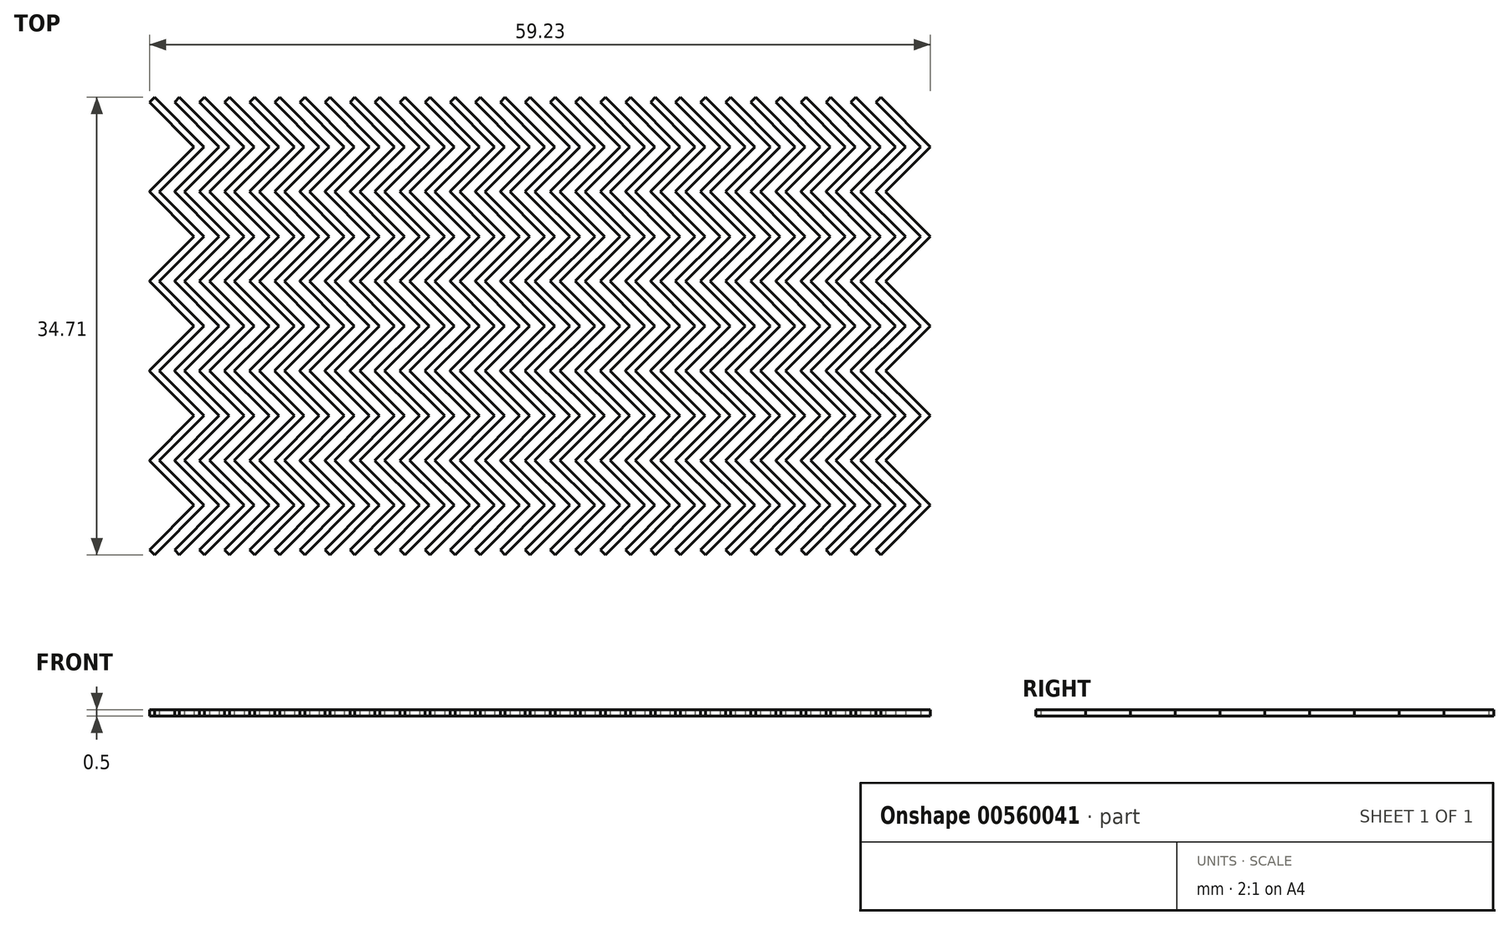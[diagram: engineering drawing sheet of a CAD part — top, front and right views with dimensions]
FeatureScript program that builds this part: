
annotation { "Feature Type Name" : "Feature", "Feature Type Description" : "" }
export const myFeature = defineFeature(function(context is Context, id is Id, definition is map)
    precondition{}
    {
        {
            var Q0;
            Q0=qCreatedBy(makeId("Top.planeOp"),FACE);
            var sketch = newSketch(context, id + "F0", { "sketchPlane" : qUnion([Q0])});
            skLineSegment(sketch, "E0.bottom", {"start": v(-22.51, 20.26) * mm, "end": v(-22.89, 19.88) * mm});
            skLineSegment(sketch, "E0.top", {"start": v(-26.27, 24.01) * mm, "end": v(-26.64, 23.64) * mm});
            skLineSegment(sketch, "E0.left", {"start": v(-22.51, 20.26) * mm, "end": v(-26.27, 24.01) * mm});
            skLineSegment(sketch, "E0.right", {"start": v(-22.89, 19.88) * mm, "end": v(-26.64, 23.64) * mm});
            skPoint(sketch, "E0.middle", {"position": v(-24.58, 21.95) * mm});
            skLineSegment(sketch, "E1.bottom", {"start": v(-22.89, 20.63) * mm, "end": v(-22.51, 20.26) * mm});
            skLineSegment(sketch, "E1.top", {"start": v(-26.64, 16.88) * mm, "end": v(-26.27, 16.5) * mm});
            skLineSegment(sketch, "E1.left", {"start": v(-22.89, 20.63) * mm, "end": v(-26.64, 16.88) * mm});
            skLineSegment(sketch, "E1.right", {"start": v(-22.51, 20.26) * mm, "end": v(-26.27, 16.5) * mm});
            skPoint(sketch, "E1.middle", {"position": v(-24.58, 18.57) * mm});
            skLineSegment(sketch, "E2.1.0.0", {"start": v(-20.61, 20.26) * mm, "end": v(-24.37, 24.01) * mm});
            skLineSegment(sketch, "E2.1.0.1", {"start": v(-20.99, 19.88) * mm, "end": v(-24.74, 23.64) * mm});
            skPoint(sketch, "E2.1.0.2", {"position": v(-22.68, 18.57) * mm});
            skLineSegment(sketch, "E2.1.0.3", {"start": v(-20.99, 20.63) * mm, "end": v(-24.74, 16.88) * mm});
            skPoint(sketch, "E2.1.0.4", {"position": v(-22.68, 21.95) * mm});
            skLineSegment(sketch, "E2.1.0.5", {"start": v(-20.61, 20.26) * mm, "end": v(-24.37, 16.5) * mm});
            skLineSegment(sketch, "E2.1.0.6", {"start": v(-24.37, 24.01) * mm, "end": v(-24.74, 23.64) * mm});
            skLineSegment(sketch, "E2.1.0.7", {"start": v(-24.74, 16.88) * mm, "end": v(-24.37, 16.5) * mm});
            skLineSegment(sketch, "E2.1.0.8", {"start": v(-20.61, 20.26) * mm, "end": v(-20.99, 19.88) * mm});
            skLineSegment(sketch, "E2.1.0.9", {"start": v(-20.99, 20.63) * mm, "end": v(-20.61, 20.26) * mm});
            skLineSegment(sketch, "E2.2.0.0", {"start": v(-18.71, 20.26) * mm, "end": v(-22.47, 24.01) * mm});
            skLineSegment(sketch, "E2.2.0.1", {"start": v(-19.09, 19.88) * mm, "end": v(-22.84, 23.64) * mm});
            skPoint(sketch, "E2.2.0.2", {"position": v(-20.78, 18.57) * mm});
            skLineSegment(sketch, "E2.2.0.3", {"start": v(-19.09, 20.63) * mm, "end": v(-22.84, 16.88) * mm});
            skPoint(sketch, "E2.2.0.4", {"position": v(-20.78, 21.95) * mm});
            skLineSegment(sketch, "E2.2.0.5", {"start": v(-18.71, 20.26) * mm, "end": v(-22.47, 16.5) * mm});
            skLineSegment(sketch, "E2.2.0.6", {"start": v(-22.47, 24.01) * mm, "end": v(-22.84, 23.64) * mm});
            skLineSegment(sketch, "E2.2.0.7", {"start": v(-22.84, 16.88) * mm, "end": v(-22.47, 16.5) * mm});
            skLineSegment(sketch, "E2.2.0.8", {"start": v(-18.71, 20.26) * mm, "end": v(-19.09, 19.88) * mm});
            skLineSegment(sketch, "E2.2.0.9", {"start": v(-19.09, 20.63) * mm, "end": v(-18.71, 20.26) * mm});
            skLineSegment(sketch, "E2.3.0.0", {"start": v(-16.81, 20.26) * mm, "end": v(-20.57, 24.01) * mm});
            skLineSegment(sketch, "E2.3.0.1", {"start": v(-17.19, 19.88) * mm, "end": v(-20.94, 23.64) * mm});
            skPoint(sketch, "E2.3.0.2", {"position": v(-18.88, 18.57) * mm});
            skLineSegment(sketch, "E2.3.0.3", {"start": v(-17.19, 20.63) * mm, "end": v(-20.94, 16.88) * mm});
            skPoint(sketch, "E2.3.0.4", {"position": v(-18.88, 21.95) * mm});
            skLineSegment(sketch, "E2.3.0.5", {"start": v(-16.81, 20.26) * mm, "end": v(-20.57, 16.5) * mm});
            skLineSegment(sketch, "E2.3.0.6", {"start": v(-20.57, 24.01) * mm, "end": v(-20.94, 23.64) * mm});
            skLineSegment(sketch, "E2.3.0.7", {"start": v(-20.94, 16.88) * mm, "end": v(-20.57, 16.5) * mm});
            skLineSegment(sketch, "E2.3.0.8", {"start": v(-16.81, 20.26) * mm, "end": v(-17.19, 19.88) * mm});
            skLineSegment(sketch, "E2.3.0.9", {"start": v(-17.19, 20.63) * mm, "end": v(-16.81, 20.26) * mm});
            skLineSegment(sketch, "E2.4.0.0", {"start": v(-14.91, 20.26) * mm, "end": v(-18.67, 24.01) * mm});
            skLineSegment(sketch, "E2.4.0.1", {"start": v(-15.29, 19.88) * mm, "end": v(-19.04, 23.64) * mm});
            skPoint(sketch, "E2.4.0.2", {"position": v(-16.98, 18.57) * mm});
            skLineSegment(sketch, "E2.4.0.3", {"start": v(-15.29, 20.63) * mm, "end": v(-19.04, 16.88) * mm});
            skPoint(sketch, "E2.4.0.4", {"position": v(-16.98, 21.95) * mm});
            skLineSegment(sketch, "E2.4.0.5", {"start": v(-14.91, 20.26) * mm, "end": v(-18.67, 16.5) * mm});
            skLineSegment(sketch, "E2.4.0.6", {"start": v(-18.67, 24.01) * mm, "end": v(-19.04, 23.64) * mm});
            skLineSegment(sketch, "E2.4.0.7", {"start": v(-19.04, 16.88) * mm, "end": v(-18.67, 16.5) * mm});
            skLineSegment(sketch, "E2.4.0.8", {"start": v(-14.91, 20.26) * mm, "end": v(-15.29, 19.88) * mm});
            skLineSegment(sketch, "E2.4.0.9", {"start": v(-15.29, 20.63) * mm, "end": v(-14.91, 20.26) * mm});
            skLineSegment(sketch, "E2.5.0.0", {"start": v(-13.01, 20.26) * mm, "end": v(-16.77, 24.01) * mm});
            skLineSegment(sketch, "E2.5.0.1", {"start": v(-13.39, 19.88) * mm, "end": v(-17.14, 23.64) * mm});
            skPoint(sketch, "E2.5.0.2", {"position": v(-15.08, 18.57) * mm});
            skLineSegment(sketch, "E2.5.0.3", {"start": v(-13.39, 20.63) * mm, "end": v(-17.14, 16.88) * mm});
            skPoint(sketch, "E2.5.0.4", {"position": v(-15.08, 21.95) * mm});
            skLineSegment(sketch, "E2.5.0.5", {"start": v(-13.01, 20.26) * mm, "end": v(-16.77, 16.5) * mm});
            skLineSegment(sketch, "E2.5.0.6", {"start": v(-16.77, 24.01) * mm, "end": v(-17.14, 23.64) * mm});
            skLineSegment(sketch, "E2.5.0.7", {"start": v(-17.14, 16.88) * mm, "end": v(-16.77, 16.5) * mm});
            skLineSegment(sketch, "E2.5.0.8", {"start": v(-13.01, 20.26) * mm, "end": v(-13.39, 19.88) * mm});
            skLineSegment(sketch, "E2.5.0.9", {"start": v(-13.39, 20.63) * mm, "end": v(-13.01, 20.26) * mm});
            skLineSegment(sketch, "E2.6.0.0", {"start": v(-11.11, 20.26) * mm, "end": v(-14.87, 24.01) * mm});
            skLineSegment(sketch, "E2.6.0.1", {"start": v(-11.49, 19.88) * mm, "end": v(-15.24, 23.64) * mm});
            skPoint(sketch, "E2.6.0.2", {"position": v(-13.18, 18.57) * mm});
            skLineSegment(sketch, "E2.6.0.3", {"start": v(-11.49, 20.63) * mm, "end": v(-15.24, 16.88) * mm});
            skPoint(sketch, "E2.6.0.4", {"position": v(-13.18, 21.95) * mm});
            skLineSegment(sketch, "E2.6.0.5", {"start": v(-11.11, 20.26) * mm, "end": v(-14.87, 16.5) * mm});
            skLineSegment(sketch, "E2.6.0.6", {"start": v(-14.87, 24.01) * mm, "end": v(-15.24, 23.64) * mm});
            skLineSegment(sketch, "E2.6.0.7", {"start": v(-15.24, 16.88) * mm, "end": v(-14.87, 16.5) * mm});
            skLineSegment(sketch, "E2.6.0.8", {"start": v(-11.11, 20.26) * mm, "end": v(-11.49, 19.88) * mm});
            skLineSegment(sketch, "E2.6.0.9", {"start": v(-11.49, 20.63) * mm, "end": v(-11.11, 20.26) * mm});
            skLineSegment(sketch, "E2.7.0.0", {"start": v(-9.21, 20.26) * mm, "end": v(-12.97, 24.01) * mm});
            skLineSegment(sketch, "E2.7.0.1", {"start": v(-9.59, 19.88) * mm, "end": v(-13.34, 23.64) * mm});
            skPoint(sketch, "E2.7.0.2", {"position": v(-11.28, 18.57) * mm});
            skLineSegment(sketch, "E2.7.0.3", {"start": v(-9.59, 20.63) * mm, "end": v(-13.34, 16.88) * mm});
            skPoint(sketch, "E2.7.0.4", {"position": v(-11.28, 21.95) * mm});
            skLineSegment(sketch, "E2.7.0.5", {"start": v(-9.21, 20.26) * mm, "end": v(-12.97, 16.5) * mm});
            skLineSegment(sketch, "E2.7.0.6", {"start": v(-12.97, 24.01) * mm, "end": v(-13.34, 23.64) * mm});
            skLineSegment(sketch, "E2.7.0.7", {"start": v(-13.34, 16.88) * mm, "end": v(-12.97, 16.5) * mm});
            skLineSegment(sketch, "E2.7.0.8", {"start": v(-9.21, 20.26) * mm, "end": v(-9.59, 19.88) * mm});
            skLineSegment(sketch, "E2.7.0.9", {"start": v(-9.59, 20.63) * mm, "end": v(-9.21, 20.26) * mm});
            skLineSegment(sketch, "E2.8.0.0", {"start": v(-7.31, 20.26) * mm, "end": v(-11.07, 24.01) * mm});
            skLineSegment(sketch, "E2.8.0.1", {"start": v(-7.69, 19.88) * mm, "end": v(-11.44, 23.64) * mm});
            skPoint(sketch, "E2.8.0.2", {"position": v(-9.38, 18.57) * mm});
            skLineSegment(sketch, "E2.8.0.3", {"start": v(-7.69, 20.63) * mm, "end": v(-11.44, 16.88) * mm});
            skPoint(sketch, "E2.8.0.4", {"position": v(-9.38, 21.95) * mm});
            skLineSegment(sketch, "E2.8.0.5", {"start": v(-7.31, 20.26) * mm, "end": v(-11.07, 16.5) * mm});
            skLineSegment(sketch, "E2.8.0.6", {"start": v(-11.07, 24.01) * mm, "end": v(-11.44, 23.64) * mm});
            skLineSegment(sketch, "E2.8.0.7", {"start": v(-11.44, 16.88) * mm, "end": v(-11.07, 16.5) * mm});
            skLineSegment(sketch, "E2.8.0.8", {"start": v(-7.31, 20.26) * mm, "end": v(-7.69, 19.88) * mm});
            skLineSegment(sketch, "E2.8.0.9", {"start": v(-7.69, 20.63) * mm, "end": v(-7.31, 20.26) * mm});
            skLineSegment(sketch, "E2.9.0.0", {"start": v(-5.41, 20.26) * mm, "end": v(-9.17, 24.01) * mm});
            skLineSegment(sketch, "E2.9.0.1", {"start": v(-5.79, 19.88) * mm, "end": v(-9.54, 23.64) * mm});
            skPoint(sketch, "E2.9.0.2", {"position": v(-7.48, 18.57) * mm});
            skLineSegment(sketch, "E2.9.0.3", {"start": v(-5.79, 20.63) * mm, "end": v(-9.54, 16.88) * mm});
            skPoint(sketch, "E2.9.0.4", {"position": v(-7.48, 21.95) * mm});
            skLineSegment(sketch, "E2.9.0.5", {"start": v(-5.41, 20.26) * mm, "end": v(-9.17, 16.5) * mm});
            skLineSegment(sketch, "E2.9.0.6", {"start": v(-9.17, 24.01) * mm, "end": v(-9.54, 23.64) * mm});
            skLineSegment(sketch, "E2.9.0.7", {"start": v(-9.54, 16.88) * mm, "end": v(-9.17, 16.5) * mm});
            skLineSegment(sketch, "E2.9.0.8", {"start": v(-5.41, 20.26) * mm, "end": v(-5.79, 19.88) * mm});
            skLineSegment(sketch, "E2.9.0.9", {"start": v(-5.79, 20.63) * mm, "end": v(-5.41, 20.26) * mm});
            skLineSegment(sketch, "E2.10.0.0", {"start": v(-3.51, 20.26) * mm, "end": v(-7.27, 24.01) * mm});
            skLineSegment(sketch, "E2.10.0.1", {"start": v(-3.89, 19.88) * mm, "end": v(-7.64, 23.64) * mm});
            skPoint(sketch, "E2.10.0.2", {"position": v(-5.58, 18.57) * mm});
            skLineSegment(sketch, "E2.10.0.3", {"start": v(-3.89, 20.63) * mm, "end": v(-7.64, 16.88) * mm});
            skPoint(sketch, "E2.10.0.4", {"position": v(-5.58, 21.95) * mm});
            skLineSegment(sketch, "E2.10.0.5", {"start": v(-3.51, 20.26) * mm, "end": v(-7.27, 16.5) * mm});
            skLineSegment(sketch, "E2.10.0.6", {"start": v(-7.27, 24.01) * mm, "end": v(-7.64, 23.64) * mm});
            skLineSegment(sketch, "E2.10.0.7", {"start": v(-7.64, 16.88) * mm, "end": v(-7.27, 16.5) * mm});
            skLineSegment(sketch, "E2.10.0.8", {"start": v(-3.51, 20.26) * mm, "end": v(-3.89, 19.88) * mm});
            skLineSegment(sketch, "E2.10.0.9", {"start": v(-3.89, 20.63) * mm, "end": v(-3.51, 20.26) * mm});
            skLineSegment(sketch, "E2.11.0.0", {"start": v(-1.61, 20.26) * mm, "end": v(-5.37, 24.01) * mm});
            skLineSegment(sketch, "E2.11.0.1", {"start": v(-1.99, 19.88) * mm, "end": v(-5.74, 23.64) * mm});
            skPoint(sketch, "E2.11.0.2", {"position": v(-3.68, 18.57) * mm});
            skLineSegment(sketch, "E2.11.0.3", {"start": v(-1.99, 20.63) * mm, "end": v(-5.74, 16.88) * mm});
            skPoint(sketch, "E2.11.0.4", {"position": v(-3.68, 21.95) * mm});
            skLineSegment(sketch, "E2.11.0.5", {"start": v(-1.61, 20.26) * mm, "end": v(-5.37, 16.5) * mm});
            skLineSegment(sketch, "E2.11.0.6", {"start": v(-5.37, 24.01) * mm, "end": v(-5.74, 23.64) * mm});
            skLineSegment(sketch, "E2.11.0.7", {"start": v(-5.74, 16.88) * mm, "end": v(-5.37, 16.5) * mm});
            skLineSegment(sketch, "E2.11.0.8", {"start": v(-1.61, 20.26) * mm, "end": v(-1.99, 19.88) * mm});
            skLineSegment(sketch, "E2.11.0.9", {"start": v(-1.99, 20.63) * mm, "end": v(-1.61, 20.26) * mm});
            skLineSegment(sketch, "E2.12.0.0", {"start": v(0.29, 20.26) * mm, "end": v(-3.47, 24.01) * mm});
            skLineSegment(sketch, "E2.12.0.1", {"start": v(-0.09, 19.88) * mm, "end": v(-3.84, 23.64) * mm});
            skPoint(sketch, "E2.12.0.2", {"position": v(-1.78, 18.57) * mm});
            skLineSegment(sketch, "E2.12.0.3", {"start": v(-0.09, 20.63) * mm, "end": v(-3.84, 16.88) * mm});
            skPoint(sketch, "E2.12.0.4", {"position": v(-1.78, 21.95) * mm});
            skLineSegment(sketch, "E2.12.0.5", {"start": v(0.29, 20.26) * mm, "end": v(-3.47, 16.5) * mm});
            skLineSegment(sketch, "E2.12.0.6", {"start": v(-3.47, 24.01) * mm, "end": v(-3.84, 23.64) * mm});
            skLineSegment(sketch, "E2.12.0.7", {"start": v(-3.84, 16.88) * mm, "end": v(-3.47, 16.5) * mm});
            skLineSegment(sketch, "E2.12.0.8", {"start": v(0.29, 20.26) * mm, "end": v(-0.09, 19.88) * mm});
            skLineSegment(sketch, "E2.12.0.9", {"start": v(-0.09, 20.63) * mm, "end": v(0.29, 20.26) * mm});
            skLineSegment(sketch, "E2.13.0.0", {"start": v(2.19, 20.26) * mm, "end": v(-1.57, 24.01) * mm});
            skLineSegment(sketch, "E2.13.0.1", {"start": v(1.81, 19.88) * mm, "end": v(-1.94, 23.64) * mm});
            skPoint(sketch, "E2.13.0.2", {"position": v(0.12, 18.57) * mm});
            skLineSegment(sketch, "E2.13.0.3", {"start": v(1.81, 20.63) * mm, "end": v(-1.94, 16.88) * mm});
            skPoint(sketch, "E2.13.0.4", {"position": v(0.12, 21.95) * mm});
            skLineSegment(sketch, "E2.13.0.5", {"start": v(2.19, 20.26) * mm, "end": v(-1.57, 16.5) * mm});
            skLineSegment(sketch, "E2.13.0.6", {"start": v(-1.57, 24.01) * mm, "end": v(-1.94, 23.64) * mm});
            skLineSegment(sketch, "E2.13.0.7", {"start": v(-1.94, 16.88) * mm, "end": v(-1.57, 16.5) * mm});
            skLineSegment(sketch, "E2.13.0.8", {"start": v(2.19, 20.26) * mm, "end": v(1.81, 19.88) * mm});
            skLineSegment(sketch, "E2.13.0.9", {"start": v(1.81, 20.63) * mm, "end": v(2.19, 20.26) * mm});
            skLineSegment(sketch, "E2.14.0.0", {"start": v(4.09, 20.26) * mm, "end": v(0.33, 24.01) * mm});
            skLineSegment(sketch, "E2.14.0.1", {"start": v(3.71, 19.88) * mm, "end": v(-0.04, 23.64) * mm});
            skPoint(sketch, "E2.14.0.2", {"position": v(2.02, 18.57) * mm});
            skLineSegment(sketch, "E2.14.0.3", {"start": v(3.71, 20.63) * mm, "end": v(-0.04, 16.88) * mm});
            skPoint(sketch, "E2.14.0.4", {"position": v(2.02, 21.95) * mm});
            skLineSegment(sketch, "E2.14.0.5", {"start": v(4.09, 20.26) * mm, "end": v(0.33, 16.5) * mm});
            skLineSegment(sketch, "E2.14.0.6", {"start": v(0.33, 24.01) * mm, "end": v(-0.04, 23.64) * mm});
            skLineSegment(sketch, "E2.14.0.7", {"start": v(-0.04, 16.88) * mm, "end": v(0.33, 16.5) * mm});
            skLineSegment(sketch, "E2.14.0.8", {"start": v(4.09, 20.26) * mm, "end": v(3.71, 19.88) * mm});
            skLineSegment(sketch, "E2.14.0.9", {"start": v(3.71, 20.63) * mm, "end": v(4.09, 20.26) * mm});
            skLineSegment(sketch, "E2.15.0.0", {"start": v(5.99, 20.26) * mm, "end": v(2.23, 24.01) * mm});
            skLineSegment(sketch, "E2.15.0.1", {"start": v(5.61, 19.88) * mm, "end": v(1.86, 23.64) * mm});
            skPoint(sketch, "E2.15.0.2", {"position": v(3.92, 18.57) * mm});
            skLineSegment(sketch, "E2.15.0.3", {"start": v(5.61, 20.63) * mm, "end": v(1.86, 16.88) * mm});
            skPoint(sketch, "E2.15.0.4", {"position": v(3.92, 21.95) * mm});
            skLineSegment(sketch, "E2.15.0.5", {"start": v(5.99, 20.26) * mm, "end": v(2.23, 16.5) * mm});
            skLineSegment(sketch, "E2.15.0.6", {"start": v(2.23, 24.01) * mm, "end": v(1.86, 23.64) * mm});
            skLineSegment(sketch, "E2.15.0.7", {"start": v(1.86, 16.88) * mm, "end": v(2.23, 16.5) * mm});
            skLineSegment(sketch, "E2.15.0.8", {"start": v(5.99, 20.26) * mm, "end": v(5.61, 19.88) * mm});
            skLineSegment(sketch, "E2.15.0.9", {"start": v(5.61, 20.63) * mm, "end": v(5.99, 20.26) * mm});
            skLineSegment(sketch, "E2.16.0.0", {"start": v(7.89, 20.26) * mm, "end": v(4.13, 24.01) * mm});
            skLineSegment(sketch, "E2.16.0.1", {"start": v(7.51, 19.88) * mm, "end": v(3.76, 23.64) * mm});
            skPoint(sketch, "E2.16.0.2", {"position": v(5.82, 18.57) * mm});
            skLineSegment(sketch, "E2.16.0.3", {"start": v(7.51, 20.63) * mm, "end": v(3.76, 16.88) * mm});
            skPoint(sketch, "E2.16.0.4", {"position": v(5.82, 21.95) * mm});
            skLineSegment(sketch, "E2.16.0.5", {"start": v(7.89, 20.26) * mm, "end": v(4.13, 16.5) * mm});
            skLineSegment(sketch, "E2.16.0.6", {"start": v(4.13, 24.01) * mm, "end": v(3.76, 23.64) * mm});
            skLineSegment(sketch, "E2.16.0.7", {"start": v(3.76, 16.88) * mm, "end": v(4.13, 16.5) * mm});
            skLineSegment(sketch, "E2.16.0.8", {"start": v(7.89, 20.26) * mm, "end": v(7.51, 19.88) * mm});
            skLineSegment(sketch, "E2.16.0.9", {"start": v(7.51, 20.63) * mm, "end": v(7.89, 20.26) * mm});
            skLineSegment(sketch, "E2.17.0.0", {"start": v(9.79, 20.26) * mm, "end": v(6.03, 24.01) * mm});
            skLineSegment(sketch, "E2.17.0.1", {"start": v(9.41, 19.88) * mm, "end": v(5.66, 23.64) * mm});
            skPoint(sketch, "E2.17.0.2", {"position": v(7.72, 18.57) * mm});
            skLineSegment(sketch, "E2.17.0.3", {"start": v(9.41, 20.63) * mm, "end": v(5.66, 16.88) * mm});
            skPoint(sketch, "E2.17.0.4", {"position": v(7.72, 21.95) * mm});
            skLineSegment(sketch, "E2.17.0.5", {"start": v(9.79, 20.26) * mm, "end": v(6.03, 16.5) * mm});
            skLineSegment(sketch, "E2.17.0.6", {"start": v(6.03, 24.01) * mm, "end": v(5.66, 23.64) * mm});
            skLineSegment(sketch, "E2.17.0.7", {"start": v(5.66, 16.88) * mm, "end": v(6.03, 16.5) * mm});
            skLineSegment(sketch, "E2.17.0.8", {"start": v(9.79, 20.26) * mm, "end": v(9.41, 19.88) * mm});
            skLineSegment(sketch, "E2.17.0.9", {"start": v(9.41, 20.63) * mm, "end": v(9.79, 20.26) * mm});
            skLineSegment(sketch, "E2.18.0.0", {"start": v(11.69, 20.26) * mm, "end": v(7.93, 24.01) * mm});
            skLineSegment(sketch, "E2.18.0.1", {"start": v(11.31, 19.88) * mm, "end": v(7.56, 23.64) * mm});
            skPoint(sketch, "E2.18.0.2", {"position": v(9.62, 18.57) * mm});
            skLineSegment(sketch, "E2.18.0.3", {"start": v(11.31, 20.63) * mm, "end": v(7.56, 16.88) * mm});
            skPoint(sketch, "E2.18.0.4", {"position": v(9.62, 21.95) * mm});
            skLineSegment(sketch, "E2.18.0.5", {"start": v(11.69, 20.26) * mm, "end": v(7.93, 16.5) * mm});
            skLineSegment(sketch, "E2.18.0.6", {"start": v(7.93, 24.01) * mm, "end": v(7.56, 23.64) * mm});
            skLineSegment(sketch, "E2.18.0.7", {"start": v(7.56, 16.88) * mm, "end": v(7.93, 16.5) * mm});
            skLineSegment(sketch, "E2.18.0.8", {"start": v(11.69, 20.26) * mm, "end": v(11.31, 19.88) * mm});
            skLineSegment(sketch, "E2.18.0.9", {"start": v(11.31, 20.63) * mm, "end": v(11.69, 20.26) * mm});
            skLineSegment(sketch, "E2.19.0.0", {"start": v(13.59, 20.26) * mm, "end": v(9.83, 24.01) * mm});
            skLineSegment(sketch, "E2.19.0.1", {"start": v(13.21, 19.88) * mm, "end": v(9.46, 23.64) * mm});
            skPoint(sketch, "E2.19.0.2", {"position": v(11.52, 18.57) * mm});
            skLineSegment(sketch, "E2.19.0.3", {"start": v(13.21, 20.63) * mm, "end": v(9.46, 16.88) * mm});
            skPoint(sketch, "E2.19.0.4", {"position": v(11.52, 21.95) * mm});
            skLineSegment(sketch, "E2.19.0.5", {"start": v(13.59, 20.26) * mm, "end": v(9.83, 16.5) * mm});
            skLineSegment(sketch, "E2.19.0.6", {"start": v(9.83, 24.01) * mm, "end": v(9.46, 23.64) * mm});
            skLineSegment(sketch, "E2.19.0.7", {"start": v(9.46, 16.88) * mm, "end": v(9.83, 16.5) * mm});
            skLineSegment(sketch, "E2.19.0.8", {"start": v(13.59, 20.26) * mm, "end": v(13.21, 19.88) * mm});
            skLineSegment(sketch, "E2.19.0.9", {"start": v(13.21, 20.63) * mm, "end": v(13.59, 20.26) * mm});
            skLineSegment(sketch, "E2.20.0.0", {"start": v(15.49, 20.26) * mm, "end": v(11.73, 24.01) * mm});
            skLineSegment(sketch, "E2.20.0.1", {"start": v(15.11, 19.88) * mm, "end": v(11.36, 23.64) * mm});
            skPoint(sketch, "E2.20.0.2", {"position": v(13.42, 18.57) * mm});
            skLineSegment(sketch, "E2.20.0.3", {"start": v(15.11, 20.63) * mm, "end": v(11.36, 16.88) * mm});
            skPoint(sketch, "E2.20.0.4", {"position": v(13.42, 21.95) * mm});
            skLineSegment(sketch, "E2.20.0.5", {"start": v(15.49, 20.26) * mm, "end": v(11.73, 16.5) * mm});
            skLineSegment(sketch, "E2.20.0.6", {"start": v(11.73, 24.01) * mm, "end": v(11.36, 23.64) * mm});
            skLineSegment(sketch, "E2.20.0.7", {"start": v(11.36, 16.88) * mm, "end": v(11.73, 16.5) * mm});
            skLineSegment(sketch, "E2.20.0.8", {"start": v(15.49, 20.26) * mm, "end": v(15.11, 19.88) * mm});
            skLineSegment(sketch, "E2.20.0.9", {"start": v(15.11, 20.63) * mm, "end": v(15.49, 20.26) * mm});
            skLineSegment(sketch, "E2.21.0.0", {"start": v(17.39, 20.26) * mm, "end": v(13.63, 24.01) * mm});
            skLineSegment(sketch, "E2.21.0.1", {"start": v(17.01, 19.88) * mm, "end": v(13.26, 23.64) * mm});
            skPoint(sketch, "E2.21.0.2", {"position": v(15.32, 18.57) * mm});
            skLineSegment(sketch, "E2.21.0.3", {"start": v(17.01, 20.63) * mm, "end": v(13.26, 16.88) * mm});
            skPoint(sketch, "E2.21.0.4", {"position": v(15.32, 21.95) * mm});
            skLineSegment(sketch, "E2.21.0.5", {"start": v(17.39, 20.26) * mm, "end": v(13.63, 16.5) * mm});
            skLineSegment(sketch, "E2.21.0.6", {"start": v(13.63, 24.01) * mm, "end": v(13.26, 23.64) * mm});
            skLineSegment(sketch, "E2.21.0.7", {"start": v(13.26, 16.88) * mm, "end": v(13.63, 16.5) * mm});
            skLineSegment(sketch, "E2.21.0.8", {"start": v(17.39, 20.26) * mm, "end": v(17.01, 19.88) * mm});
            skLineSegment(sketch, "E2.21.0.9", {"start": v(17.01, 20.63) * mm, "end": v(17.39, 20.26) * mm});
            skLineSegment(sketch, "E2.22.0.0", {"start": v(19.29, 20.26) * mm, "end": v(15.53, 24.01) * mm});
            skLineSegment(sketch, "E2.22.0.1", {"start": v(18.91, 19.88) * mm, "end": v(15.16, 23.64) * mm});
            skPoint(sketch, "E2.22.0.2", {"position": v(17.22, 18.57) * mm});
            skLineSegment(sketch, "E2.22.0.3", {"start": v(18.91, 20.63) * mm, "end": v(15.16, 16.88) * mm});
            skPoint(sketch, "E2.22.0.4", {"position": v(17.22, 21.95) * mm});
            skLineSegment(sketch, "E2.22.0.5", {"start": v(19.29, 20.26) * mm, "end": v(15.53, 16.5) * mm});
            skLineSegment(sketch, "E2.22.0.6", {"start": v(15.53, 24.01) * mm, "end": v(15.16, 23.64) * mm});
            skLineSegment(sketch, "E2.22.0.7", {"start": v(15.16, 16.88) * mm, "end": v(15.53, 16.5) * mm});
            skLineSegment(sketch, "E2.22.0.8", {"start": v(19.29, 20.26) * mm, "end": v(18.91, 19.88) * mm});
            skLineSegment(sketch, "E2.22.0.9", {"start": v(18.91, 20.63) * mm, "end": v(19.29, 20.26) * mm});
            skLineSegment(sketch, "E2.23.0.0", {"start": v(21.19, 20.26) * mm, "end": v(17.43, 24.01) * mm});
            skLineSegment(sketch, "E2.23.0.1", {"start": v(20.81, 19.88) * mm, "end": v(17.06, 23.64) * mm});
            skPoint(sketch, "E2.23.0.2", {"position": v(19.12, 18.57) * mm});
            skLineSegment(sketch, "E2.23.0.3", {"start": v(20.81, 20.63) * mm, "end": v(17.06, 16.88) * mm});
            skPoint(sketch, "E2.23.0.4", {"position": v(19.12, 21.95) * mm});
            skLineSegment(sketch, "E2.23.0.5", {"start": v(21.19, 20.26) * mm, "end": v(17.43, 16.5) * mm});
            skLineSegment(sketch, "E2.23.0.6", {"start": v(17.43, 24.01) * mm, "end": v(17.06, 23.64) * mm});
            skLineSegment(sketch, "E2.23.0.7", {"start": v(17.06, 16.88) * mm, "end": v(17.43, 16.5) * mm});
            skLineSegment(sketch, "E2.23.0.8", {"start": v(21.19, 20.26) * mm, "end": v(20.81, 19.88) * mm});
            skLineSegment(sketch, "E2.23.0.9", {"start": v(20.81, 20.63) * mm, "end": v(21.19, 20.26) * mm});
            skLineSegment(sketch, "E2.24.0.0", {"start": v(23.09, 20.26) * mm, "end": v(19.33, 24.01) * mm});
            skLineSegment(sketch, "E2.24.0.1", {"start": v(22.71, 19.88) * mm, "end": v(18.96, 23.64) * mm});
            skPoint(sketch, "E2.24.0.2", {"position": v(21.02, 18.57) * mm});
            skLineSegment(sketch, "E2.24.0.3", {"start": v(22.71, 20.63) * mm, "end": v(18.96, 16.88) * mm});
            skPoint(sketch, "E2.24.0.4", {"position": v(21.02, 21.95) * mm});
            skLineSegment(sketch, "E2.24.0.5", {"start": v(23.09, 20.26) * mm, "end": v(19.33, 16.5) * mm});
            skLineSegment(sketch, "E2.24.0.6", {"start": v(19.33, 24.01) * mm, "end": v(18.96, 23.64) * mm});
            skLineSegment(sketch, "E2.24.0.7", {"start": v(18.96, 16.88) * mm, "end": v(19.33, 16.5) * mm});
            skLineSegment(sketch, "E2.24.0.8", {"start": v(23.09, 20.26) * mm, "end": v(22.71, 19.88) * mm});
            skLineSegment(sketch, "E2.24.0.9", {"start": v(22.71, 20.63) * mm, "end": v(23.09, 20.26) * mm});
            skLineSegment(sketch, "E2.25.0.0", {"start": v(24.99, 20.26) * mm, "end": v(21.23, 24.01) * mm});
            skLineSegment(sketch, "E2.25.0.1", {"start": v(24.61, 19.88) * mm, "end": v(20.86, 23.64) * mm});
            skPoint(sketch, "E2.25.0.2", {"position": v(22.92, 18.57) * mm});
            skLineSegment(sketch, "E2.25.0.3", {"start": v(24.61, 20.63) * mm, "end": v(20.86, 16.88) * mm});
            skPoint(sketch, "E2.25.0.4", {"position": v(22.92, 21.95) * mm});
            skLineSegment(sketch, "E2.25.0.5", {"start": v(24.99, 20.26) * mm, "end": v(21.23, 16.5) * mm});
            skLineSegment(sketch, "E2.25.0.6", {"start": v(21.23, 24.01) * mm, "end": v(20.86, 23.64) * mm});
            skLineSegment(sketch, "E2.25.0.7", {"start": v(20.86, 16.88) * mm, "end": v(21.23, 16.5) * mm});
            skLineSegment(sketch, "E2.25.0.8", {"start": v(24.99, 20.26) * mm, "end": v(24.61, 19.88) * mm});
            skLineSegment(sketch, "E2.25.0.9", {"start": v(24.61, 20.63) * mm, "end": v(24.99, 20.26) * mm});
            skLineSegment(sketch, "E2.26.0.0", {"start": v(26.89, 20.26) * mm, "end": v(23.13, 24.01) * mm});
            skLineSegment(sketch, "E2.26.0.1", {"start": v(26.51, 19.88) * mm, "end": v(22.76, 23.64) * mm});
            skPoint(sketch, "E2.26.0.2", {"position": v(24.82, 18.57) * mm});
            skLineSegment(sketch, "E2.26.0.3", {"start": v(26.51, 20.63) * mm, "end": v(22.76, 16.88) * mm});
            skPoint(sketch, "E2.26.0.4", {"position": v(24.82, 21.95) * mm});
            skLineSegment(sketch, "E2.26.0.5", {"start": v(26.89, 20.26) * mm, "end": v(23.13, 16.5) * mm});
            skLineSegment(sketch, "E2.26.0.6", {"start": v(23.13, 24.01) * mm, "end": v(22.76, 23.64) * mm});
            skLineSegment(sketch, "E2.26.0.7", {"start": v(22.76, 16.88) * mm, "end": v(23.13, 16.5) * mm});
            skLineSegment(sketch, "E2.26.0.8", {"start": v(26.89, 20.26) * mm, "end": v(26.51, 19.88) * mm});
            skLineSegment(sketch, "E2.26.0.9", {"start": v(26.51, 20.63) * mm, "end": v(26.89, 20.26) * mm});
            skLineSegment(sketch, "E2.27.0.0", {"start": v(28.79, 20.26) * mm, "end": v(25.03, 24.01) * mm});
            skLineSegment(sketch, "E2.27.0.1", {"start": v(28.41, 19.88) * mm, "end": v(24.66, 23.64) * mm});
            skPoint(sketch, "E2.27.0.2", {"position": v(26.72, 18.57) * mm});
            skLineSegment(sketch, "E2.27.0.3", {"start": v(28.41, 20.63) * mm, "end": v(24.66, 16.88) * mm});
            skPoint(sketch, "E2.27.0.4", {"position": v(26.72, 21.95) * mm});
            skLineSegment(sketch, "E2.27.0.5", {"start": v(28.79, 20.26) * mm, "end": v(25.03, 16.5) * mm});
            skLineSegment(sketch, "E2.27.0.6", {"start": v(25.03, 24.01) * mm, "end": v(24.66, 23.64) * mm});
            skLineSegment(sketch, "E2.27.0.7", {"start": v(24.66, 16.88) * mm, "end": v(25.03, 16.5) * mm});
            skLineSegment(sketch, "E2.27.0.8", {"start": v(28.79, 20.26) * mm, "end": v(28.41, 19.88) * mm});
            skLineSegment(sketch, "E2.27.0.9", {"start": v(28.41, 20.63) * mm, "end": v(28.79, 20.26) * mm});
            skLineSegment(sketch, "E2.28.0.0", {"start": v(30.69, 20.26) * mm, "end": v(26.93, 24.01) * mm});
            skLineSegment(sketch, "E2.28.0.1", {"start": v(30.31, 19.88) * mm, "end": v(26.56, 23.64) * mm});
            skPoint(sketch, "E2.28.0.2", {"position": v(28.62, 18.57) * mm});
            skLineSegment(sketch, "E2.28.0.3", {"start": v(30.31, 20.63) * mm, "end": v(26.56, 16.88) * mm});
            skPoint(sketch, "E2.28.0.4", {"position": v(28.62, 21.95) * mm});
            skLineSegment(sketch, "E2.28.0.5", {"start": v(30.69, 20.26) * mm, "end": v(26.93, 16.5) * mm});
            skLineSegment(sketch, "E2.28.0.6", {"start": v(26.93, 24.01) * mm, "end": v(26.56, 23.64) * mm});
            skLineSegment(sketch, "E2.28.0.7", {"start": v(26.56, 16.88) * mm, "end": v(26.93, 16.5) * mm});
            skLineSegment(sketch, "E2.28.0.8", {"start": v(30.69, 20.26) * mm, "end": v(30.31, 19.88) * mm});
            skLineSegment(sketch, "E2.28.0.9", {"start": v(30.31, 20.63) * mm, "end": v(30.69, 20.26) * mm});
            skLineSegment(sketch, "E2.29.0.0", {"start": v(32.59, 20.26) * mm, "end": v(28.83, 24.01) * mm});
            skLineSegment(sketch, "E2.29.0.1", {"start": v(32.21, 19.88) * mm, "end": v(28.46, 23.64) * mm});
            skPoint(sketch, "E2.29.0.2", {"position": v(30.52, 18.57) * mm});
            skLineSegment(sketch, "E2.29.0.3", {"start": v(32.21, 20.63) * mm, "end": v(28.46, 16.88) * mm});
            skPoint(sketch, "E2.29.0.4", {"position": v(30.52, 21.95) * mm});
            skLineSegment(sketch, "E2.29.0.5", {"start": v(32.59, 20.26) * mm, "end": v(28.83, 16.5) * mm});
            skLineSegment(sketch, "E2.29.0.6", {"start": v(28.83, 24.01) * mm, "end": v(28.46, 23.64) * mm});
            skLineSegment(sketch, "E2.29.0.7", {"start": v(28.46, 16.88) * mm, "end": v(28.83, 16.5) * mm});
            skLineSegment(sketch, "E2.29.0.8", {"start": v(32.59, 20.26) * mm, "end": v(32.21, 19.88) * mm});
            skLineSegment(sketch, "E2.29.0.9", {"start": v(32.21, 20.63) * mm, "end": v(32.59, 20.26) * mm});
            skLineSegment(sketch, "E2.direction1", {"start": v(-26.27, 16.5) * mm, "end": v(-24.37, 16.5) * mm, "construction": true});
            skPoint(sketch, "E3.0.1.0", {"position": v(-22.68, 11.77) * mm});
            skPoint(sketch, "E3.0.1.1", {"position": v(-24.58, 11.77) * mm});
            skPoint(sketch, "E3.0.1.2", {"position": v(-24.58, 15.15) * mm});
            skPoint(sketch, "E3.0.1.3", {"position": v(30.52, 15.15) * mm});
            skPoint(sketch, "E3.0.1.4", {"position": v(-22.68, 15.15) * mm});
            skPoint(sketch, "E3.0.1.5", {"position": v(28.62, 15.15) * mm});
            skPoint(sketch, "E3.0.1.6", {"position": v(30.52, 11.77) * mm});
            skLineSegment(sketch, "E3.0.1.7", {"start": v(32.59, 13.46) * mm, "end": v(28.83, 17.21) * mm});
            skPoint(sketch, "E3.0.1.8", {"position": v(28.62, 11.77) * mm});
            skLineSegment(sketch, "E3.0.1.9", {"start": v(-22.89, 13.08) * mm, "end": v(-26.64, 16.84) * mm});
            skLineSegment(sketch, "E3.0.1.10", {"start": v(-22.89, 13.83) * mm, "end": v(-26.64, 10.08) * mm});
            skPoint(sketch, "E3.0.1.11", {"position": v(5.82, 11.77) * mm});
            skPoint(sketch, "E3.0.1.12", {"position": v(3.92, 11.77) * mm});
            skPoint(sketch, "E3.0.1.13", {"position": v(26.72, 11.77) * mm});
            skPoint(sketch, "E3.0.1.14", {"position": v(26.72, 15.15) * mm});
            skLineSegment(sketch, "E3.0.1.15", {"start": v(32.21, 13.08) * mm, "end": v(28.46, 16.84) * mm});
            skLineSegment(sketch, "E3.0.1.16", {"start": v(32.59, 13.46) * mm, "end": v(28.83, 9.7) * mm});
            skPoint(sketch, "E3.0.1.17", {"position": v(0.12, 11.77) * mm});
            skLineSegment(sketch, "E3.0.1.18", {"start": v(-22.51, 13.46) * mm, "end": v(-26.27, 17.21) * mm});
            skLineSegment(sketch, "E3.0.1.19", {"start": v(-22.51, 13.46) * mm, "end": v(-26.27, 9.7) * mm});
            skPoint(sketch, "E3.0.1.20", {"position": v(-7.48, 11.77) * mm});
            skPoint(sketch, "E3.0.1.21", {"position": v(7.72, 11.77) * mm});
            skPoint(sketch, "E3.0.1.22", {"position": v(22.92, 11.77) * mm});
            skLineSegment(sketch, "E3.0.1.23", {"start": v(30.69, 13.46) * mm, "end": v(26.93, 9.7) * mm});
            skPoint(sketch, "E3.0.1.24", {"position": v(-9.38, 15.15) * mm});
            skPoint(sketch, "E3.0.1.25", {"position": v(5.82, 15.15) * mm});
            skLineSegment(sketch, "E3.0.1.26", {"start": v(7.89, 13.46) * mm, "end": v(4.13, 9.7) * mm});
            skPoint(sketch, "E3.0.1.27", {"position": v(21.02, 15.15) * mm});
            skPoint(sketch, "E3.0.1.28", {"position": v(-9.38, 11.77) * mm});
            skPoint(sketch, "E3.0.1.29", {"position": v(21.02, 11.77) * mm});
            skPoint(sketch, "E3.0.1.30", {"position": v(-11.28, 15.15) * mm});
            skPoint(sketch, "E3.0.1.31", {"position": v(3.92, 15.15) * mm});
            skPoint(sketch, "E3.0.1.32", {"position": v(19.12, 15.15) * mm});
            skLineSegment(sketch, "E3.0.1.33", {"start": v(30.31, 13.08) * mm, "end": v(26.56, 16.84) * mm});
            skLineSegment(sketch, "E3.0.1.34", {"start": v(30.69, 13.46) * mm, "end": v(26.93, 17.21) * mm});
            skPoint(sketch, "E3.0.1.35", {"position": v(-11.28, 11.77) * mm});
            skPoint(sketch, "E3.0.1.36", {"position": v(19.12, 11.77) * mm});
            skPoint(sketch, "E3.0.1.37", {"position": v(-13.18, 15.15) * mm});
            skPoint(sketch, "E3.0.1.38", {"position": v(2.02, 15.15) * mm});
            skPoint(sketch, "E3.0.1.39", {"position": v(17.22, 15.15) * mm});
            skPoint(sketch, "E3.0.1.40", {"position": v(2.02, 11.77) * mm});
            skLineSegment(sketch, "E3.0.1.41", {"start": v(28.46, 10.08) * mm, "end": v(28.83, 9.7) * mm});
            skPoint(sketch, "E3.0.1.42", {"position": v(22.92, 15.15) * mm});
            skPoint(sketch, "E3.0.1.43", {"position": v(7.72, 15.15) * mm});
            skPoint(sketch, "E3.0.1.44", {"position": v(-7.48, 15.15) * mm});
            skPoint(sketch, "E3.0.1.45", {"position": v(24.82, 11.77) * mm});
            skPoint(sketch, "E3.0.1.46", {"position": v(9.62, 11.77) * mm});
            skPoint(sketch, "E3.0.1.47", {"position": v(-5.58, 11.77) * mm});
            skPoint(sketch, "E3.0.1.48", {"position": v(9.62, 15.15) * mm});
            skPoint(sketch, "E3.0.1.49", {"position": v(-5.58, 15.15) * mm});
            skPoint(sketch, "E3.0.1.50", {"position": v(-20.78, 15.15) * mm});
            skPoint(sketch, "E3.0.1.51", {"position": v(24.82, 15.15) * mm});
            skPoint(sketch, "E3.0.1.52", {"position": v(11.52, 11.77) * mm});
            skPoint(sketch, "E3.0.1.53", {"position": v(-3.68, 11.77) * mm});
            skPoint(sketch, "E3.0.1.54", {"position": v(-18.88, 11.77) * mm});
            skPoint(sketch, "E3.0.1.55", {"position": v(11.52, 15.15) * mm});
            skPoint(sketch, "E3.0.1.56", {"position": v(-3.68, 15.15) * mm});
            skPoint(sketch, "E3.0.1.57", {"position": v(-18.88, 15.15) * mm});
            skPoint(sketch, "E3.0.1.58", {"position": v(13.42, 11.77) * mm});
            skPoint(sketch, "E3.0.1.59", {"position": v(-1.78, 11.77) * mm});
            skPoint(sketch, "E3.0.1.60", {"position": v(-16.98, 11.77) * mm});
            skLineSegment(sketch, "E3.0.1.61", {"start": v(32.21, 13.83) * mm, "end": v(28.46, 10.08) * mm});
            skPoint(sketch, "E3.0.1.62", {"position": v(13.42, 15.15) * mm});
            skPoint(sketch, "E3.0.1.63", {"position": v(-1.78, 15.15) * mm});
            skPoint(sketch, "E3.0.1.64", {"position": v(-16.98, 15.15) * mm});
            skPoint(sketch, "E3.0.1.65", {"position": v(15.32, 11.77) * mm});
            skPoint(sketch, "E3.0.1.66", {"position": v(-15.08, 11.77) * mm});
            skLineSegment(sketch, "E3.0.1.67", {"start": v(28.83, 17.21) * mm, "end": v(28.46, 16.84) * mm});
            skLineSegment(sketch, "E3.0.1.68", {"start": v(-26.27, 17.21) * mm, "end": v(-26.64, 16.84) * mm});
            skLineSegment(sketch, "E3.0.1.69", {"start": v(-20.61, 13.46) * mm, "end": v(-24.37, 17.21) * mm});
            skLineSegment(sketch, "E3.0.1.70", {"start": v(-20.99, 13.08) * mm, "end": v(-24.74, 16.84) * mm});
            skLineSegment(sketch, "E3.0.1.71", {"start": v(-24.37, 17.21) * mm, "end": v(-24.74, 16.84) * mm});
            skLineSegment(sketch, "E3.0.1.72", {"start": v(19.33, 17.21) * mm, "end": v(18.96, 16.84) * mm});
            skLineSegment(sketch, "E3.0.1.73", {"start": v(23.13, 17.21) * mm, "end": v(22.76, 16.84) * mm});
            skLineSegment(sketch, "E3.0.1.74", {"start": v(-3.47, 17.21) * mm, "end": v(-3.84, 16.84) * mm});
            skLineSegment(sketch, "E3.0.1.75", {"start": v(4.13, 17.21) * mm, "end": v(3.76, 16.84) * mm});
            skLineSegment(sketch, "E3.0.1.76", {"start": v(7.93, 17.21) * mm, "end": v(7.56, 16.84) * mm});
            skLineSegment(sketch, "E3.0.1.77", {"start": v(-18.67, 17.21) * mm, "end": v(-19.04, 16.84) * mm});
            skLineSegment(sketch, "E3.0.1.78", {"start": v(-11.07, 17.21) * mm, "end": v(-11.44, 16.84) * mm});
            skLineSegment(sketch, "E3.0.1.79", {"start": v(-7.27, 17.21) * mm, "end": v(-7.64, 16.84) * mm});
            skLineSegment(sketch, "E3.0.1.80", {"start": v(-22.47, 17.21) * mm, "end": v(-22.84, 16.84) * mm});
            skLineSegment(sketch, "E3.0.1.81", {"start": v(15.49, 13.46) * mm, "end": v(11.73, 9.7) * mm});
            skLineSegment(sketch, "E3.0.1.82", {"start": v(23.09, 13.46) * mm, "end": v(19.33, 9.7) * mm});
            skLineSegment(sketch, "E3.0.1.83", {"start": v(26.89, 13.46) * mm, "end": v(23.13, 9.7) * mm});
            skLineSegment(sketch, "E3.0.1.84", {"start": v(0.29, 13.46) * mm, "end": v(-3.47, 9.7) * mm});
            skLineSegment(sketch, "E3.0.1.85", {"start": v(4.09, 13.46) * mm, "end": v(0.33, 9.7) * mm});
            skLineSegment(sketch, "E3.0.1.86", {"start": v(11.69, 13.46) * mm, "end": v(7.93, 9.7) * mm});
            skLineSegment(sketch, "E3.0.1.87", {"start": v(-14.91, 13.46) * mm, "end": v(-18.67, 9.7) * mm});
            skLineSegment(sketch, "E3.0.1.88", {"start": v(-7.31, 13.46) * mm, "end": v(-11.07, 9.7) * mm});
            skLineSegment(sketch, "E3.0.1.89", {"start": v(-3.51, 13.46) * mm, "end": v(-7.27, 9.7) * mm});
            skLineSegment(sketch, "E3.0.1.90", {"start": v(22.71, 13.83) * mm, "end": v(18.96, 10.08) * mm});
            skLineSegment(sketch, "E3.0.1.91", {"start": v(26.51, 13.83) * mm, "end": v(22.76, 10.08) * mm});
            skLineSegment(sketch, "E3.0.1.92", {"start": v(3.71, 13.83) * mm, "end": v(-0.04, 10.08) * mm});
            skLineSegment(sketch, "E3.0.1.93", {"start": v(7.51, 13.83) * mm, "end": v(3.76, 10.08) * mm});
            skLineSegment(sketch, "E3.0.1.94", {"start": v(30.31, 13.83) * mm, "end": v(26.56, 10.08) * mm});
            skLineSegment(sketch, "E3.0.1.95", {"start": v(-0.09, 13.08) * mm, "end": v(-3.84, 16.84) * mm});
            skLineSegment(sketch, "E3.0.1.96", {"start": v(7.51, 13.08) * mm, "end": v(3.76, 16.84) * mm});
            skLineSegment(sketch, "E3.0.1.97", {"start": v(11.31, 13.08) * mm, "end": v(7.56, 16.84) * mm});
            skLineSegment(sketch, "E3.0.1.98", {"start": v(-15.29, 13.08) * mm, "end": v(-19.04, 16.84) * mm});
            skLineSegment(sketch, "E3.0.1.99", {"start": v(-7.69, 13.08) * mm, "end": v(-11.44, 16.84) * mm});
            skLineSegment(sketch, "E3.0.1.100", {"start": v(-3.89, 13.08) * mm, "end": v(-7.64, 16.84) * mm});
            skLineSegment(sketch, "E3.0.1.101", {"start": v(-19.09, 13.08) * mm, "end": v(-22.84, 16.84) * mm});
            skLineSegment(sketch, "E3.0.1.102", {"start": v(15.11, 13.08) * mm, "end": v(11.36, 16.84) * mm});
            skLineSegment(sketch, "E3.0.1.103", {"start": v(22.71, 13.08) * mm, "end": v(18.96, 16.84) * mm});
            skLineSegment(sketch, "E3.0.1.104", {"start": v(26.51, 13.08) * mm, "end": v(22.76, 16.84) * mm});
            skLineSegment(sketch, "E3.0.1.105", {"start": v(-14.91, 13.46) * mm, "end": v(-18.67, 17.21) * mm});
            skLineSegment(sketch, "E3.0.1.106", {"start": v(26.93, 17.21) * mm, "end": v(26.56, 16.84) * mm});
            skLineSegment(sketch, "E3.0.1.107", {"start": v(-3.51, 13.46) * mm, "end": v(-7.27, 17.21) * mm});
            skLineSegment(sketch, "E3.0.1.108", {"start": v(-7.31, 13.46) * mm, "end": v(-11.07, 17.21) * mm});
            skLineSegment(sketch, "E3.0.1.109", {"start": v(-18.71, 13.46) * mm, "end": v(-22.47, 17.21) * mm});
            skLineSegment(sketch, "E3.0.1.110", {"start": v(-26.27, 9.7) * mm, "end": v(-24.37, 9.7) * mm, "construction": true});
            skLineSegment(sketch, "E3.0.1.111", {"start": v(15.49, 13.46) * mm, "end": v(11.73, 17.21) * mm});
            skLineSegment(sketch, "E3.0.1.112", {"start": v(23.09, 13.46) * mm, "end": v(19.33, 17.21) * mm});
            skLineSegment(sketch, "E3.0.1.113", {"start": v(0.29, 13.46) * mm, "end": v(-3.47, 17.21) * mm});
            skLineSegment(sketch, "E3.0.1.114", {"start": v(26.89, 13.46) * mm, "end": v(23.13, 17.21) * mm});
            skLineSegment(sketch, "E3.0.1.115", {"start": v(7.89, 13.46) * mm, "end": v(4.13, 17.21) * mm});
            skLineSegment(sketch, "E3.0.1.116", {"start": v(11.69, 13.46) * mm, "end": v(7.93, 17.21) * mm});
            skPoint(sketch, "E3.0.1.117", {"position": v(-13.18, 11.77) * mm});
            skPoint(sketch, "E3.0.1.118", {"position": v(17.22, 11.77) * mm});
            skPoint(sketch, "E3.0.1.119", {"position": v(-15.08, 15.15) * mm});
            skPoint(sketch, "E3.0.1.120", {"position": v(0.12, 15.15) * mm});
            skPoint(sketch, "E3.0.1.121", {"position": v(15.32, 15.15) * mm});
            skLineSegment(sketch, "E3.0.1.122", {"start": v(11.73, 17.21) * mm, "end": v(11.36, 16.84) * mm});
            skLineSegment(sketch, "E3.0.1.123", {"start": v(-7.64, 10.08) * mm, "end": v(-7.27, 9.7) * mm});
            skLineSegment(sketch, "E3.0.1.124", {"start": v(7.56, 10.08) * mm, "end": v(7.93, 9.7) * mm});
            skLineSegment(sketch, "E3.0.1.125", {"start": v(3.76, 10.08) * mm, "end": v(4.13, 9.7) * mm});
            skLineSegment(sketch, "E3.0.1.126", {"start": v(-0.04, 10.08) * mm, "end": v(0.33, 9.7) * mm});
            skLineSegment(sketch, "E3.0.1.127", {"start": v(-3.84, 10.08) * mm, "end": v(-3.47, 9.7) * mm});
            skLineSegment(sketch, "E3.0.1.128", {"start": v(22.76, 10.08) * mm, "end": v(23.13, 9.7) * mm});
            skLineSegment(sketch, "E3.0.1.129", {"start": v(11.36, 10.08) * mm, "end": v(11.73, 9.7) * mm});
            skLineSegment(sketch, "E3.0.1.130", {"start": v(26.56, 10.08) * mm, "end": v(26.93, 9.7) * mm});
            skPoint(sketch, "E3.0.1.131", {"position": v(-20.78, 11.77) * mm});
            skLineSegment(sketch, "E3.0.1.132", {"start": v(-9.21, 13.46) * mm, "end": v(-12.97, 17.21) * mm});
            skLineSegment(sketch, "E3.0.1.133", {"start": v(-16.81, 13.46) * mm, "end": v(-20.57, 17.21) * mm});
            skLineSegment(sketch, "E3.0.1.134", {"start": v(5.99, 13.46) * mm, "end": v(2.23, 17.21) * mm});
            skLineSegment(sketch, "E3.0.1.135", {"start": v(-1.61, 13.46) * mm, "end": v(-5.37, 17.21) * mm});
            skLineSegment(sketch, "E3.0.1.136", {"start": v(-5.41, 13.46) * mm, "end": v(-9.17, 17.21) * mm});
            skLineSegment(sketch, "E3.0.1.137", {"start": v(21.19, 13.46) * mm, "end": v(17.43, 17.21) * mm});
            skLineSegment(sketch, "E3.0.1.138", {"start": v(13.59, 13.46) * mm, "end": v(9.83, 17.21) * mm});
            skLineSegment(sketch, "E3.0.1.139", {"start": v(9.79, 13.46) * mm, "end": v(6.03, 17.21) * mm});
            skLineSegment(sketch, "E3.0.1.140", {"start": v(28.79, 13.46) * mm, "end": v(25.03, 17.21) * mm});
            skLineSegment(sketch, "E3.0.1.141", {"start": v(24.99, 13.46) * mm, "end": v(21.23, 17.21) * mm});
            skLineSegment(sketch, "E3.0.1.142", {"start": v(-9.59, 13.08) * mm, "end": v(-13.34, 16.84) * mm});
            skLineSegment(sketch, "E3.0.1.143", {"start": v(-17.19, 13.08) * mm, "end": v(-20.94, 16.84) * mm});
            skLineSegment(sketch, "E3.0.1.144", {"start": v(5.61, 13.08) * mm, "end": v(1.86, 16.84) * mm});
            skLineSegment(sketch, "E3.0.1.145", {"start": v(-1.99, 13.08) * mm, "end": v(-5.74, 16.84) * mm});
            skLineSegment(sketch, "E3.0.1.146", {"start": v(20.81, 13.08) * mm, "end": v(17.06, 16.84) * mm});
            skLineSegment(sketch, "E3.0.1.147", {"start": v(-5.79, 13.08) * mm, "end": v(-9.54, 16.84) * mm});
            skLineSegment(sketch, "E3.0.1.148", {"start": v(13.21, 13.08) * mm, "end": v(9.46, 16.84) * mm});
            skLineSegment(sketch, "E3.0.1.149", {"start": v(9.41, 13.08) * mm, "end": v(5.66, 16.84) * mm});
            skLineSegment(sketch, "E3.0.1.150", {"start": v(24.61, 13.08) * mm, "end": v(20.86, 16.84) * mm});
            skLineSegment(sketch, "E3.0.1.151", {"start": v(28.41, 13.08) * mm, "end": v(24.66, 16.84) * mm});
            skLineSegment(sketch, "E3.0.1.152", {"start": v(-13.39, 13.83) * mm, "end": v(-17.14, 10.08) * mm});
            skLineSegment(sketch, "E3.0.1.153", {"start": v(5.61, 13.83) * mm, "end": v(1.86, 10.08) * mm});
            skLineSegment(sketch, "E3.0.1.154", {"start": v(1.81, 13.83) * mm, "end": v(-1.94, 10.08) * mm});
            skLineSegment(sketch, "E3.0.1.155", {"start": v(-1.99, 13.83) * mm, "end": v(-5.74, 10.08) * mm});
            skLineSegment(sketch, "E3.0.1.156", {"start": v(-5.79, 13.83) * mm, "end": v(-9.54, 10.08) * mm});
            skLineSegment(sketch, "E3.0.1.157", {"start": v(17.01, 13.83) * mm, "end": v(13.26, 10.08) * mm});
            skLineSegment(sketch, "E3.0.1.158", {"start": v(13.21, 13.83) * mm, "end": v(9.46, 10.08) * mm});
            skLineSegment(sketch, "E3.0.1.159", {"start": v(9.41, 13.83) * mm, "end": v(5.66, 10.08) * mm});
            skLineSegment(sketch, "E3.0.1.160", {"start": v(24.61, 13.83) * mm, "end": v(20.86, 10.08) * mm});
            skLineSegment(sketch, "E3.0.1.161", {"start": v(28.41, 13.83) * mm, "end": v(24.66, 10.08) * mm});
            skLineSegment(sketch, "E3.0.1.162", {"start": v(-13.01, 13.46) * mm, "end": v(-16.77, 9.7) * mm});
            skLineSegment(sketch, "E3.0.1.163", {"start": v(5.99, 13.46) * mm, "end": v(2.23, 9.7) * mm});
            skLineSegment(sketch, "E3.0.1.164", {"start": v(2.19, 13.46) * mm, "end": v(-1.57, 9.7) * mm});
            skLineSegment(sketch, "E3.0.1.165", {"start": v(-1.61, 13.46) * mm, "end": v(-5.37, 9.7) * mm});
            skLineSegment(sketch, "E3.0.1.166", {"start": v(-5.41, 13.46) * mm, "end": v(-9.17, 9.7) * mm});
            skLineSegment(sketch, "E3.0.1.167", {"start": v(17.39, 13.46) * mm, "end": v(13.63, 9.7) * mm});
            skLineSegment(sketch, "E3.0.1.168", {"start": v(13.59, 13.46) * mm, "end": v(9.83, 9.7) * mm});
            skLineSegment(sketch, "E3.0.1.169", {"start": v(9.79, 13.46) * mm, "end": v(6.03, 9.7) * mm});
            skLineSegment(sketch, "E3.0.1.170", {"start": v(28.79, 13.46) * mm, "end": v(25.03, 9.7) * mm});
            skLineSegment(sketch, "E3.0.1.171", {"start": v(24.99, 13.46) * mm, "end": v(21.23, 9.7) * mm});
            skLineSegment(sketch, "E3.0.1.172", {"start": v(-20.57, 17.21) * mm, "end": v(-20.94, 16.84) * mm});
            skLineSegment(sketch, "E3.0.1.173", {"start": v(-5.37, 17.21) * mm, "end": v(-5.74, 16.84) * mm});
            skLineSegment(sketch, "E3.0.1.174", {"start": v(-9.17, 17.21) * mm, "end": v(-9.54, 16.84) * mm});
            skLineSegment(sketch, "E3.0.1.175", {"start": v(9.83, 17.21) * mm, "end": v(9.46, 16.84) * mm});
            skLineSegment(sketch, "E3.0.1.176", {"start": v(6.03, 17.21) * mm, "end": v(5.66, 16.84) * mm});
            skLineSegment(sketch, "E3.0.1.177", {"start": v(25.03, 17.21) * mm, "end": v(24.66, 16.84) * mm});
            skLineSegment(sketch, "E3.0.1.178", {"start": v(21.23, 17.21) * mm, "end": v(20.86, 16.84) * mm});
            skLineSegment(sketch, "E3.0.1.179", {"start": v(-22.89, 13.83) * mm, "end": v(-22.51, 13.46) * mm});
            skLineSegment(sketch, "E3.0.1.180", {"start": v(-20.99, 13.83) * mm, "end": v(-24.74, 10.08) * mm});
            skLineSegment(sketch, "E3.0.1.181", {"start": v(-20.61, 13.46) * mm, "end": v(-24.37, 9.7) * mm});
            skLineSegment(sketch, "E3.0.1.182", {"start": v(15.53, 17.21) * mm, "end": v(15.16, 16.84) * mm});
            skLineSegment(sketch, "E3.0.1.183", {"start": v(0.33, 17.21) * mm, "end": v(-0.04, 16.84) * mm});
            skLineSegment(sketch, "E3.0.1.184", {"start": v(-14.87, 17.21) * mm, "end": v(-15.24, 16.84) * mm});
            skLineSegment(sketch, "E3.0.1.185", {"start": v(19.29, 13.46) * mm, "end": v(15.53, 9.7) * mm});
            skLineSegment(sketch, "E3.0.1.186", {"start": v(-11.11, 13.46) * mm, "end": v(-14.87, 9.7) * mm});
            skLineSegment(sketch, "E3.0.1.187", {"start": v(-18.71, 13.46) * mm, "end": v(-22.47, 9.7) * mm});
            skLineSegment(sketch, "E3.0.1.188", {"start": v(15.11, 13.83) * mm, "end": v(11.36, 10.08) * mm});
            skLineSegment(sketch, "E3.0.1.189", {"start": v(18.91, 13.83) * mm, "end": v(15.16, 10.08) * mm});
            skLineSegment(sketch, "E3.0.1.190", {"start": v(-0.09, 13.83) * mm, "end": v(-3.84, 10.08) * mm});
            skLineSegment(sketch, "E3.0.1.191", {"start": v(11.31, 13.83) * mm, "end": v(7.56, 10.08) * mm});
            skLineSegment(sketch, "E3.0.1.192", {"start": v(-15.29, 13.83) * mm, "end": v(-19.04, 10.08) * mm});
            skLineSegment(sketch, "E3.0.1.193", {"start": v(-11.49, 13.83) * mm, "end": v(-15.24, 10.08) * mm});
            skLineSegment(sketch, "E3.0.1.194", {"start": v(-3.89, 13.83) * mm, "end": v(-7.64, 10.08) * mm});
            skLineSegment(sketch, "E3.0.1.195", {"start": v(-7.69, 13.83) * mm, "end": v(-11.44, 10.08) * mm});
            skLineSegment(sketch, "E3.0.1.196", {"start": v(-19.09, 13.83) * mm, "end": v(-22.84, 10.08) * mm});
            skLineSegment(sketch, "E3.0.1.197", {"start": v(3.71, 13.08) * mm, "end": v(-0.04, 16.84) * mm});
            skLineSegment(sketch, "E3.0.1.198", {"start": v(-11.49, 13.08) * mm, "end": v(-15.24, 16.84) * mm});
            skLineSegment(sketch, "E3.0.1.199", {"start": v(18.91, 13.08) * mm, "end": v(15.16, 16.84) * mm});
            skLineSegment(sketch, "E3.0.1.200", {"start": v(-11.11, 13.46) * mm, "end": v(-14.87, 17.21) * mm});
            skLineSegment(sketch, "E3.0.1.201", {"start": v(19.29, 13.46) * mm, "end": v(15.53, 17.21) * mm});
            skLineSegment(sketch, "E3.0.1.202", {"start": v(4.09, 13.46) * mm, "end": v(0.33, 17.21) * mm});
            skLineSegment(sketch, "E3.0.1.203", {"start": v(24.66, 10.08) * mm, "end": v(25.03, 9.7) * mm});
            skLineSegment(sketch, "E3.0.1.204", {"start": v(9.46, 10.08) * mm, "end": v(9.83, 9.7) * mm});
            skLineSegment(sketch, "E3.0.1.205", {"start": v(13.26, 10.08) * mm, "end": v(13.63, 9.7) * mm});
            skLineSegment(sketch, "E3.0.1.206", {"start": v(20.86, 10.08) * mm, "end": v(21.23, 9.7) * mm});
            skLineSegment(sketch, "E3.0.1.207", {"start": v(-5.74, 10.08) * mm, "end": v(-5.37, 9.7) * mm});
            skLineSegment(sketch, "E3.0.1.208", {"start": v(-1.94, 10.08) * mm, "end": v(-1.57, 9.7) * mm});
            skLineSegment(sketch, "E3.0.1.209", {"start": v(5.66, 10.08) * mm, "end": v(6.03, 9.7) * mm});
            skLineSegment(sketch, "E3.0.1.210", {"start": v(1.86, 10.08) * mm, "end": v(2.23, 9.7) * mm});
            skLineSegment(sketch, "E3.0.1.211", {"start": v(-17.14, 10.08) * mm, "end": v(-16.77, 9.7) * mm});
            skLineSegment(sketch, "E3.0.1.212", {"start": v(-9.54, 10.08) * mm, "end": v(-9.17, 9.7) * mm});
            skLineSegment(sketch, "E3.0.1.213", {"start": v(-22.84, 10.08) * mm, "end": v(-22.47, 9.7) * mm});
            skLineSegment(sketch, "E3.0.1.214", {"start": v(-11.44, 10.08) * mm, "end": v(-11.07, 9.7) * mm});
            skLineSegment(sketch, "E3.0.1.215", {"start": v(-15.24, 10.08) * mm, "end": v(-14.87, 9.7) * mm});
            skLineSegment(sketch, "E3.0.1.216", {"start": v(-19.04, 10.08) * mm, "end": v(-18.67, 9.7) * mm});
            skLineSegment(sketch, "E3.0.1.217", {"start": v(18.96, 10.08) * mm, "end": v(19.33, 9.7) * mm});
            skLineSegment(sketch, "E3.0.1.218", {"start": v(15.16, 10.08) * mm, "end": v(15.53, 9.7) * mm});
            skLineSegment(sketch, "E3.0.1.219", {"start": v(-13.01, 13.46) * mm, "end": v(-16.77, 17.21) * mm});
            skLineSegment(sketch, "E3.0.1.220", {"start": v(2.19, 13.46) * mm, "end": v(-1.57, 17.21) * mm});
            skLineSegment(sketch, "E3.0.1.221", {"start": v(17.39, 13.46) * mm, "end": v(13.63, 17.21) * mm});
            skLineSegment(sketch, "E3.0.1.222", {"start": v(-13.39, 13.08) * mm, "end": v(-17.14, 16.84) * mm});
            skLineSegment(sketch, "E3.0.1.223", {"start": v(1.81, 13.08) * mm, "end": v(-1.94, 16.84) * mm});
            skLineSegment(sketch, "E3.0.1.224", {"start": v(17.01, 13.08) * mm, "end": v(13.26, 16.84) * mm});
            skLineSegment(sketch, "E3.0.1.225", {"start": v(-9.59, 13.83) * mm, "end": v(-13.34, 10.08) * mm});
            skLineSegment(sketch, "E3.0.1.226", {"start": v(-17.19, 13.83) * mm, "end": v(-20.94, 10.08) * mm});
            skLineSegment(sketch, "E3.0.1.227", {"start": v(20.81, 13.83) * mm, "end": v(17.06, 10.08) * mm});
            skLineSegment(sketch, "E3.0.1.228", {"start": v(-9.21, 13.46) * mm, "end": v(-12.97, 9.7) * mm});
            skLineSegment(sketch, "E3.0.1.229", {"start": v(-16.81, 13.46) * mm, "end": v(-20.57, 9.7) * mm});
            skLineSegment(sketch, "E3.0.1.230", {"start": v(21.19, 13.46) * mm, "end": v(17.43, 9.7) * mm});
            skLineSegment(sketch, "E3.0.1.231", {"start": v(-12.97, 17.21) * mm, "end": v(-13.34, 16.84) * mm});
            skLineSegment(sketch, "E3.0.1.232", {"start": v(-16.77, 17.21) * mm, "end": v(-17.14, 16.84) * mm});
            skLineSegment(sketch, "E3.0.1.233", {"start": v(2.23, 17.21) * mm, "end": v(1.86, 16.84) * mm});
            skLineSegment(sketch, "E3.0.1.234", {"start": v(-1.57, 17.21) * mm, "end": v(-1.94, 16.84) * mm});
            skLineSegment(sketch, "E3.0.1.235", {"start": v(17.43, 17.21) * mm, "end": v(17.06, 16.84) * mm});
            skLineSegment(sketch, "E3.0.1.236", {"start": v(13.63, 17.21) * mm, "end": v(13.26, 16.84) * mm});
            skLineSegment(sketch, "E3.0.1.237", {"start": v(-24.74, 10.08) * mm, "end": v(-24.37, 9.7) * mm});
            skLineSegment(sketch, "E3.0.1.238", {"start": v(-22.51, 13.46) * mm, "end": v(-22.89, 13.08) * mm});
            skLineSegment(sketch, "E3.0.1.239", {"start": v(-26.64, 10.08) * mm, "end": v(-26.27, 9.7) * mm});
            skLineSegment(sketch, "E3.0.1.240", {"start": v(32.21, 13.83) * mm, "end": v(32.59, 13.46) * mm});
            skLineSegment(sketch, "E3.0.1.241", {"start": v(9.41, 13.83) * mm, "end": v(9.79, 13.46) * mm});
            skLineSegment(sketch, "E3.0.1.242", {"start": v(32.59, 13.46) * mm, "end": v(32.21, 13.08) * mm});
            skLineSegment(sketch, "E3.0.1.243", {"start": v(9.79, 13.46) * mm, "end": v(9.41, 13.08) * mm});
            skLineSegment(sketch, "E3.0.1.244", {"start": v(17.06, 10.08) * mm, "end": v(17.43, 9.7) * mm});
            skLineSegment(sketch, "E3.0.1.245", {"start": v(-20.94, 10.08) * mm, "end": v(-20.57, 9.7) * mm});
            skLineSegment(sketch, "E3.0.1.246", {"start": v(-13.34, 10.08) * mm, "end": v(-12.97, 9.7) * mm});
            skLineSegment(sketch, "E3.0.1.247", {"start": v(11.69, 13.46) * mm, "end": v(11.31, 13.08) * mm});
            skLineSegment(sketch, "E3.0.1.248", {"start": v(11.31, 13.83) * mm, "end": v(11.69, 13.46) * mm});
            skLineSegment(sketch, "E3.0.1.249", {"start": v(28.41, 13.83) * mm, "end": v(28.79, 13.46) * mm});
            skLineSegment(sketch, "E3.0.1.250", {"start": v(13.21, 13.83) * mm, "end": v(13.59, 13.46) * mm});
            skLineSegment(sketch, "E3.0.1.251", {"start": v(1.81, 13.83) * mm, "end": v(2.19, 13.46) * mm});
            skLineSegment(sketch, "E3.0.1.252", {"start": v(-13.39, 13.83) * mm, "end": v(-13.01, 13.46) * mm});
            skLineSegment(sketch, "E3.0.1.253", {"start": v(-5.79, 13.83) * mm, "end": v(-5.41, 13.46) * mm});
            skLineSegment(sketch, "E3.0.1.254", {"start": v(28.79, 13.46) * mm, "end": v(28.41, 13.08) * mm});
            skLineSegment(sketch, "E3.0.1.255", {"start": v(13.59, 13.46) * mm, "end": v(13.21, 13.08) * mm});
            skLineSegment(sketch, "E3.0.1.256", {"start": v(2.19, 13.46) * mm, "end": v(1.81, 13.08) * mm});
            skLineSegment(sketch, "E3.0.1.257", {"start": v(-13.01, 13.46) * mm, "end": v(-13.39, 13.08) * mm});
            skLineSegment(sketch, "E3.0.1.258", {"start": v(-5.41, 13.46) * mm, "end": v(-5.79, 13.08) * mm});
            skLineSegment(sketch, "E3.0.1.259", {"start": v(-7.31, 13.46) * mm, "end": v(-7.69, 13.08) * mm});
            skLineSegment(sketch, "E3.0.1.260", {"start": v(-11.11, 13.46) * mm, "end": v(-11.49, 13.08) * mm});
            skLineSegment(sketch, "E3.0.1.261", {"start": v(7.89, 13.46) * mm, "end": v(7.51, 13.08) * mm});
            skLineSegment(sketch, "E3.0.1.262", {"start": v(4.09, 13.46) * mm, "end": v(3.71, 13.08) * mm});
            skLineSegment(sketch, "E3.0.1.263", {"start": v(26.89, 13.46) * mm, "end": v(26.51, 13.08) * mm});
            skLineSegment(sketch, "E3.0.1.264", {"start": v(30.69, 13.46) * mm, "end": v(30.31, 13.08) * mm});
            skLineSegment(sketch, "E3.0.1.265", {"start": v(-11.49, 13.83) * mm, "end": v(-11.11, 13.46) * mm});
            skLineSegment(sketch, "E3.0.1.266", {"start": v(3.71, 13.83) * mm, "end": v(4.09, 13.46) * mm});
            skLineSegment(sketch, "E3.0.1.267", {"start": v(-7.69, 13.83) * mm, "end": v(-7.31, 13.46) * mm});
            skLineSegment(sketch, "E3.0.1.268", {"start": v(15.11, 13.83) * mm, "end": v(15.49, 13.46) * mm});
            skLineSegment(sketch, "E3.0.1.269", {"start": v(7.51, 13.83) * mm, "end": v(7.89, 13.46) * mm});
            skLineSegment(sketch, "E3.0.1.270", {"start": v(30.31, 13.83) * mm, "end": v(30.69, 13.46) * mm});
            skLineSegment(sketch, "E3.0.1.271", {"start": v(26.51, 13.83) * mm, "end": v(26.89, 13.46) * mm});
            skLineSegment(sketch, "E3.0.1.272", {"start": v(-20.61, 13.46) * mm, "end": v(-20.99, 13.08) * mm});
            skLineSegment(sketch, "E3.0.1.273", {"start": v(-20.99, 13.83) * mm, "end": v(-20.61, 13.46) * mm});
            skLineSegment(sketch, "E3.0.1.274", {"start": v(17.01, 13.83) * mm, "end": v(17.39, 13.46) * mm});
            skLineSegment(sketch, "E3.0.1.275", {"start": v(24.61, 13.83) * mm, "end": v(24.99, 13.46) * mm});
            skLineSegment(sketch, "E3.0.1.276", {"start": v(5.61, 13.83) * mm, "end": v(5.99, 13.46) * mm});
            skLineSegment(sketch, "E3.0.1.277", {"start": v(-17.19, 13.83) * mm, "end": v(-16.81, 13.46) * mm});
            skLineSegment(sketch, "E3.0.1.278", {"start": v(-9.59, 13.83) * mm, "end": v(-9.21, 13.46) * mm});
            skLineSegment(sketch, "E3.0.1.279", {"start": v(17.39, 13.46) * mm, "end": v(17.01, 13.08) * mm});
            skLineSegment(sketch, "E3.0.1.280", {"start": v(24.99, 13.46) * mm, "end": v(24.61, 13.08) * mm});
            skLineSegment(sketch, "E3.0.1.281", {"start": v(5.99, 13.46) * mm, "end": v(5.61, 13.08) * mm});
            skLineSegment(sketch, "E3.0.1.282", {"start": v(-16.81, 13.46) * mm, "end": v(-17.19, 13.08) * mm});
            skLineSegment(sketch, "E3.0.1.283", {"start": v(-9.21, 13.46) * mm, "end": v(-9.59, 13.08) * mm});
            skLineSegment(sketch, "E3.0.1.284", {"start": v(-18.71, 13.46) * mm, "end": v(-19.09, 13.08) * mm});
            skLineSegment(sketch, "E3.0.1.285", {"start": v(-14.91, 13.46) * mm, "end": v(-15.29, 13.08) * mm});
            skLineSegment(sketch, "E3.0.1.286", {"start": v(0.29, 13.46) * mm, "end": v(-0.09, 13.08) * mm});
            skLineSegment(sketch, "E3.0.1.287", {"start": v(23.09, 13.46) * mm, "end": v(22.71, 13.08) * mm});
            skLineSegment(sketch, "E3.0.1.288", {"start": v(15.49, 13.46) * mm, "end": v(15.11, 13.08) * mm});
            skLineSegment(sketch, "E3.0.1.289", {"start": v(-15.29, 13.83) * mm, "end": v(-14.91, 13.46) * mm});
            skLineSegment(sketch, "E3.0.1.290", {"start": v(-19.09, 13.83) * mm, "end": v(-18.71, 13.46) * mm});
            skLineSegment(sketch, "E3.0.1.291", {"start": v(-0.09, 13.83) * mm, "end": v(0.29, 13.46) * mm});
            skLineSegment(sketch, "E3.0.1.292", {"start": v(-3.89, 13.83) * mm, "end": v(-3.51, 13.46) * mm});
            skLineSegment(sketch, "E3.0.1.293", {"start": v(22.71, 13.83) * mm, "end": v(23.09, 13.46) * mm});
            skLineSegment(sketch, "E3.0.1.294", {"start": v(20.81, 13.83) * mm, "end": v(21.19, 13.46) * mm});
            skLineSegment(sketch, "E3.0.1.295", {"start": v(-1.99, 13.83) * mm, "end": v(-1.61, 13.46) * mm});
            skLineSegment(sketch, "E3.0.1.296", {"start": v(21.19, 13.46) * mm, "end": v(20.81, 13.08) * mm});
            skLineSegment(sketch, "E3.0.1.297", {"start": v(-1.61, 13.46) * mm, "end": v(-1.99, 13.08) * mm});
            skLineSegment(sketch, "E3.0.1.298", {"start": v(-3.51, 13.46) * mm, "end": v(-3.89, 13.08) * mm});
            skLineSegment(sketch, "E3.0.1.299", {"start": v(19.29, 13.46) * mm, "end": v(18.91, 13.08) * mm});
            skLineSegment(sketch, "E3.0.1.300", {"start": v(18.91, 13.83) * mm, "end": v(19.29, 13.46) * mm});
            skPoint(sketch, "E3.0.2.0", {"position": v(-22.68, 4.97) * mm});
            skPoint(sketch, "E3.0.2.1", {"position": v(-24.58, 4.97) * mm});
            skPoint(sketch, "E3.0.2.2", {"position": v(-24.58, 8.35) * mm});
            skPoint(sketch, "E3.0.2.3", {"position": v(30.52, 8.35) * mm});
            skPoint(sketch, "E3.0.2.4", {"position": v(-22.68, 8.35) * mm});
            skPoint(sketch, "E3.0.2.5", {"position": v(28.62, 8.35) * mm});
            skPoint(sketch, "E3.0.2.6", {"position": v(30.52, 4.97) * mm});
            skLineSegment(sketch, "E3.0.2.7", {"start": v(32.59, 6.66) * mm, "end": v(28.83, 10.41) * mm});
            skPoint(sketch, "E3.0.2.8", {"position": v(28.62, 4.97) * mm});
            skLineSegment(sketch, "E3.0.2.9", {"start": v(-22.89, 6.28) * mm, "end": v(-26.64, 10.04) * mm});
            skLineSegment(sketch, "E3.0.2.10", {"start": v(-22.89, 7.03) * mm, "end": v(-26.64, 3.28) * mm});
            skPoint(sketch, "E3.0.2.11", {"position": v(5.82, 4.97) * mm});
            skPoint(sketch, "E3.0.2.12", {"position": v(3.92, 4.97) * mm});
            skPoint(sketch, "E3.0.2.13", {"position": v(26.72, 4.97) * mm});
            skPoint(sketch, "E3.0.2.14", {"position": v(26.72, 8.35) * mm});
            skLineSegment(sketch, "E3.0.2.15", {"start": v(32.21, 6.28) * mm, "end": v(28.46, 10.04) * mm});
            skLineSegment(sketch, "E3.0.2.16", {"start": v(32.59, 6.66) * mm, "end": v(28.83, 2.9) * mm});
            skPoint(sketch, "E3.0.2.17", {"position": v(0.12, 4.97) * mm});
            skLineSegment(sketch, "E3.0.2.18", {"start": v(-22.51, 6.66) * mm, "end": v(-26.27, 10.41) * mm});
            skLineSegment(sketch, "E3.0.2.19", {"start": v(-22.51, 6.66) * mm, "end": v(-26.27, 2.9) * mm});
            skPoint(sketch, "E3.0.2.20", {"position": v(-7.48, 4.97) * mm});
            skPoint(sketch, "E3.0.2.21", {"position": v(7.72, 4.97) * mm});
            skPoint(sketch, "E3.0.2.22", {"position": v(22.92, 4.97) * mm});
            skLineSegment(sketch, "E3.0.2.23", {"start": v(30.69, 6.66) * mm, "end": v(26.93, 2.9) * mm});
            skPoint(sketch, "E3.0.2.24", {"position": v(-9.38, 8.35) * mm});
            skPoint(sketch, "E3.0.2.25", {"position": v(5.82, 8.35) * mm});
            skLineSegment(sketch, "E3.0.2.26", {"start": v(7.89, 6.66) * mm, "end": v(4.13, 2.9) * mm});
            skPoint(sketch, "E3.0.2.27", {"position": v(21.02, 8.35) * mm});
            skPoint(sketch, "E3.0.2.28", {"position": v(-9.38, 4.97) * mm});
            skPoint(sketch, "E3.0.2.29", {"position": v(21.02, 4.97) * mm});
            skPoint(sketch, "E3.0.2.30", {"position": v(-11.28, 8.35) * mm});
            skPoint(sketch, "E3.0.2.31", {"position": v(3.92, 8.35) * mm});
            skPoint(sketch, "E3.0.2.32", {"position": v(19.12, 8.35) * mm});
            skLineSegment(sketch, "E3.0.2.33", {"start": v(30.31, 6.28) * mm, "end": v(26.56, 10.04) * mm});
            skLineSegment(sketch, "E3.0.2.34", {"start": v(30.69, 6.66) * mm, "end": v(26.93, 10.41) * mm});
            skPoint(sketch, "E3.0.2.35", {"position": v(-11.28, 4.97) * mm});
            skPoint(sketch, "E3.0.2.36", {"position": v(19.12, 4.97) * mm});
            skPoint(sketch, "E3.0.2.37", {"position": v(-13.18, 8.35) * mm});
            skPoint(sketch, "E3.0.2.38", {"position": v(2.02, 8.35) * mm});
            skPoint(sketch, "E3.0.2.39", {"position": v(17.22, 8.35) * mm});
            skPoint(sketch, "E3.0.2.40", {"position": v(2.02, 4.97) * mm});
            skLineSegment(sketch, "E3.0.2.41", {"start": v(28.46, 3.28) * mm, "end": v(28.83, 2.9) * mm});
            skPoint(sketch, "E3.0.2.42", {"position": v(22.92, 8.35) * mm});
            skPoint(sketch, "E3.0.2.43", {"position": v(7.72, 8.35) * mm});
            skPoint(sketch, "E3.0.2.44", {"position": v(-7.48, 8.35) * mm});
            skPoint(sketch, "E3.0.2.45", {"position": v(24.82, 4.97) * mm});
            skPoint(sketch, "E3.0.2.46", {"position": v(9.62, 4.97) * mm});
            skPoint(sketch, "E3.0.2.47", {"position": v(-5.58, 4.97) * mm});
            skPoint(sketch, "E3.0.2.48", {"position": v(9.62, 8.35) * mm});
            skPoint(sketch, "E3.0.2.49", {"position": v(-5.58, 8.35) * mm});
            skPoint(sketch, "E3.0.2.50", {"position": v(-20.78, 8.35) * mm});
            skPoint(sketch, "E3.0.2.51", {"position": v(24.82, 8.35) * mm});
            skPoint(sketch, "E3.0.2.52", {"position": v(11.52, 4.97) * mm});
            skPoint(sketch, "E3.0.2.53", {"position": v(-3.68, 4.97) * mm});
            skPoint(sketch, "E3.0.2.54", {"position": v(-18.88, 4.97) * mm});
            skPoint(sketch, "E3.0.2.55", {"position": v(11.52, 8.35) * mm});
            skPoint(sketch, "E3.0.2.56", {"position": v(-3.68, 8.35) * mm});
            skPoint(sketch, "E3.0.2.57", {"position": v(-18.88, 8.35) * mm});
            skPoint(sketch, "E3.0.2.58", {"position": v(13.42, 4.97) * mm});
            skPoint(sketch, "E3.0.2.59", {"position": v(-1.78, 4.97) * mm});
            skPoint(sketch, "E3.0.2.60", {"position": v(-16.98, 4.97) * mm});
            skLineSegment(sketch, "E3.0.2.61", {"start": v(32.21, 7.03) * mm, "end": v(28.46, 3.28) * mm});
            skPoint(sketch, "E3.0.2.62", {"position": v(13.42, 8.35) * mm});
            skPoint(sketch, "E3.0.2.63", {"position": v(-1.78, 8.35) * mm});
            skPoint(sketch, "E3.0.2.64", {"position": v(-16.98, 8.35) * mm});
            skPoint(sketch, "E3.0.2.65", {"position": v(15.32, 4.97) * mm});
            skPoint(sketch, "E3.0.2.66", {"position": v(-15.08, 4.97) * mm});
            skLineSegment(sketch, "E3.0.2.67", {"start": v(28.83, 10.41) * mm, "end": v(28.46, 10.04) * mm});
            skLineSegment(sketch, "E3.0.2.68", {"start": v(-26.27, 10.41) * mm, "end": v(-26.64, 10.04) * mm});
            skLineSegment(sketch, "E3.0.2.69", {"start": v(-20.61, 6.66) * mm, "end": v(-24.37, 10.41) * mm});
            skLineSegment(sketch, "E3.0.2.70", {"start": v(-20.99, 6.28) * mm, "end": v(-24.74, 10.04) * mm});
            skLineSegment(sketch, "E3.0.2.71", {"start": v(-24.37, 10.41) * mm, "end": v(-24.74, 10.04) * mm});
            skLineSegment(sketch, "E3.0.2.72", {"start": v(19.33, 10.41) * mm, "end": v(18.96, 10.04) * mm});
            skLineSegment(sketch, "E3.0.2.73", {"start": v(23.13, 10.41) * mm, "end": v(22.76, 10.04) * mm});
            skLineSegment(sketch, "E3.0.2.74", {"start": v(-3.47, 10.41) * mm, "end": v(-3.84, 10.04) * mm});
            skLineSegment(sketch, "E3.0.2.75", {"start": v(4.13, 10.41) * mm, "end": v(3.76, 10.04) * mm});
            skLineSegment(sketch, "E3.0.2.76", {"start": v(7.93, 10.41) * mm, "end": v(7.56, 10.04) * mm});
            skLineSegment(sketch, "E3.0.2.77", {"start": v(-18.67, 10.41) * mm, "end": v(-19.04, 10.04) * mm});
            skLineSegment(sketch, "E3.0.2.78", {"start": v(-11.07, 10.41) * mm, "end": v(-11.44, 10.04) * mm});
            skLineSegment(sketch, "E3.0.2.79", {"start": v(-7.27, 10.41) * mm, "end": v(-7.64, 10.04) * mm});
            skLineSegment(sketch, "E3.0.2.80", {"start": v(-22.47, 10.41) * mm, "end": v(-22.84, 10.04) * mm});
            skLineSegment(sketch, "E3.0.2.81", {"start": v(15.49, 6.66) * mm, "end": v(11.73, 2.9) * mm});
            skLineSegment(sketch, "E3.0.2.82", {"start": v(23.09, 6.66) * mm, "end": v(19.33, 2.9) * mm});
            skLineSegment(sketch, "E3.0.2.83", {"start": v(26.89, 6.66) * mm, "end": v(23.13, 2.9) * mm});
            skLineSegment(sketch, "E3.0.2.84", {"start": v(0.29, 6.66) * mm, "end": v(-3.47, 2.9) * mm});
            skLineSegment(sketch, "E3.0.2.85", {"start": v(4.09, 6.66) * mm, "end": v(0.33, 2.9) * mm});
            skLineSegment(sketch, "E3.0.2.86", {"start": v(11.69, 6.66) * mm, "end": v(7.93, 2.9) * mm});
            skLineSegment(sketch, "E3.0.2.87", {"start": v(-14.91, 6.66) * mm, "end": v(-18.67, 2.9) * mm});
            skLineSegment(sketch, "E3.0.2.88", {"start": v(-7.31, 6.66) * mm, "end": v(-11.07, 2.9) * mm});
            skLineSegment(sketch, "E3.0.2.89", {"start": v(-3.51, 6.66) * mm, "end": v(-7.27, 2.9) * mm});
            skLineSegment(sketch, "E3.0.2.90", {"start": v(22.71, 7.03) * mm, "end": v(18.96, 3.28) * mm});
            skLineSegment(sketch, "E3.0.2.91", {"start": v(26.51, 7.03) * mm, "end": v(22.76, 3.28) * mm});
            skLineSegment(sketch, "E3.0.2.92", {"start": v(3.71, 7.03) * mm, "end": v(-0.04, 3.28) * mm});
            skLineSegment(sketch, "E3.0.2.93", {"start": v(7.51, 7.03) * mm, "end": v(3.76, 3.28) * mm});
            skLineSegment(sketch, "E3.0.2.94", {"start": v(30.31, 7.03) * mm, "end": v(26.56, 3.28) * mm});
            skLineSegment(sketch, "E3.0.2.95", {"start": v(-0.09, 6.28) * mm, "end": v(-3.84, 10.04) * mm});
            skLineSegment(sketch, "E3.0.2.96", {"start": v(7.51, 6.28) * mm, "end": v(3.76, 10.04) * mm});
            skLineSegment(sketch, "E3.0.2.97", {"start": v(11.31, 6.28) * mm, "end": v(7.56, 10.04) * mm});
            skLineSegment(sketch, "E3.0.2.98", {"start": v(-15.29, 6.28) * mm, "end": v(-19.04, 10.04) * mm});
            skLineSegment(sketch, "E3.0.2.99", {"start": v(-7.69, 6.28) * mm, "end": v(-11.44, 10.04) * mm});
            skLineSegment(sketch, "E3.0.2.100", {"start": v(-3.89, 6.28) * mm, "end": v(-7.64, 10.04) * mm});
            skLineSegment(sketch, "E3.0.2.101", {"start": v(-19.09, 6.28) * mm, "end": v(-22.84, 10.04) * mm});
            skLineSegment(sketch, "E3.0.2.102", {"start": v(15.11, 6.28) * mm, "end": v(11.36, 10.04) * mm});
            skLineSegment(sketch, "E3.0.2.103", {"start": v(22.71, 6.28) * mm, "end": v(18.96, 10.04) * mm});
            skLineSegment(sketch, "E3.0.2.104", {"start": v(26.51, 6.28) * mm, "end": v(22.76, 10.04) * mm});
            skLineSegment(sketch, "E3.0.2.105", {"start": v(-14.91, 6.66) * mm, "end": v(-18.67, 10.41) * mm});
            skLineSegment(sketch, "E3.0.2.106", {"start": v(26.93, 10.41) * mm, "end": v(26.56, 10.04) * mm});
            skLineSegment(sketch, "E3.0.2.107", {"start": v(-3.51, 6.66) * mm, "end": v(-7.27, 10.41) * mm});
            skLineSegment(sketch, "E3.0.2.108", {"start": v(-7.31, 6.66) * mm, "end": v(-11.07, 10.41) * mm});
            skLineSegment(sketch, "E3.0.2.109", {"start": v(-18.71, 6.66) * mm, "end": v(-22.47, 10.41) * mm});
            skLineSegment(sketch, "E3.0.2.110", {"start": v(-26.27, 2.9) * mm, "end": v(-24.37, 2.9) * mm, "construction": true});
            skLineSegment(sketch, "E3.0.2.111", {"start": v(15.49, 6.66) * mm, "end": v(11.73, 10.41) * mm});
            skLineSegment(sketch, "E3.0.2.112", {"start": v(23.09, 6.66) * mm, "end": v(19.33, 10.41) * mm});
            skLineSegment(sketch, "E3.0.2.113", {"start": v(0.29, 6.66) * mm, "end": v(-3.47, 10.41) * mm});
            skLineSegment(sketch, "E3.0.2.114", {"start": v(26.89, 6.66) * mm, "end": v(23.13, 10.41) * mm});
            skLineSegment(sketch, "E3.0.2.115", {"start": v(7.89, 6.66) * mm, "end": v(4.13, 10.41) * mm});
            skLineSegment(sketch, "E3.0.2.116", {"start": v(11.69, 6.66) * mm, "end": v(7.93, 10.41) * mm});
            skPoint(sketch, "E3.0.2.117", {"position": v(-13.18, 4.97) * mm});
            skPoint(sketch, "E3.0.2.118", {"position": v(17.22, 4.97) * mm});
            skPoint(sketch, "E3.0.2.119", {"position": v(-15.08, 8.35) * mm});
            skPoint(sketch, "E3.0.2.120", {"position": v(0.12, 8.35) * mm});
            skPoint(sketch, "E3.0.2.121", {"position": v(15.32, 8.35) * mm});
            skLineSegment(sketch, "E3.0.2.122", {"start": v(11.73, 10.41) * mm, "end": v(11.36, 10.04) * mm});
            skLineSegment(sketch, "E3.0.2.123", {"start": v(-7.64, 3.28) * mm, "end": v(-7.27, 2.9) * mm});
            skLineSegment(sketch, "E3.0.2.124", {"start": v(7.56, 3.28) * mm, "end": v(7.93, 2.9) * mm});
            skLineSegment(sketch, "E3.0.2.125", {"start": v(3.76, 3.28) * mm, "end": v(4.13, 2.9) * mm});
            skLineSegment(sketch, "E3.0.2.126", {"start": v(-0.04, 3.28) * mm, "end": v(0.33, 2.9) * mm});
            skLineSegment(sketch, "E3.0.2.127", {"start": v(-3.84, 3.28) * mm, "end": v(-3.47, 2.9) * mm});
            skLineSegment(sketch, "E3.0.2.128", {"start": v(22.76, 3.28) * mm, "end": v(23.13, 2.9) * mm});
            skLineSegment(sketch, "E3.0.2.129", {"start": v(11.36, 3.28) * mm, "end": v(11.73, 2.9) * mm});
            skLineSegment(sketch, "E3.0.2.130", {"start": v(26.56, 3.28) * mm, "end": v(26.93, 2.9) * mm});
            skPoint(sketch, "E3.0.2.131", {"position": v(-20.78, 4.97) * mm});
            skLineSegment(sketch, "E3.0.2.132", {"start": v(-9.21, 6.66) * mm, "end": v(-12.97, 10.41) * mm});
            skLineSegment(sketch, "E3.0.2.133", {"start": v(-16.81, 6.66) * mm, "end": v(-20.57, 10.41) * mm});
            skLineSegment(sketch, "E3.0.2.134", {"start": v(5.99, 6.66) * mm, "end": v(2.23, 10.41) * mm});
            skLineSegment(sketch, "E3.0.2.135", {"start": v(-1.61, 6.66) * mm, "end": v(-5.37, 10.41) * mm});
            skLineSegment(sketch, "E3.0.2.136", {"start": v(-5.41, 6.66) * mm, "end": v(-9.17, 10.41) * mm});
            skLineSegment(sketch, "E3.0.2.137", {"start": v(21.19, 6.66) * mm, "end": v(17.43, 10.41) * mm});
            skLineSegment(sketch, "E3.0.2.138", {"start": v(13.59, 6.66) * mm, "end": v(9.83, 10.41) * mm});
            skLineSegment(sketch, "E3.0.2.139", {"start": v(9.79, 6.66) * mm, "end": v(6.03, 10.41) * mm});
            skLineSegment(sketch, "E3.0.2.140", {"start": v(28.79, 6.66) * mm, "end": v(25.03, 10.41) * mm});
            skLineSegment(sketch, "E3.0.2.141", {"start": v(24.99, 6.66) * mm, "end": v(21.23, 10.41) * mm});
            skLineSegment(sketch, "E3.0.2.142", {"start": v(-9.59, 6.28) * mm, "end": v(-13.34, 10.04) * mm});
            skLineSegment(sketch, "E3.0.2.143", {"start": v(-17.19, 6.28) * mm, "end": v(-20.94, 10.04) * mm});
            skLineSegment(sketch, "E3.0.2.144", {"start": v(5.61, 6.28) * mm, "end": v(1.86, 10.04) * mm});
            skLineSegment(sketch, "E3.0.2.145", {"start": v(-1.99, 6.28) * mm, "end": v(-5.74, 10.04) * mm});
            skLineSegment(sketch, "E3.0.2.146", {"start": v(20.81, 6.28) * mm, "end": v(17.06, 10.04) * mm});
            skLineSegment(sketch, "E3.0.2.147", {"start": v(-5.79, 6.28) * mm, "end": v(-9.54, 10.04) * mm});
            skLineSegment(sketch, "E3.0.2.148", {"start": v(13.21, 6.28) * mm, "end": v(9.46, 10.04) * mm});
            skLineSegment(sketch, "E3.0.2.149", {"start": v(9.41, 6.28) * mm, "end": v(5.66, 10.04) * mm});
            skLineSegment(sketch, "E3.0.2.150", {"start": v(24.61, 6.28) * mm, "end": v(20.86, 10.04) * mm});
            skLineSegment(sketch, "E3.0.2.151", {"start": v(28.41, 6.28) * mm, "end": v(24.66, 10.04) * mm});
            skLineSegment(sketch, "E3.0.2.152", {"start": v(-13.39, 7.03) * mm, "end": v(-17.14, 3.28) * mm});
            skLineSegment(sketch, "E3.0.2.153", {"start": v(5.61, 7.03) * mm, "end": v(1.86, 3.28) * mm});
            skLineSegment(sketch, "E3.0.2.154", {"start": v(1.81, 7.03) * mm, "end": v(-1.94, 3.28) * mm});
            skLineSegment(sketch, "E3.0.2.155", {"start": v(-1.99, 7.03) * mm, "end": v(-5.74, 3.28) * mm});
            skLineSegment(sketch, "E3.0.2.156", {"start": v(-5.79, 7.03) * mm, "end": v(-9.54, 3.28) * mm});
            skLineSegment(sketch, "E3.0.2.157", {"start": v(17.01, 7.03) * mm, "end": v(13.26, 3.28) * mm});
            skLineSegment(sketch, "E3.0.2.158", {"start": v(13.21, 7.03) * mm, "end": v(9.46, 3.28) * mm});
            skLineSegment(sketch, "E3.0.2.159", {"start": v(9.41, 7.03) * mm, "end": v(5.66, 3.28) * mm});
            skLineSegment(sketch, "E3.0.2.160", {"start": v(24.61, 7.03) * mm, "end": v(20.86, 3.28) * mm});
            skLineSegment(sketch, "E3.0.2.161", {"start": v(28.41, 7.03) * mm, "end": v(24.66, 3.28) * mm});
            skLineSegment(sketch, "E3.0.2.162", {"start": v(-13.01, 6.66) * mm, "end": v(-16.77, 2.9) * mm});
            skLineSegment(sketch, "E3.0.2.163", {"start": v(5.99, 6.66) * mm, "end": v(2.23, 2.9) * mm});
            skLineSegment(sketch, "E3.0.2.164", {"start": v(2.19, 6.66) * mm, "end": v(-1.57, 2.9) * mm});
            skLineSegment(sketch, "E3.0.2.165", {"start": v(-1.61, 6.66) * mm, "end": v(-5.37, 2.9) * mm});
            skLineSegment(sketch, "E3.0.2.166", {"start": v(-5.41, 6.66) * mm, "end": v(-9.17, 2.9) * mm});
            skLineSegment(sketch, "E3.0.2.167", {"start": v(17.39, 6.66) * mm, "end": v(13.63, 2.9) * mm});
            skLineSegment(sketch, "E3.0.2.168", {"start": v(13.59, 6.66) * mm, "end": v(9.83, 2.9) * mm});
            skLineSegment(sketch, "E3.0.2.169", {"start": v(9.79, 6.66) * mm, "end": v(6.03, 2.9) * mm});
            skLineSegment(sketch, "E3.0.2.170", {"start": v(28.79, 6.66) * mm, "end": v(25.03, 2.9) * mm});
            skLineSegment(sketch, "E3.0.2.171", {"start": v(24.99, 6.66) * mm, "end": v(21.23, 2.9) * mm});
            skLineSegment(sketch, "E3.0.2.172", {"start": v(-20.57, 10.41) * mm, "end": v(-20.94, 10.04) * mm});
            skLineSegment(sketch, "E3.0.2.173", {"start": v(-5.37, 10.41) * mm, "end": v(-5.74, 10.04) * mm});
            skLineSegment(sketch, "E3.0.2.174", {"start": v(-9.17, 10.41) * mm, "end": v(-9.54, 10.04) * mm});
            skLineSegment(sketch, "E3.0.2.175", {"start": v(9.83, 10.41) * mm, "end": v(9.46, 10.04) * mm});
            skLineSegment(sketch, "E3.0.2.176", {"start": v(6.03, 10.41) * mm, "end": v(5.66, 10.04) * mm});
            skLineSegment(sketch, "E3.0.2.177", {"start": v(25.03, 10.41) * mm, "end": v(24.66, 10.04) * mm});
            skLineSegment(sketch, "E3.0.2.178", {"start": v(21.23, 10.41) * mm, "end": v(20.86, 10.04) * mm});
            skLineSegment(sketch, "E3.0.2.179", {"start": v(-22.89, 7.03) * mm, "end": v(-22.51, 6.66) * mm});
            skLineSegment(sketch, "E3.0.2.180", {"start": v(-20.99, 7.03) * mm, "end": v(-24.74, 3.28) * mm});
            skLineSegment(sketch, "E3.0.2.181", {"start": v(-20.61, 6.66) * mm, "end": v(-24.37, 2.9) * mm});
            skLineSegment(sketch, "E3.0.2.182", {"start": v(15.53, 10.41) * mm, "end": v(15.16, 10.04) * mm});
            skLineSegment(sketch, "E3.0.2.183", {"start": v(0.33, 10.41) * mm, "end": v(-0.04, 10.04) * mm});
            skLineSegment(sketch, "E3.0.2.184", {"start": v(-14.87, 10.41) * mm, "end": v(-15.24, 10.04) * mm});
            skLineSegment(sketch, "E3.0.2.185", {"start": v(19.29, 6.66) * mm, "end": v(15.53, 2.9) * mm});
            skLineSegment(sketch, "E3.0.2.186", {"start": v(-11.11, 6.66) * mm, "end": v(-14.87, 2.9) * mm});
            skLineSegment(sketch, "E3.0.2.187", {"start": v(-18.71, 6.66) * mm, "end": v(-22.47, 2.9) * mm});
            skLineSegment(sketch, "E3.0.2.188", {"start": v(15.11, 7.03) * mm, "end": v(11.36, 3.28) * mm});
            skLineSegment(sketch, "E3.0.2.189", {"start": v(18.91, 7.03) * mm, "end": v(15.16, 3.28) * mm});
            skLineSegment(sketch, "E3.0.2.190", {"start": v(-0.09, 7.03) * mm, "end": v(-3.84, 3.28) * mm});
            skLineSegment(sketch, "E3.0.2.191", {"start": v(11.31, 7.03) * mm, "end": v(7.56, 3.28) * mm});
            skLineSegment(sketch, "E3.0.2.192", {"start": v(-15.29, 7.03) * mm, "end": v(-19.04, 3.28) * mm});
            skLineSegment(sketch, "E3.0.2.193", {"start": v(-11.49, 7.03) * mm, "end": v(-15.24, 3.28) * mm});
            skLineSegment(sketch, "E3.0.2.194", {"start": v(-3.89, 7.03) * mm, "end": v(-7.64, 3.28) * mm});
            skLineSegment(sketch, "E3.0.2.195", {"start": v(-7.69, 7.03) * mm, "end": v(-11.44, 3.28) * mm});
            skLineSegment(sketch, "E3.0.2.196", {"start": v(-19.09, 7.03) * mm, "end": v(-22.84, 3.28) * mm});
            skLineSegment(sketch, "E3.0.2.197", {"start": v(3.71, 6.28) * mm, "end": v(-0.04, 10.04) * mm});
            skLineSegment(sketch, "E3.0.2.198", {"start": v(-11.49, 6.28) * mm, "end": v(-15.24, 10.04) * mm});
            skLineSegment(sketch, "E3.0.2.199", {"start": v(18.91, 6.28) * mm, "end": v(15.16, 10.04) * mm});
            skLineSegment(sketch, "E3.0.2.200", {"start": v(-11.11, 6.66) * mm, "end": v(-14.87, 10.41) * mm});
            skLineSegment(sketch, "E3.0.2.201", {"start": v(19.29, 6.66) * mm, "end": v(15.53, 10.41) * mm});
            skLineSegment(sketch, "E3.0.2.202", {"start": v(4.09, 6.66) * mm, "end": v(0.33, 10.41) * mm});
            skLineSegment(sketch, "E3.0.2.203", {"start": v(24.66, 3.28) * mm, "end": v(25.03, 2.9) * mm});
            skLineSegment(sketch, "E3.0.2.204", {"start": v(9.46, 3.28) * mm, "end": v(9.83, 2.9) * mm});
            skLineSegment(sketch, "E3.0.2.205", {"start": v(13.26, 3.28) * mm, "end": v(13.63, 2.9) * mm});
            skLineSegment(sketch, "E3.0.2.206", {"start": v(20.86, 3.28) * mm, "end": v(21.23, 2.9) * mm});
            skLineSegment(sketch, "E3.0.2.207", {"start": v(-5.74, 3.28) * mm, "end": v(-5.37, 2.9) * mm});
            skLineSegment(sketch, "E3.0.2.208", {"start": v(-1.94, 3.28) * mm, "end": v(-1.57, 2.9) * mm});
            skLineSegment(sketch, "E3.0.2.209", {"start": v(5.66, 3.28) * mm, "end": v(6.03, 2.9) * mm});
            skLineSegment(sketch, "E3.0.2.210", {"start": v(1.86, 3.28) * mm, "end": v(2.23, 2.9) * mm});
            skLineSegment(sketch, "E3.0.2.211", {"start": v(-17.14, 3.28) * mm, "end": v(-16.77, 2.9) * mm});
            skLineSegment(sketch, "E3.0.2.212", {"start": v(-9.54, 3.28) * mm, "end": v(-9.17, 2.9) * mm});
            skLineSegment(sketch, "E3.0.2.213", {"start": v(-22.84, 3.28) * mm, "end": v(-22.47, 2.9) * mm});
            skLineSegment(sketch, "E3.0.2.214", {"start": v(-11.44, 3.28) * mm, "end": v(-11.07, 2.9) * mm});
            skLineSegment(sketch, "E3.0.2.215", {"start": v(-15.24, 3.28) * mm, "end": v(-14.87, 2.9) * mm});
            skLineSegment(sketch, "E3.0.2.216", {"start": v(-19.04, 3.28) * mm, "end": v(-18.67, 2.9) * mm});
            skLineSegment(sketch, "E3.0.2.217", {"start": v(18.96, 3.28) * mm, "end": v(19.33, 2.9) * mm});
            skLineSegment(sketch, "E3.0.2.218", {"start": v(15.16, 3.28) * mm, "end": v(15.53, 2.9) * mm});
            skLineSegment(sketch, "E3.0.2.219", {"start": v(-13.01, 6.66) * mm, "end": v(-16.77, 10.41) * mm});
            skLineSegment(sketch, "E3.0.2.220", {"start": v(2.19, 6.66) * mm, "end": v(-1.57, 10.41) * mm});
            skLineSegment(sketch, "E3.0.2.221", {"start": v(17.39, 6.66) * mm, "end": v(13.63, 10.41) * mm});
            skLineSegment(sketch, "E3.0.2.222", {"start": v(-13.39, 6.28) * mm, "end": v(-17.14, 10.04) * mm});
            skLineSegment(sketch, "E3.0.2.223", {"start": v(1.81, 6.28) * mm, "end": v(-1.94, 10.04) * mm});
            skLineSegment(sketch, "E3.0.2.224", {"start": v(17.01, 6.28) * mm, "end": v(13.26, 10.04) * mm});
            skLineSegment(sketch, "E3.0.2.225", {"start": v(-9.59, 7.03) * mm, "end": v(-13.34, 3.28) * mm});
            skLineSegment(sketch, "E3.0.2.226", {"start": v(-17.19, 7.03) * mm, "end": v(-20.94, 3.28) * mm});
            skLineSegment(sketch, "E3.0.2.227", {"start": v(20.81, 7.03) * mm, "end": v(17.06, 3.28) * mm});
            skLineSegment(sketch, "E3.0.2.228", {"start": v(-9.21, 6.66) * mm, "end": v(-12.97, 2.9) * mm});
            skLineSegment(sketch, "E3.0.2.229", {"start": v(-16.81, 6.66) * mm, "end": v(-20.57, 2.9) * mm});
            skLineSegment(sketch, "E3.0.2.230", {"start": v(21.19, 6.66) * mm, "end": v(17.43, 2.9) * mm});
            skLineSegment(sketch, "E3.0.2.231", {"start": v(-12.97, 10.41) * mm, "end": v(-13.34, 10.04) * mm});
            skLineSegment(sketch, "E3.0.2.232", {"start": v(-16.77, 10.41) * mm, "end": v(-17.14, 10.04) * mm});
            skLineSegment(sketch, "E3.0.2.233", {"start": v(2.23, 10.41) * mm, "end": v(1.86, 10.04) * mm});
            skLineSegment(sketch, "E3.0.2.234", {"start": v(-1.57, 10.41) * mm, "end": v(-1.94, 10.04) * mm});
            skLineSegment(sketch, "E3.0.2.235", {"start": v(17.43, 10.41) * mm, "end": v(17.06, 10.04) * mm});
            skLineSegment(sketch, "E3.0.2.236", {"start": v(13.63, 10.41) * mm, "end": v(13.26, 10.04) * mm});
            skLineSegment(sketch, "E3.0.2.237", {"start": v(-24.74, 3.28) * mm, "end": v(-24.37, 2.9) * mm});
            skLineSegment(sketch, "E3.0.2.238", {"start": v(-22.51, 6.66) * mm, "end": v(-22.89, 6.28) * mm});
            skLineSegment(sketch, "E3.0.2.239", {"start": v(-26.64, 3.28) * mm, "end": v(-26.27, 2.9) * mm});
            skLineSegment(sketch, "E3.0.2.240", {"start": v(32.21, 7.03) * mm, "end": v(32.59, 6.66) * mm});
            skLineSegment(sketch, "E3.0.2.241", {"start": v(9.41, 7.03) * mm, "end": v(9.79, 6.66) * mm});
            skLineSegment(sketch, "E3.0.2.242", {"start": v(32.59, 6.66) * mm, "end": v(32.21, 6.28) * mm});
            skLineSegment(sketch, "E3.0.2.243", {"start": v(9.79, 6.66) * mm, "end": v(9.41, 6.28) * mm});
            skLineSegment(sketch, "E3.0.2.244", {"start": v(17.06, 3.28) * mm, "end": v(17.43, 2.9) * mm});
            skLineSegment(sketch, "E3.0.2.245", {"start": v(-20.94, 3.28) * mm, "end": v(-20.57, 2.9) * mm});
            skLineSegment(sketch, "E3.0.2.246", {"start": v(-13.34, 3.28) * mm, "end": v(-12.97, 2.9) * mm});
            skLineSegment(sketch, "E3.0.2.247", {"start": v(11.69, 6.66) * mm, "end": v(11.31, 6.28) * mm});
            skLineSegment(sketch, "E3.0.2.248", {"start": v(11.31, 7.03) * mm, "end": v(11.69, 6.66) * mm});
            skLineSegment(sketch, "E3.0.2.249", {"start": v(28.41, 7.03) * mm, "end": v(28.79, 6.66) * mm});
            skLineSegment(sketch, "E3.0.2.250", {"start": v(13.21, 7.03) * mm, "end": v(13.59, 6.66) * mm});
            skLineSegment(sketch, "E3.0.2.251", {"start": v(1.81, 7.03) * mm, "end": v(2.19, 6.66) * mm});
            skLineSegment(sketch, "E3.0.2.252", {"start": v(-13.39, 7.03) * mm, "end": v(-13.01, 6.66) * mm});
            skLineSegment(sketch, "E3.0.2.253", {"start": v(-5.79, 7.03) * mm, "end": v(-5.41, 6.66) * mm});
            skLineSegment(sketch, "E3.0.2.254", {"start": v(28.79, 6.66) * mm, "end": v(28.41, 6.28) * mm});
            skLineSegment(sketch, "E3.0.2.255", {"start": v(13.59, 6.66) * mm, "end": v(13.21, 6.28) * mm});
            skLineSegment(sketch, "E3.0.2.256", {"start": v(2.19, 6.66) * mm, "end": v(1.81, 6.28) * mm});
            skLineSegment(sketch, "E3.0.2.257", {"start": v(-13.01, 6.66) * mm, "end": v(-13.39, 6.28) * mm});
            skLineSegment(sketch, "E3.0.2.258", {"start": v(-5.41, 6.66) * mm, "end": v(-5.79, 6.28) * mm});
            skLineSegment(sketch, "E3.0.2.259", {"start": v(-7.31, 6.66) * mm, "end": v(-7.69, 6.28) * mm});
            skLineSegment(sketch, "E3.0.2.260", {"start": v(-11.11, 6.66) * mm, "end": v(-11.49, 6.28) * mm});
            skLineSegment(sketch, "E3.0.2.261", {"start": v(7.89, 6.66) * mm, "end": v(7.51, 6.28) * mm});
            skLineSegment(sketch, "E3.0.2.262", {"start": v(4.09, 6.66) * mm, "end": v(3.71, 6.28) * mm});
            skLineSegment(sketch, "E3.0.2.263", {"start": v(26.89, 6.66) * mm, "end": v(26.51, 6.28) * mm});
            skLineSegment(sketch, "E3.0.2.264", {"start": v(30.69, 6.66) * mm, "end": v(30.31, 6.28) * mm});
            skLineSegment(sketch, "E3.0.2.265", {"start": v(-11.49, 7.03) * mm, "end": v(-11.11, 6.66) * mm});
            skLineSegment(sketch, "E3.0.2.266", {"start": v(3.71, 7.03) * mm, "end": v(4.09, 6.66) * mm});
            skLineSegment(sketch, "E3.0.2.267", {"start": v(-7.69, 7.03) * mm, "end": v(-7.31, 6.66) * mm});
            skLineSegment(sketch, "E3.0.2.268", {"start": v(15.11, 7.03) * mm, "end": v(15.49, 6.66) * mm});
            skLineSegment(sketch, "E3.0.2.269", {"start": v(7.51, 7.03) * mm, "end": v(7.89, 6.66) * mm});
            skLineSegment(sketch, "E3.0.2.270", {"start": v(30.31, 7.03) * mm, "end": v(30.69, 6.66) * mm});
            skLineSegment(sketch, "E3.0.2.271", {"start": v(26.51, 7.03) * mm, "end": v(26.89, 6.66) * mm});
            skLineSegment(sketch, "E3.0.2.272", {"start": v(-20.61, 6.66) * mm, "end": v(-20.99, 6.28) * mm});
            skLineSegment(sketch, "E3.0.2.273", {"start": v(-20.99, 7.03) * mm, "end": v(-20.61, 6.66) * mm});
            skLineSegment(sketch, "E3.0.2.274", {"start": v(17.01, 7.03) * mm, "end": v(17.39, 6.66) * mm});
            skLineSegment(sketch, "E3.0.2.275", {"start": v(24.61, 7.03) * mm, "end": v(24.99, 6.66) * mm});
            skLineSegment(sketch, "E3.0.2.276", {"start": v(5.61, 7.03) * mm, "end": v(5.99, 6.66) * mm});
            skLineSegment(sketch, "E3.0.2.277", {"start": v(-17.19, 7.03) * mm, "end": v(-16.81, 6.66) * mm});
            skLineSegment(sketch, "E3.0.2.278", {"start": v(-9.59, 7.03) * mm, "end": v(-9.21, 6.66) * mm});
            skLineSegment(sketch, "E3.0.2.279", {"start": v(17.39, 6.66) * mm, "end": v(17.01, 6.28) * mm});
            skLineSegment(sketch, "E3.0.2.280", {"start": v(24.99, 6.66) * mm, "end": v(24.61, 6.28) * mm});
            skLineSegment(sketch, "E3.0.2.281", {"start": v(5.99, 6.66) * mm, "end": v(5.61, 6.28) * mm});
            skLineSegment(sketch, "E3.0.2.282", {"start": v(-16.81, 6.66) * mm, "end": v(-17.19, 6.28) * mm});
            skLineSegment(sketch, "E3.0.2.283", {"start": v(-9.21, 6.66) * mm, "end": v(-9.59, 6.28) * mm});
            skLineSegment(sketch, "E3.0.2.284", {"start": v(-18.71, 6.66) * mm, "end": v(-19.09, 6.28) * mm});
            skLineSegment(sketch, "E3.0.2.285", {"start": v(-14.91, 6.66) * mm, "end": v(-15.29, 6.28) * mm});
            skLineSegment(sketch, "E3.0.2.286", {"start": v(0.29, 6.66) * mm, "end": v(-0.09, 6.28) * mm});
            skLineSegment(sketch, "E3.0.2.287", {"start": v(23.09, 6.66) * mm, "end": v(22.71, 6.28) * mm});
            skLineSegment(sketch, "E3.0.2.288", {"start": v(15.49, 6.66) * mm, "end": v(15.11, 6.28) * mm});
            skLineSegment(sketch, "E3.0.2.289", {"start": v(-15.29, 7.03) * mm, "end": v(-14.91, 6.66) * mm});
            skLineSegment(sketch, "E3.0.2.290", {"start": v(-19.09, 7.03) * mm, "end": v(-18.71, 6.66) * mm});
            skLineSegment(sketch, "E3.0.2.291", {"start": v(-0.09, 7.03) * mm, "end": v(0.29, 6.66) * mm});
            skLineSegment(sketch, "E3.0.2.292", {"start": v(-3.89, 7.03) * mm, "end": v(-3.51, 6.66) * mm});
            skLineSegment(sketch, "E3.0.2.293", {"start": v(22.71, 7.03) * mm, "end": v(23.09, 6.66) * mm});
            skLineSegment(sketch, "E3.0.2.294", {"start": v(20.81, 7.03) * mm, "end": v(21.19, 6.66) * mm});
            skLineSegment(sketch, "E3.0.2.295", {"start": v(-1.99, 7.03) * mm, "end": v(-1.61, 6.66) * mm});
            skLineSegment(sketch, "E3.0.2.296", {"start": v(21.19, 6.66) * mm, "end": v(20.81, 6.28) * mm});
            skLineSegment(sketch, "E3.0.2.297", {"start": v(-1.61, 6.66) * mm, "end": v(-1.99, 6.28) * mm});
            skLineSegment(sketch, "E3.0.2.298", {"start": v(-3.51, 6.66) * mm, "end": v(-3.89, 6.28) * mm});
            skLineSegment(sketch, "E3.0.2.299", {"start": v(19.29, 6.66) * mm, "end": v(18.91, 6.28) * mm});
            skLineSegment(sketch, "E3.0.2.300", {"start": v(18.91, 7.03) * mm, "end": v(19.29, 6.66) * mm});
            skPoint(sketch, "E3.0.3.0", {"position": v(-22.68, -1.83) * mm});
            skPoint(sketch, "E3.0.3.1", {"position": v(-24.58, -1.83) * mm});
            skPoint(sketch, "E3.0.3.2", {"position": v(-24.58, 1.55) * mm});
            skPoint(sketch, "E3.0.3.3", {"position": v(30.52, 1.55) * mm});
            skPoint(sketch, "E3.0.3.4", {"position": v(-22.68, 1.55) * mm});
            skPoint(sketch, "E3.0.3.5", {"position": v(28.62, 1.55) * mm});
            skPoint(sketch, "E3.0.3.6", {"position": v(30.52, -1.83) * mm});
            skLineSegment(sketch, "E3.0.3.7", {"start": v(32.59, -0.14) * mm, "end": v(28.83, 3.61) * mm});
            skPoint(sketch, "E3.0.3.8", {"position": v(28.62, -1.83) * mm});
            skLineSegment(sketch, "E3.0.3.9", {"start": v(-22.89, -0.52) * mm, "end": v(-26.64, 3.24) * mm});
            skLineSegment(sketch, "E3.0.3.10", {"start": v(-22.89, 0.23) * mm, "end": v(-26.64, -3.52) * mm});
            skPoint(sketch, "E3.0.3.11", {"position": v(5.82, -1.83) * mm});
            skPoint(sketch, "E3.0.3.12", {"position": v(3.92, -1.83) * mm});
            skPoint(sketch, "E3.0.3.13", {"position": v(26.72, -1.83) * mm});
            skPoint(sketch, "E3.0.3.14", {"position": v(26.72, 1.55) * mm});
            skLineSegment(sketch, "E3.0.3.15", {"start": v(32.21, -0.52) * mm, "end": v(28.46, 3.24) * mm});
            skLineSegment(sketch, "E3.0.3.16", {"start": v(32.59, -0.14) * mm, "end": v(28.83, -3.9) * mm});
            skPoint(sketch, "E3.0.3.17", {"position": v(0.12, -1.83) * mm});
            skLineSegment(sketch, "E3.0.3.18", {"start": v(-22.51, -0.14) * mm, "end": v(-26.27, 3.61) * mm});
            skLineSegment(sketch, "E3.0.3.19", {"start": v(-22.51, -0.14) * mm, "end": v(-26.27, -3.9) * mm});
            skPoint(sketch, "E3.0.3.20", {"position": v(-7.48, -1.83) * mm});
            skPoint(sketch, "E3.0.3.21", {"position": v(7.72, -1.83) * mm});
            skPoint(sketch, "E3.0.3.22", {"position": v(22.92, -1.83) * mm});
            skLineSegment(sketch, "E3.0.3.23", {"start": v(30.69, -0.14) * mm, "end": v(26.93, -3.9) * mm});
            skPoint(sketch, "E3.0.3.24", {"position": v(-9.38, 1.55) * mm});
            skPoint(sketch, "E3.0.3.25", {"position": v(5.82, 1.55) * mm});
            skLineSegment(sketch, "E3.0.3.26", {"start": v(7.89, -0.14) * mm, "end": v(4.13, -3.9) * mm});
            skPoint(sketch, "E3.0.3.27", {"position": v(21.02, 1.55) * mm});
            skPoint(sketch, "E3.0.3.28", {"position": v(-9.38, -1.83) * mm});
            skPoint(sketch, "E3.0.3.29", {"position": v(21.02, -1.83) * mm});
            skPoint(sketch, "E3.0.3.30", {"position": v(-11.28, 1.55) * mm});
            skPoint(sketch, "E3.0.3.31", {"position": v(3.92, 1.55) * mm});
            skPoint(sketch, "E3.0.3.32", {"position": v(19.12, 1.55) * mm});
            skLineSegment(sketch, "E3.0.3.33", {"start": v(30.31, -0.52) * mm, "end": v(26.56, 3.24) * mm});
            skLineSegment(sketch, "E3.0.3.34", {"start": v(30.69, -0.14) * mm, "end": v(26.93, 3.61) * mm});
            skPoint(sketch, "E3.0.3.35", {"position": v(-11.28, -1.83) * mm});
            skPoint(sketch, "E3.0.3.36", {"position": v(19.12, -1.83) * mm});
            skPoint(sketch, "E3.0.3.37", {"position": v(-13.18, 1.55) * mm});
            skPoint(sketch, "E3.0.3.38", {"position": v(2.02, 1.55) * mm});
            skPoint(sketch, "E3.0.3.39", {"position": v(17.22, 1.55) * mm});
            skPoint(sketch, "E3.0.3.40", {"position": v(2.02, -1.83) * mm});
            skLineSegment(sketch, "E3.0.3.41", {"start": v(28.46, -3.52) * mm, "end": v(28.83, -3.9) * mm});
            skPoint(sketch, "E3.0.3.42", {"position": v(22.92, 1.55) * mm});
            skPoint(sketch, "E3.0.3.43", {"position": v(7.72, 1.55) * mm});
            skPoint(sketch, "E3.0.3.44", {"position": v(-7.48, 1.55) * mm});
            skPoint(sketch, "E3.0.3.45", {"position": v(24.82, -1.83) * mm});
            skPoint(sketch, "E3.0.3.46", {"position": v(9.62, -1.83) * mm});
            skPoint(sketch, "E3.0.3.47", {"position": v(-5.58, -1.83) * mm});
            skPoint(sketch, "E3.0.3.48", {"position": v(9.62, 1.55) * mm});
            skPoint(sketch, "E3.0.3.49", {"position": v(-5.58, 1.55) * mm});
            skPoint(sketch, "E3.0.3.50", {"position": v(-20.78, 1.55) * mm});
            skPoint(sketch, "E3.0.3.51", {"position": v(24.82, 1.55) * mm});
            skPoint(sketch, "E3.0.3.52", {"position": v(11.52, -1.83) * mm});
            skPoint(sketch, "E3.0.3.53", {"position": v(-3.68, -1.83) * mm});
            skPoint(sketch, "E3.0.3.54", {"position": v(-18.88, -1.83) * mm});
            skPoint(sketch, "E3.0.3.55", {"position": v(11.52, 1.55) * mm});
            skPoint(sketch, "E3.0.3.56", {"position": v(-3.68, 1.55) * mm});
            skPoint(sketch, "E3.0.3.57", {"position": v(-18.88, 1.55) * mm});
            skPoint(sketch, "E3.0.3.58", {"position": v(13.42, -1.83) * mm});
            skPoint(sketch, "E3.0.3.59", {"position": v(-1.78, -1.83) * mm});
            skPoint(sketch, "E3.0.3.60", {"position": v(-16.98, -1.83) * mm});
            skLineSegment(sketch, "E3.0.3.61", {"start": v(32.21, 0.23) * mm, "end": v(28.46, -3.52) * mm});
            skPoint(sketch, "E3.0.3.62", {"position": v(13.42, 1.55) * mm});
            skPoint(sketch, "E3.0.3.63", {"position": v(-1.78, 1.55) * mm});
            skPoint(sketch, "E3.0.3.64", {"position": v(-16.98, 1.55) * mm});
            skPoint(sketch, "E3.0.3.65", {"position": v(15.32, -1.83) * mm});
            skPoint(sketch, "E3.0.3.66", {"position": v(-15.08, -1.83) * mm});
            skLineSegment(sketch, "E3.0.3.67", {"start": v(28.83, 3.61) * mm, "end": v(28.46, 3.24) * mm});
            skLineSegment(sketch, "E3.0.3.68", {"start": v(-26.27, 3.61) * mm, "end": v(-26.64, 3.24) * mm});
            skLineSegment(sketch, "E3.0.3.69", {"start": v(-20.61, -0.14) * mm, "end": v(-24.37, 3.61) * mm});
            skLineSegment(sketch, "E3.0.3.70", {"start": v(-20.99, -0.52) * mm, "end": v(-24.74, 3.24) * mm});
            skLineSegment(sketch, "E3.0.3.71", {"start": v(-24.37, 3.61) * mm, "end": v(-24.74, 3.24) * mm});
            skLineSegment(sketch, "E3.0.3.72", {"start": v(19.33, 3.61) * mm, "end": v(18.96, 3.24) * mm});
            skLineSegment(sketch, "E3.0.3.73", {"start": v(23.13, 3.61) * mm, "end": v(22.76, 3.24) * mm});
            skLineSegment(sketch, "E3.0.3.74", {"start": v(-3.47, 3.61) * mm, "end": v(-3.84, 3.24) * mm});
            skLineSegment(sketch, "E3.0.3.75", {"start": v(4.13, 3.61) * mm, "end": v(3.76, 3.24) * mm});
            skLineSegment(sketch, "E3.0.3.76", {"start": v(7.93, 3.61) * mm, "end": v(7.56, 3.24) * mm});
            skLineSegment(sketch, "E3.0.3.77", {"start": v(-18.67, 3.61) * mm, "end": v(-19.04, 3.24) * mm});
            skLineSegment(sketch, "E3.0.3.78", {"start": v(-11.07, 3.61) * mm, "end": v(-11.44, 3.24) * mm});
            skLineSegment(sketch, "E3.0.3.79", {"start": v(-7.27, 3.61) * mm, "end": v(-7.64, 3.24) * mm});
            skLineSegment(sketch, "E3.0.3.80", {"start": v(-22.47, 3.61) * mm, "end": v(-22.84, 3.24) * mm});
            skLineSegment(sketch, "E3.0.3.81", {"start": v(15.49, -0.14) * mm, "end": v(11.73, -3.9) * mm});
            skLineSegment(sketch, "E3.0.3.82", {"start": v(23.09, -0.14) * mm, "end": v(19.33, -3.9) * mm});
            skLineSegment(sketch, "E3.0.3.83", {"start": v(26.89, -0.14) * mm, "end": v(23.13, -3.9) * mm});
            skLineSegment(sketch, "E3.0.3.84", {"start": v(0.29, -0.14) * mm, "end": v(-3.47, -3.9) * mm});
            skLineSegment(sketch, "E3.0.3.85", {"start": v(4.09, -0.14) * mm, "end": v(0.33, -3.9) * mm});
            skLineSegment(sketch, "E3.0.3.86", {"start": v(11.69, -0.14) * mm, "end": v(7.93, -3.9) * mm});
            skLineSegment(sketch, "E3.0.3.87", {"start": v(-14.91, -0.14) * mm, "end": v(-18.67, -3.9) * mm});
            skLineSegment(sketch, "E3.0.3.88", {"start": v(-7.31, -0.14) * mm, "end": v(-11.07, -3.9) * mm});
            skLineSegment(sketch, "E3.0.3.89", {"start": v(-3.51, -0.14) * mm, "end": v(-7.27, -3.9) * mm});
            skLineSegment(sketch, "E3.0.3.90", {"start": v(22.71, 0.23) * mm, "end": v(18.96, -3.52) * mm});
            skLineSegment(sketch, "E3.0.3.91", {"start": v(26.51, 0.23) * mm, "end": v(22.76, -3.52) * mm});
            skLineSegment(sketch, "E3.0.3.92", {"start": v(3.71, 0.23) * mm, "end": v(-0.04, -3.52) * mm});
            skLineSegment(sketch, "E3.0.3.93", {"start": v(7.51, 0.23) * mm, "end": v(3.76, -3.52) * mm});
            skLineSegment(sketch, "E3.0.3.94", {"start": v(30.31, 0.23) * mm, "end": v(26.56, -3.52) * mm});
            skLineSegment(sketch, "E3.0.3.95", {"start": v(-0.09, -0.52) * mm, "end": v(-3.84, 3.24) * mm});
            skLineSegment(sketch, "E3.0.3.96", {"start": v(7.51, -0.52) * mm, "end": v(3.76, 3.24) * mm});
            skLineSegment(sketch, "E3.0.3.97", {"start": v(11.31, -0.52) * mm, "end": v(7.56, 3.24) * mm});
            skLineSegment(sketch, "E3.0.3.98", {"start": v(-15.29, -0.52) * mm, "end": v(-19.04, 3.24) * mm});
            skLineSegment(sketch, "E3.0.3.99", {"start": v(-7.69, -0.52) * mm, "end": v(-11.44, 3.24) * mm});
            skLineSegment(sketch, "E3.0.3.100", {"start": v(-3.89, -0.52) * mm, "end": v(-7.64, 3.24) * mm});
            skLineSegment(sketch, "E3.0.3.101", {"start": v(-19.09, -0.52) * mm, "end": v(-22.84, 3.24) * mm});
            skLineSegment(sketch, "E3.0.3.102", {"start": v(15.11, -0.52) * mm, "end": v(11.36, 3.24) * mm});
            skLineSegment(sketch, "E3.0.3.103", {"start": v(22.71, -0.52) * mm, "end": v(18.96, 3.24) * mm});
            skLineSegment(sketch, "E3.0.3.104", {"start": v(26.51, -0.52) * mm, "end": v(22.76, 3.24) * mm});
            skLineSegment(sketch, "E3.0.3.105", {"start": v(-14.91, -0.14) * mm, "end": v(-18.67, 3.61) * mm});
            skLineSegment(sketch, "E3.0.3.106", {"start": v(26.93, 3.61) * mm, "end": v(26.56, 3.24) * mm});
            skLineSegment(sketch, "E3.0.3.107", {"start": v(-3.51, -0.14) * mm, "end": v(-7.27, 3.61) * mm});
            skLineSegment(sketch, "E3.0.3.108", {"start": v(-7.31, -0.14) * mm, "end": v(-11.07, 3.61) * mm});
            skLineSegment(sketch, "E3.0.3.109", {"start": v(-18.71, -0.14) * mm, "end": v(-22.47, 3.61) * mm});
            skLineSegment(sketch, "E3.0.3.110", {"start": v(-26.27, -3.9) * mm, "end": v(-24.37, -3.9) * mm, "construction": true});
            skLineSegment(sketch, "E3.0.3.111", {"start": v(15.49, -0.14) * mm, "end": v(11.73, 3.61) * mm});
            skLineSegment(sketch, "E3.0.3.112", {"start": v(23.09, -0.14) * mm, "end": v(19.33, 3.61) * mm});
            skLineSegment(sketch, "E3.0.3.113", {"start": v(0.29, -0.14) * mm, "end": v(-3.47, 3.61) * mm});
            skLineSegment(sketch, "E3.0.3.114", {"start": v(26.89, -0.14) * mm, "end": v(23.13, 3.61) * mm});
            skLineSegment(sketch, "E3.0.3.115", {"start": v(7.89, -0.14) * mm, "end": v(4.13, 3.61) * mm});
            skLineSegment(sketch, "E3.0.3.116", {"start": v(11.69, -0.14) * mm, "end": v(7.93, 3.61) * mm});
            skPoint(sketch, "E3.0.3.117", {"position": v(-13.18, -1.83) * mm});
            skPoint(sketch, "E3.0.3.118", {"position": v(17.22, -1.83) * mm});
            skPoint(sketch, "E3.0.3.119", {"position": v(-15.08, 1.55) * mm});
            skPoint(sketch, "E3.0.3.120", {"position": v(0.12, 1.55) * mm});
            skPoint(sketch, "E3.0.3.121", {"position": v(15.32, 1.55) * mm});
            skLineSegment(sketch, "E3.0.3.122", {"start": v(11.73, 3.61) * mm, "end": v(11.36, 3.24) * mm});
            skLineSegment(sketch, "E3.0.3.123", {"start": v(-7.64, -3.52) * mm, "end": v(-7.27, -3.9) * mm});
            skLineSegment(sketch, "E3.0.3.124", {"start": v(7.56, -3.52) * mm, "end": v(7.93, -3.9) * mm});
            skLineSegment(sketch, "E3.0.3.125", {"start": v(3.76, -3.52) * mm, "end": v(4.13, -3.9) * mm});
            skLineSegment(sketch, "E3.0.3.126", {"start": v(-0.04, -3.52) * mm, "end": v(0.33, -3.9) * mm});
            skLineSegment(sketch, "E3.0.3.127", {"start": v(-3.84, -3.52) * mm, "end": v(-3.47, -3.9) * mm});
            skLineSegment(sketch, "E3.0.3.128", {"start": v(22.76, -3.52) * mm, "end": v(23.13, -3.9) * mm});
            skLineSegment(sketch, "E3.0.3.129", {"start": v(11.36, -3.52) * mm, "end": v(11.73, -3.9) * mm});
            skLineSegment(sketch, "E3.0.3.130", {"start": v(26.56, -3.52) * mm, "end": v(26.93, -3.9) * mm});
            skPoint(sketch, "E3.0.3.131", {"position": v(-20.78, -1.83) * mm});
            skLineSegment(sketch, "E3.0.3.132", {"start": v(-9.21, -0.14) * mm, "end": v(-12.97, 3.61) * mm});
            skLineSegment(sketch, "E3.0.3.133", {"start": v(-16.81, -0.14) * mm, "end": v(-20.57, 3.61) * mm});
            skLineSegment(sketch, "E3.0.3.134", {"start": v(5.99, -0.14) * mm, "end": v(2.23, 3.61) * mm});
            skLineSegment(sketch, "E3.0.3.135", {"start": v(-1.61, -0.14) * mm, "end": v(-5.37, 3.61) * mm});
            skLineSegment(sketch, "E3.0.3.136", {"start": v(-5.41, -0.14) * mm, "end": v(-9.17, 3.61) * mm});
            skLineSegment(sketch, "E3.0.3.137", {"start": v(21.19, -0.14) * mm, "end": v(17.43, 3.61) * mm});
            skLineSegment(sketch, "E3.0.3.138", {"start": v(13.59, -0.14) * mm, "end": v(9.83, 3.61) * mm});
            skLineSegment(sketch, "E3.0.3.139", {"start": v(9.79, -0.14) * mm, "end": v(6.03, 3.61) * mm});
            skLineSegment(sketch, "E3.0.3.140", {"start": v(28.79, -0.14) * mm, "end": v(25.03, 3.61) * mm});
            skLineSegment(sketch, "E3.0.3.141", {"start": v(24.99, -0.14) * mm, "end": v(21.23, 3.61) * mm});
            skLineSegment(sketch, "E3.0.3.142", {"start": v(-9.59, -0.52) * mm, "end": v(-13.34, 3.24) * mm});
            skLineSegment(sketch, "E3.0.3.143", {"start": v(-17.19, -0.52) * mm, "end": v(-20.94, 3.24) * mm});
            skLineSegment(sketch, "E3.0.3.144", {"start": v(5.61, -0.52) * mm, "end": v(1.86, 3.24) * mm});
            skLineSegment(sketch, "E3.0.3.145", {"start": v(-1.99, -0.52) * mm, "end": v(-5.74, 3.24) * mm});
            skLineSegment(sketch, "E3.0.3.146", {"start": v(20.81, -0.52) * mm, "end": v(17.06, 3.24) * mm});
            skLineSegment(sketch, "E3.0.3.147", {"start": v(-5.79, -0.52) * mm, "end": v(-9.54, 3.24) * mm});
            skLineSegment(sketch, "E3.0.3.148", {"start": v(13.21, -0.52) * mm, "end": v(9.46, 3.24) * mm});
            skLineSegment(sketch, "E3.0.3.149", {"start": v(9.41, -0.52) * mm, "end": v(5.66, 3.24) * mm});
            skLineSegment(sketch, "E3.0.3.150", {"start": v(24.61, -0.52) * mm, "end": v(20.86, 3.24) * mm});
            skLineSegment(sketch, "E3.0.3.151", {"start": v(28.41, -0.52) * mm, "end": v(24.66, 3.24) * mm});
            skLineSegment(sketch, "E3.0.3.152", {"start": v(-13.39, 0.23) * mm, "end": v(-17.14, -3.52) * mm});
            skLineSegment(sketch, "E3.0.3.153", {"start": v(5.61, 0.23) * mm, "end": v(1.86, -3.52) * mm});
            skLineSegment(sketch, "E3.0.3.154", {"start": v(1.81, 0.23) * mm, "end": v(-1.94, -3.52) * mm});
            skLineSegment(sketch, "E3.0.3.155", {"start": v(-1.99, 0.23) * mm, "end": v(-5.74, -3.52) * mm});
            skLineSegment(sketch, "E3.0.3.156", {"start": v(-5.79, 0.23) * mm, "end": v(-9.54, -3.52) * mm});
            skLineSegment(sketch, "E3.0.3.157", {"start": v(17.01, 0.23) * mm, "end": v(13.26, -3.52) * mm});
            skLineSegment(sketch, "E3.0.3.158", {"start": v(13.21, 0.23) * mm, "end": v(9.46, -3.52) * mm});
            skLineSegment(sketch, "E3.0.3.159", {"start": v(9.41, 0.23) * mm, "end": v(5.66, -3.52) * mm});
            skLineSegment(sketch, "E3.0.3.160", {"start": v(24.61, 0.23) * mm, "end": v(20.86, -3.52) * mm});
            skLineSegment(sketch, "E3.0.3.161", {"start": v(28.41, 0.23) * mm, "end": v(24.66, -3.52) * mm});
            skLineSegment(sketch, "E3.0.3.162", {"start": v(-13.01, -0.14) * mm, "end": v(-16.77, -3.9) * mm});
            skLineSegment(sketch, "E3.0.3.163", {"start": v(5.99, -0.14) * mm, "end": v(2.23, -3.9) * mm});
            skLineSegment(sketch, "E3.0.3.164", {"start": v(2.19, -0.14) * mm, "end": v(-1.57, -3.9) * mm});
            skLineSegment(sketch, "E3.0.3.165", {"start": v(-1.61, -0.14) * mm, "end": v(-5.37, -3.9) * mm});
            skLineSegment(sketch, "E3.0.3.166", {"start": v(-5.41, -0.14) * mm, "end": v(-9.17, -3.9) * mm});
            skLineSegment(sketch, "E3.0.3.167", {"start": v(17.39, -0.14) * mm, "end": v(13.63, -3.9) * mm});
            skLineSegment(sketch, "E3.0.3.168", {"start": v(13.59, -0.14) * mm, "end": v(9.83, -3.9) * mm});
            skLineSegment(sketch, "E3.0.3.169", {"start": v(9.79, -0.14) * mm, "end": v(6.03, -3.9) * mm});
            skLineSegment(sketch, "E3.0.3.170", {"start": v(28.79, -0.14) * mm, "end": v(25.03, -3.9) * mm});
            skLineSegment(sketch, "E3.0.3.171", {"start": v(24.99, -0.14) * mm, "end": v(21.23, -3.9) * mm});
            skLineSegment(sketch, "E3.0.3.172", {"start": v(-20.57, 3.61) * mm, "end": v(-20.94, 3.24) * mm});
            skLineSegment(sketch, "E3.0.3.173", {"start": v(-5.37, 3.61) * mm, "end": v(-5.74, 3.24) * mm});
            skLineSegment(sketch, "E3.0.3.174", {"start": v(-9.17, 3.61) * mm, "end": v(-9.54, 3.24) * mm});
            skLineSegment(sketch, "E3.0.3.175", {"start": v(9.83, 3.61) * mm, "end": v(9.46, 3.24) * mm});
            skLineSegment(sketch, "E3.0.3.176", {"start": v(6.03, 3.61) * mm, "end": v(5.66, 3.24) * mm});
            skLineSegment(sketch, "E3.0.3.177", {"start": v(25.03, 3.61) * mm, "end": v(24.66, 3.24) * mm});
            skLineSegment(sketch, "E3.0.3.178", {"start": v(21.23, 3.61) * mm, "end": v(20.86, 3.24) * mm});
            skLineSegment(sketch, "E3.0.3.179", {"start": v(-22.89, 0.23) * mm, "end": v(-22.51, -0.14) * mm});
            skLineSegment(sketch, "E3.0.3.180", {"start": v(-20.99, 0.23) * mm, "end": v(-24.74, -3.52) * mm});
            skLineSegment(sketch, "E3.0.3.181", {"start": v(-20.61, -0.14) * mm, "end": v(-24.37, -3.9) * mm});
            skLineSegment(sketch, "E3.0.3.182", {"start": v(15.53, 3.61) * mm, "end": v(15.16, 3.24) * mm});
            skLineSegment(sketch, "E3.0.3.183", {"start": v(0.33, 3.61) * mm, "end": v(-0.04, 3.24) * mm});
            skLineSegment(sketch, "E3.0.3.184", {"start": v(-14.87, 3.61) * mm, "end": v(-15.24, 3.24) * mm});
            skLineSegment(sketch, "E3.0.3.185", {"start": v(19.29, -0.14) * mm, "end": v(15.53, -3.9) * mm});
            skLineSegment(sketch, "E3.0.3.186", {"start": v(-11.11, -0.14) * mm, "end": v(-14.87, -3.9) * mm});
            skLineSegment(sketch, "E3.0.3.187", {"start": v(-18.71, -0.14) * mm, "end": v(-22.47, -3.9) * mm});
            skLineSegment(sketch, "E3.0.3.188", {"start": v(15.11, 0.23) * mm, "end": v(11.36, -3.52) * mm});
            skLineSegment(sketch, "E3.0.3.189", {"start": v(18.91, 0.23) * mm, "end": v(15.16, -3.52) * mm});
            skLineSegment(sketch, "E3.0.3.190", {"start": v(-0.09, 0.23) * mm, "end": v(-3.84, -3.52) * mm});
            skLineSegment(sketch, "E3.0.3.191", {"start": v(11.31, 0.23) * mm, "end": v(7.56, -3.52) * mm});
            skLineSegment(sketch, "E3.0.3.192", {"start": v(-15.29, 0.23) * mm, "end": v(-19.04, -3.52) * mm});
            skLineSegment(sketch, "E3.0.3.193", {"start": v(-11.49, 0.23) * mm, "end": v(-15.24, -3.52) * mm});
            skLineSegment(sketch, "E3.0.3.194", {"start": v(-3.89, 0.23) * mm, "end": v(-7.64, -3.52) * mm});
            skLineSegment(sketch, "E3.0.3.195", {"start": v(-7.69, 0.23) * mm, "end": v(-11.44, -3.52) * mm});
            skLineSegment(sketch, "E3.0.3.196", {"start": v(-19.09, 0.23) * mm, "end": v(-22.84, -3.52) * mm});
            skLineSegment(sketch, "E3.0.3.197", {"start": v(3.71, -0.52) * mm, "end": v(-0.04, 3.24) * mm});
            skLineSegment(sketch, "E3.0.3.198", {"start": v(-11.49, -0.52) * mm, "end": v(-15.24, 3.24) * mm});
            skLineSegment(sketch, "E3.0.3.199", {"start": v(18.91, -0.52) * mm, "end": v(15.16, 3.24) * mm});
            skLineSegment(sketch, "E3.0.3.200", {"start": v(-11.11, -0.14) * mm, "end": v(-14.87, 3.61) * mm});
            skLineSegment(sketch, "E3.0.3.201", {"start": v(19.29, -0.14) * mm, "end": v(15.53, 3.61) * mm});
            skLineSegment(sketch, "E3.0.3.202", {"start": v(4.09, -0.14) * mm, "end": v(0.33, 3.61) * mm});
            skLineSegment(sketch, "E3.0.3.203", {"start": v(24.66, -3.52) * mm, "end": v(25.03, -3.9) * mm});
            skLineSegment(sketch, "E3.0.3.204", {"start": v(9.46, -3.52) * mm, "end": v(9.83, -3.9) * mm});
            skLineSegment(sketch, "E3.0.3.205", {"start": v(13.26, -3.52) * mm, "end": v(13.63, -3.9) * mm});
            skLineSegment(sketch, "E3.0.3.206", {"start": v(20.86, -3.52) * mm, "end": v(21.23, -3.9) * mm});
            skLineSegment(sketch, "E3.0.3.207", {"start": v(-5.74, -3.52) * mm, "end": v(-5.37, -3.9) * mm});
            skLineSegment(sketch, "E3.0.3.208", {"start": v(-1.94, -3.52) * mm, "end": v(-1.57, -3.9) * mm});
            skLineSegment(sketch, "E3.0.3.209", {"start": v(5.66, -3.52) * mm, "end": v(6.03, -3.9) * mm});
            skLineSegment(sketch, "E3.0.3.210", {"start": v(1.86, -3.52) * mm, "end": v(2.23, -3.9) * mm});
            skLineSegment(sketch, "E3.0.3.211", {"start": v(-17.14, -3.52) * mm, "end": v(-16.77, -3.9) * mm});
            skLineSegment(sketch, "E3.0.3.212", {"start": v(-9.54, -3.52) * mm, "end": v(-9.17, -3.9) * mm});
            skLineSegment(sketch, "E3.0.3.213", {"start": v(-22.84, -3.52) * mm, "end": v(-22.47, -3.9) * mm});
            skLineSegment(sketch, "E3.0.3.214", {"start": v(-11.44, -3.52) * mm, "end": v(-11.07, -3.9) * mm});
            skLineSegment(sketch, "E3.0.3.215", {"start": v(-15.24, -3.52) * mm, "end": v(-14.87, -3.9) * mm});
            skLineSegment(sketch, "E3.0.3.216", {"start": v(-19.04, -3.52) * mm, "end": v(-18.67, -3.9) * mm});
            skLineSegment(sketch, "E3.0.3.217", {"start": v(18.96, -3.52) * mm, "end": v(19.33, -3.9) * mm});
            skLineSegment(sketch, "E3.0.3.218", {"start": v(15.16, -3.52) * mm, "end": v(15.53, -3.9) * mm});
            skLineSegment(sketch, "E3.0.3.219", {"start": v(-13.01, -0.14) * mm, "end": v(-16.77, 3.61) * mm});
            skLineSegment(sketch, "E3.0.3.220", {"start": v(2.19, -0.14) * mm, "end": v(-1.57, 3.61) * mm});
            skLineSegment(sketch, "E3.0.3.221", {"start": v(17.39, -0.14) * mm, "end": v(13.63, 3.61) * mm});
            skLineSegment(sketch, "E3.0.3.222", {"start": v(-13.39, -0.52) * mm, "end": v(-17.14, 3.24) * mm});
            skLineSegment(sketch, "E3.0.3.223", {"start": v(1.81, -0.52) * mm, "end": v(-1.94, 3.24) * mm});
            skLineSegment(sketch, "E3.0.3.224", {"start": v(17.01, -0.52) * mm, "end": v(13.26, 3.24) * mm});
            skLineSegment(sketch, "E3.0.3.225", {"start": v(-9.59, 0.23) * mm, "end": v(-13.34, -3.52) * mm});
            skLineSegment(sketch, "E3.0.3.226", {"start": v(-17.19, 0.23) * mm, "end": v(-20.94, -3.52) * mm});
            skLineSegment(sketch, "E3.0.3.227", {"start": v(20.81, 0.23) * mm, "end": v(17.06, -3.52) * mm});
            skLineSegment(sketch, "E3.0.3.228", {"start": v(-9.21, -0.14) * mm, "end": v(-12.97, -3.9) * mm});
            skLineSegment(sketch, "E3.0.3.229", {"start": v(-16.81, -0.14) * mm, "end": v(-20.57, -3.9) * mm});
            skLineSegment(sketch, "E3.0.3.230", {"start": v(21.19, -0.14) * mm, "end": v(17.43, -3.9) * mm});
            skLineSegment(sketch, "E3.0.3.231", {"start": v(-12.97, 3.61) * mm, "end": v(-13.34, 3.24) * mm});
            skLineSegment(sketch, "E3.0.3.232", {"start": v(-16.77, 3.61) * mm, "end": v(-17.14, 3.24) * mm});
            skLineSegment(sketch, "E3.0.3.233", {"start": v(2.23, 3.61) * mm, "end": v(1.86, 3.24) * mm});
            skLineSegment(sketch, "E3.0.3.234", {"start": v(-1.57, 3.61) * mm, "end": v(-1.94, 3.24) * mm});
            skLineSegment(sketch, "E3.0.3.235", {"start": v(17.43, 3.61) * mm, "end": v(17.06, 3.24) * mm});
            skLineSegment(sketch, "E3.0.3.236", {"start": v(13.63, 3.61) * mm, "end": v(13.26, 3.24) * mm});
            skLineSegment(sketch, "E3.0.3.237", {"start": v(-24.74, -3.52) * mm, "end": v(-24.37, -3.9) * mm});
            skLineSegment(sketch, "E3.0.3.238", {"start": v(-22.51, -0.14) * mm, "end": v(-22.89, -0.52) * mm});
            skLineSegment(sketch, "E3.0.3.239", {"start": v(-26.64, -3.52) * mm, "end": v(-26.27, -3.9) * mm});
            skLineSegment(sketch, "E3.0.3.240", {"start": v(32.21, 0.23) * mm, "end": v(32.59, -0.14) * mm});
            skLineSegment(sketch, "E3.0.3.241", {"start": v(9.41, 0.23) * mm, "end": v(9.79, -0.14) * mm});
            skLineSegment(sketch, "E3.0.3.242", {"start": v(32.59, -0.14) * mm, "end": v(32.21, -0.52) * mm});
            skLineSegment(sketch, "E3.0.3.243", {"start": v(9.79, -0.14) * mm, "end": v(9.41, -0.52) * mm});
            skLineSegment(sketch, "E3.0.3.244", {"start": v(17.06, -3.52) * mm, "end": v(17.43, -3.9) * mm});
            skLineSegment(sketch, "E3.0.3.245", {"start": v(-20.94, -3.52) * mm, "end": v(-20.57, -3.9) * mm});
            skLineSegment(sketch, "E3.0.3.246", {"start": v(-13.34, -3.52) * mm, "end": v(-12.97, -3.9) * mm});
            skLineSegment(sketch, "E3.0.3.247", {"start": v(11.69, -0.14) * mm, "end": v(11.31, -0.52) * mm});
            skLineSegment(sketch, "E3.0.3.248", {"start": v(11.31, 0.23) * mm, "end": v(11.69, -0.14) * mm});
            skLineSegment(sketch, "E3.0.3.249", {"start": v(28.41, 0.23) * mm, "end": v(28.79, -0.14) * mm});
            skLineSegment(sketch, "E3.0.3.250", {"start": v(13.21, 0.23) * mm, "end": v(13.59, -0.14) * mm});
            skLineSegment(sketch, "E3.0.3.251", {"start": v(1.81, 0.23) * mm, "end": v(2.19, -0.14) * mm});
            skLineSegment(sketch, "E3.0.3.252", {"start": v(-13.39, 0.23) * mm, "end": v(-13.01, -0.14) * mm});
            skLineSegment(sketch, "E3.0.3.253", {"start": v(-5.79, 0.23) * mm, "end": v(-5.41, -0.14) * mm});
            skLineSegment(sketch, "E3.0.3.254", {"start": v(28.79, -0.14) * mm, "end": v(28.41, -0.52) * mm});
            skLineSegment(sketch, "E3.0.3.255", {"start": v(13.59, -0.14) * mm, "end": v(13.21, -0.52) * mm});
            skLineSegment(sketch, "E3.0.3.256", {"start": v(2.19, -0.14) * mm, "end": v(1.81, -0.52) * mm});
            skLineSegment(sketch, "E3.0.3.257", {"start": v(-13.01, -0.14) * mm, "end": v(-13.39, -0.52) * mm});
            skLineSegment(sketch, "E3.0.3.258", {"start": v(-5.41, -0.14) * mm, "end": v(-5.79, -0.52) * mm});
            skLineSegment(sketch, "E3.0.3.259", {"start": v(-7.31, -0.14) * mm, "end": v(-7.69, -0.52) * mm});
            skLineSegment(sketch, "E3.0.3.260", {"start": v(-11.11, -0.14) * mm, "end": v(-11.49, -0.52) * mm});
            skLineSegment(sketch, "E3.0.3.261", {"start": v(7.89, -0.14) * mm, "end": v(7.51, -0.52) * mm});
            skLineSegment(sketch, "E3.0.3.262", {"start": v(4.09, -0.14) * mm, "end": v(3.71, -0.52) * mm});
            skLineSegment(sketch, "E3.0.3.263", {"start": v(26.89, -0.14) * mm, "end": v(26.51, -0.52) * mm});
            skLineSegment(sketch, "E3.0.3.264", {"start": v(30.69, -0.14) * mm, "end": v(30.31, -0.52) * mm});
            skLineSegment(sketch, "E3.0.3.265", {"start": v(-11.49, 0.23) * mm, "end": v(-11.11, -0.14) * mm});
            skLineSegment(sketch, "E3.0.3.266", {"start": v(3.71, 0.23) * mm, "end": v(4.09, -0.14) * mm});
            skLineSegment(sketch, "E3.0.3.267", {"start": v(-7.69, 0.23) * mm, "end": v(-7.31, -0.14) * mm});
            skLineSegment(sketch, "E3.0.3.268", {"start": v(15.11, 0.23) * mm, "end": v(15.49, -0.14) * mm});
            skLineSegment(sketch, "E3.0.3.269", {"start": v(7.51, 0.23) * mm, "end": v(7.89, -0.14) * mm});
            skLineSegment(sketch, "E3.0.3.270", {"start": v(30.31, 0.23) * mm, "end": v(30.69, -0.14) * mm});
            skLineSegment(sketch, "E3.0.3.271", {"start": v(26.51, 0.23) * mm, "end": v(26.89, -0.14) * mm});
            skLineSegment(sketch, "E3.0.3.272", {"start": v(-20.61, -0.14) * mm, "end": v(-20.99, -0.52) * mm});
            skLineSegment(sketch, "E3.0.3.273", {"start": v(-20.99, 0.23) * mm, "end": v(-20.61, -0.14) * mm});
            skLineSegment(sketch, "E3.0.3.274", {"start": v(17.01, 0.23) * mm, "end": v(17.39, -0.14) * mm});
            skLineSegment(sketch, "E3.0.3.275", {"start": v(24.61, 0.23) * mm, "end": v(24.99, -0.14) * mm});
            skLineSegment(sketch, "E3.0.3.276", {"start": v(5.61, 0.23) * mm, "end": v(5.99, -0.14) * mm});
            skLineSegment(sketch, "E3.0.3.277", {"start": v(-17.19, 0.23) * mm, "end": v(-16.81, -0.14) * mm});
            skLineSegment(sketch, "E3.0.3.278", {"start": v(-9.59, 0.23) * mm, "end": v(-9.21, -0.14) * mm});
            skLineSegment(sketch, "E3.0.3.279", {"start": v(17.39, -0.14) * mm, "end": v(17.01, -0.52) * mm});
            skLineSegment(sketch, "E3.0.3.280", {"start": v(24.99, -0.14) * mm, "end": v(24.61, -0.52) * mm});
            skLineSegment(sketch, "E3.0.3.281", {"start": v(5.99, -0.14) * mm, "end": v(5.61, -0.52) * mm});
            skLineSegment(sketch, "E3.0.3.282", {"start": v(-16.81, -0.14) * mm, "end": v(-17.19, -0.52) * mm});
            skLineSegment(sketch, "E3.0.3.283", {"start": v(-9.21, -0.14) * mm, "end": v(-9.59, -0.52) * mm});
            skLineSegment(sketch, "E3.0.3.284", {"start": v(-18.71, -0.14) * mm, "end": v(-19.09, -0.52) * mm});
            skLineSegment(sketch, "E3.0.3.285", {"start": v(-14.91, -0.14) * mm, "end": v(-15.29, -0.52) * mm});
            skLineSegment(sketch, "E3.0.3.286", {"start": v(0.29, -0.14) * mm, "end": v(-0.09, -0.52) * mm});
            skLineSegment(sketch, "E3.0.3.287", {"start": v(23.09, -0.14) * mm, "end": v(22.71, -0.52) * mm});
            skLineSegment(sketch, "E3.0.3.288", {"start": v(15.49, -0.14) * mm, "end": v(15.11, -0.52) * mm});
            skLineSegment(sketch, "E3.0.3.289", {"start": v(-15.29, 0.23) * mm, "end": v(-14.91, -0.14) * mm});
            skLineSegment(sketch, "E3.0.3.290", {"start": v(-19.09, 0.23) * mm, "end": v(-18.71, -0.14) * mm});
            skLineSegment(sketch, "E3.0.3.291", {"start": v(-0.09, 0.23) * mm, "end": v(0.29, -0.14) * mm});
            skLineSegment(sketch, "E3.0.3.292", {"start": v(-3.89, 0.23) * mm, "end": v(-3.51, -0.14) * mm});
            skLineSegment(sketch, "E3.0.3.293", {"start": v(22.71, 0.23) * mm, "end": v(23.09, -0.14) * mm});
            skLineSegment(sketch, "E3.0.3.294", {"start": v(20.81, 0.23) * mm, "end": v(21.19, -0.14) * mm});
            skLineSegment(sketch, "E3.0.3.295", {"start": v(-1.99, 0.23) * mm, "end": v(-1.61, -0.14) * mm});
            skLineSegment(sketch, "E3.0.3.296", {"start": v(21.19, -0.14) * mm, "end": v(20.81, -0.52) * mm});
            skLineSegment(sketch, "E3.0.3.297", {"start": v(-1.61, -0.14) * mm, "end": v(-1.99, -0.52) * mm});
            skLineSegment(sketch, "E3.0.3.298", {"start": v(-3.51, -0.14) * mm, "end": v(-3.89, -0.52) * mm});
            skLineSegment(sketch, "E3.0.3.299", {"start": v(19.29, -0.14) * mm, "end": v(18.91, -0.52) * mm});
            skLineSegment(sketch, "E3.0.3.300", {"start": v(18.91, 0.23) * mm, "end": v(19.29, -0.14) * mm});
            skPoint(sketch, "E3.0.4.0", {"position": v(-22.68, -8.63) * mm});
            skPoint(sketch, "E3.0.4.1", {"position": v(-24.58, -8.63) * mm});
            skPoint(sketch, "E3.0.4.2", {"position": v(-24.58, -5.25) * mm});
            skPoint(sketch, "E3.0.4.3", {"position": v(30.52, -5.25) * mm});
            skPoint(sketch, "E3.0.4.4", {"position": v(-22.68, -5.25) * mm});
            skPoint(sketch, "E3.0.4.5", {"position": v(28.62, -5.25) * mm});
            skPoint(sketch, "E3.0.4.6", {"position": v(30.52, -8.63) * mm});
            skLineSegment(sketch, "E3.0.4.7", {"start": v(32.59, -6.94) * mm, "end": v(28.83, -3.19) * mm});
            skPoint(sketch, "E3.0.4.8", {"position": v(28.62, -8.63) * mm});
            skLineSegment(sketch, "E3.0.4.9", {"start": v(-22.89, -7.32) * mm, "end": v(-26.64, -3.56) * mm});
            skLineSegment(sketch, "E3.0.4.10", {"start": v(-22.89, -6.57) * mm, "end": v(-26.64, -10.32) * mm});
            skPoint(sketch, "E3.0.4.11", {"position": v(5.82, -8.63) * mm});
            skPoint(sketch, "E3.0.4.12", {"position": v(3.92, -8.63) * mm});
            skPoint(sketch, "E3.0.4.13", {"position": v(26.72, -8.63) * mm});
            skPoint(sketch, "E3.0.4.14", {"position": v(26.72, -5.25) * mm});
            skLineSegment(sketch, "E3.0.4.15", {"start": v(32.21, -7.32) * mm, "end": v(28.46, -3.56) * mm});
            skLineSegment(sketch, "E3.0.4.16", {"start": v(32.59, -6.94) * mm, "end": v(28.83, -10.7) * mm});
            skPoint(sketch, "E3.0.4.17", {"position": v(0.12, -8.63) * mm});
            skLineSegment(sketch, "E3.0.4.18", {"start": v(-22.51, -6.94) * mm, "end": v(-26.27, -3.19) * mm});
            skLineSegment(sketch, "E3.0.4.19", {"start": v(-22.51, -6.94) * mm, "end": v(-26.27, -10.7) * mm});
            skPoint(sketch, "E3.0.4.20", {"position": v(-7.48, -8.63) * mm});
            skPoint(sketch, "E3.0.4.21", {"position": v(7.72, -8.63) * mm});
            skPoint(sketch, "E3.0.4.22", {"position": v(22.92, -8.63) * mm});
            skLineSegment(sketch, "E3.0.4.23", {"start": v(30.69, -6.94) * mm, "end": v(26.93, -10.7) * mm});
            skPoint(sketch, "E3.0.4.24", {"position": v(-9.38, -5.25) * mm});
            skPoint(sketch, "E3.0.4.25", {"position": v(5.82, -5.25) * mm});
            skLineSegment(sketch, "E3.0.4.26", {"start": v(7.89, -6.94) * mm, "end": v(4.13, -10.7) * mm});
            skPoint(sketch, "E3.0.4.27", {"position": v(21.02, -5.25) * mm});
            skPoint(sketch, "E3.0.4.28", {"position": v(-9.38, -8.63) * mm});
            skPoint(sketch, "E3.0.4.29", {"position": v(21.02, -8.63) * mm});
            skPoint(sketch, "E3.0.4.30", {"position": v(-11.28, -5.25) * mm});
            skPoint(sketch, "E3.0.4.31", {"position": v(3.92, -5.25) * mm});
            skPoint(sketch, "E3.0.4.32", {"position": v(19.12, -5.25) * mm});
            skLineSegment(sketch, "E3.0.4.33", {"start": v(30.31, -7.32) * mm, "end": v(26.56, -3.56) * mm});
            skLineSegment(sketch, "E3.0.4.34", {"start": v(30.69, -6.94) * mm, "end": v(26.93, -3.19) * mm});
            skPoint(sketch, "E3.0.4.35", {"position": v(-11.28, -8.63) * mm});
            skPoint(sketch, "E3.0.4.36", {"position": v(19.12, -8.63) * mm});
            skPoint(sketch, "E3.0.4.37", {"position": v(-13.18, -5.25) * mm});
            skPoint(sketch, "E3.0.4.38", {"position": v(2.02, -5.25) * mm});
            skPoint(sketch, "E3.0.4.39", {"position": v(17.22, -5.25) * mm});
            skPoint(sketch, "E3.0.4.40", {"position": v(2.02, -8.63) * mm});
            skLineSegment(sketch, "E3.0.4.41", {"start": v(28.46, -10.32) * mm, "end": v(28.83, -10.7) * mm});
            skPoint(sketch, "E3.0.4.42", {"position": v(22.92, -5.25) * mm});
            skPoint(sketch, "E3.0.4.43", {"position": v(7.72, -5.25) * mm});
            skPoint(sketch, "E3.0.4.44", {"position": v(-7.48, -5.25) * mm});
            skPoint(sketch, "E3.0.4.45", {"position": v(24.82, -8.63) * mm});
            skPoint(sketch, "E3.0.4.46", {"position": v(9.62, -8.63) * mm});
            skPoint(sketch, "E3.0.4.47", {"position": v(-5.58, -8.63) * mm});
            skPoint(sketch, "E3.0.4.48", {"position": v(9.62, -5.25) * mm});
            skPoint(sketch, "E3.0.4.49", {"position": v(-5.58, -5.25) * mm});
            skPoint(sketch, "E3.0.4.50", {"position": v(-20.78, -5.25) * mm});
            skPoint(sketch, "E3.0.4.51", {"position": v(24.82, -5.25) * mm});
            skPoint(sketch, "E3.0.4.52", {"position": v(11.52, -8.63) * mm});
            skPoint(sketch, "E3.0.4.53", {"position": v(-3.68, -8.63) * mm});
            skPoint(sketch, "E3.0.4.54", {"position": v(-18.88, -8.63) * mm});
            skPoint(sketch, "E3.0.4.55", {"position": v(11.52, -5.25) * mm});
            skPoint(sketch, "E3.0.4.56", {"position": v(-3.68, -5.25) * mm});
            skPoint(sketch, "E3.0.4.57", {"position": v(-18.88, -5.25) * mm});
            skPoint(sketch, "E3.0.4.58", {"position": v(13.42, -8.63) * mm});
            skPoint(sketch, "E3.0.4.59", {"position": v(-1.78, -8.63) * mm});
            skPoint(sketch, "E3.0.4.60", {"position": v(-16.98, -8.63) * mm});
            skLineSegment(sketch, "E3.0.4.61", {"start": v(32.21, -6.57) * mm, "end": v(28.46, -10.32) * mm});
            skPoint(sketch, "E3.0.4.62", {"position": v(13.42, -5.25) * mm});
            skPoint(sketch, "E3.0.4.63", {"position": v(-1.78, -5.25) * mm});
            skPoint(sketch, "E3.0.4.64", {"position": v(-16.98, -5.25) * mm});
            skPoint(sketch, "E3.0.4.65", {"position": v(15.32, -8.63) * mm});
            skPoint(sketch, "E3.0.4.66", {"position": v(-15.08, -8.63) * mm});
            skLineSegment(sketch, "E3.0.4.67", {"start": v(28.83, -3.19) * mm, "end": v(28.46, -3.56) * mm});
            skLineSegment(sketch, "E3.0.4.68", {"start": v(-26.27, -3.19) * mm, "end": v(-26.64, -3.56) * mm});
            skLineSegment(sketch, "E3.0.4.69", {"start": v(-20.61, -6.94) * mm, "end": v(-24.37, -3.19) * mm});
            skLineSegment(sketch, "E3.0.4.70", {"start": v(-20.99, -7.32) * mm, "end": v(-24.74, -3.56) * mm});
            skLineSegment(sketch, "E3.0.4.71", {"start": v(-24.37, -3.19) * mm, "end": v(-24.74, -3.56) * mm});
            skLineSegment(sketch, "E3.0.4.72", {"start": v(19.33, -3.19) * mm, "end": v(18.96, -3.56) * mm});
            skLineSegment(sketch, "E3.0.4.73", {"start": v(23.13, -3.19) * mm, "end": v(22.76, -3.56) * mm});
            skLineSegment(sketch, "E3.0.4.74", {"start": v(-3.47, -3.19) * mm, "end": v(-3.84, -3.56) * mm});
            skLineSegment(sketch, "E3.0.4.75", {"start": v(4.13, -3.19) * mm, "end": v(3.76, -3.56) * mm});
            skLineSegment(sketch, "E3.0.4.76", {"start": v(7.93, -3.19) * mm, "end": v(7.56, -3.56) * mm});
            skLineSegment(sketch, "E3.0.4.77", {"start": v(-18.67, -3.19) * mm, "end": v(-19.04, -3.56) * mm});
            skLineSegment(sketch, "E3.0.4.78", {"start": v(-11.07, -3.19) * mm, "end": v(-11.44, -3.56) * mm});
            skLineSegment(sketch, "E3.0.4.79", {"start": v(-7.27, -3.19) * mm, "end": v(-7.64, -3.56) * mm});
            skLineSegment(sketch, "E3.0.4.80", {"start": v(-22.47, -3.19) * mm, "end": v(-22.84, -3.56) * mm});
            skLineSegment(sketch, "E3.0.4.81", {"start": v(15.49, -6.94) * mm, "end": v(11.73, -10.7) * mm});
            skLineSegment(sketch, "E3.0.4.82", {"start": v(23.09, -6.94) * mm, "end": v(19.33, -10.7) * mm});
            skLineSegment(sketch, "E3.0.4.83", {"start": v(26.89, -6.94) * mm, "end": v(23.13, -10.7) * mm});
            skLineSegment(sketch, "E3.0.4.84", {"start": v(0.29, -6.94) * mm, "end": v(-3.47, -10.7) * mm});
            skLineSegment(sketch, "E3.0.4.85", {"start": v(4.09, -6.94) * mm, "end": v(0.33, -10.7) * mm});
            skLineSegment(sketch, "E3.0.4.86", {"start": v(11.69, -6.94) * mm, "end": v(7.93, -10.7) * mm});
            skLineSegment(sketch, "E3.0.4.87", {"start": v(-14.91, -6.94) * mm, "end": v(-18.67, -10.7) * mm});
            skLineSegment(sketch, "E3.0.4.88", {"start": v(-7.31, -6.94) * mm, "end": v(-11.07, -10.7) * mm});
            skLineSegment(sketch, "E3.0.4.89", {"start": v(-3.51, -6.94) * mm, "end": v(-7.27, -10.7) * mm});
            skLineSegment(sketch, "E3.0.4.90", {"start": v(22.71, -6.57) * mm, "end": v(18.96, -10.32) * mm});
            skLineSegment(sketch, "E3.0.4.91", {"start": v(26.51, -6.57) * mm, "end": v(22.76, -10.32) * mm});
            skLineSegment(sketch, "E3.0.4.92", {"start": v(3.71, -6.57) * mm, "end": v(-0.04, -10.32) * mm});
            skLineSegment(sketch, "E3.0.4.93", {"start": v(7.51, -6.57) * mm, "end": v(3.76, -10.32) * mm});
            skLineSegment(sketch, "E3.0.4.94", {"start": v(30.31, -6.57) * mm, "end": v(26.56, -10.32) * mm});
            skLineSegment(sketch, "E3.0.4.95", {"start": v(-0.09, -7.32) * mm, "end": v(-3.84, -3.56) * mm});
            skLineSegment(sketch, "E3.0.4.96", {"start": v(7.51, -7.32) * mm, "end": v(3.76, -3.56) * mm});
            skLineSegment(sketch, "E3.0.4.97", {"start": v(11.31, -7.32) * mm, "end": v(7.56, -3.56) * mm});
            skLineSegment(sketch, "E3.0.4.98", {"start": v(-15.29, -7.32) * mm, "end": v(-19.04, -3.56) * mm});
            skLineSegment(sketch, "E3.0.4.99", {"start": v(-7.69, -7.32) * mm, "end": v(-11.44, -3.56) * mm});
            skLineSegment(sketch, "E3.0.4.100", {"start": v(-3.89, -7.32) * mm, "end": v(-7.64, -3.56) * mm});
            skLineSegment(sketch, "E3.0.4.101", {"start": v(-19.09, -7.32) * mm, "end": v(-22.84, -3.56) * mm});
            skLineSegment(sketch, "E3.0.4.102", {"start": v(15.11, -7.32) * mm, "end": v(11.36, -3.56) * mm});
            skLineSegment(sketch, "E3.0.4.103", {"start": v(22.71, -7.32) * mm, "end": v(18.96, -3.56) * mm});
            skLineSegment(sketch, "E3.0.4.104", {"start": v(26.51, -7.32) * mm, "end": v(22.76, -3.56) * mm});
            skLineSegment(sketch, "E3.0.4.105", {"start": v(-14.91, -6.94) * mm, "end": v(-18.67, -3.19) * mm});
            skLineSegment(sketch, "E3.0.4.106", {"start": v(26.93, -3.19) * mm, "end": v(26.56, -3.56) * mm});
            skLineSegment(sketch, "E3.0.4.107", {"start": v(-3.51, -6.94) * mm, "end": v(-7.27, -3.19) * mm});
            skLineSegment(sketch, "E3.0.4.108", {"start": v(-7.31, -6.94) * mm, "end": v(-11.07, -3.19) * mm});
            skLineSegment(sketch, "E3.0.4.109", {"start": v(-18.71, -6.94) * mm, "end": v(-22.47, -3.19) * mm});
            skLineSegment(sketch, "E3.0.4.110", {"start": v(-26.27, -10.7) * mm, "end": v(-24.37, -10.7) * mm, "construction": true});
            skLineSegment(sketch, "E3.0.4.111", {"start": v(15.49, -6.94) * mm, "end": v(11.73, -3.19) * mm});
            skLineSegment(sketch, "E3.0.4.112", {"start": v(23.09, -6.94) * mm, "end": v(19.33, -3.19) * mm});
            skLineSegment(sketch, "E3.0.4.113", {"start": v(0.29, -6.94) * mm, "end": v(-3.47, -3.19) * mm});
            skLineSegment(sketch, "E3.0.4.114", {"start": v(26.89, -6.94) * mm, "end": v(23.13, -3.19) * mm});
            skLineSegment(sketch, "E3.0.4.115", {"start": v(7.89, -6.94) * mm, "end": v(4.13, -3.19) * mm});
            skLineSegment(sketch, "E3.0.4.116", {"start": v(11.69, -6.94) * mm, "end": v(7.93, -3.19) * mm});
            skPoint(sketch, "E3.0.4.117", {"position": v(-13.18, -8.63) * mm});
            skPoint(sketch, "E3.0.4.118", {"position": v(17.22, -8.63) * mm});
            skPoint(sketch, "E3.0.4.119", {"position": v(-15.08, -5.25) * mm});
            skPoint(sketch, "E3.0.4.120", {"position": v(0.12, -5.25) * mm});
            skPoint(sketch, "E3.0.4.121", {"position": v(15.32, -5.25) * mm});
            skLineSegment(sketch, "E3.0.4.122", {"start": v(11.73, -3.19) * mm, "end": v(11.36, -3.56) * mm});
            skLineSegment(sketch, "E3.0.4.123", {"start": v(-7.64, -10.32) * mm, "end": v(-7.27, -10.7) * mm});
            skLineSegment(sketch, "E3.0.4.124", {"start": v(7.56, -10.32) * mm, "end": v(7.93, -10.7) * mm});
            skLineSegment(sketch, "E3.0.4.125", {"start": v(3.76, -10.32) * mm, "end": v(4.13, -10.7) * mm});
            skLineSegment(sketch, "E3.0.4.126", {"start": v(-0.04, -10.32) * mm, "end": v(0.33, -10.7) * mm});
            skLineSegment(sketch, "E3.0.4.127", {"start": v(-3.84, -10.32) * mm, "end": v(-3.47, -10.7) * mm});
            skLineSegment(sketch, "E3.0.4.128", {"start": v(22.76, -10.32) * mm, "end": v(23.13, -10.7) * mm});
            skLineSegment(sketch, "E3.0.4.129", {"start": v(11.36, -10.32) * mm, "end": v(11.73, -10.7) * mm});
            skLineSegment(sketch, "E3.0.4.130", {"start": v(26.56, -10.32) * mm, "end": v(26.93, -10.7) * mm});
            skPoint(sketch, "E3.0.4.131", {"position": v(-20.78, -8.63) * mm});
            skLineSegment(sketch, "E3.0.4.132", {"start": v(-9.21, -6.94) * mm, "end": v(-12.97, -3.19) * mm});
            skLineSegment(sketch, "E3.0.4.133", {"start": v(-16.81, -6.94) * mm, "end": v(-20.57, -3.19) * mm});
            skLineSegment(sketch, "E3.0.4.134", {"start": v(5.99, -6.94) * mm, "end": v(2.23, -3.19) * mm});
            skLineSegment(sketch, "E3.0.4.135", {"start": v(-1.61, -6.94) * mm, "end": v(-5.37, -3.19) * mm});
            skLineSegment(sketch, "E3.0.4.136", {"start": v(-5.41, -6.94) * mm, "end": v(-9.17, -3.19) * mm});
            skLineSegment(sketch, "E3.0.4.137", {"start": v(21.19, -6.94) * mm, "end": v(17.43, -3.19) * mm});
            skLineSegment(sketch, "E3.0.4.138", {"start": v(13.59, -6.94) * mm, "end": v(9.83, -3.19) * mm});
            skLineSegment(sketch, "E3.0.4.139", {"start": v(9.79, -6.94) * mm, "end": v(6.03, -3.19) * mm});
            skLineSegment(sketch, "E3.0.4.140", {"start": v(28.79, -6.94) * mm, "end": v(25.03, -3.19) * mm});
            skLineSegment(sketch, "E3.0.4.141", {"start": v(24.99, -6.94) * mm, "end": v(21.23, -3.19) * mm});
            skLineSegment(sketch, "E3.0.4.142", {"start": v(-9.59, -7.32) * mm, "end": v(-13.34, -3.56) * mm});
            skLineSegment(sketch, "E3.0.4.143", {"start": v(-17.19, -7.32) * mm, "end": v(-20.94, -3.56) * mm});
            skLineSegment(sketch, "E3.0.4.144", {"start": v(5.61, -7.32) * mm, "end": v(1.86, -3.56) * mm});
            skLineSegment(sketch, "E3.0.4.145", {"start": v(-1.99, -7.32) * mm, "end": v(-5.74, -3.56) * mm});
            skLineSegment(sketch, "E3.0.4.146", {"start": v(20.81, -7.32) * mm, "end": v(17.06, -3.56) * mm});
            skLineSegment(sketch, "E3.0.4.147", {"start": v(-5.79, -7.32) * mm, "end": v(-9.54, -3.56) * mm});
            skLineSegment(sketch, "E3.0.4.148", {"start": v(13.21, -7.32) * mm, "end": v(9.46, -3.56) * mm});
            skLineSegment(sketch, "E3.0.4.149", {"start": v(9.41, -7.32) * mm, "end": v(5.66, -3.56) * mm});
            skLineSegment(sketch, "E3.0.4.150", {"start": v(24.61, -7.32) * mm, "end": v(20.86, -3.56) * mm});
            skLineSegment(sketch, "E3.0.4.151", {"start": v(28.41, -7.32) * mm, "end": v(24.66, -3.56) * mm});
            skLineSegment(sketch, "E3.0.4.152", {"start": v(-13.39, -6.57) * mm, "end": v(-17.14, -10.32) * mm});
            skLineSegment(sketch, "E3.0.4.153", {"start": v(5.61, -6.57) * mm, "end": v(1.86, -10.32) * mm});
            skLineSegment(sketch, "E3.0.4.154", {"start": v(1.81, -6.57) * mm, "end": v(-1.94, -10.32) * mm});
            skLineSegment(sketch, "E3.0.4.155", {"start": v(-1.99, -6.57) * mm, "end": v(-5.74, -10.32) * mm});
            skLineSegment(sketch, "E3.0.4.156", {"start": v(-5.79, -6.57) * mm, "end": v(-9.54, -10.32) * mm});
            skLineSegment(sketch, "E3.0.4.157", {"start": v(17.01, -6.57) * mm, "end": v(13.26, -10.32) * mm});
            skLineSegment(sketch, "E3.0.4.158", {"start": v(13.21, -6.57) * mm, "end": v(9.46, -10.32) * mm});
            skLineSegment(sketch, "E3.0.4.159", {"start": v(9.41, -6.57) * mm, "end": v(5.66, -10.32) * mm});
            skLineSegment(sketch, "E3.0.4.160", {"start": v(24.61, -6.57) * mm, "end": v(20.86, -10.32) * mm});
            skLineSegment(sketch, "E3.0.4.161", {"start": v(28.41, -6.57) * mm, "end": v(24.66, -10.32) * mm});
            skLineSegment(sketch, "E3.0.4.162", {"start": v(-13.01, -6.94) * mm, "end": v(-16.77, -10.7) * mm});
            skLineSegment(sketch, "E3.0.4.163", {"start": v(5.99, -6.94) * mm, "end": v(2.23, -10.7) * mm});
            skLineSegment(sketch, "E3.0.4.164", {"start": v(2.19, -6.94) * mm, "end": v(-1.57, -10.7) * mm});
            skLineSegment(sketch, "E3.0.4.165", {"start": v(-1.61, -6.94) * mm, "end": v(-5.37, -10.7) * mm});
            skLineSegment(sketch, "E3.0.4.166", {"start": v(-5.41, -6.94) * mm, "end": v(-9.17, -10.7) * mm});
            skLineSegment(sketch, "E3.0.4.167", {"start": v(17.39, -6.94) * mm, "end": v(13.63, -10.7) * mm});
            skLineSegment(sketch, "E3.0.4.168", {"start": v(13.59, -6.94) * mm, "end": v(9.83, -10.7) * mm});
            skLineSegment(sketch, "E3.0.4.169", {"start": v(9.79, -6.94) * mm, "end": v(6.03, -10.7) * mm});
            skLineSegment(sketch, "E3.0.4.170", {"start": v(28.79, -6.94) * mm, "end": v(25.03, -10.7) * mm});
            skLineSegment(sketch, "E3.0.4.171", {"start": v(24.99, -6.94) * mm, "end": v(21.23, -10.7) * mm});
            skLineSegment(sketch, "E3.0.4.172", {"start": v(-20.57, -3.19) * mm, "end": v(-20.94, -3.56) * mm});
            skLineSegment(sketch, "E3.0.4.173", {"start": v(-5.37, -3.19) * mm, "end": v(-5.74, -3.56) * mm});
            skLineSegment(sketch, "E3.0.4.174", {"start": v(-9.17, -3.19) * mm, "end": v(-9.54, -3.56) * mm});
            skLineSegment(sketch, "E3.0.4.175", {"start": v(9.83, -3.19) * mm, "end": v(9.46, -3.56) * mm});
            skLineSegment(sketch, "E3.0.4.176", {"start": v(6.03, -3.19) * mm, "end": v(5.66, -3.56) * mm});
            skLineSegment(sketch, "E3.0.4.177", {"start": v(25.03, -3.19) * mm, "end": v(24.66, -3.56) * mm});
            skLineSegment(sketch, "E3.0.4.178", {"start": v(21.23, -3.19) * mm, "end": v(20.86, -3.56) * mm});
            skLineSegment(sketch, "E3.0.4.179", {"start": v(-22.89, -6.57) * mm, "end": v(-22.51, -6.94) * mm});
            skLineSegment(sketch, "E3.0.4.180", {"start": v(-20.99, -6.57) * mm, "end": v(-24.74, -10.32) * mm});
            skLineSegment(sketch, "E3.0.4.181", {"start": v(-20.61, -6.94) * mm, "end": v(-24.37, -10.7) * mm});
            skLineSegment(sketch, "E3.0.4.182", {"start": v(15.53, -3.19) * mm, "end": v(15.16, -3.56) * mm});
            skLineSegment(sketch, "E3.0.4.183", {"start": v(0.33, -3.19) * mm, "end": v(-0.04, -3.56) * mm});
            skLineSegment(sketch, "E3.0.4.184", {"start": v(-14.87, -3.19) * mm, "end": v(-15.24, -3.56) * mm});
            skLineSegment(sketch, "E3.0.4.185", {"start": v(19.29, -6.94) * mm, "end": v(15.53, -10.7) * mm});
            skLineSegment(sketch, "E3.0.4.186", {"start": v(-11.11, -6.94) * mm, "end": v(-14.87, -10.7) * mm});
            skLineSegment(sketch, "E3.0.4.187", {"start": v(-18.71, -6.94) * mm, "end": v(-22.47, -10.7) * mm});
            skLineSegment(sketch, "E3.0.4.188", {"start": v(15.11, -6.57) * mm, "end": v(11.36, -10.32) * mm});
            skLineSegment(sketch, "E3.0.4.189", {"start": v(18.91, -6.57) * mm, "end": v(15.16, -10.32) * mm});
            skLineSegment(sketch, "E3.0.4.190", {"start": v(-0.09, -6.57) * mm, "end": v(-3.84, -10.32) * mm});
            skLineSegment(sketch, "E3.0.4.191", {"start": v(11.31, -6.57) * mm, "end": v(7.56, -10.32) * mm});
            skLineSegment(sketch, "E3.0.4.192", {"start": v(-15.29, -6.57) * mm, "end": v(-19.04, -10.32) * mm});
            skLineSegment(sketch, "E3.0.4.193", {"start": v(-11.49, -6.57) * mm, "end": v(-15.24, -10.32) * mm});
            skLineSegment(sketch, "E3.0.4.194", {"start": v(-3.89, -6.57) * mm, "end": v(-7.64, -10.32) * mm});
            skLineSegment(sketch, "E3.0.4.195", {"start": v(-7.69, -6.57) * mm, "end": v(-11.44, -10.32) * mm});
            skLineSegment(sketch, "E3.0.4.196", {"start": v(-19.09, -6.57) * mm, "end": v(-22.84, -10.32) * mm});
            skLineSegment(sketch, "E3.0.4.197", {"start": v(3.71, -7.32) * mm, "end": v(-0.04, -3.56) * mm});
            skLineSegment(sketch, "E3.0.4.198", {"start": v(-11.49, -7.32) * mm, "end": v(-15.24, -3.56) * mm});
            skLineSegment(sketch, "E3.0.4.199", {"start": v(18.91, -7.32) * mm, "end": v(15.16, -3.56) * mm});
            skLineSegment(sketch, "E3.0.4.200", {"start": v(-11.11, -6.94) * mm, "end": v(-14.87, -3.19) * mm});
            skLineSegment(sketch, "E3.0.4.201", {"start": v(19.29, -6.94) * mm, "end": v(15.53, -3.19) * mm});
            skLineSegment(sketch, "E3.0.4.202", {"start": v(4.09, -6.94) * mm, "end": v(0.33, -3.19) * mm});
            skLineSegment(sketch, "E3.0.4.203", {"start": v(24.66, -10.32) * mm, "end": v(25.03, -10.7) * mm});
            skLineSegment(sketch, "E3.0.4.204", {"start": v(9.46, -10.32) * mm, "end": v(9.83, -10.7) * mm});
            skLineSegment(sketch, "E3.0.4.205", {"start": v(13.26, -10.32) * mm, "end": v(13.63, -10.7) * mm});
            skLineSegment(sketch, "E3.0.4.206", {"start": v(20.86, -10.32) * mm, "end": v(21.23, -10.7) * mm});
            skLineSegment(sketch, "E3.0.4.207", {"start": v(-5.74, -10.32) * mm, "end": v(-5.37, -10.7) * mm});
            skLineSegment(sketch, "E3.0.4.208", {"start": v(-1.94, -10.32) * mm, "end": v(-1.57, -10.7) * mm});
            skLineSegment(sketch, "E3.0.4.209", {"start": v(5.66, -10.32) * mm, "end": v(6.03, -10.7) * mm});
            skLineSegment(sketch, "E3.0.4.210", {"start": v(1.86, -10.32) * mm, "end": v(2.23, -10.7) * mm});
            skLineSegment(sketch, "E3.0.4.211", {"start": v(-17.14, -10.32) * mm, "end": v(-16.77, -10.7) * mm});
            skLineSegment(sketch, "E3.0.4.212", {"start": v(-9.54, -10.32) * mm, "end": v(-9.17, -10.7) * mm});
            skLineSegment(sketch, "E3.0.4.213", {"start": v(-22.84, -10.32) * mm, "end": v(-22.47, -10.7) * mm});
            skLineSegment(sketch, "E3.0.4.214", {"start": v(-11.44, -10.32) * mm, "end": v(-11.07, -10.7) * mm});
            skLineSegment(sketch, "E3.0.4.215", {"start": v(-15.24, -10.32) * mm, "end": v(-14.87, -10.7) * mm});
            skLineSegment(sketch, "E3.0.4.216", {"start": v(-19.04, -10.32) * mm, "end": v(-18.67, -10.7) * mm});
            skLineSegment(sketch, "E3.0.4.217", {"start": v(18.96, -10.32) * mm, "end": v(19.33, -10.7) * mm});
            skLineSegment(sketch, "E3.0.4.218", {"start": v(15.16, -10.32) * mm, "end": v(15.53, -10.7) * mm});
            skLineSegment(sketch, "E3.0.4.219", {"start": v(-13.01, -6.94) * mm, "end": v(-16.77, -3.19) * mm});
            skLineSegment(sketch, "E3.0.4.220", {"start": v(2.19, -6.94) * mm, "end": v(-1.57, -3.19) * mm});
            skLineSegment(sketch, "E3.0.4.221", {"start": v(17.39, -6.94) * mm, "end": v(13.63, -3.19) * mm});
            skLineSegment(sketch, "E3.0.4.222", {"start": v(-13.39, -7.32) * mm, "end": v(-17.14, -3.56) * mm});
            skLineSegment(sketch, "E3.0.4.223", {"start": v(1.81, -7.32) * mm, "end": v(-1.94, -3.56) * mm});
            skLineSegment(sketch, "E3.0.4.224", {"start": v(17.01, -7.32) * mm, "end": v(13.26, -3.56) * mm});
            skLineSegment(sketch, "E3.0.4.225", {"start": v(-9.59, -6.57) * mm, "end": v(-13.34, -10.32) * mm});
            skLineSegment(sketch, "E3.0.4.226", {"start": v(-17.19, -6.57) * mm, "end": v(-20.94, -10.32) * mm});
            skLineSegment(sketch, "E3.0.4.227", {"start": v(20.81, -6.57) * mm, "end": v(17.06, -10.32) * mm});
            skLineSegment(sketch, "E3.0.4.228", {"start": v(-9.21, -6.94) * mm, "end": v(-12.97, -10.7) * mm});
            skLineSegment(sketch, "E3.0.4.229", {"start": v(-16.81, -6.94) * mm, "end": v(-20.57, -10.7) * mm});
            skLineSegment(sketch, "E3.0.4.230", {"start": v(21.19, -6.94) * mm, "end": v(17.43, -10.7) * mm});
            skLineSegment(sketch, "E3.0.4.231", {"start": v(-12.97, -3.19) * mm, "end": v(-13.34, -3.56) * mm});
            skLineSegment(sketch, "E3.0.4.232", {"start": v(-16.77, -3.19) * mm, "end": v(-17.14, -3.56) * mm});
            skLineSegment(sketch, "E3.0.4.233", {"start": v(2.23, -3.19) * mm, "end": v(1.86, -3.56) * mm});
            skLineSegment(sketch, "E3.0.4.234", {"start": v(-1.57, -3.19) * mm, "end": v(-1.94, -3.56) * mm});
            skLineSegment(sketch, "E3.0.4.235", {"start": v(17.43, -3.19) * mm, "end": v(17.06, -3.56) * mm});
            skLineSegment(sketch, "E3.0.4.236", {"start": v(13.63, -3.19) * mm, "end": v(13.26, -3.56) * mm});
            skLineSegment(sketch, "E3.0.4.237", {"start": v(-24.74, -10.32) * mm, "end": v(-24.37, -10.7) * mm});
            skLineSegment(sketch, "E3.0.4.238", {"start": v(-22.51, -6.94) * mm, "end": v(-22.89, -7.32) * mm});
            skLineSegment(sketch, "E3.0.4.239", {"start": v(-26.64, -10.32) * mm, "end": v(-26.27, -10.7) * mm});
            skLineSegment(sketch, "E3.0.4.240", {"start": v(32.21, -6.57) * mm, "end": v(32.59, -6.94) * mm});
            skLineSegment(sketch, "E3.0.4.241", {"start": v(9.41, -6.57) * mm, "end": v(9.79, -6.94) * mm});
            skLineSegment(sketch, "E3.0.4.242", {"start": v(32.59, -6.94) * mm, "end": v(32.21, -7.32) * mm});
            skLineSegment(sketch, "E3.0.4.243", {"start": v(9.79, -6.94) * mm, "end": v(9.41, -7.32) * mm});
            skLineSegment(sketch, "E3.0.4.244", {"start": v(17.06, -10.32) * mm, "end": v(17.43, -10.7) * mm});
            skLineSegment(sketch, "E3.0.4.245", {"start": v(-20.94, -10.32) * mm, "end": v(-20.57, -10.7) * mm});
            skLineSegment(sketch, "E3.0.4.246", {"start": v(-13.34, -10.32) * mm, "end": v(-12.97, -10.7) * mm});
            skLineSegment(sketch, "E3.0.4.247", {"start": v(11.69, -6.94) * mm, "end": v(11.31, -7.32) * mm});
            skLineSegment(sketch, "E3.0.4.248", {"start": v(11.31, -6.57) * mm, "end": v(11.69, -6.94) * mm});
            skLineSegment(sketch, "E3.0.4.249", {"start": v(28.41, -6.57) * mm, "end": v(28.79, -6.94) * mm});
            skLineSegment(sketch, "E3.0.4.250", {"start": v(13.21, -6.57) * mm, "end": v(13.59, -6.94) * mm});
            skLineSegment(sketch, "E3.0.4.251", {"start": v(1.81, -6.57) * mm, "end": v(2.19, -6.94) * mm});
            skLineSegment(sketch, "E3.0.4.252", {"start": v(-13.39, -6.57) * mm, "end": v(-13.01, -6.94) * mm});
            skLineSegment(sketch, "E3.0.4.253", {"start": v(-5.79, -6.57) * mm, "end": v(-5.41, -6.94) * mm});
            skLineSegment(sketch, "E3.0.4.254", {"start": v(28.79, -6.94) * mm, "end": v(28.41, -7.32) * mm});
            skLineSegment(sketch, "E3.0.4.255", {"start": v(13.59, -6.94) * mm, "end": v(13.21, -7.32) * mm});
            skLineSegment(sketch, "E3.0.4.256", {"start": v(2.19, -6.94) * mm, "end": v(1.81, -7.32) * mm});
            skLineSegment(sketch, "E3.0.4.257", {"start": v(-13.01, -6.94) * mm, "end": v(-13.39, -7.32) * mm});
            skLineSegment(sketch, "E3.0.4.258", {"start": v(-5.41, -6.94) * mm, "end": v(-5.79, -7.32) * mm});
            skLineSegment(sketch, "E3.0.4.259", {"start": v(-7.31, -6.94) * mm, "end": v(-7.69, -7.32) * mm});
            skLineSegment(sketch, "E3.0.4.260", {"start": v(-11.11, -6.94) * mm, "end": v(-11.49, -7.32) * mm});
            skLineSegment(sketch, "E3.0.4.261", {"start": v(7.89, -6.94) * mm, "end": v(7.51, -7.32) * mm});
            skLineSegment(sketch, "E3.0.4.262", {"start": v(4.09, -6.94) * mm, "end": v(3.71, -7.32) * mm});
            skLineSegment(sketch, "E3.0.4.263", {"start": v(26.89, -6.94) * mm, "end": v(26.51, -7.32) * mm});
            skLineSegment(sketch, "E3.0.4.264", {"start": v(30.69, -6.94) * mm, "end": v(30.31, -7.32) * mm});
            skLineSegment(sketch, "E3.0.4.265", {"start": v(-11.49, -6.57) * mm, "end": v(-11.11, -6.94) * mm});
            skLineSegment(sketch, "E3.0.4.266", {"start": v(3.71, -6.57) * mm, "end": v(4.09, -6.94) * mm});
            skLineSegment(sketch, "E3.0.4.267", {"start": v(-7.69, -6.57) * mm, "end": v(-7.31, -6.94) * mm});
            skLineSegment(sketch, "E3.0.4.268", {"start": v(15.11, -6.57) * mm, "end": v(15.49, -6.94) * mm});
            skLineSegment(sketch, "E3.0.4.269", {"start": v(7.51, -6.57) * mm, "end": v(7.89, -6.94) * mm});
            skLineSegment(sketch, "E3.0.4.270", {"start": v(30.31, -6.57) * mm, "end": v(30.69, -6.94) * mm});
            skLineSegment(sketch, "E3.0.4.271", {"start": v(26.51, -6.57) * mm, "end": v(26.89, -6.94) * mm});
            skLineSegment(sketch, "E3.0.4.272", {"start": v(-20.61, -6.94) * mm, "end": v(-20.99, -7.32) * mm});
            skLineSegment(sketch, "E3.0.4.273", {"start": v(-20.99, -6.57) * mm, "end": v(-20.61, -6.94) * mm});
            skLineSegment(sketch, "E3.0.4.274", {"start": v(17.01, -6.57) * mm, "end": v(17.39, -6.94) * mm});
            skLineSegment(sketch, "E3.0.4.275", {"start": v(24.61, -6.57) * mm, "end": v(24.99, -6.94) * mm});
            skLineSegment(sketch, "E3.0.4.276", {"start": v(5.61, -6.57) * mm, "end": v(5.99, -6.94) * mm});
            skLineSegment(sketch, "E3.0.4.277", {"start": v(-17.19, -6.57) * mm, "end": v(-16.81, -6.94) * mm});
            skLineSegment(sketch, "E3.0.4.278", {"start": v(-9.59, -6.57) * mm, "end": v(-9.21, -6.94) * mm});
            skLineSegment(sketch, "E3.0.4.279", {"start": v(17.39, -6.94) * mm, "end": v(17.01, -7.32) * mm});
            skLineSegment(sketch, "E3.0.4.280", {"start": v(24.99, -6.94) * mm, "end": v(24.61, -7.32) * mm});
            skLineSegment(sketch, "E3.0.4.281", {"start": v(5.99, -6.94) * mm, "end": v(5.61, -7.32) * mm});
            skLineSegment(sketch, "E3.0.4.282", {"start": v(-16.81, -6.94) * mm, "end": v(-17.19, -7.32) * mm});
            skLineSegment(sketch, "E3.0.4.283", {"start": v(-9.21, -6.94) * mm, "end": v(-9.59, -7.32) * mm});
            skLineSegment(sketch, "E3.0.4.284", {"start": v(-18.71, -6.94) * mm, "end": v(-19.09, -7.32) * mm});
            skLineSegment(sketch, "E3.0.4.285", {"start": v(-14.91, -6.94) * mm, "end": v(-15.29, -7.32) * mm});
            skLineSegment(sketch, "E3.0.4.286", {"start": v(0.29, -6.94) * mm, "end": v(-0.09, -7.32) * mm});
            skLineSegment(sketch, "E3.0.4.287", {"start": v(23.09, -6.94) * mm, "end": v(22.71, -7.32) * mm});
            skLineSegment(sketch, "E3.0.4.288", {"start": v(15.49, -6.94) * mm, "end": v(15.11, -7.32) * mm});
            skLineSegment(sketch, "E3.0.4.289", {"start": v(-15.29, -6.57) * mm, "end": v(-14.91, -6.94) * mm});
            skLineSegment(sketch, "E3.0.4.290", {"start": v(-19.09, -6.57) * mm, "end": v(-18.71, -6.94) * mm});
            skLineSegment(sketch, "E3.0.4.291", {"start": v(-0.09, -6.57) * mm, "end": v(0.29, -6.94) * mm});
            skLineSegment(sketch, "E3.0.4.292", {"start": v(-3.89, -6.57) * mm, "end": v(-3.51, -6.94) * mm});
            skLineSegment(sketch, "E3.0.4.293", {"start": v(22.71, -6.57) * mm, "end": v(23.09, -6.94) * mm});
            skLineSegment(sketch, "E3.0.4.294", {"start": v(20.81, -6.57) * mm, "end": v(21.19, -6.94) * mm});
            skLineSegment(sketch, "E3.0.4.295", {"start": v(-1.99, -6.57) * mm, "end": v(-1.61, -6.94) * mm});
            skLineSegment(sketch, "E3.0.4.296", {"start": v(21.19, -6.94) * mm, "end": v(20.81, -7.32) * mm});
            skLineSegment(sketch, "E3.0.4.297", {"start": v(-1.61, -6.94) * mm, "end": v(-1.99, -7.32) * mm});
            skLineSegment(sketch, "E3.0.4.298", {"start": v(-3.51, -6.94) * mm, "end": v(-3.89, -7.32) * mm});
            skLineSegment(sketch, "E3.0.4.299", {"start": v(19.29, -6.94) * mm, "end": v(18.91, -7.32) * mm});
            skLineSegment(sketch, "E3.0.4.300", {"start": v(18.91, -6.57) * mm, "end": v(19.29, -6.94) * mm});
            skLineSegment(sketch, "E3.direction1", {"start": v(-26.27, 16.5) * mm, "end": v(-1.27, 16.5) * mm, "construction": true});
            skLineSegment(sketch, "E3.direction2", {"start": v(-26.27, 16.5) * mm, "end": v(-26.27, 9.7) * mm, "construction": true});
            skSolve(sketch);
        }
        {
            var Q0;
            {var subQ3=sQuery(id+"F0.wireOp",EDGE,"E2.11.0.6");Q0=makeQuery(id+"F0.imprint","IMPRINT",FACE,{"disambiguationData":[TD([[makeQuery(id+"F0.imprint","IMPRINT",EDGE,{"derivedFrom":subQ3}),1.0]])]});}
            var Q1;
            {var subQ3=sQuery(id+"F0.wireOp",EDGE,"E2.10.0.6");Q1=makeQuery(id+"F0.imprint","IMPRINT",FACE,{"disambiguationData":[TD([[makeQuery(id+"F0.imprint","IMPRINT",EDGE,{"derivedFrom":subQ3}),1.0]])]});}
            var Q2;
            {var subQ3=sQuery(id+"F0.wireOp",EDGE,"E2.8.0.6");Q2=makeQuery(id+"F0.imprint","IMPRINT",FACE,{"disambiguationData":[TD([[makeQuery(id+"F0.imprint","IMPRINT",EDGE,{"derivedFrom":subQ3}),1.0]])]});}
            var Q3;
            {var subQ3=sQuery(id+"F0.wireOp",EDGE,"E2.7.0.6");Q3=makeQuery(id+"F0.imprint","IMPRINT",FACE,{"disambiguationData":[TD([[makeQuery(id+"F0.imprint","IMPRINT",EDGE,{"derivedFrom":subQ3}),1.0]])]});}
            var Q4;
            {var subQ3=sQuery(id+"F0.wireOp",EDGE,"E2.3.0.6");Q4=makeQuery(id+"F0.imprint","IMPRINT",FACE,{"disambiguationData":[TD([[makeQuery(id+"F0.imprint","IMPRINT",EDGE,{"derivedFrom":subQ3}),1.0]])]});}
            var Q5;
            {var subQ3=sQuery(id+"F0.wireOp",EDGE,"E2.2.0.6");Q5=makeQuery(id+"F0.imprint","IMPRINT",FACE,{"disambiguationData":[TD([[makeQuery(id+"F0.imprint","IMPRINT",EDGE,{"derivedFrom":subQ3}),1.0]])]});}
            var Q6;
            {var subQ3=sQuery(id+"F0.wireOp",EDGE,"E2.1.0.6");Q6=makeQuery(id+"F0.imprint","IMPRINT",FACE,{"disambiguationData":[TD([[makeQuery(id+"F0.imprint","IMPRINT",EDGE,{"derivedFrom":subQ3}),1.0]])]});}
            var Q7;
            {var subQ0=sQuery(id+"F0.wireOp",EDGE,"E0.top");Q7=makeQuery(id+"F0.imprint","IMPRINT",FACE,{"disambiguationData":[TD([[makeQuery(id+"F0.imprint","IMPRINT",EDGE,{"derivedFrom":subQ0}),1.0]])]});}
            var Q8;
            {var subQ3=sQuery(id+"F0.wireOp",EDGE,"E2.15.0.6");Q8=makeQuery(id+"F0.imprint","IMPRINT",FACE,{"disambiguationData":[TD([[makeQuery(id+"F0.imprint","IMPRINT",EDGE,{"derivedFrom":subQ3}),1.0]])]});}
            var Q9;
            {var subQ5=sQuery(id+"F0.wireOp",EDGE,"E3.0.4.41");Q9=makeQuery(id+"F0.imprint","IMPRINT",FACE,{"disambiguationData":[TD([[makeQuery(id+"F0.imprint","IMPRINT",EDGE,{"derivedFrom":subQ5}),1.0]])]});}
            var Q10;
            {var subQ5=sQuery(id+"F0.wireOp",EDGE,"E3.0.1.96");var subQ6=sQuery(id+"F0.wireOp",EDGE,"E3.0.1.26");var subQ7=makeQuery(id+"F0.imprint","INTERSECT",VERTEX,{"derivedFrom":[subQ6,subQ5]});Q10=makeQuery(id+"F0.imprint","IMPRINT",FACE,{"disambiguationData":[TD([[makeQuery(id+"F0.imprint","IMPRINT",EDGE,{"disambiguationData":[TD([[subQ7,-1.0]])],"derivedFrom":subQ6}),-1.0]])]});}
            var Q11;
            {var subQ3=sQuery(id+"F0.wireOp",EDGE,"E1.top");var subQ5=sQuery(id+"F0.wireOp",EDGE,"E3.0.1.68");var subQ6=makeQuery(id+"F0.imprint","INTERSECT",VERTEX,{"derivedFrom":[subQ3,subQ5]});Q11=makeQuery(id+"F0.imprint","IMPRINT",FACE,{"disambiguationData":[TD([[makeQuery(id+"F0.imprint","IMPRINT",EDGE,{"disambiguationData":[TD([[subQ6,1.0]])],"derivedFrom":subQ3}),1.0]])]});}
            var Q12;
            {var subQ3=sQuery(id+"F0.wireOp",EDGE,"E2.29.0.6");Q12=makeQuery(id+"F0.imprint","IMPRINT",FACE,{"disambiguationData":[TD([[makeQuery(id+"F0.imprint","IMPRINT",EDGE,{"derivedFrom":subQ3}),1.0]])]});}
            var Q13;
            {var subQ3=sQuery(id+"F0.wireOp",EDGE,"E3.0.1.160");var subQ6=sQuery(id+"F0.wireOp",EDGE,"E3.0.1.150");var subQ11=makeQuery(id+"F0.imprint","INTERSECT",VERTEX,{"derivedFrom":[subQ6,subQ3]});Q13=makeQuery(id+"F0.imprint","IMPRINT",FACE,{"disambiguationData":[TD([[makeQuery(id+"F0.imprint","IMPRINT",EDGE,{"disambiguationData":[TD([[subQ11,1.0]])],"derivedFrom":subQ6}),1.0]])]});}
            var Q14;
            {var subQ3=sQuery(id+"F0.wireOp",EDGE,"E3.0.1.225");var subQ6=sQuery(id+"F0.wireOp",EDGE,"E3.0.1.142");var subQ11=makeQuery(id+"F0.imprint","INTERSECT",VERTEX,{"derivedFrom":[subQ6,subQ3]});Q14=makeQuery(id+"F0.imprint","IMPRINT",FACE,{"disambiguationData":[TD([[makeQuery(id+"F0.imprint","IMPRINT",EDGE,{"disambiguationData":[TD([[subQ11,1.0]])],"derivedFrom":subQ6}),1.0]])]});}
            var Q15;
            {var subQ5=sQuery(id+"F0.wireOp",EDGE,"E3.0.1.100");var subQ6=sQuery(id+"F0.wireOp",EDGE,"E3.0.1.89");var subQ7=makeQuery(id+"F0.imprint","INTERSECT",VERTEX,{"derivedFrom":[subQ6,subQ5]});Q15=makeQuery(id+"F0.imprint","IMPRINT",FACE,{"disambiguationData":[TD([[makeQuery(id+"F0.imprint","IMPRINT",EDGE,{"disambiguationData":[TD([[subQ7,-1.0]])],"derivedFrom":subQ6}),-1.0]])]});}
            var Q16;
            {var subQ3=sQuery(id+"F0.wireOp",EDGE,"E3.0.2.10");var subQ6=sQuery(id+"F0.wireOp",EDGE,"E3.0.2.9");var subQ10=makeQuery(id+"F0.imprint","INTERSECT",VERTEX,{"derivedFrom":[subQ6,subQ3]});Q16=makeQuery(id+"F0.imprint","IMPRINT",FACE,{"disambiguationData":[TD([[makeQuery(id+"F0.imprint","IMPRINT",EDGE,{"disambiguationData":[TD([[subQ10,1.0]])],"derivedFrom":subQ6}),1.0]])]});}
            var Q17;
            {var subQ3=sQuery(id+"F0.wireOp",EDGE,"E3.0.1.68");var subQ6=sQuery(id+"F0.wireOp",EDGE,"E1.top");var subQ10=makeQuery(id+"F0.imprint","INTERSECT",VERTEX,{"derivedFrom":[subQ6,subQ3]});Q17=makeQuery(id+"F0.imprint","IMPRINT",FACE,{"disambiguationData":[TD([[makeQuery(id+"F0.imprint","IMPRINT",EDGE,{"disambiguationData":[TD([[subQ10,-1.0]])],"derivedFrom":subQ6}),-1.0]])]});}
            var Q18;
            {var subQ1=sQuery(id+"F0.wireOp",EDGE,"E3.0.1.95");var subQ7=sQuery(id+"F0.wireOp",EDGE,"E3.0.1.84");var subQ8=makeQuery(id+"F0.imprint","INTERSECT",VERTEX,{"derivedFrom":[subQ7,subQ1]});Q18=makeQuery(id+"F0.imprint","IMPRINT",FACE,{"disambiguationData":[TD([[makeQuery(id+"F0.imprint","IMPRINT",EDGE,{"disambiguationData":[TD([[subQ8,-1.0]])],"derivedFrom":subQ7}),-1.0]])]});}
            var Q19;
            {var subQ3=sQuery(id+"F0.wireOp",EDGE,"E3.0.2.81");var subQ9=sQuery(id+"F0.wireOp",EDGE,"E3.0.2.129");var subQ10=makeQuery(id+"F0.imprint","INTERSECT",VERTEX,{"derivedFrom":[subQ3,subQ9]});Q19=makeQuery(id+"F0.imprint","IMPRINT",FACE,{"disambiguationData":[TD([[makeQuery(id+"F0.imprint","IMPRINT",EDGE,{"disambiguationData":[TD([[subQ10,1.0]])],"derivedFrom":subQ3}),1.0]])]});}
            var Q20;
            {var subQ0=sQuery(id+"F0.wireOp",EDGE,"E3.0.2.61");var subQ1=sQuery(id+"F0.wireOp",EDGE,"E3.0.2.15");var subQ2=makeQuery(id+"F0.imprint","INTERSECT",VERTEX,{"derivedFrom":[subQ1,subQ0]});Q20=makeQuery(id+"F0.imprint","IMPRINT",FACE,{"disambiguationData":[TD([[makeQuery(id+"F0.imprint","IMPRINT",EDGE,{"disambiguationData":[TD([[subQ2,1.0]])],"derivedFrom":subQ1}),1.0]])]});}
            var Q21;
            {var subQ7=sQuery(id+"F0.wireOp",EDGE,"E3.0.2.170");var subQ9=sQuery(id+"F0.wireOp",EDGE,"E3.0.2.203");var subQ10=makeQuery(id+"F0.imprint","INTERSECT",VERTEX,{"derivedFrom":[subQ7,subQ9]});Q21=makeQuery(id+"F0.imprint","IMPRINT",FACE,{"disambiguationData":[TD([[makeQuery(id+"F0.imprint","IMPRINT",EDGE,{"disambiguationData":[TD([[subQ10,1.0]])],"derivedFrom":subQ7}),1.0]])]});}
            var Q22;
            {var subQ3=sQuery(id+"F0.wireOp",EDGE,"E3.0.2.162");var subQ6=sQuery(id+"F0.wireOp",EDGE,"E3.0.2.211");var subQ11=makeQuery(id+"F0.imprint","INTERSECT",VERTEX,{"derivedFrom":[subQ3,subQ6]});Q22=makeQuery(id+"F0.imprint","IMPRINT",FACE,{"disambiguationData":[TD([[makeQuery(id+"F0.imprint","IMPRINT",EDGE,{"disambiguationData":[TD([[subQ11,1.0]])],"derivedFrom":subQ3}),1.0]])]});}
            var Q23;
            {var subQ3=sQuery(id+"F0.wireOp",EDGE,"E2.16.0.6");Q23=makeQuery(id+"F0.imprint","IMPRINT",FACE,{"disambiguationData":[TD([[makeQuery(id+"F0.imprint","IMPRINT",EDGE,{"derivedFrom":subQ3}),1.0]])]});}
            var Q24;
            {var subQ7=sQuery(id+"F0.wireOp",EDGE,"E3.0.2.16");var subQ9=sQuery(id+"F0.wireOp",EDGE,"E3.0.2.41");var subQ10=makeQuery(id+"F0.imprint","INTERSECT",VERTEX,{"derivedFrom":[subQ7,subQ9]});Q24=makeQuery(id+"F0.imprint","IMPRINT",FACE,{"disambiguationData":[TD([[makeQuery(id+"F0.imprint","IMPRINT",EDGE,{"disambiguationData":[TD([[subQ10,1.0]])],"derivedFrom":subQ7}),1.0]])]});}
            var Q25;
            {var subQ7=sQuery(id+"F0.wireOp",EDGE,"E3.0.2.163");var subQ9=sQuery(id+"F0.wireOp",EDGE,"E3.0.2.210");var subQ10=makeQuery(id+"F0.imprint","INTERSECT",VERTEX,{"derivedFrom":[subQ7,subQ9]});Q25=makeQuery(id+"F0.imprint","IMPRINT",FACE,{"disambiguationData":[TD([[makeQuery(id+"F0.imprint","IMPRINT",EDGE,{"disambiguationData":[TD([[subQ10,1.0]])],"derivedFrom":subQ7}),1.0]])]});}
            var Q26;
            {var subQ3=sQuery(id+"F0.wireOp",EDGE,"E2.29.0.3");var subQ6=sQuery(id+"F0.wireOp",EDGE,"E2.29.0.1");var subQ10=makeQuery(id+"F0.imprint","INTERSECT",VERTEX,{"derivedFrom":[subQ6,subQ3]});Q26=makeQuery(id+"F0.imprint","IMPRINT",FACE,{"disambiguationData":[TD([[makeQuery(id+"F0.imprint","IMPRINT",EDGE,{"disambiguationData":[TD([[subQ10,1.0]])],"derivedFrom":subQ6}),1.0]])]});}
            var Q27;
            {var subQ0=sQuery(id+"F0.wireOp",EDGE,"E3.0.1.222");var subQ1=sQuery(id+"F0.wireOp",EDGE,"E3.0.1.152");var subQ2=makeQuery(id+"F0.imprint","INTERSECT",VERTEX,{"derivedFrom":[subQ1,subQ0]});Q27=makeQuery(id+"F0.imprint","IMPRINT",FACE,{"disambiguationData":[TD([[makeQuery(id+"F0.imprint","IMPRINT",EDGE,{"disambiguationData":[TD([[subQ2,-1.0]])],"derivedFrom":subQ1}),1.0]])]});}
            var Q28;
            {var subQ1=sQuery(id+"F0.wireOp",EDGE,"E3.0.1.144");var subQ8=sQuery(id+"F0.wireOp",EDGE,"E3.0.1.153");var subQ10=makeQuery(id+"F0.imprint","INTERSECT",VERTEX,{"derivedFrom":[subQ1,subQ8]});Q28=makeQuery(id+"F0.imprint","IMPRINT",FACE,{"disambiguationData":[TD([[makeQuery(id+"F0.imprint","IMPRINT",EDGE,{"disambiguationData":[TD([[subQ10,1.0]])],"derivedFrom":subQ1}),1.0]])]});}
            var Q29;
            {var subQ3=sQuery(id+"F0.wireOp",EDGE,"E2.18.0.6");Q29=makeQuery(id+"F0.imprint","IMPRINT",FACE,{"disambiguationData":[TD([[makeQuery(id+"F0.imprint","IMPRINT",EDGE,{"derivedFrom":subQ3}),1.0]])]});}
            var Q30;
            {var subQ5=sQuery(id+"F0.wireOp",EDGE,"E2.29.0.7");var subQ6=sQuery(id+"F0.wireOp",EDGE,"E2.29.0.5");var subQ7=makeQuery(id+"F0.imprint","INTERSECT",VERTEX,{"derivedFrom":[subQ6,subQ5]});Q30=makeQuery(id+"F0.imprint","IMPRINT",FACE,{"disambiguationData":[TD([[makeQuery(id+"F0.imprint","IMPRINT",EDGE,{"disambiguationData":[TD([[subQ7,1.0]])],"derivedFrom":subQ6}),1.0]])]});}
            var Q31;
            {var subQ6=sQuery(id+"F0.wireOp",EDGE,"E3.0.2.217");var subQ9=sQuery(id+"F0.wireOp",EDGE,"E3.0.2.82");var subQ10=makeQuery(id+"F0.imprint","INTERSECT",VERTEX,{"derivedFrom":[subQ9,subQ6]});Q31=makeQuery(id+"F0.imprint","IMPRINT",FACE,{"disambiguationData":[TD([[makeQuery(id+"F0.imprint","IMPRINT",EDGE,{"disambiguationData":[TD([[subQ10,1.0]])],"derivedFrom":subQ9}),1.0]])]});}
            var Q32;
            {var subQ7=sQuery(id+"F0.wireOp",EDGE,"E3.0.2.239");var subQ8=sQuery(id+"F0.wireOp",EDGE,"E3.0.2.19");var subQ9=makeQuery(id+"F0.imprint","INTERSECT",VERTEX,{"derivedFrom":[subQ8,subQ7]});Q32=makeQuery(id+"F0.imprint","IMPRINT",FACE,{"disambiguationData":[TD([[makeQuery(id+"F0.imprint","IMPRINT",EDGE,{"disambiguationData":[TD([[subQ9,1.0]])],"derivedFrom":subQ8}),1.0]])]});}
            var Q33;
            {var subQ5=sQuery(id+"F0.wireOp",EDGE,"E3.0.2.237");var subQ6=sQuery(id+"F0.wireOp",EDGE,"E3.0.2.181");var subQ7=makeQuery(id+"F0.imprint","INTERSECT",VERTEX,{"derivedFrom":[subQ6,subQ5]});Q33=makeQuery(id+"F0.imprint","IMPRINT",FACE,{"disambiguationData":[TD([[makeQuery(id+"F0.imprint","IMPRINT",EDGE,{"disambiguationData":[TD([[subQ7,1.0]])],"derivedFrom":subQ6}),1.0]])]});}
            var Q34;
            {var subQ5=sQuery(id+"F0.wireOp",EDGE,"E3.0.2.164");var subQ7=sQuery(id+"F0.wireOp",EDGE,"E3.0.2.208");var subQ8=makeQuery(id+"F0.imprint","INTERSECT",VERTEX,{"derivedFrom":[subQ5,subQ7]});Q34=makeQuery(id+"F0.imprint","IMPRINT",FACE,{"disambiguationData":[TD([[makeQuery(id+"F0.imprint","IMPRINT",EDGE,{"disambiguationData":[TD([[subQ8,1.0]])],"derivedFrom":subQ5}),1.0]])]});}
            var Q35;
            {var subQ3=sQuery(id+"F0.wireOp",EDGE,"E3.0.2.230");var subQ5=sQuery(id+"F0.wireOp",EDGE,"E3.0.2.244");var subQ6=makeQuery(id+"F0.imprint","INTERSECT",VERTEX,{"derivedFrom":[subQ3,subQ5]});Q35=makeQuery(id+"F0.imprint","IMPRINT",FACE,{"disambiguationData":[TD([[makeQuery(id+"F0.imprint","IMPRINT",EDGE,{"disambiguationData":[TD([[subQ6,1.0]])],"derivedFrom":subQ3}),1.0]])]});}
            var Q36;
            {var subQ3=sQuery(id+"F0.wireOp",EDGE,"E2.19.0.6");Q36=makeQuery(id+"F0.imprint","IMPRINT",FACE,{"disambiguationData":[TD([[makeQuery(id+"F0.imprint","IMPRINT",EDGE,{"derivedFrom":subQ3}),1.0]])]});}
            var Q37;
            {var subQ3=sQuery(id+"F0.wireOp",EDGE,"E3.0.1.154");var subQ5=sQuery(id+"F0.wireOp",EDGE,"E3.0.1.223");var subQ6=makeQuery(id+"F0.imprint","INTERSECT",VERTEX,{"derivedFrom":[subQ3,subQ5]});Q37=makeQuery(id+"F0.imprint","IMPRINT",FACE,{"disambiguationData":[TD([[makeQuery(id+"F0.imprint","IMPRINT",EDGE,{"disambiguationData":[TD([[subQ6,-1.0]])],"derivedFrom":subQ3}),1.0]])]});}
            var Q38;
            {var subQ1=sQuery(id+"F0.wireOp",EDGE,"E3.0.1.145");var subQ9=sQuery(id+"F0.wireOp",EDGE,"E3.0.1.155");var subQ11=makeQuery(id+"F0.imprint","INTERSECT",VERTEX,{"derivedFrom":[subQ1,subQ9]});Q38=makeQuery(id+"F0.imprint","IMPRINT",FACE,{"disambiguationData":[TD([[makeQuery(id+"F0.imprint","IMPRINT",EDGE,{"disambiguationData":[TD([[subQ11,1.0]])],"derivedFrom":subQ1}),1.0]])]});}
            var Q39;
            {var subQ1=sQuery(id+"F0.wireOp",EDGE,"E3.0.1.70");var subQ5=sQuery(id+"F0.wireOp",EDGE,"E3.0.1.180");var subQ6=makeQuery(id+"F0.imprint","INTERSECT",VERTEX,{"derivedFrom":[subQ1,subQ5]});Q39=makeQuery(id+"F0.imprint","IMPRINT",FACE,{"disambiguationData":[TD([[makeQuery(id+"F0.imprint","IMPRINT",EDGE,{"disambiguationData":[TD([[subQ6,1.0]])],"derivedFrom":subQ1}),1.0]])]});}
            var Q40;
            {var subQ5=sQuery(id+"F0.wireOp",EDGE,"E3.0.2.214");var subQ7=sQuery(id+"F0.wireOp",EDGE,"E3.0.2.88");var subQ8=makeQuery(id+"F0.imprint","INTERSECT",VERTEX,{"derivedFrom":[subQ7,subQ5]});Q40=makeQuery(id+"F0.imprint","IMPRINT",FACE,{"disambiguationData":[TD([[makeQuery(id+"F0.imprint","IMPRINT",EDGE,{"disambiguationData":[TD([[subQ8,1.0]])],"derivedFrom":subQ7}),1.0]])]});}
            var Q41;
            {var subQ3=sQuery(id+"F0.wireOp",EDGE,"E3.0.2.165");var subQ5=sQuery(id+"F0.wireOp",EDGE,"E3.0.2.207");var subQ6=makeQuery(id+"F0.imprint","INTERSECT",VERTEX,{"derivedFrom":[subQ3,subQ5]});Q41=makeQuery(id+"F0.imprint","IMPRINT",FACE,{"disambiguationData":[TD([[makeQuery(id+"F0.imprint","IMPRINT",EDGE,{"disambiguationData":[TD([[subQ6,1.0]])],"derivedFrom":subQ3}),1.0]])]});}
            var Q42;
            {var subQ3=sQuery(id+"F0.wireOp",EDGE,"E3.0.1.10");var subQ6=sQuery(id+"F0.wireOp",EDGE,"E3.0.1.9");var subQ10=makeQuery(id+"F0.imprint","INTERSECT",VERTEX,{"derivedFrom":[subQ6,subQ3]});Q42=makeQuery(id+"F0.imprint","IMPRINT",FACE,{"disambiguationData":[TD([[makeQuery(id+"F0.imprint","IMPRINT",EDGE,{"disambiguationData":[TD([[subQ10,1.0]])],"derivedFrom":subQ6}),1.0]])]});}
            var Q43;
            {var subQ6=sQuery(id+"F0.wireOp",EDGE,"E3.0.2.128");var subQ9=sQuery(id+"F0.wireOp",EDGE,"E3.0.2.83");var subQ10=makeQuery(id+"F0.imprint","INTERSECT",VERTEX,{"derivedFrom":[subQ9,subQ6]});Q43=makeQuery(id+"F0.imprint","IMPRINT",FACE,{"disambiguationData":[TD([[makeQuery(id+"F0.imprint","IMPRINT",EDGE,{"disambiguationData":[TD([[subQ10,1.0]])],"derivedFrom":subQ9}),1.0]])]});}
            var Q44;
            {var subQ3=sQuery(id+"F0.wireOp",EDGE,"E3.0.3.10");var subQ6=sQuery(id+"F0.wireOp",EDGE,"E3.0.3.9");var subQ10=makeQuery(id+"F0.imprint","INTERSECT",VERTEX,{"derivedFrom":[subQ6,subQ3]});Q44=makeQuery(id+"F0.imprint","IMPRINT",FACE,{"disambiguationData":[TD([[makeQuery(id+"F0.imprint","IMPRINT",EDGE,{"disambiguationData":[TD([[subQ10,1.0]])],"derivedFrom":subQ6}),1.0]])]});}
            var Q45;
            {var subQ0=sQuery(id+"F0.wireOp",EDGE,"E3.0.1.61");var subQ1=sQuery(id+"F0.wireOp",EDGE,"E3.0.1.15");var subQ2=makeQuery(id+"F0.imprint","INTERSECT",VERTEX,{"derivedFrom":[subQ1,subQ0]});Q45=makeQuery(id+"F0.imprint","IMPRINT",FACE,{"disambiguationData":[TD([[makeQuery(id+"F0.imprint","IMPRINT",EDGE,{"disambiguationData":[TD([[subQ2,1.0]])],"derivedFrom":subQ1}),1.0]])]});}
            var Q46;
            {var subQ3=sQuery(id+"F0.wireOp",EDGE,"E3.0.2.166");var subQ9=sQuery(id+"F0.wireOp",EDGE,"E3.0.2.212");var subQ10=makeQuery(id+"F0.imprint","INTERSECT",VERTEX,{"derivedFrom":[subQ3,subQ9]});Q46=makeQuery(id+"F0.imprint","IMPRINT",FACE,{"disambiguationData":[TD([[makeQuery(id+"F0.imprint","IMPRINT",EDGE,{"disambiguationData":[TD([[subQ10,1.0]])],"derivedFrom":subQ3}),1.0]])]});}
            var Q47;
            {var subQ0=sQuery(id+"F0.wireOp",EDGE,"E3.0.3.61");var subQ1=sQuery(id+"F0.wireOp",EDGE,"E3.0.3.15");var subQ2=makeQuery(id+"F0.imprint","INTERSECT",VERTEX,{"derivedFrom":[subQ1,subQ0]});Q47=makeQuery(id+"F0.imprint","IMPRINT",FACE,{"disambiguationData":[TD([[makeQuery(id+"F0.imprint","IMPRINT",EDGE,{"disambiguationData":[TD([[subQ2,1.0]])],"derivedFrom":subQ1}),1.0]])]});}
            var Q48;
            {var subQ5=sQuery(id+"F0.wireOp",EDGE,"E3.0.1.98");var subQ7=sQuery(id+"F0.wireOp",EDGE,"E3.0.1.87");var subQ8=makeQuery(id+"F0.imprint","INTERSECT",VERTEX,{"derivedFrom":[subQ7,subQ5]});Q48=makeQuery(id+"F0.imprint","IMPRINT",FACE,{"disambiguationData":[TD([[makeQuery(id+"F0.imprint","IMPRINT",EDGE,{"disambiguationData":[TD([[subQ8,-1.0]])],"derivedFrom":subQ7}),-1.0]])]});}
            var Q49;
            {var subQ3=sQuery(id+"F0.wireOp",EDGE,"E2.23.0.6");Q49=makeQuery(id+"F0.imprint","IMPRINT",FACE,{"disambiguationData":[TD([[makeQuery(id+"F0.imprint","IMPRINT",EDGE,{"derivedFrom":subQ3}),1.0]])]});}
            var Q50;
            {var subQ7=sQuery(id+"F0.wireOp",EDGE,"E3.0.2.127");var subQ9=sQuery(id+"F0.wireOp",EDGE,"E3.0.2.84");var subQ10=makeQuery(id+"F0.imprint","INTERSECT",VERTEX,{"derivedFrom":[subQ9,subQ7]});Q50=makeQuery(id+"F0.imprint","IMPRINT",FACE,{"disambiguationData":[TD([[makeQuery(id+"F0.imprint","IMPRINT",EDGE,{"disambiguationData":[TD([[subQ10,1.0]])],"derivedFrom":subQ9}),1.0]])]});}
            var Q51;
            {var subQ3=sQuery(id+"F0.wireOp",EDGE,"E3.0.2.167");var subQ7=sQuery(id+"F0.wireOp",EDGE,"E3.0.2.205");var subQ8=makeQuery(id+"F0.imprint","INTERSECT",VERTEX,{"derivedFrom":[subQ3,subQ7]});Q51=makeQuery(id+"F0.imprint","IMPRINT",FACE,{"disambiguationData":[TD([[makeQuery(id+"F0.imprint","IMPRINT",EDGE,{"disambiguationData":[TD([[subQ8,1.0]])],"derivedFrom":subQ3}),1.0]])]});}
            var Q52;
            {var subQ5=sQuery(id+"F0.wireOp",EDGE,"E3.0.3.41");var subQ9=sQuery(id+"F0.wireOp",EDGE,"E3.0.3.16");var subQ11=makeQuery(id+"F0.imprint","INTERSECT",VERTEX,{"derivedFrom":[subQ9,subQ5]});Q52=makeQuery(id+"F0.imprint","IMPRINT",FACE,{"disambiguationData":[TD([[makeQuery(id+"F0.imprint","IMPRINT",EDGE,{"disambiguationData":[TD([[subQ11,1.0]])],"derivedFrom":subQ9}),1.0]])]});}
            var Q53;
            {var subQ3=sQuery(id+"F0.wireOp",EDGE,"E2.24.0.6");Q53=makeQuery(id+"F0.imprint","IMPRINT",FACE,{"disambiguationData":[TD([[makeQuery(id+"F0.imprint","IMPRINT",EDGE,{"derivedFrom":subQ3}),1.0]])]});}
            var Q54;
            {var subQ7=sQuery(id+"F0.wireOp",EDGE,"E3.0.1.16");var subQ9=sQuery(id+"F0.wireOp",EDGE,"E3.0.1.41");var subQ10=makeQuery(id+"F0.imprint","INTERSECT",VERTEX,{"derivedFrom":[subQ7,subQ9]});Q54=makeQuery(id+"F0.imprint","IMPRINT",FACE,{"disambiguationData":[TD([[makeQuery(id+"F0.imprint","IMPRINT",EDGE,{"disambiguationData":[TD([[subQ10,1.0]])],"derivedFrom":subQ7}),1.0]])]});}
            var Q55;
            {var subQ6=sQuery(id+"F0.wireOp",EDGE,"E3.0.2.125");var subQ9=sQuery(id+"F0.wireOp",EDGE,"E3.0.2.26");var subQ10=makeQuery(id+"F0.imprint","INTERSECT",VERTEX,{"derivedFrom":[subQ9,subQ6]});Q55=makeQuery(id+"F0.imprint","IMPRINT",FACE,{"disambiguationData":[TD([[makeQuery(id+"F0.imprint","IMPRINT",EDGE,{"disambiguationData":[TD([[subQ10,1.0]])],"derivedFrom":subQ9}),1.0]])]});}
            var Q56;
            {var subQ1=sQuery(id+"F0.wireOp",EDGE,"E3.0.2.215");var subQ5=sQuery(id+"F0.wireOp",EDGE,"E3.0.2.186");var subQ6=makeQuery(id+"F0.imprint","INTERSECT",VERTEX,{"derivedFrom":[subQ5,subQ1]});Q56=makeQuery(id+"F0.imprint","IMPRINT",FACE,{"disambiguationData":[TD([[makeQuery(id+"F0.imprint","IMPRINT",EDGE,{"disambiguationData":[TD([[subQ6,1.0]])],"derivedFrom":subQ5}),1.0]])]});}
            var Q57;
            {var subQ0=sQuery(id+"F0.wireOp",EDGE,"E3.0.1.196");var subQ1=sQuery(id+"F0.wireOp",EDGE,"E3.0.1.101");var subQ2=makeQuery(id+"F0.imprint","INTERSECT",VERTEX,{"derivedFrom":[subQ1,subQ0]});Q57=makeQuery(id+"F0.imprint","IMPRINT",FACE,{"disambiguationData":[TD([[makeQuery(id+"F0.imprint","IMPRINT",EDGE,{"disambiguationData":[TD([[subQ2,1.0]])],"derivedFrom":subQ1}),1.0]])]});}
            var Q58;
            {var subQ7=sQuery(id+"F0.wireOp",EDGE,"E3.0.3.239");var subQ8=sQuery(id+"F0.wireOp",EDGE,"E3.0.3.19");var subQ9=makeQuery(id+"F0.imprint","INTERSECT",VERTEX,{"derivedFrom":[subQ8,subQ7]});Q58=makeQuery(id+"F0.imprint","IMPRINT",FACE,{"disambiguationData":[TD([[makeQuery(id+"F0.imprint","IMPRINT",EDGE,{"disambiguationData":[TD([[subQ9,1.0]])],"derivedFrom":subQ8}),1.0]])]});}
            var Q59;
            {var subQ3=sQuery(id+"F0.wireOp",EDGE,"E2.26.0.6");Q59=makeQuery(id+"F0.imprint","IMPRINT",FACE,{"disambiguationData":[TD([[makeQuery(id+"F0.imprint","IMPRINT",EDGE,{"derivedFrom":subQ3}),1.0]])]});}
            var Q60;
            {var subQ7=sQuery(id+"F0.wireOp",EDGE,"E3.0.1.239");var subQ8=sQuery(id+"F0.wireOp",EDGE,"E3.0.1.19");var subQ9=makeQuery(id+"F0.imprint","INTERSECT",VERTEX,{"derivedFrom":[subQ8,subQ7]});Q60=makeQuery(id+"F0.imprint","IMPRINT",FACE,{"disambiguationData":[TD([[makeQuery(id+"F0.imprint","IMPRINT",EDGE,{"disambiguationData":[TD([[subQ9,1.0]])],"derivedFrom":subQ8}),1.0]])]});}
            var Q61;
            {var subQ5=sQuery(id+"F0.wireOp",EDGE,"E3.0.1.99");var subQ7=sQuery(id+"F0.wireOp",EDGE,"E3.0.1.88");var subQ8=makeQuery(id+"F0.imprint","INTERSECT",VERTEX,{"derivedFrom":[subQ7,subQ5]});Q61=makeQuery(id+"F0.imprint","IMPRINT",FACE,{"disambiguationData":[TD([[makeQuery(id+"F0.imprint","IMPRINT",EDGE,{"disambiguationData":[TD([[subQ8,-1.0]])],"derivedFrom":subQ7}),-1.0]])]});}
            var Q62;
            {var subQ3=sQuery(id+"F0.wireOp",EDGE,"E2.27.0.6");Q62=makeQuery(id+"F0.imprint","IMPRINT",FACE,{"disambiguationData":[TD([[makeQuery(id+"F0.imprint","IMPRINT",EDGE,{"derivedFrom":subQ3}),1.0]])]});}
            var Q63;
            {var subQ1=sQuery(id+"F0.wireOp",EDGE,"E3.0.1.149");var subQ7=sQuery(id+"F0.wireOp",EDGE,"E3.0.1.159");var subQ8=makeQuery(id+"F0.imprint","INTERSECT",VERTEX,{"derivedFrom":[subQ1,subQ7]});Q63=makeQuery(id+"F0.imprint","IMPRINT",FACE,{"disambiguationData":[TD([[makeQuery(id+"F0.imprint","IMPRINT",EDGE,{"disambiguationData":[TD([[subQ8,1.0]])],"derivedFrom":subQ1}),1.0]])]});}
            var Q64;
            {var subQ5=sQuery(id+"F0.wireOp",EDGE,"E3.0.1.104");var subQ9=sQuery(id+"F0.wireOp",EDGE,"E3.0.1.83");var subQ11=makeQuery(id+"F0.imprint","INTERSECT",VERTEX,{"derivedFrom":[subQ9,subQ5]});Q64=makeQuery(id+"F0.imprint","IMPRINT",FACE,{"disambiguationData":[TD([[makeQuery(id+"F0.imprint","IMPRINT",EDGE,{"disambiguationData":[TD([[subQ11,-1.0]])],"derivedFrom":subQ9}),-1.0]])]});}
            var Q65;
            {var subQ1=sQuery(id+"F0.wireOp",EDGE,"E3.0.1.33");var subQ5=sQuery(id+"F0.wireOp",EDGE,"E3.0.1.23");var subQ6=makeQuery(id+"F0.imprint","INTERSECT",VERTEX,{"derivedFrom":[subQ5,subQ1]});Q65=makeQuery(id+"F0.imprint","IMPRINT",FACE,{"disambiguationData":[TD([[makeQuery(id+"F0.imprint","IMPRINT",EDGE,{"disambiguationData":[TD([[subQ6,-1.0]])],"derivedFrom":subQ5}),-1.0]])]});}
            var Q66;
            {var subQ3=sQuery(id+"F0.wireOp",EDGE,"E2.12.0.6");Q66=makeQuery(id+"F0.imprint","IMPRINT",FACE,{"disambiguationData":[TD([[makeQuery(id+"F0.imprint","IMPRINT",EDGE,{"derivedFrom":subQ3}),1.0]])]});}
            var Q67;
            {var subQ3=sQuery(id+"F0.wireOp",EDGE,"E2.9.0.6");Q67=makeQuery(id+"F0.imprint","IMPRINT",FACE,{"disambiguationData":[TD([[makeQuery(id+"F0.imprint","IMPRINT",EDGE,{"derivedFrom":subQ3}),1.0]])]});}
            var Q68;
            {var subQ3=sQuery(id+"F0.wireOp",EDGE,"E2.6.0.6");Q68=makeQuery(id+"F0.imprint","IMPRINT",FACE,{"disambiguationData":[TD([[makeQuery(id+"F0.imprint","IMPRINT",EDGE,{"derivedFrom":subQ3}),1.0]])]});}
            var Q69;
            {var subQ3=sQuery(id+"F0.wireOp",EDGE,"E2.5.0.6");Q69=makeQuery(id+"F0.imprint","IMPRINT",FACE,{"disambiguationData":[TD([[makeQuery(id+"F0.imprint","IMPRINT",EDGE,{"derivedFrom":subQ3}),1.0]])]});}
            var Q70;
            {var subQ3=sQuery(id+"F0.wireOp",EDGE,"E2.4.0.6");Q70=makeQuery(id+"F0.imprint","IMPRINT",FACE,{"disambiguationData":[TD([[makeQuery(id+"F0.imprint","IMPRINT",EDGE,{"derivedFrom":subQ3}),1.0]])]});}
            var Q71;
            {var subQ3=sQuery(id+"F0.wireOp",EDGE,"E2.14.0.6");Q71=makeQuery(id+"F0.imprint","IMPRINT",FACE,{"disambiguationData":[TD([[makeQuery(id+"F0.imprint","IMPRINT",EDGE,{"derivedFrom":subQ3}),1.0]])]});}
            var Q72;
            {var subQ3=sQuery(id+"F0.wireOp",EDGE,"E2.13.0.6");Q72=makeQuery(id+"F0.imprint","IMPRINT",FACE,{"disambiguationData":[TD([[makeQuery(id+"F0.imprint","IMPRINT",EDGE,{"derivedFrom":subQ3}),1.0]])]});}
            var Q73;
            {var subQ5=sQuery(id+"F0.wireOp",EDGE,"E3.0.1.198");var subQ6=sQuery(id+"F0.wireOp",EDGE,"E3.0.1.186");var subQ7=makeQuery(id+"F0.imprint","INTERSECT",VERTEX,{"derivedFrom":[subQ6,subQ5]});Q73=makeQuery(id+"F0.imprint","IMPRINT",FACE,{"disambiguationData":[TD([[makeQuery(id+"F0.imprint","IMPRINT",EDGE,{"disambiguationData":[TD([[subQ7,-1.0]])],"derivedFrom":subQ6}),-1.0]])]});}
            var Q74;
            {var subQ3=sQuery(id+"F0.wireOp",EDGE,"E3.0.1.161");var subQ5=sQuery(id+"F0.wireOp",EDGE,"E3.0.1.151");var subQ6=makeQuery(id+"F0.imprint","INTERSECT",VERTEX,{"derivedFrom":[subQ5,subQ3]});Q74=makeQuery(id+"F0.imprint","IMPRINT",FACE,{"disambiguationData":[TD([[makeQuery(id+"F0.imprint","IMPRINT",EDGE,{"disambiguationData":[TD([[subQ6,1.0]])],"derivedFrom":subQ5}),1.0]])]});}
            var Q75;
            {var subQ0=sQuery(id+"F0.wireOp",EDGE,"E3.0.1.226");var subQ1=sQuery(id+"F0.wireOp",EDGE,"E3.0.1.143");var subQ2=makeQuery(id+"F0.imprint","INTERSECT",VERTEX,{"derivedFrom":[subQ1,subQ0]});Q75=makeQuery(id+"F0.imprint","IMPRINT",FACE,{"disambiguationData":[TD([[makeQuery(id+"F0.imprint","IMPRINT",EDGE,{"disambiguationData":[TD([[subQ2,1.0]])],"derivedFrom":subQ1}),1.0]])]});}
            var Q76;
            {var subQ3=sQuery(id+"F0.wireOp",EDGE,"E3.0.1.23");var subQ9=sQuery(id+"F0.wireOp",EDGE,"E3.0.1.130");var subQ11=makeQuery(id+"F0.imprint","INTERSECT",VERTEX,{"derivedFrom":[subQ3,subQ9]});Q76=makeQuery(id+"F0.imprint","IMPRINT",FACE,{"disambiguationData":[TD([[makeQuery(id+"F0.imprint","IMPRINT",EDGE,{"disambiguationData":[TD([[subQ11,1.0]])],"derivedFrom":subQ3}),1.0]])]});}
            var Q77;
            {var subQ3=sQuery(id+"F0.wireOp",EDGE,"E2.28.0.3");var subQ6=sQuery(id+"F0.wireOp",EDGE,"E2.28.0.1");var subQ10=makeQuery(id+"F0.imprint","INTERSECT",VERTEX,{"derivedFrom":[subQ6,subQ3]});Q77=makeQuery(id+"F0.imprint","IMPRINT",FACE,{"disambiguationData":[TD([[makeQuery(id+"F0.imprint","IMPRINT",EDGE,{"disambiguationData":[TD([[subQ10,1.0]])],"derivedFrom":subQ6}),1.0]])]});}
            var Q78;
            {var subQ3=sQuery(id+"F0.wireOp",EDGE,"E3.0.3.23");var subQ5=sQuery(id+"F0.wireOp",EDGE,"E3.0.3.130");var subQ6=makeQuery(id+"F0.imprint","INTERSECT",VERTEX,{"derivedFrom":[subQ3,subQ5]});Q78=makeQuery(id+"F0.imprint","IMPRINT",FACE,{"disambiguationData":[TD([[makeQuery(id+"F0.imprint","IMPRINT",EDGE,{"disambiguationData":[TD([[subQ6,1.0]])],"derivedFrom":subQ3}),1.0]])]});}
            var Q79;
            {var subQ5=sQuery(id+"F0.wireOp",EDGE,"E3.0.4.239");Q79=makeQuery(id+"F0.imprint","IMPRINT",FACE,{"disambiguationData":[TD([[makeQuery(id+"F0.imprint","IMPRINT",EDGE,{"derivedFrom":subQ5}),1.0]])]});}
            var Q80;
            {var subQ3=sQuery(id+"F0.wireOp",EDGE,"E2.28.0.5");var subQ5=sQuery(id+"F0.wireOp",EDGE,"E2.28.0.7");var subQ6=makeQuery(id+"F0.imprint","INTERSECT",VERTEX,{"derivedFrom":[subQ3,subQ5]});Q80=makeQuery(id+"F0.imprint","IMPRINT",FACE,{"disambiguationData":[TD([[makeQuery(id+"F0.imprint","IMPRINT",EDGE,{"disambiguationData":[TD([[subQ6,1.0]])],"derivedFrom":subQ3}),1.0]])]});}
            var Q81;
            {var subQ5=sQuery(id+"F0.wireOp",EDGE,"E3.0.2.124");var subQ7=sQuery(id+"F0.wireOp",EDGE,"E3.0.2.86");var subQ8=makeQuery(id+"F0.imprint","INTERSECT",VERTEX,{"derivedFrom":[subQ7,subQ5]});Q81=makeQuery(id+"F0.imprint","IMPRINT",FACE,{"disambiguationData":[TD([[makeQuery(id+"F0.imprint","IMPRINT",EDGE,{"disambiguationData":[TD([[subQ8,1.0]])],"derivedFrom":subQ7}),1.0]])]});}
            var Q82;
            {var subQ7=sQuery(id+"F0.wireOp",EDGE,"E3.0.2.228");var subQ9=sQuery(id+"F0.wireOp",EDGE,"E3.0.2.246");var subQ10=makeQuery(id+"F0.imprint","INTERSECT",VERTEX,{"derivedFrom":[subQ7,subQ9]});Q82=makeQuery(id+"F0.imprint","IMPRINT",FACE,{"disambiguationData":[TD([[makeQuery(id+"F0.imprint","IMPRINT",EDGE,{"disambiguationData":[TD([[subQ10,1.0]])],"derivedFrom":subQ7}),1.0]])]});}
            var Q83;
            {var subQ3=sQuery(id+"F0.wireOp",EDGE,"E3.0.4.130");Q83=makeQuery(id+"F0.imprint","IMPRINT",FACE,{"disambiguationData":[TD([[makeQuery(id+"F0.imprint","IMPRINT",EDGE,{"derivedFrom":subQ3}),1.0]])]});}
            var Q84;
            {var subQ7=sQuery(id+"F0.wireOp",EDGE,"E3.0.2.171");var subQ9=sQuery(id+"F0.wireOp",EDGE,"E3.0.2.206");var subQ10=makeQuery(id+"F0.imprint","INTERSECT",VERTEX,{"derivedFrom":[subQ7,subQ9]});Q84=makeQuery(id+"F0.imprint","IMPRINT",FACE,{"disambiguationData":[TD([[makeQuery(id+"F0.imprint","IMPRINT",EDGE,{"disambiguationData":[TD([[subQ10,1.0]])],"derivedFrom":subQ7}),1.0]])]});}
            var Q85;
            {var subQ3=sQuery(id+"F0.wireOp",EDGE,"E3.0.2.229");var subQ5=sQuery(id+"F0.wireOp",EDGE,"E3.0.2.245");var subQ6=makeQuery(id+"F0.imprint","INTERSECT",VERTEX,{"derivedFrom":[subQ3,subQ5]});Q85=makeQuery(id+"F0.imprint","IMPRINT",FACE,{"disambiguationData":[TD([[makeQuery(id+"F0.imprint","IMPRINT",EDGE,{"disambiguationData":[TD([[subQ6,1.0]])],"derivedFrom":subQ3}),1.0]])]});}
            var Q86;
            {var subQ3=sQuery(id+"F0.wireOp",EDGE,"E2.17.0.6");Q86=makeQuery(id+"F0.imprint","IMPRINT",FACE,{"disambiguationData":[TD([[makeQuery(id+"F0.imprint","IMPRINT",EDGE,{"derivedFrom":subQ3}),1.0]])]});}
            var Q87;
            {var subQ0=sQuery(id+"F0.wireOp",EDGE,"E3.0.1.197");var subQ1=sQuery(id+"F0.wireOp",EDGE,"E3.0.1.85");var subQ2=makeQuery(id+"F0.imprint","INTERSECT",VERTEX,{"derivedFrom":[subQ1,subQ0]});Q87=makeQuery(id+"F0.imprint","IMPRINT",FACE,{"disambiguationData":[TD([[makeQuery(id+"F0.imprint","IMPRINT",EDGE,{"disambiguationData":[TD([[subQ2,-1.0]])],"derivedFrom":subQ1}),-1.0]])]});}
            var Q88;
            {var subQ5=sQuery(id+"F0.wireOp",EDGE,"E3.0.2.216");var subQ7=sQuery(id+"F0.wireOp",EDGE,"E3.0.2.87");var subQ8=makeQuery(id+"F0.imprint","INTERSECT",VERTEX,{"derivedFrom":[subQ7,subQ5]});Q88=makeQuery(id+"F0.imprint","IMPRINT",FACE,{"disambiguationData":[TD([[makeQuery(id+"F0.imprint","IMPRINT",EDGE,{"disambiguationData":[TD([[subQ8,1.0]])],"derivedFrom":subQ7}),1.0]])]});}
            var Q89;
            {var subQ3=sQuery(id+"F0.wireOp",EDGE,"E2.1.0.5");var subQ5=sQuery(id+"F0.wireOp",EDGE,"E2.1.0.7");var subQ6=makeQuery(id+"F0.imprint","INTERSECT",VERTEX,{"derivedFrom":[subQ3,subQ5]});Q89=makeQuery(id+"F0.imprint","IMPRINT",FACE,{"disambiguationData":[TD([[makeQuery(id+"F0.imprint","IMPRINT",EDGE,{"disambiguationData":[TD([[subQ6,1.0]])],"derivedFrom":subQ3}),1.0]])]});}
            var Q90;
            {var subQ5=sQuery(id+"F0.wireOp",EDGE,"E3.0.4.237");Q90=makeQuery(id+"F0.imprint","IMPRINT",FACE,{"disambiguationData":[TD([[makeQuery(id+"F0.imprint","IMPRINT",EDGE,{"derivedFrom":subQ5}),1.0]])]});}
            var Q91;
            {var subQ3=sQuery(id+"F0.wireOp",EDGE,"E2.20.0.6");Q91=makeQuery(id+"F0.imprint","IMPRINT",FACE,{"disambiguationData":[TD([[makeQuery(id+"F0.imprint","IMPRINT",EDGE,{"derivedFrom":subQ3}),1.0]])]});}
            var Q92;
            {var subQ5=sQuery(id+"F0.wireOp",EDGE,"E3.0.1.97");var subQ7=sQuery(id+"F0.wireOp",EDGE,"E3.0.1.86");var subQ8=makeQuery(id+"F0.imprint","INTERSECT",VERTEX,{"derivedFrom":[subQ7,subQ5]});Q92=makeQuery(id+"F0.imprint","IMPRINT",FACE,{"disambiguationData":[TD([[makeQuery(id+"F0.imprint","IMPRINT",EDGE,{"disambiguationData":[TD([[subQ8,-1.0]])],"derivedFrom":subQ7}),-1.0]])]});}
            var Q93;
            {var subQ1=sQuery(id+"F0.wireOp",EDGE,"E3.0.2.33");var subQ5=sQuery(id+"F0.wireOp",EDGE,"E3.0.2.23");var subQ6=makeQuery(id+"F0.imprint","INTERSECT",VERTEX,{"derivedFrom":[subQ5,subQ1]});Q93=makeQuery(id+"F0.imprint","IMPRINT",FACE,{"disambiguationData":[TD([[makeQuery(id+"F0.imprint","IMPRINT",EDGE,{"disambiguationData":[TD([[subQ6,-1.0]])],"derivedFrom":subQ5}),-1.0]])]});}
            var Q94;
            {var subQ1=sQuery(id+"F0.wireOp",EDGE,"E3.0.3.70");var subQ5=sQuery(id+"F0.wireOp",EDGE,"E3.0.3.180");var subQ6=makeQuery(id+"F0.imprint","INTERSECT",VERTEX,{"derivedFrom":[subQ1,subQ5]});Q94=makeQuery(id+"F0.imprint","IMPRINT",FACE,{"disambiguationData":[TD([[makeQuery(id+"F0.imprint","IMPRINT",EDGE,{"disambiguationData":[TD([[subQ6,1.0]])],"derivedFrom":subQ1}),1.0]])]});}
            var Q95;
            {var subQ3=sQuery(id+"F0.wireOp",EDGE,"E2.21.0.6");Q95=makeQuery(id+"F0.imprint","IMPRINT",FACE,{"disambiguationData":[TD([[makeQuery(id+"F0.imprint","IMPRINT",EDGE,{"derivedFrom":subQ3}),1.0]])]});}
            var Q96;
            {var subQ1=sQuery(id+"F0.wireOp",EDGE,"E3.0.1.102");var subQ7=sQuery(id+"F0.wireOp",EDGE,"E3.0.1.81");var subQ8=makeQuery(id+"F0.imprint","INTERSECT",VERTEX,{"derivedFrom":[subQ7,subQ1]});Q96=makeQuery(id+"F0.imprint","IMPRINT",FACE,{"disambiguationData":[TD([[makeQuery(id+"F0.imprint","IMPRINT",EDGE,{"disambiguationData":[TD([[subQ8,-1.0]])],"derivedFrom":subQ7}),-1.0]])]});}
            var Q97;
            {var subQ0=sQuery(id+"F0.wireOp",EDGE,"E3.0.1.224");var subQ1=sQuery(id+"F0.wireOp",EDGE,"E3.0.1.157");var subQ2=makeQuery(id+"F0.imprint","INTERSECT",VERTEX,{"derivedFrom":[subQ1,subQ0]});Q97=makeQuery(id+"F0.imprint","IMPRINT",FACE,{"disambiguationData":[TD([[makeQuery(id+"F0.imprint","IMPRINT",EDGE,{"disambiguationData":[TD([[subQ2,-1.0]])],"derivedFrom":subQ1}),1.0]])]});}
            var Q98;
            {var subQ3=sQuery(id+"F0.wireOp",EDGE,"E3.0.1.227");var subQ6=sQuery(id+"F0.wireOp",EDGE,"E3.0.1.146");var subQ10=makeQuery(id+"F0.imprint","INTERSECT",VERTEX,{"derivedFrom":[subQ6,subQ3]});Q98=makeQuery(id+"F0.imprint","IMPRINT",FACE,{"disambiguationData":[TD([[makeQuery(id+"F0.imprint","IMPRINT",EDGE,{"disambiguationData":[TD([[subQ10,1.0]])],"derivedFrom":subQ6}),1.0]])]});}
            var Q99;
            {var subQ3=sQuery(id+"F0.wireOp",EDGE,"E3.0.2.23");var subQ9=sQuery(id+"F0.wireOp",EDGE,"E3.0.2.130");var subQ11=makeQuery(id+"F0.imprint","INTERSECT",VERTEX,{"derivedFrom":[subQ3,subQ9]});Q99=makeQuery(id+"F0.imprint","IMPRINT",FACE,{"disambiguationData":[TD([[makeQuery(id+"F0.imprint","IMPRINT",EDGE,{"disambiguationData":[TD([[subQ11,1.0]])],"derivedFrom":subQ3}),1.0]])]});}
            var Q100;
            {var subQ1=sQuery(id+"F0.wireOp",EDGE,"E3.0.2.218");var subQ9=sQuery(id+"F0.wireOp",EDGE,"E3.0.2.185");var subQ10=makeQuery(id+"F0.imprint","INTERSECT",VERTEX,{"derivedFrom":[subQ9,subQ1]});Q100=makeQuery(id+"F0.imprint","IMPRINT",FACE,{"disambiguationData":[TD([[makeQuery(id+"F0.imprint","IMPRINT",EDGE,{"disambiguationData":[TD([[subQ10,1.0]])],"derivedFrom":subQ9}),1.0]])]});}
            var Q101;
            {var subQ3=sQuery(id+"F0.wireOp",EDGE,"E2.22.0.6");Q101=makeQuery(id+"F0.imprint","IMPRINT",FACE,{"disambiguationData":[TD([[makeQuery(id+"F0.imprint","IMPRINT",EDGE,{"derivedFrom":subQ3}),1.0]])]});}
            var Q102;
            {var subQ1=sQuery(id+"F0.wireOp",EDGE,"E3.0.1.147");var subQ7=sQuery(id+"F0.wireOp",EDGE,"E3.0.1.156");var subQ8=makeQuery(id+"F0.imprint","INTERSECT",VERTEX,{"derivedFrom":[subQ1,subQ7]});Q102=makeQuery(id+"F0.imprint","IMPRINT",FACE,{"disambiguationData":[TD([[makeQuery(id+"F0.imprint","IMPRINT",EDGE,{"disambiguationData":[TD([[subQ8,1.0]])],"derivedFrom":subQ1}),1.0]])]});}
            var Q103;
            {var subQ5=sQuery(id+"F0.wireOp",EDGE,"E3.0.2.123");var subQ7=sQuery(id+"F0.wireOp",EDGE,"E3.0.2.89");var subQ8=makeQuery(id+"F0.imprint","INTERSECT",VERTEX,{"derivedFrom":[subQ7,subQ5]});Q103=makeQuery(id+"F0.imprint","IMPRINT",FACE,{"disambiguationData":[TD([[makeQuery(id+"F0.imprint","IMPRINT",EDGE,{"disambiguationData":[TD([[subQ8,1.0]])],"derivedFrom":subQ7}),1.0]])]});}
            var Q104;
            {var subQ0=sQuery(id+"F0.wireOp",EDGE,"E3.0.1.103");var subQ1=sQuery(id+"F0.wireOp",EDGE,"E3.0.1.82");var subQ2=makeQuery(id+"F0.imprint","INTERSECT",VERTEX,{"derivedFrom":[subQ1,subQ0]});Q104=makeQuery(id+"F0.imprint","IMPRINT",FACE,{"disambiguationData":[TD([[makeQuery(id+"F0.imprint","IMPRINT",EDGE,{"disambiguationData":[TD([[subQ2,-1.0]])],"derivedFrom":subQ1}),-1.0]])]});}
            var Q105;
            {var subQ3=sQuery(id+"F0.wireOp",EDGE,"E2.25.0.6");Q105=makeQuery(id+"F0.imprint","IMPRINT",FACE,{"disambiguationData":[TD([[makeQuery(id+"F0.imprint","IMPRINT",EDGE,{"derivedFrom":subQ3}),1.0]])]});}
            var Q106;
            {var subQ3=sQuery(id+"F0.wireOp",EDGE,"E3.0.1.158");var subQ5=sQuery(id+"F0.wireOp",EDGE,"E3.0.1.148");var subQ6=makeQuery(id+"F0.imprint","INTERSECT",VERTEX,{"derivedFrom":[subQ5,subQ3]});Q106=makeQuery(id+"F0.imprint","IMPRINT",FACE,{"disambiguationData":[TD([[makeQuery(id+"F0.imprint","IMPRINT",EDGE,{"disambiguationData":[TD([[subQ6,1.0]])],"derivedFrom":subQ5}),1.0]])]});}
            var Q107;
            {var subQ5=sQuery(id+"F0.wireOp",EDGE,"E3.0.2.126");var subQ6=sQuery(id+"F0.wireOp",EDGE,"E3.0.2.85");var subQ7=makeQuery(id+"F0.imprint","INTERSECT",VERTEX,{"derivedFrom":[subQ6,subQ5]});Q107=makeQuery(id+"F0.imprint","IMPRINT",FACE,{"disambiguationData":[TD([[makeQuery(id+"F0.imprint","IMPRINT",EDGE,{"disambiguationData":[TD([[subQ7,1.0]])],"derivedFrom":subQ6}),1.0]])]});}
            var Q108;
            {var subQ7=sQuery(id+"F0.wireOp",EDGE,"E3.0.2.168");var subQ9=sQuery(id+"F0.wireOp",EDGE,"E3.0.2.204");var subQ10=makeQuery(id+"F0.imprint","INTERSECT",VERTEX,{"derivedFrom":[subQ7,subQ9]});Q108=makeQuery(id+"F0.imprint","IMPRINT",FACE,{"disambiguationData":[TD([[makeQuery(id+"F0.imprint","IMPRINT",EDGE,{"disambiguationData":[TD([[subQ10,1.0]])],"derivedFrom":subQ7}),1.0]])]});}
            var Q109;
            {var subQ5=sQuery(id+"F0.wireOp",EDGE,"E3.0.3.237");var subQ6=sQuery(id+"F0.wireOp",EDGE,"E3.0.3.181");var subQ7=makeQuery(id+"F0.imprint","INTERSECT",VERTEX,{"derivedFrom":[subQ6,subQ5]});Q109=makeQuery(id+"F0.imprint","IMPRINT",FACE,{"disambiguationData":[TD([[makeQuery(id+"F0.imprint","IMPRINT",EDGE,{"disambiguationData":[TD([[subQ7,1.0]])],"derivedFrom":subQ6}),1.0]])]});}
            var Q110;
            {var subQ7=sQuery(id+"F0.wireOp",EDGE,"E3.0.2.213");var subQ9=sQuery(id+"F0.wireOp",EDGE,"E3.0.2.187");var subQ10=makeQuery(id+"F0.imprint","INTERSECT",VERTEX,{"derivedFrom":[subQ9,subQ7]});Q110=makeQuery(id+"F0.imprint","IMPRINT",FACE,{"disambiguationData":[TD([[makeQuery(id+"F0.imprint","IMPRINT",EDGE,{"disambiguationData":[TD([[subQ10,1.0]])],"derivedFrom":subQ9}),1.0]])]});}
            var Q111;
            {var subQ1=sQuery(id+"F0.wireOp",EDGE,"E3.0.3.33");var subQ5=sQuery(id+"F0.wireOp",EDGE,"E3.0.3.23");var subQ6=makeQuery(id+"F0.imprint","INTERSECT",VERTEX,{"derivedFrom":[subQ5,subQ1]});Q111=makeQuery(id+"F0.imprint","IMPRINT",FACE,{"disambiguationData":[TD([[makeQuery(id+"F0.imprint","IMPRINT",EDGE,{"disambiguationData":[TD([[subQ6,-1.0]])],"derivedFrom":subQ5}),-1.0]])]});}
            var Q112;
            {var subQ3=sQuery(id+"F0.wireOp",EDGE,"E2.28.0.6");Q112=makeQuery(id+"F0.imprint","IMPRINT",FACE,{"disambiguationData":[TD([[makeQuery(id+"F0.imprint","IMPRINT",EDGE,{"derivedFrom":subQ3}),1.0]])]});}
            var Q113;
            {var subQ1=sQuery(id+"F0.wireOp",EDGE,"E3.0.2.70");var subQ5=sQuery(id+"F0.wireOp",EDGE,"E3.0.2.180");var subQ6=makeQuery(id+"F0.imprint","INTERSECT",VERTEX,{"derivedFrom":[subQ1,subQ5]});Q113=makeQuery(id+"F0.imprint","IMPRINT",FACE,{"disambiguationData":[TD([[makeQuery(id+"F0.imprint","IMPRINT",EDGE,{"disambiguationData":[TD([[subQ6,1.0]])],"derivedFrom":subQ1}),1.0]])]});}
            var Q114;
            {var subQ7=sQuery(id+"F0.wireOp",EDGE,"E3.0.1.185");var subQ9=sQuery(id+"F0.wireOp",EDGE,"E3.0.1.199");var subQ10=makeQuery(id+"F0.imprint","INTERSECT",VERTEX,{"derivedFrom":[subQ7,subQ9]});Q114=makeQuery(id+"F0.imprint","IMPRINT",FACE,{"disambiguationData":[TD([[makeQuery(id+"F0.imprint","IMPRINT",EDGE,{"disambiguationData":[TD([[subQ10,-1.0]])],"derivedFrom":subQ7}),-1.0]])]});}
            var Q115;
            {var subQ3=sQuery(id+"F0.wireOp",EDGE,"E3.0.2.169");var subQ8=sQuery(id+"F0.wireOp",EDGE,"E3.0.2.209");var subQ11=makeQuery(id+"F0.imprint","INTERSECT",VERTEX,{"derivedFrom":[subQ3,subQ8]});Q115=makeQuery(id+"F0.imprint","IMPRINT",FACE,{"disambiguationData":[TD([[makeQuery(id+"F0.imprint","IMPRINT",EDGE,{"disambiguationData":[TD([[subQ11,1.0]])],"derivedFrom":subQ3}),1.0]])]});}
            var Q116;
            {var subQ1=sQuery(id+"F0.wireOp",EDGE,"E3.0.2.147");var subQ7=sQuery(id+"F0.wireOp",EDGE,"E3.0.2.156");var subQ8=makeQuery(id+"F0.imprint","INTERSECT",VERTEX,{"derivedFrom":[subQ1,subQ7]});Q116=makeQuery(id+"F0.imprint","IMPRINT",FACE,{"disambiguationData":[TD([[makeQuery(id+"F0.imprint","IMPRINT",EDGE,{"disambiguationData":[TD([[subQ8,1.0]])],"derivedFrom":subQ1}),1.0]])]});}
            var Q117;
            {var subQ3=sQuery(id+"F0.wireOp",EDGE,"E3.0.3.161");var subQ7=sQuery(id+"F0.wireOp",EDGE,"E3.0.3.151");var subQ8=makeQuery(id+"F0.imprint","INTERSECT",VERTEX,{"derivedFrom":[subQ7,subQ3]});Q117=makeQuery(id+"F0.imprint","IMPRINT",FACE,{"disambiguationData":[TD([[makeQuery(id+"F0.imprint","IMPRINT",EDGE,{"disambiguationData":[TD([[subQ8,1.0]])],"derivedFrom":subQ7}),1.0]])]});}
            var Q118;
            {var subQ0=sQuery(id+"F0.wireOp",EDGE,"E3.0.3.226");var subQ1=sQuery(id+"F0.wireOp",EDGE,"E3.0.3.143");var subQ2=makeQuery(id+"F0.imprint","INTERSECT",VERTEX,{"derivedFrom":[subQ1,subQ0]});Q118=makeQuery(id+"F0.imprint","IMPRINT",FACE,{"disambiguationData":[TD([[makeQuery(id+"F0.imprint","IMPRINT",EDGE,{"disambiguationData":[TD([[subQ2,1.0]])],"derivedFrom":subQ1}),1.0]])]});}
            var Q119;
            {var subQ5=sQuery(id+"F0.wireOp",EDGE,"E3.0.3.123");var subQ7=sQuery(id+"F0.wireOp",EDGE,"E3.0.3.89");var subQ8=makeQuery(id+"F0.imprint","INTERSECT",VERTEX,{"derivedFrom":[subQ7,subQ5]});Q119=makeQuery(id+"F0.imprint","IMPRINT",FACE,{"disambiguationData":[TD([[makeQuery(id+"F0.imprint","IMPRINT",EDGE,{"disambiguationData":[TD([[subQ8,1.0]])],"derivedFrom":subQ7}),1.0]])]});}
            var Q120;
            {var subQ7=sQuery(id+"F0.wireOp",EDGE,"E3.0.3.186");var subQ9=sQuery(id+"F0.wireOp",EDGE,"E3.0.3.198");var subQ10=makeQuery(id+"F0.imprint","INTERSECT",VERTEX,{"derivedFrom":[subQ7,subQ9]});Q120=makeQuery(id+"F0.imprint","IMPRINT",FACE,{"disambiguationData":[TD([[makeQuery(id+"F0.imprint","IMPRINT",EDGE,{"disambiguationData":[TD([[subQ10,-1.0]])],"derivedFrom":subQ7}),-1.0]])]});}
            var Q121;
            {var subQ5=sQuery(id+"F0.wireOp",EDGE,"E2.8.0.7");var subQ6=sQuery(id+"F0.wireOp",EDGE,"E2.8.0.5");var subQ7=makeQuery(id+"F0.imprint","INTERSECT",VERTEX,{"derivedFrom":[subQ6,subQ5]});Q121=makeQuery(id+"F0.imprint","IMPRINT",FACE,{"disambiguationData":[TD([[makeQuery(id+"F0.imprint","IMPRINT",EDGE,{"disambiguationData":[TD([[subQ7,1.0]])],"derivedFrom":subQ6}),1.0]])]});}
            var Q122;
            {var subQ5=sQuery(id+"F0.wireOp",EDGE,"E2.4.0.7");var subQ6=sQuery(id+"F0.wireOp",EDGE,"E2.4.0.5");var subQ7=makeQuery(id+"F0.imprint","INTERSECT",VERTEX,{"derivedFrom":[subQ6,subQ5]});Q122=makeQuery(id+"F0.imprint","IMPRINT",FACE,{"disambiguationData":[TD([[makeQuery(id+"F0.imprint","IMPRINT",EDGE,{"disambiguationData":[TD([[subQ7,1.0]])],"derivedFrom":subQ6}),1.0]])]});}
            var Q123;
            {var subQ6=sQuery(id+"F0.wireOp",EDGE,"E2.16.0.7");var subQ9=sQuery(id+"F0.wireOp",EDGE,"E2.16.0.5");var subQ10=makeQuery(id+"F0.imprint","INTERSECT",VERTEX,{"derivedFrom":[subQ9,subQ6]});Q123=makeQuery(id+"F0.imprint","IMPRINT",FACE,{"disambiguationData":[TD([[makeQuery(id+"F0.imprint","IMPRINT",EDGE,{"disambiguationData":[TD([[subQ10,1.0]])],"derivedFrom":subQ9}),1.0]])]});}
            var Q124;
            {var subQ5=sQuery(id+"F0.wireOp",EDGE,"E3.0.4.246");Q124=makeQuery(id+"F0.imprint","IMPRINT",FACE,{"disambiguationData":[TD([[makeQuery(id+"F0.imprint","IMPRINT",EDGE,{"derivedFrom":subQ5}),1.0]])]});}
            var Q125;
            {var subQ3=sQuery(id+"F0.wireOp",EDGE,"E3.0.2.227");var subQ6=sQuery(id+"F0.wireOp",EDGE,"E3.0.2.146");var subQ10=makeQuery(id+"F0.imprint","INTERSECT",VERTEX,{"derivedFrom":[subQ6,subQ3]});Q125=makeQuery(id+"F0.imprint","IMPRINT",FACE,{"disambiguationData":[TD([[makeQuery(id+"F0.imprint","IMPRINT",EDGE,{"disambiguationData":[TD([[subQ10,1.0]])],"derivedFrom":subQ6}),1.0]])]});}
            var Q126;
            {var subQ3=sQuery(id+"F0.wireOp",EDGE,"E3.0.3.225");var subQ6=sQuery(id+"F0.wireOp",EDGE,"E3.0.3.142");var subQ11=makeQuery(id+"F0.imprint","INTERSECT",VERTEX,{"derivedFrom":[subQ6,subQ3]});Q126=makeQuery(id+"F0.imprint","IMPRINT",FACE,{"disambiguationData":[TD([[makeQuery(id+"F0.imprint","IMPRINT",EDGE,{"disambiguationData":[TD([[subQ11,1.0]])],"derivedFrom":subQ6}),1.0]])]});}
            var Q127;
            {var subQ5=sQuery(id+"F0.wireOp",EDGE,"E3.0.3.100");var subQ6=sQuery(id+"F0.wireOp",EDGE,"E3.0.3.89");var subQ7=makeQuery(id+"F0.imprint","INTERSECT",VERTEX,{"derivedFrom":[subQ6,subQ5]});Q127=makeQuery(id+"F0.imprint","IMPRINT",FACE,{"disambiguationData":[TD([[makeQuery(id+"F0.imprint","IMPRINT",EDGE,{"disambiguationData":[TD([[subQ7,-1.0]])],"derivedFrom":subQ6}),-1.0]])]});}
            var Q128;
            {var subQ1=sQuery(id+"F0.wireOp",EDGE,"E3.0.3.128");var subQ9=sQuery(id+"F0.wireOp",EDGE,"E3.0.3.83");var subQ10=makeQuery(id+"F0.imprint","INTERSECT",VERTEX,{"derivedFrom":[subQ9,subQ1]});Q128=makeQuery(id+"F0.imprint","IMPRINT",FACE,{"disambiguationData":[TD([[makeQuery(id+"F0.imprint","IMPRINT",EDGE,{"disambiguationData":[TD([[subQ10,1.0]])],"derivedFrom":subQ9}),1.0]])]});}
            var Q129;
            {var subQ3=sQuery(id+"F0.wireOp",EDGE,"E3.0.1.166");var subQ9=sQuery(id+"F0.wireOp",EDGE,"E3.0.1.212");var subQ10=makeQuery(id+"F0.imprint","INTERSECT",VERTEX,{"derivedFrom":[subQ3,subQ9]});Q129=makeQuery(id+"F0.imprint","IMPRINT",FACE,{"disambiguationData":[TD([[makeQuery(id+"F0.imprint","IMPRINT",EDGE,{"disambiguationData":[TD([[subQ10,1.0]])],"derivedFrom":subQ3}),1.0]])]});}
            var Q130;
            {var subQ1=sQuery(id+"F0.wireOp",EDGE,"E3.0.1.218");var subQ9=sQuery(id+"F0.wireOp",EDGE,"E3.0.1.185");var subQ10=makeQuery(id+"F0.imprint","INTERSECT",VERTEX,{"derivedFrom":[subQ9,subQ1]});Q130=makeQuery(id+"F0.imprint","IMPRINT",FACE,{"disambiguationData":[TD([[makeQuery(id+"F0.imprint","IMPRINT",EDGE,{"disambiguationData":[TD([[subQ10,1.0]])],"derivedFrom":subQ9}),1.0]])]});}
            var Q131;
            {var subQ6=sQuery(id+"F0.wireOp",EDGE,"E3.0.3.218");var subQ9=sQuery(id+"F0.wireOp",EDGE,"E3.0.3.185");var subQ10=makeQuery(id+"F0.imprint","INTERSECT",VERTEX,{"derivedFrom":[subQ9,subQ6]});Q131=makeQuery(id+"F0.imprint","IMPRINT",FACE,{"disambiguationData":[TD([[makeQuery(id+"F0.imprint","IMPRINT",EDGE,{"disambiguationData":[TD([[subQ10,1.0]])],"derivedFrom":subQ9}),1.0]])]});}
            var Q132;
            {var subQ3=sQuery(id+"F0.wireOp",EDGE,"E3.0.1.167");var subQ7=sQuery(id+"F0.wireOp",EDGE,"E3.0.1.205");var subQ8=makeQuery(id+"F0.imprint","INTERSECT",VERTEX,{"derivedFrom":[subQ3,subQ7]});Q132=makeQuery(id+"F0.imprint","IMPRINT",FACE,{"disambiguationData":[TD([[makeQuery(id+"F0.imprint","IMPRINT",EDGE,{"disambiguationData":[TD([[subQ8,1.0]])],"derivedFrom":subQ3}),1.0]])]});}
            var Q133;
            {var subQ0=sQuery(id+"F0.wireOp",EDGE,"E3.0.2.103");var subQ1=sQuery(id+"F0.wireOp",EDGE,"E3.0.2.82");var subQ2=makeQuery(id+"F0.imprint","INTERSECT",VERTEX,{"derivedFrom":[subQ1,subQ0]});Q133=makeQuery(id+"F0.imprint","IMPRINT",FACE,{"disambiguationData":[TD([[makeQuery(id+"F0.imprint","IMPRINT",EDGE,{"disambiguationData":[TD([[subQ2,-1.0]])],"derivedFrom":subQ1}),-1.0]])]});}
            var Q134;
            {var subQ7=sQuery(id+"F0.wireOp",EDGE,"E3.0.3.127");var subQ9=sQuery(id+"F0.wireOp",EDGE,"E3.0.3.84");var subQ10=makeQuery(id+"F0.imprint","INTERSECT",VERTEX,{"derivedFrom":[subQ9,subQ7]});Q134=makeQuery(id+"F0.imprint","IMPRINT",FACE,{"disambiguationData":[TD([[makeQuery(id+"F0.imprint","IMPRINT",EDGE,{"disambiguationData":[TD([[subQ10,1.0]])],"derivedFrom":subQ9}),1.0]])]});}
            var Q135;
            {var subQ3=sQuery(id+"F0.wireOp",EDGE,"E2.1.0.3");var subQ6=sQuery(id+"F0.wireOp",EDGE,"E2.1.0.1");var subQ10=makeQuery(id+"F0.imprint","INTERSECT",VERTEX,{"derivedFrom":[subQ6,subQ3]});Q135=makeQuery(id+"F0.imprint","IMPRINT",FACE,{"disambiguationData":[TD([[makeQuery(id+"F0.imprint","IMPRINT",EDGE,{"disambiguationData":[TD([[subQ10,1.0]])],"derivedFrom":subQ6}),1.0]])]});}
            var Q136;
            {var subQ3=sQuery(id+"F0.wireOp",EDGE,"E3.0.4.125");Q136=makeQuery(id+"F0.imprint","IMPRINT",FACE,{"disambiguationData":[TD([[makeQuery(id+"F0.imprint","IMPRINT",EDGE,{"derivedFrom":subQ3}),1.0]])]});}
            var Q137;
            {var subQ3=sQuery(id+"F0.wireOp",EDGE,"E2.9.0.3");var subQ6=sQuery(id+"F0.wireOp",EDGE,"E2.9.0.1");var subQ11=makeQuery(id+"F0.imprint","INTERSECT",VERTEX,{"derivedFrom":[subQ6,subQ3]});Q137=makeQuery(id+"F0.imprint","IMPRINT",FACE,{"disambiguationData":[TD([[makeQuery(id+"F0.imprint","IMPRINT",EDGE,{"disambiguationData":[TD([[subQ11,1.0]])],"derivedFrom":subQ6}),1.0]])]});}
            var Q138;
            {var subQ3=sQuery(id+"F0.wireOp",EDGE,"E3.0.2.158");var subQ5=sQuery(id+"F0.wireOp",EDGE,"E3.0.2.148");var subQ6=makeQuery(id+"F0.imprint","INTERSECT",VERTEX,{"derivedFrom":[subQ5,subQ3]});Q138=makeQuery(id+"F0.imprint","IMPRINT",FACE,{"disambiguationData":[TD([[makeQuery(id+"F0.imprint","IMPRINT",EDGE,{"disambiguationData":[TD([[subQ6,1.0]])],"derivedFrom":subQ5}),1.0]])]});}
            var Q139;
            {var subQ0=sQuery(id+"F0.wireOp",EDGE,"E3.0.2.196");var subQ1=sQuery(id+"F0.wireOp",EDGE,"E3.0.2.101");var subQ2=makeQuery(id+"F0.imprint","INTERSECT",VERTEX,{"derivedFrom":[subQ1,subQ0]});Q139=makeQuery(id+"F0.imprint","IMPRINT",FACE,{"disambiguationData":[TD([[makeQuery(id+"F0.imprint","IMPRINT",EDGE,{"disambiguationData":[TD([[subQ2,1.0]])],"derivedFrom":subQ1}),1.0]])]});}
            var Q140;
            {var subQ3=sQuery(id+"F0.wireOp",EDGE,"E2.21.0.5");var subQ5=sQuery(id+"F0.wireOp",EDGE,"E2.21.0.7");var subQ6=makeQuery(id+"F0.imprint","INTERSECT",VERTEX,{"derivedFrom":[subQ3,subQ5]});Q140=makeQuery(id+"F0.imprint","IMPRINT",FACE,{"disambiguationData":[TD([[makeQuery(id+"F0.imprint","IMPRINT",EDGE,{"disambiguationData":[TD([[subQ6,1.0]])],"derivedFrom":subQ3}),1.0]])]});}
            var Q141;
            {var subQ7=sQuery(id+"F0.wireOp",EDGE,"E2.17.0.5");var subQ9=sQuery(id+"F0.wireOp",EDGE,"E2.17.0.7");var subQ11=makeQuery(id+"F0.imprint","INTERSECT",VERTEX,{"derivedFrom":[subQ7,subQ9]});Q141=makeQuery(id+"F0.imprint","IMPRINT",FACE,{"disambiguationData":[TD([[makeQuery(id+"F0.imprint","IMPRINT",EDGE,{"disambiguationData":[TD([[subQ11,1.0]])],"derivedFrom":subQ7}),1.0]])]});}
            var Q142;
            {var subQ3=sQuery(id+"F0.wireOp",EDGE,"E2.13.0.5");var subQ5=sQuery(id+"F0.wireOp",EDGE,"E2.13.0.7");var subQ6=makeQuery(id+"F0.imprint","INTERSECT",VERTEX,{"derivedFrom":[subQ3,subQ5]});Q142=makeQuery(id+"F0.imprint","IMPRINT",FACE,{"disambiguationData":[TD([[makeQuery(id+"F0.imprint","IMPRINT",EDGE,{"disambiguationData":[TD([[subQ6,1.0]])],"derivedFrom":subQ3}),1.0]])]});}
            var Q143;
            {var subQ5=sQuery(id+"F0.wireOp",EDGE,"E2.9.0.7");var subQ6=sQuery(id+"F0.wireOp",EDGE,"E2.9.0.5");var subQ7=makeQuery(id+"F0.imprint","INTERSECT",VERTEX,{"derivedFrom":[subQ6,subQ5]});Q143=makeQuery(id+"F0.imprint","IMPRINT",FACE,{"disambiguationData":[TD([[makeQuery(id+"F0.imprint","IMPRINT",EDGE,{"disambiguationData":[TD([[subQ7,1.0]])],"derivedFrom":subQ6}),1.0]])]});}
            var Q144;
            {var subQ5=sQuery(id+"F0.wireOp",EDGE,"E3.0.1.126");var subQ6=sQuery(id+"F0.wireOp",EDGE,"E3.0.1.85");var subQ7=makeQuery(id+"F0.imprint","INTERSECT",VERTEX,{"derivedFrom":[subQ6,subQ5]});Q144=makeQuery(id+"F0.imprint","IMPRINT",FACE,{"disambiguationData":[TD([[makeQuery(id+"F0.imprint","IMPRINT",EDGE,{"disambiguationData":[TD([[subQ7,1.0]])],"derivedFrom":subQ6}),1.0]])]});}
            var Q145;
            {var subQ3=sQuery(id+"F0.wireOp",EDGE,"E2.25.0.5");var subQ9=sQuery(id+"F0.wireOp",EDGE,"E2.25.0.7");var subQ10=makeQuery(id+"F0.imprint","INTERSECT",VERTEX,{"derivedFrom":[subQ3,subQ9]});Q145=makeQuery(id+"F0.imprint","IMPRINT",FACE,{"disambiguationData":[TD([[makeQuery(id+"F0.imprint","IMPRINT",EDGE,{"disambiguationData":[TD([[subQ10,1.0]])],"derivedFrom":subQ3}),1.0]])]});}
            var Q146;
            {var subQ7=sQuery(id+"F0.wireOp",EDGE,"E3.0.1.168");var subQ9=sQuery(id+"F0.wireOp",EDGE,"E3.0.1.204");var subQ10=makeQuery(id+"F0.imprint","INTERSECT",VERTEX,{"derivedFrom":[subQ7,subQ9]});Q146=makeQuery(id+"F0.imprint","IMPRINT",FACE,{"disambiguationData":[TD([[makeQuery(id+"F0.imprint","IMPRINT",EDGE,{"disambiguationData":[TD([[subQ10,1.0]])],"derivedFrom":subQ7}),1.0]])]});}
            var Q147;
            {var subQ5=sQuery(id+"F0.wireOp",EDGE,"E3.0.2.99");var subQ7=sQuery(id+"F0.wireOp",EDGE,"E3.0.2.88");var subQ8=makeQuery(id+"F0.imprint","INTERSECT",VERTEX,{"derivedFrom":[subQ7,subQ5]});Q147=makeQuery(id+"F0.imprint","IMPRINT",FACE,{"disambiguationData":[TD([[makeQuery(id+"F0.imprint","IMPRINT",EDGE,{"disambiguationData":[TD([[subQ8,-1.0]])],"derivedFrom":subQ7}),-1.0]])]});}
            var Q148;
            {var subQ3=sQuery(id+"F0.wireOp",EDGE,"E3.0.3.168");var subQ5=sQuery(id+"F0.wireOp",EDGE,"E3.0.3.204");var subQ6=makeQuery(id+"F0.imprint","INTERSECT",VERTEX,{"derivedFrom":[subQ3,subQ5]});Q148=makeQuery(id+"F0.imprint","IMPRINT",FACE,{"disambiguationData":[TD([[makeQuery(id+"F0.imprint","IMPRINT",EDGE,{"disambiguationData":[TD([[subQ6,1.0]])],"derivedFrom":subQ3}),1.0]])]});}
            var Q149;
            {var subQ5=sQuery(id+"F0.wireOp",EDGE,"E3.0.2.104");var subQ9=sQuery(id+"F0.wireOp",EDGE,"E3.0.2.83");var subQ11=makeQuery(id+"F0.imprint","INTERSECT",VERTEX,{"derivedFrom":[subQ9,subQ5]});Q149=makeQuery(id+"F0.imprint","IMPRINT",FACE,{"disambiguationData":[TD([[makeQuery(id+"F0.imprint","IMPRINT",EDGE,{"disambiguationData":[TD([[subQ11,-1.0]])],"derivedFrom":subQ9}),-1.0]])]});}
            var Q150;
            {var subQ7=sQuery(id+"F0.wireOp",EDGE,"E3.0.1.213");var subQ9=sQuery(id+"F0.wireOp",EDGE,"E3.0.1.187");var subQ10=makeQuery(id+"F0.imprint","INTERSECT",VERTEX,{"derivedFrom":[subQ9,subQ7]});Q150=makeQuery(id+"F0.imprint","IMPRINT",FACE,{"disambiguationData":[TD([[makeQuery(id+"F0.imprint","IMPRINT",EDGE,{"disambiguationData":[TD([[subQ10,1.0]])],"derivedFrom":subQ9}),1.0]])]});}
            var Q151;
            {var subQ1=sQuery(id+"F0.wireOp",EDGE,"E3.0.3.213");var subQ5=sQuery(id+"F0.wireOp",EDGE,"E3.0.3.187");var subQ6=makeQuery(id+"F0.imprint","INTERSECT",VERTEX,{"derivedFrom":[subQ5,subQ1]});Q151=makeQuery(id+"F0.imprint","IMPRINT",FACE,{"disambiguationData":[TD([[makeQuery(id+"F0.imprint","IMPRINT",EDGE,{"disambiguationData":[TD([[subQ6,1.0]])],"derivedFrom":subQ5}),1.0]])]});}
            var Q152;
            {var subQ5=sQuery(id+"F0.wireOp",EDGE,"E3.0.4.209");Q152=makeQuery(id+"F0.imprint","IMPRINT",FACE,{"disambiguationData":[TD([[makeQuery(id+"F0.imprint","IMPRINT",EDGE,{"derivedFrom":subQ5}),1.0]])]});}
            var Q153;
            {var subQ3=sQuery(id+"F0.wireOp",EDGE,"E3.0.1.169");var subQ8=sQuery(id+"F0.wireOp",EDGE,"E3.0.1.209");var subQ11=makeQuery(id+"F0.imprint","INTERSECT",VERTEX,{"derivedFrom":[subQ3,subQ8]});Q153=makeQuery(id+"F0.imprint","IMPRINT",FACE,{"disambiguationData":[TD([[makeQuery(id+"F0.imprint","IMPRINT",EDGE,{"disambiguationData":[TD([[subQ11,1.0]])],"derivedFrom":subQ3}),1.0]])]});}
            var Q154;
            {var subQ5=sQuery(id+"F0.wireOp",EDGE,"E3.0.3.97");var subQ7=sQuery(id+"F0.wireOp",EDGE,"E3.0.3.86");var subQ8=makeQuery(id+"F0.imprint","INTERSECT",VERTEX,{"derivedFrom":[subQ7,subQ5]});Q154=makeQuery(id+"F0.imprint","IMPRINT",FACE,{"disambiguationData":[TD([[makeQuery(id+"F0.imprint","IMPRINT",EDGE,{"disambiguationData":[TD([[subQ8,-1.0]])],"derivedFrom":subQ7}),-1.0]])]});}
            var Q155;
            {var subQ3=sQuery(id+"F0.wireOp",EDGE,"E3.0.4.128");Q155=makeQuery(id+"F0.imprint","IMPRINT",FACE,{"disambiguationData":[TD([[makeQuery(id+"F0.imprint","IMPRINT",EDGE,{"derivedFrom":subQ3}),1.0]])]});}
            var Q156;
            {var subQ3=sQuery(id+"F0.wireOp",EDGE,"E2.26.0.3");var subQ6=sQuery(id+"F0.wireOp",EDGE,"E2.26.0.1");var subQ11=makeQuery(id+"F0.imprint","INTERSECT",VERTEX,{"derivedFrom":[subQ6,subQ3]});Q156=makeQuery(id+"F0.imprint","IMPRINT",FACE,{"disambiguationData":[TD([[makeQuery(id+"F0.imprint","IMPRINT",EDGE,{"disambiguationData":[TD([[subQ11,1.0]])],"derivedFrom":subQ6}),1.0]])]});}
            var Q157;
            {var subQ3=sQuery(id+"F0.wireOp",EDGE,"E3.0.2.160");var subQ6=sQuery(id+"F0.wireOp",EDGE,"E3.0.2.150");var subQ11=makeQuery(id+"F0.imprint","INTERSECT",VERTEX,{"derivedFrom":[subQ6,subQ3]});Q157=makeQuery(id+"F0.imprint","IMPRINT",FACE,{"disambiguationData":[TD([[makeQuery(id+"F0.imprint","IMPRINT",EDGE,{"disambiguationData":[TD([[subQ11,1.0]])],"derivedFrom":subQ6}),1.0]])]});}
            var Q158;
            {var subQ3=sQuery(id+"F0.wireOp",EDGE,"E3.0.2.225");var subQ6=sQuery(id+"F0.wireOp",EDGE,"E3.0.2.142");var subQ11=makeQuery(id+"F0.imprint","INTERSECT",VERTEX,{"derivedFrom":[subQ6,subQ3]});Q158=makeQuery(id+"F0.imprint","IMPRINT",FACE,{"disambiguationData":[TD([[makeQuery(id+"F0.imprint","IMPRINT",EDGE,{"disambiguationData":[TD([[subQ11,1.0]])],"derivedFrom":subQ6}),1.0]])]});}
            var Q159;
            {var subQ0=sQuery(id+"F0.wireOp",EDGE,"E3.0.3.224");var subQ1=sQuery(id+"F0.wireOp",EDGE,"E3.0.3.157");var subQ2=makeQuery(id+"F0.imprint","INTERSECT",VERTEX,{"derivedFrom":[subQ1,subQ0]});Q159=makeQuery(id+"F0.imprint","IMPRINT",FACE,{"disambiguationData":[TD([[makeQuery(id+"F0.imprint","IMPRINT",EDGE,{"disambiguationData":[TD([[subQ2,-1.0]])],"derivedFrom":subQ1}),1.0]])]});}
            var Q160;
            {var subQ5=sQuery(id+"F0.wireOp",EDGE,"E2.14.0.7");var subQ6=sQuery(id+"F0.wireOp",EDGE,"E2.14.0.5");var subQ7=makeQuery(id+"F0.imprint","INTERSECT",VERTEX,{"derivedFrom":[subQ6,subQ5]});Q160=makeQuery(id+"F0.imprint","IMPRINT",FACE,{"disambiguationData":[TD([[makeQuery(id+"F0.imprint","IMPRINT",EDGE,{"disambiguationData":[TD([[subQ7,1.0]])],"derivedFrom":subQ6}),1.0]])]});}
            var Q161;
            {var subQ5=sQuery(id+"F0.wireOp",EDGE,"E3.0.1.124");var subQ7=sQuery(id+"F0.wireOp",EDGE,"E3.0.1.86");var subQ8=makeQuery(id+"F0.imprint","INTERSECT",VERTEX,{"derivedFrom":[subQ7,subQ5]});Q161=makeQuery(id+"F0.imprint","IMPRINT",FACE,{"disambiguationData":[TD([[makeQuery(id+"F0.imprint","IMPRINT",EDGE,{"disambiguationData":[TD([[subQ8,1.0]])],"derivedFrom":subQ7}),1.0]])]});}
            var Q162;
            {var subQ7=sQuery(id+"F0.wireOp",EDGE,"E3.0.1.228");var subQ9=sQuery(id+"F0.wireOp",EDGE,"E3.0.1.246");var subQ10=makeQuery(id+"F0.imprint","INTERSECT",VERTEX,{"derivedFrom":[subQ7,subQ9]});Q162=makeQuery(id+"F0.imprint","IMPRINT",FACE,{"disambiguationData":[TD([[makeQuery(id+"F0.imprint","IMPRINT",EDGE,{"disambiguationData":[TD([[subQ10,1.0]])],"derivedFrom":subQ7}),1.0]])]});}
            var Q163;
            {var subQ7=sQuery(id+"F0.wireOp",EDGE,"E3.0.1.170");var subQ9=sQuery(id+"F0.wireOp",EDGE,"E3.0.1.203");var subQ10=makeQuery(id+"F0.imprint","INTERSECT",VERTEX,{"derivedFrom":[subQ7,subQ9]});Q163=makeQuery(id+"F0.imprint","IMPRINT",FACE,{"disambiguationData":[TD([[makeQuery(id+"F0.imprint","IMPRINT",EDGE,{"disambiguationData":[TD([[subQ10,1.0]])],"derivedFrom":subQ7}),1.0]])]});}
            var Q164;
            {var subQ3=sQuery(id+"F0.wireOp",EDGE,"E3.0.1.162");var subQ6=sQuery(id+"F0.wireOp",EDGE,"E3.0.1.211");var subQ11=makeQuery(id+"F0.imprint","INTERSECT",VERTEX,{"derivedFrom":[subQ3,subQ6]});Q164=makeQuery(id+"F0.imprint","IMPRINT",FACE,{"disambiguationData":[TD([[makeQuery(id+"F0.imprint","IMPRINT",EDGE,{"disambiguationData":[TD([[subQ11,1.0]])],"derivedFrom":subQ3}),1.0]])]});}
            var Q165;
            {var subQ1=sQuery(id+"F0.wireOp",EDGE,"E3.0.3.124");var subQ5=sQuery(id+"F0.wireOp",EDGE,"E3.0.3.86");var subQ6=makeQuery(id+"F0.imprint","INTERSECT",VERTEX,{"derivedFrom":[subQ5,subQ1]});Q165=makeQuery(id+"F0.imprint","IMPRINT",FACE,{"disambiguationData":[TD([[makeQuery(id+"F0.imprint","IMPRINT",EDGE,{"disambiguationData":[TD([[subQ6,1.0]])],"derivedFrom":subQ5}),1.0]])]});}
            var Q166;
            {var subQ0=sQuery(id+"F0.wireOp",EDGE,"E3.0.3.129");var subQ1=sQuery(id+"F0.wireOp",EDGE,"E3.0.3.81");var subQ2=makeQuery(id+"F0.imprint","INTERSECT",VERTEX,{"derivedFrom":[subQ1,subQ0]});Q166=makeQuery(id+"F0.imprint","IMPRINT",FACE,{"disambiguationData":[TD([[makeQuery(id+"F0.imprint","IMPRINT",EDGE,{"disambiguationData":[TD([[subQ2,1.0]])],"derivedFrom":subQ1}),1.0]])]});}
            var Q167;
            {var subQ5=sQuery(id+"F0.wireOp",EDGE,"E3.0.4.203");Q167=makeQuery(id+"F0.imprint","IMPRINT",FACE,{"disambiguationData":[TD([[makeQuery(id+"F0.imprint","IMPRINT",EDGE,{"derivedFrom":subQ5}),1.0]])]});}
            var Q168;
            {var subQ3=sQuery(id+"F0.wireOp",EDGE,"E3.0.4.127");Q168=makeQuery(id+"F0.imprint","IMPRINT",FACE,{"disambiguationData":[TD([[makeQuery(id+"F0.imprint","IMPRINT",EDGE,{"derivedFrom":subQ3}),1.0]])]});}
            var Q169;
            {var subQ3=sQuery(id+"F0.wireOp",EDGE,"E3.0.3.170");var subQ6=sQuery(id+"F0.wireOp",EDGE,"E3.0.3.203");var subQ10=makeQuery(id+"F0.imprint","INTERSECT",VERTEX,{"derivedFrom":[subQ3,subQ6]});Q169=makeQuery(id+"F0.imprint","IMPRINT",FACE,{"disambiguationData":[TD([[makeQuery(id+"F0.imprint","IMPRINT",EDGE,{"disambiguationData":[TD([[subQ10,1.0]])],"derivedFrom":subQ3}),1.0]])]});}
            var Q170;
            {var subQ5=sQuery(id+"F0.wireOp",EDGE,"E3.0.3.211");var subQ6=sQuery(id+"F0.wireOp",EDGE,"E3.0.3.162");var subQ7=makeQuery(id+"F0.imprint","INTERSECT",VERTEX,{"derivedFrom":[subQ6,subQ5]});Q170=makeQuery(id+"F0.imprint","IMPRINT",FACE,{"disambiguationData":[TD([[makeQuery(id+"F0.imprint","IMPRINT",EDGE,{"disambiguationData":[TD([[subQ7,1.0]])],"derivedFrom":subQ6}),1.0]])]});}
            var Q171;
            {var subQ5=sQuery(id+"F0.wireOp",EDGE,"E2.26.0.7");var subQ6=sQuery(id+"F0.wireOp",EDGE,"E2.26.0.5");var subQ7=makeQuery(id+"F0.imprint","INTERSECT",VERTEX,{"derivedFrom":[subQ6,subQ5]});Q171=makeQuery(id+"F0.imprint","IMPRINT",FACE,{"disambiguationData":[TD([[makeQuery(id+"F0.imprint","IMPRINT",EDGE,{"disambiguationData":[TD([[subQ7,1.0]])],"derivedFrom":subQ6}),1.0]])]});}
            var Q172;
            {var subQ6=sQuery(id+"F0.wireOp",EDGE,"E2.22.0.7");var subQ9=sQuery(id+"F0.wireOp",EDGE,"E2.22.0.5");var subQ10=makeQuery(id+"F0.imprint","INTERSECT",VERTEX,{"derivedFrom":[subQ9,subQ6]});Q172=makeQuery(id+"F0.imprint","IMPRINT",FACE,{"disambiguationData":[TD([[makeQuery(id+"F0.imprint","IMPRINT",EDGE,{"disambiguationData":[TD([[subQ10,1.0]])],"derivedFrom":subQ9}),1.0]])]});}
            var Q173;
            {var subQ5=sQuery(id+"F0.wireOp",EDGE,"E2.18.0.7");var subQ7=sQuery(id+"F0.wireOp",EDGE,"E2.18.0.5");var subQ8=makeQuery(id+"F0.imprint","INTERSECT",VERTEX,{"derivedFrom":[subQ7,subQ5]});Q173=makeQuery(id+"F0.imprint","IMPRINT",FACE,{"disambiguationData":[TD([[makeQuery(id+"F0.imprint","IMPRINT",EDGE,{"disambiguationData":[TD([[subQ8,1.0]])],"derivedFrom":subQ7}),1.0]])]});}
            var Q174;
            {var subQ5=sQuery(id+"F0.wireOp",EDGE,"E3.0.2.96");var subQ6=sQuery(id+"F0.wireOp",EDGE,"E3.0.2.26");var subQ7=makeQuery(id+"F0.imprint","INTERSECT",VERTEX,{"derivedFrom":[subQ6,subQ5]});Q174=makeQuery(id+"F0.imprint","IMPRINT",FACE,{"disambiguationData":[TD([[makeQuery(id+"F0.imprint","IMPRINT",EDGE,{"disambiguationData":[TD([[subQ7,-1.0]])],"derivedFrom":subQ6}),-1.0]])]});}
            var Q175;
            {var subQ3=sQuery(id+"F0.wireOp",EDGE,"E3.0.2.161");var subQ5=sQuery(id+"F0.wireOp",EDGE,"E3.0.2.151");var subQ6=makeQuery(id+"F0.imprint","INTERSECT",VERTEX,{"derivedFrom":[subQ5,subQ3]});Q175=makeQuery(id+"F0.imprint","IMPRINT",FACE,{"disambiguationData":[TD([[makeQuery(id+"F0.imprint","IMPRINT",EDGE,{"disambiguationData":[TD([[subQ6,1.0]])],"derivedFrom":subQ5}),1.0]])]});}
            var Q176;
            {var subQ5=sQuery(id+"F0.wireOp",EDGE,"E3.0.2.198");var subQ6=sQuery(id+"F0.wireOp",EDGE,"E3.0.2.186");var subQ7=makeQuery(id+"F0.imprint","INTERSECT",VERTEX,{"derivedFrom":[subQ6,subQ5]});Q176=makeQuery(id+"F0.imprint","IMPRINT",FACE,{"disambiguationData":[TD([[makeQuery(id+"F0.imprint","IMPRINT",EDGE,{"disambiguationData":[TD([[subQ7,-1.0]])],"derivedFrom":subQ6}),-1.0]])]});}
            var Q177;
            {var subQ5=sQuery(id+"F0.wireOp",EDGE,"E3.0.3.98");var subQ7=sQuery(id+"F0.wireOp",EDGE,"E3.0.3.87");var subQ8=makeQuery(id+"F0.imprint","INTERSECT",VERTEX,{"derivedFrom":[subQ7,subQ5]});Q177=makeQuery(id+"F0.imprint","IMPRINT",FACE,{"disambiguationData":[TD([[makeQuery(id+"F0.imprint","IMPRINT",EDGE,{"disambiguationData":[TD([[subQ8,-1.0]])],"derivedFrom":subQ7}),-1.0]])]});}
            var Q178;
            {var subQ1=sQuery(id+"F0.wireOp",EDGE,"E3.0.3.147");var subQ7=sQuery(id+"F0.wireOp",EDGE,"E3.0.3.156");var subQ8=makeQuery(id+"F0.imprint","INTERSECT",VERTEX,{"derivedFrom":[subQ1,subQ7]});Q178=makeQuery(id+"F0.imprint","IMPRINT",FACE,{"disambiguationData":[TD([[makeQuery(id+"F0.imprint","IMPRINT",EDGE,{"disambiguationData":[TD([[subQ8,1.0]])],"derivedFrom":subQ1}),1.0]])]});}
            var Q179;
            {var subQ3=sQuery(id+"F0.wireOp",EDGE,"E3.0.4.211");Q179=makeQuery(id+"F0.imprint","IMPRINT",FACE,{"disambiguationData":[TD([[makeQuery(id+"F0.imprint","IMPRINT",EDGE,{"derivedFrom":subQ3}),1.0]])]});}
            var Q180;
            {var subQ3=sQuery(id+"F0.wireOp",EDGE,"E3.0.4.126");Q180=makeQuery(id+"F0.imprint","IMPRINT",FACE,{"disambiguationData":[TD([[makeQuery(id+"F0.imprint","IMPRINT",EDGE,{"derivedFrom":subQ3}),1.0]])]});}
            var Q181;
            {var subQ5=sQuery(id+"F0.wireOp",EDGE,"E2.10.0.7");var subQ6=sQuery(id+"F0.wireOp",EDGE,"E2.10.0.5");var subQ7=makeQuery(id+"F0.imprint","INTERSECT",VERTEX,{"derivedFrom":[subQ6,subQ5]});Q181=makeQuery(id+"F0.imprint","IMPRINT",FACE,{"disambiguationData":[TD([[makeQuery(id+"F0.imprint","IMPRINT",EDGE,{"disambiguationData":[TD([[subQ7,1.0]])],"derivedFrom":subQ6}),1.0]])]});}
            var Q182;
            {var subQ7=sQuery(id+"F0.wireOp",EDGE,"E2.2.0.7");var subQ9=sQuery(id+"F0.wireOp",EDGE,"E2.2.0.5");var subQ10=makeQuery(id+"F0.imprint","INTERSECT",VERTEX,{"derivedFrom":[subQ9,subQ7]});Q182=makeQuery(id+"F0.imprint","IMPRINT",FACE,{"disambiguationData":[TD([[makeQuery(id+"F0.imprint","IMPRINT",EDGE,{"disambiguationData":[TD([[subQ10,1.0]])],"derivedFrom":subQ9}),1.0]])]});}
            var Q183;
            {var subQ3=sQuery(id+"F0.wireOp",EDGE,"E3.0.1.229");var subQ5=sQuery(id+"F0.wireOp",EDGE,"E3.0.1.245");var subQ6=makeQuery(id+"F0.imprint","INTERSECT",VERTEX,{"derivedFrom":[subQ3,subQ5]});Q183=makeQuery(id+"F0.imprint","IMPRINT",FACE,{"disambiguationData":[TD([[makeQuery(id+"F0.imprint","IMPRINT",EDGE,{"disambiguationData":[TD([[subQ6,1.0]])],"derivedFrom":subQ3}),1.0]])]});}
            var Q184;
            {var subQ7=sQuery(id+"F0.wireOp",EDGE,"E3.0.1.171");var subQ9=sQuery(id+"F0.wireOp",EDGE,"E3.0.1.206");var subQ10=makeQuery(id+"F0.imprint","INTERSECT",VERTEX,{"derivedFrom":[subQ7,subQ9]});Q184=makeQuery(id+"F0.imprint","IMPRINT",FACE,{"disambiguationData":[TD([[makeQuery(id+"F0.imprint","IMPRINT",EDGE,{"disambiguationData":[TD([[subQ10,1.0]])],"derivedFrom":subQ7}),1.0]])]});}
            var Q185;
            {var subQ7=sQuery(id+"F0.wireOp",EDGE,"E3.0.1.163");var subQ9=sQuery(id+"F0.wireOp",EDGE,"E3.0.1.210");var subQ10=makeQuery(id+"F0.imprint","INTERSECT",VERTEX,{"derivedFrom":[subQ7,subQ9]});Q185=makeQuery(id+"F0.imprint","IMPRINT",FACE,{"disambiguationData":[TD([[makeQuery(id+"F0.imprint","IMPRINT",EDGE,{"disambiguationData":[TD([[subQ10,1.0]])],"derivedFrom":subQ7}),1.0]])]});}
            var Q186;
            {var subQ3=sQuery(id+"F0.wireOp",EDGE,"E3.0.3.171");var subQ5=sQuery(id+"F0.wireOp",EDGE,"E3.0.3.206");var subQ6=makeQuery(id+"F0.imprint","INTERSECT",VERTEX,{"derivedFrom":[subQ3,subQ5]});Q186=makeQuery(id+"F0.imprint","IMPRINT",FACE,{"disambiguationData":[TD([[makeQuery(id+"F0.imprint","IMPRINT",EDGE,{"disambiguationData":[TD([[subQ6,1.0]])],"derivedFrom":subQ3}),1.0]])]});}
            var Q187;
            {var subQ3=sQuery(id+"F0.wireOp",EDGE,"E3.0.4.208");Q187=makeQuery(id+"F0.imprint","IMPRINT",FACE,{"disambiguationData":[TD([[makeQuery(id+"F0.imprint","IMPRINT",EDGE,{"derivedFrom":subQ3}),1.0]])]});}
            var Q188;
            {var subQ1=sQuery(id+"F0.wireOp",EDGE,"E3.0.2.144");var subQ8=sQuery(id+"F0.wireOp",EDGE,"E3.0.2.153");var subQ10=makeQuery(id+"F0.imprint","INTERSECT",VERTEX,{"derivedFrom":[subQ1,subQ8]});Q188=makeQuery(id+"F0.imprint","IMPRINT",FACE,{"disambiguationData":[TD([[makeQuery(id+"F0.imprint","IMPRINT",EDGE,{"disambiguationData":[TD([[subQ10,1.0]])],"derivedFrom":subQ1}),1.0]])]});}
            var Q189;
            {var subQ0=sQuery(id+"F0.wireOp",EDGE,"E3.0.2.197");var subQ1=sQuery(id+"F0.wireOp",EDGE,"E3.0.2.85");var subQ2=makeQuery(id+"F0.imprint","INTERSECT",VERTEX,{"derivedFrom":[subQ1,subQ0]});Q189=makeQuery(id+"F0.imprint","IMPRINT",FACE,{"disambiguationData":[TD([[makeQuery(id+"F0.imprint","IMPRINT",EDGE,{"disambiguationData":[TD([[subQ2,-1.0]])],"derivedFrom":subQ1}),-1.0]])]});}
            var Q190;
            {var subQ0=sQuery(id+"F0.wireOp",EDGE,"E3.0.3.196");var subQ1=sQuery(id+"F0.wireOp",EDGE,"E3.0.3.101");var subQ2=makeQuery(id+"F0.imprint","INTERSECT",VERTEX,{"derivedFrom":[subQ1,subQ0]});Q190=makeQuery(id+"F0.imprint","IMPRINT",FACE,{"disambiguationData":[TD([[makeQuery(id+"F0.imprint","IMPRINT",EDGE,{"disambiguationData":[TD([[subQ2,1.0]])],"derivedFrom":subQ1}),1.0]])]});}
            var Q191;
            {var subQ5=sQuery(id+"F0.wireOp",EDGE,"E3.0.3.216");var subQ6=sQuery(id+"F0.wireOp",EDGE,"E3.0.3.87");var subQ7=makeQuery(id+"F0.imprint","INTERSECT",VERTEX,{"derivedFrom":[subQ6,subQ5]});Q191=makeQuery(id+"F0.imprint","IMPRINT",FACE,{"disambiguationData":[TD([[makeQuery(id+"F0.imprint","IMPRINT",EDGE,{"disambiguationData":[TD([[subQ7,1.0]])],"derivedFrom":subQ6}),1.0]])]});}
            var Q192;
            {var subQ3=sQuery(id+"F0.wireOp",EDGE,"E3.0.3.158");var subQ5=sQuery(id+"F0.wireOp",EDGE,"E3.0.3.148");var subQ6=makeQuery(id+"F0.imprint","INTERSECT",VERTEX,{"derivedFrom":[subQ5,subQ3]});Q192=makeQuery(id+"F0.imprint","IMPRINT",FACE,{"disambiguationData":[TD([[makeQuery(id+"F0.imprint","IMPRINT",EDGE,{"disambiguationData":[TD([[subQ6,1.0]])],"derivedFrom":subQ5}),1.0]])]});}
            var Q193;
            {var subQ3=sQuery(id+"F0.wireOp",EDGE,"E3.0.4.205");Q193=makeQuery(id+"F0.imprint","IMPRINT",FACE,{"disambiguationData":[TD([[makeQuery(id+"F0.imprint","IMPRINT",EDGE,{"derivedFrom":subQ3}),1.0]])]});}
            var Q194;
            {var subQ3=sQuery(id+"F0.wireOp",EDGE,"E2.27.0.3");var subQ9=sQuery(id+"F0.wireOp",EDGE,"E2.27.0.1");var subQ11=makeQuery(id+"F0.imprint","INTERSECT",VERTEX,{"derivedFrom":[subQ9,subQ3]});Q194=makeQuery(id+"F0.imprint","IMPRINT",FACE,{"disambiguationData":[TD([[makeQuery(id+"F0.imprint","IMPRINT",EDGE,{"disambiguationData":[TD([[subQ11,1.0]])],"derivedFrom":subQ9}),1.0]])]});}
            var Q195;
            {var subQ5=sQuery(id+"F0.wireOp",EDGE,"E3.0.1.216");var subQ7=sQuery(id+"F0.wireOp",EDGE,"E3.0.1.87");var subQ8=makeQuery(id+"F0.imprint","INTERSECT",VERTEX,{"derivedFrom":[subQ7,subQ5]});Q195=makeQuery(id+"F0.imprint","IMPRINT",FACE,{"disambiguationData":[TD([[makeQuery(id+"F0.imprint","IMPRINT",EDGE,{"disambiguationData":[TD([[subQ8,1.0]])],"derivedFrom":subQ7}),1.0]])]});}
            var Q196;
            {var subQ5=sQuery(id+"F0.wireOp",EDGE,"E3.0.3.244");var subQ6=sQuery(id+"F0.wireOp",EDGE,"E3.0.3.230");var subQ7=makeQuery(id+"F0.imprint","INTERSECT",VERTEX,{"derivedFrom":[subQ6,subQ5]});Q196=makeQuery(id+"F0.imprint","IMPRINT",FACE,{"disambiguationData":[TD([[makeQuery(id+"F0.imprint","IMPRINT",EDGE,{"disambiguationData":[TD([[subQ7,1.0]])],"derivedFrom":subQ6}),1.0]])]});}
            var Q197;
            {var subQ3=sQuery(id+"F0.wireOp",EDGE,"E3.0.4.218");Q197=makeQuery(id+"F0.imprint","IMPRINT",FACE,{"disambiguationData":[TD([[makeQuery(id+"F0.imprint","IMPRINT",EDGE,{"derivedFrom":subQ3}),1.0]])]});}
            var Q198;
            {var subQ3=sQuery(id+"F0.wireOp",EDGE,"E3.0.4.214");Q198=makeQuery(id+"F0.imprint","IMPRINT",FACE,{"disambiguationData":[TD([[makeQuery(id+"F0.imprint","IMPRINT",EDGE,{"derivedFrom":subQ3}),1.0]])]});}
            var Q199;
            {var subQ3=sQuery(id+"F0.wireOp",EDGE,"E2.11.0.5");var subQ5=sQuery(id+"F0.wireOp",EDGE,"E2.11.0.7");var subQ6=makeQuery(id+"F0.imprint","INTERSECT",VERTEX,{"derivedFrom":[subQ3,subQ5]});Q199=makeQuery(id+"F0.imprint","IMPRINT",FACE,{"disambiguationData":[TD([[makeQuery(id+"F0.imprint","IMPRINT",EDGE,{"disambiguationData":[TD([[subQ6,1.0]])],"derivedFrom":subQ3}),1.0]])]});}
            var Q200;
            {var subQ7=sQuery(id+"F0.wireOp",EDGE,"E2.7.0.5");var subQ9=sQuery(id+"F0.wireOp",EDGE,"E2.7.0.7");var subQ10=makeQuery(id+"F0.imprint","INTERSECT",VERTEX,{"derivedFrom":[subQ7,subQ9]});Q200=makeQuery(id+"F0.imprint","IMPRINT",FACE,{"disambiguationData":[TD([[makeQuery(id+"F0.imprint","IMPRINT",EDGE,{"disambiguationData":[TD([[subQ10,1.0]])],"derivedFrom":subQ7}),1.0]])]});}
            var Q201;
            {var subQ3=sQuery(id+"F0.wireOp",EDGE,"E2.27.0.5");var subQ5=sQuery(id+"F0.wireOp",EDGE,"E2.27.0.7");var subQ6=makeQuery(id+"F0.imprint","INTERSECT",VERTEX,{"derivedFrom":[subQ3,subQ5]});Q201=makeQuery(id+"F0.imprint","IMPRINT",FACE,{"disambiguationData":[TD([[makeQuery(id+"F0.imprint","IMPRINT",EDGE,{"disambiguationData":[TD([[subQ6,1.0]])],"derivedFrom":subQ3}),1.0]])]});}
            var Q202;
            {var subQ5=sQuery(id+"F0.wireOp",EDGE,"E2.23.0.7");var subQ6=sQuery(id+"F0.wireOp",EDGE,"E2.23.0.5");var subQ7=makeQuery(id+"F0.imprint","INTERSECT",VERTEX,{"derivedFrom":[subQ6,subQ5]});Q202=makeQuery(id+"F0.imprint","IMPRINT",FACE,{"disambiguationData":[TD([[makeQuery(id+"F0.imprint","IMPRINT",EDGE,{"disambiguationData":[TD([[subQ7,1.0]])],"derivedFrom":subQ6}),1.0]])]});}
            var Q203;
            {var subQ3=sQuery(id+"F0.wireOp",EDGE,"E2.19.0.5");var subQ5=sQuery(id+"F0.wireOp",EDGE,"E2.19.0.7");var subQ6=makeQuery(id+"F0.imprint","INTERSECT",VERTEX,{"derivedFrom":[subQ3,subQ5]});Q203=makeQuery(id+"F0.imprint","IMPRINT",FACE,{"disambiguationData":[TD([[makeQuery(id+"F0.imprint","IMPRINT",EDGE,{"disambiguationData":[TD([[subQ6,1.0]])],"derivedFrom":subQ3}),1.0]])]});}
            var Q204;
            {var subQ6=sQuery(id+"F0.wireOp",EDGE,"E3.0.1.217");var subQ9=sQuery(id+"F0.wireOp",EDGE,"E3.0.1.82");var subQ10=makeQuery(id+"F0.imprint","INTERSECT",VERTEX,{"derivedFrom":[subQ9,subQ6]});Q204=makeQuery(id+"F0.imprint","IMPRINT",FACE,{"disambiguationData":[TD([[makeQuery(id+"F0.imprint","IMPRINT",EDGE,{"disambiguationData":[TD([[subQ10,1.0]])],"derivedFrom":subQ9}),1.0]])]});}
            var Q205;
            {var subQ5=sQuery(id+"F0.wireOp",EDGE,"E3.0.1.237");var subQ6=sQuery(id+"F0.wireOp",EDGE,"E3.0.1.181");var subQ7=makeQuery(id+"F0.imprint","INTERSECT",VERTEX,{"derivedFrom":[subQ6,subQ5]});Q205=makeQuery(id+"F0.imprint","IMPRINT",FACE,{"disambiguationData":[TD([[makeQuery(id+"F0.imprint","IMPRINT",EDGE,{"disambiguationData":[TD([[subQ7,1.0]])],"derivedFrom":subQ6}),1.0]])]});}
            var Q206;
            {var subQ5=sQuery(id+"F0.wireOp",EDGE,"E3.0.1.164");var subQ7=sQuery(id+"F0.wireOp",EDGE,"E3.0.1.208");var subQ8=makeQuery(id+"F0.imprint","INTERSECT",VERTEX,{"derivedFrom":[subQ5,subQ7]});Q206=makeQuery(id+"F0.imprint","IMPRINT",FACE,{"disambiguationData":[TD([[makeQuery(id+"F0.imprint","IMPRINT",EDGE,{"disambiguationData":[TD([[subQ8,1.0]])],"derivedFrom":subQ5}),1.0]])]});}
            var Q207;
            {var subQ7=sQuery(id+"F0.wireOp",EDGE,"E3.0.3.104");var subQ9=sQuery(id+"F0.wireOp",EDGE,"E3.0.3.83");var subQ10=makeQuery(id+"F0.imprint","INTERSECT",VERTEX,{"derivedFrom":[subQ9,subQ7]});Q207=makeQuery(id+"F0.imprint","IMPRINT",FACE,{"disambiguationData":[TD([[makeQuery(id+"F0.imprint","IMPRINT",EDGE,{"disambiguationData":[TD([[subQ10,-1.0]])],"derivedFrom":subQ9}),-1.0]])]});}
            var Q208;
            {var subQ3=sQuery(id+"F0.wireOp",EDGE,"E3.0.2.154");var subQ5=sQuery(id+"F0.wireOp",EDGE,"E3.0.2.223");var subQ6=makeQuery(id+"F0.imprint","INTERSECT",VERTEX,{"derivedFrom":[subQ3,subQ5]});Q208=makeQuery(id+"F0.imprint","IMPRINT",FACE,{"disambiguationData":[TD([[makeQuery(id+"F0.imprint","IMPRINT",EDGE,{"disambiguationData":[TD([[subQ6,-1.0]])],"derivedFrom":subQ3}),1.0]])]});}
            var Q209;
            {var subQ7=sQuery(id+"F0.wireOp",EDGE,"E3.0.3.199");var subQ8=sQuery(id+"F0.wireOp",EDGE,"E3.0.3.185");var subQ9=makeQuery(id+"F0.imprint","INTERSECT",VERTEX,{"derivedFrom":[subQ8,subQ7]});Q209=makeQuery(id+"F0.imprint","IMPRINT",FACE,{"disambiguationData":[TD([[makeQuery(id+"F0.imprint","IMPRINT",EDGE,{"disambiguationData":[TD([[subQ9,-1.0]])],"derivedFrom":subQ8}),-1.0]])]});}
            var Q210;
            {var subQ7=sQuery(id+"F0.wireOp",EDGE,"E3.0.3.165");var subQ9=sQuery(id+"F0.wireOp",EDGE,"E3.0.3.207");var subQ10=makeQuery(id+"F0.imprint","INTERSECT",VERTEX,{"derivedFrom":[subQ7,subQ9]});Q210=makeQuery(id+"F0.imprint","IMPRINT",FACE,{"disambiguationData":[TD([[makeQuery(id+"F0.imprint","IMPRINT",EDGE,{"disambiguationData":[TD([[subQ10,1.0]])],"derivedFrom":subQ7}),1.0]])]});}
            var Q211;
            {var subQ5=sQuery(id+"F0.wireOp",EDGE,"E3.0.4.213");Q211=makeQuery(id+"F0.imprint","IMPRINT",FACE,{"disambiguationData":[TD([[makeQuery(id+"F0.imprint","IMPRINT",EDGE,{"derivedFrom":subQ5}),1.0]])]});}
            var Q212;
            {var subQ5=sQuery(id+"F0.wireOp",EDGE,"E3.0.1.214");var subQ7=sQuery(id+"F0.wireOp",EDGE,"E3.0.1.88");var subQ8=makeQuery(id+"F0.imprint","INTERSECT",VERTEX,{"derivedFrom":[subQ7,subQ5]});Q212=makeQuery(id+"F0.imprint","IMPRINT",FACE,{"disambiguationData":[TD([[makeQuery(id+"F0.imprint","IMPRINT",EDGE,{"disambiguationData":[TD([[subQ8,1.0]])],"derivedFrom":subQ7}),1.0]])]});}
            var Q213;
            {var subQ5=sQuery(id+"F0.wireOp",EDGE,"E3.0.2.97");var subQ7=sQuery(id+"F0.wireOp",EDGE,"E3.0.2.86");var subQ8=makeQuery(id+"F0.imprint","INTERSECT",VERTEX,{"derivedFrom":[subQ7,subQ5]});Q213=makeQuery(id+"F0.imprint","IMPRINT",FACE,{"disambiguationData":[TD([[makeQuery(id+"F0.imprint","IMPRINT",EDGE,{"disambiguationData":[TD([[subQ8,-1.0]])],"derivedFrom":subQ7}),-1.0]])]});}
            var Q214;
            {var subQ0=sQuery(id+"F0.wireOp",EDGE,"E3.0.2.99");var subQ1=sQuery(id+"F0.wireOp",EDGE,"E3.0.2.88");var subQ2=makeQuery(id+"F0.imprint","INTERSECT",VERTEX,{"derivedFrom":[subQ1,subQ0]});Q214=makeQuery(id+"F0.imprint","IMPRINT",FACE,{"disambiguationData":[TD([[makeQuery(id+"F0.imprint","IMPRINT",EDGE,{"disambiguationData":[TD([[subQ2,1.0]])],"derivedFrom":subQ1}),-1.0]])]});}
            var Q215;
            {var subQ5=sQuery(id+"F0.wireOp",EDGE,"E3.0.2.98");var subQ7=sQuery(id+"F0.wireOp",EDGE,"E3.0.2.87");var subQ8=makeQuery(id+"F0.imprint","INTERSECT",VERTEX,{"derivedFrom":[subQ7,subQ5]});Q215=makeQuery(id+"F0.imprint","IMPRINT",FACE,{"disambiguationData":[TD([[makeQuery(id+"F0.imprint","IMPRINT",EDGE,{"disambiguationData":[TD([[subQ8,-1.0]])],"derivedFrom":subQ7}),-1.0]])]});}
            var Q216;
            {var subQ5=sQuery(id+"F0.wireOp",EDGE,"E3.0.3.96");var subQ6=sQuery(id+"F0.wireOp",EDGE,"E3.0.3.26");var subQ7=makeQuery(id+"F0.imprint","INTERSECT",VERTEX,{"derivedFrom":[subQ6,subQ5]});Q216=makeQuery(id+"F0.imprint","IMPRINT",FACE,{"disambiguationData":[TD([[makeQuery(id+"F0.imprint","IMPRINT",EDGE,{"disambiguationData":[TD([[subQ7,-1.0]])],"derivedFrom":subQ6}),-1.0]])]});}
            var Q217;
            {var subQ0=sQuery(id+"F0.wireOp",EDGE,"E3.0.4.227");var subQ1=sQuery(id+"F0.wireOp",EDGE,"E3.0.4.137");var subQ2=makeQuery(id+"F0.imprint","INTERSECT",VERTEX,{"derivedFrom":[subQ1,subQ0]});Q217=makeQuery(id+"F0.imprint","IMPRINT",FACE,{"disambiguationData":[TD([[makeQuery(id+"F0.imprint","IMPRINT",EDGE,{"disambiguationData":[TD([[subQ2,1.0]])],"derivedFrom":subQ1}),1.0]])]});}
            var Q218;
            {var subQ0=sQuery(id+"F0.wireOp",EDGE,"E3.0.4.180");var subQ1=sQuery(id+"F0.wireOp",EDGE,"E3.0.4.69");var subQ2=makeQuery(id+"F0.imprint","INTERSECT",VERTEX,{"derivedFrom":[subQ1,subQ0]});Q218=makeQuery(id+"F0.imprint","IMPRINT",FACE,{"disambiguationData":[TD([[makeQuery(id+"F0.imprint","IMPRINT",EDGE,{"disambiguationData":[TD([[subQ2,1.0]])],"derivedFrom":subQ1}),1.0]])]});}
            var Q219;
            {var subQ0=sQuery(id+"F0.wireOp",EDGE,"E3.0.1.68");var subQ1=sQuery(id+"F0.wireOp",EDGE,"E1.top");var subQ2=makeQuery(id+"F0.imprint","INTERSECT",VERTEX,{"derivedFrom":[subQ1,subQ0]});Q219=makeQuery(id+"F0.imprint","IMPRINT",FACE,{"disambiguationData":[TD([[makeQuery(id+"F0.imprint","IMPRINT",EDGE,{"disambiguationData":[TD([[subQ2,-1.0]])],"derivedFrom":subQ1}),1.0]])]});}
            var Q220;
            {var subQ5=sQuery(id+"F0.wireOp",EDGE,"E3.0.4.210");Q220=makeQuery(id+"F0.imprint","IMPRINT",FACE,{"disambiguationData":[TD([[makeQuery(id+"F0.imprint","IMPRINT",EDGE,{"derivedFrom":subQ5}),1.0]])]});}
            var Q221;
            {var subQ5=sQuery(id+"F0.wireOp",EDGE,"E2.24.0.7");var subQ6=sQuery(id+"F0.wireOp",EDGE,"E2.24.0.5");var subQ7=makeQuery(id+"F0.imprint","INTERSECT",VERTEX,{"derivedFrom":[subQ6,subQ5]});Q221=makeQuery(id+"F0.imprint","IMPRINT",FACE,{"disambiguationData":[TD([[makeQuery(id+"F0.imprint","IMPRINT",EDGE,{"disambiguationData":[TD([[subQ7,1.0]])],"derivedFrom":subQ6}),1.0]])]});}
            var Q222;
            {var subQ0=sQuery(id+"F0.wireOp",EDGE,"E2.20.0.7");var subQ1=sQuery(id+"F0.wireOp",EDGE,"E2.20.0.5");var subQ2=makeQuery(id+"F0.imprint","INTERSECT",VERTEX,{"derivedFrom":[subQ1,subQ0]});Q222=makeQuery(id+"F0.imprint","IMPRINT",FACE,{"disambiguationData":[TD([[makeQuery(id+"F0.imprint","IMPRINT",EDGE,{"disambiguationData":[TD([[subQ2,1.0]])],"derivedFrom":subQ1}),-1.0]])]});}
            var Q223;
            {var subQ7=sQuery(id+"F0.wireOp",EDGE,"E2.12.0.7");var subQ9=sQuery(id+"F0.wireOp",EDGE,"E2.12.0.5");var subQ10=makeQuery(id+"F0.imprint","INTERSECT",VERTEX,{"derivedFrom":[subQ9,subQ7]});Q223=makeQuery(id+"F0.imprint","IMPRINT",FACE,{"disambiguationData":[TD([[makeQuery(id+"F0.imprint","IMPRINT",EDGE,{"disambiguationData":[TD([[subQ10,1.0]])],"derivedFrom":subQ9}),1.0]])]});}
            var Q224;
            {var subQ5=sQuery(id+"F0.wireOp",EDGE,"E3.0.1.123");var subQ7=sQuery(id+"F0.wireOp",EDGE,"E3.0.1.89");var subQ8=makeQuery(id+"F0.imprint","INTERSECT",VERTEX,{"derivedFrom":[subQ7,subQ5]});Q224=makeQuery(id+"F0.imprint","IMPRINT",FACE,{"disambiguationData":[TD([[makeQuery(id+"F0.imprint","IMPRINT",EDGE,{"disambiguationData":[TD([[subQ8,1.0]])],"derivedFrom":subQ7}),1.0]])]});}
            var Q225;
            {var subQ0=sQuery(id+"F0.wireOp",EDGE,"E3.0.1.127");var subQ1=sQuery(id+"F0.wireOp",EDGE,"E3.0.1.84");var subQ2=makeQuery(id+"F0.imprint","INTERSECT",VERTEX,{"derivedFrom":[subQ1,subQ0]});Q225=makeQuery(id+"F0.imprint","IMPRINT",FACE,{"disambiguationData":[TD([[makeQuery(id+"F0.imprint","IMPRINT",EDGE,{"disambiguationData":[TD([[subQ2,1.0]])],"derivedFrom":subQ1}),-1.0]])]});}
            var Q226;
            {var subQ0=sQuery(id+"F0.wireOp",EDGE,"E2.28.0.7");var subQ1=sQuery(id+"F0.wireOp",EDGE,"E2.28.0.5");var subQ2=makeQuery(id+"F0.imprint","INTERSECT",VERTEX,{"derivedFrom":[subQ1,subQ0]});Q226=makeQuery(id+"F0.imprint","IMPRINT",FACE,{"disambiguationData":[TD([[makeQuery(id+"F0.imprint","IMPRINT",EDGE,{"disambiguationData":[TD([[subQ2,1.0]])],"derivedFrom":subQ1}),-1.0]])]});}
            var Q227;
            {var subQ3=sQuery(id+"F0.wireOp",EDGE,"E2.4.0.3");var subQ6=sQuery(id+"F0.wireOp",EDGE,"E2.4.0.1");var subQ10=makeQuery(id+"F0.imprint","INTERSECT",VERTEX,{"derivedFrom":[subQ6,subQ3]});Q227=makeQuery(id+"F0.imprint","IMPRINT",FACE,{"disambiguationData":[TD([[makeQuery(id+"F0.imprint","IMPRINT",EDGE,{"disambiguationData":[TD([[subQ10,1.0]])],"derivedFrom":subQ6}),1.0]])]});}
            var Q228;
            {var subQ3=sQuery(id+"F0.wireOp",EDGE,"E2.20.0.3");var subQ6=sQuery(id+"F0.wireOp",EDGE,"E2.20.0.1");var subQ10=makeQuery(id+"F0.imprint","INTERSECT",VERTEX,{"derivedFrom":[subQ6,subQ3]});Q228=makeQuery(id+"F0.imprint","IMPRINT",FACE,{"disambiguationData":[TD([[makeQuery(id+"F0.imprint","IMPRINT",EDGE,{"disambiguationData":[TD([[subQ10,1.0]])],"derivedFrom":subQ6}),1.0]])]});}
            var Q229;
            {var subQ3=sQuery(id+"F0.wireOp",EDGE,"E2.16.0.3");var subQ6=sQuery(id+"F0.wireOp",EDGE,"E2.16.0.1");var subQ10=makeQuery(id+"F0.imprint","INTERSECT",VERTEX,{"derivedFrom":[subQ6,subQ3]});Q229=makeQuery(id+"F0.imprint","IMPRINT",FACE,{"disambiguationData":[TD([[makeQuery(id+"F0.imprint","IMPRINT",EDGE,{"disambiguationData":[TD([[subQ10,1.0]])],"derivedFrom":subQ6}),1.0]])]});}
            var Q230;
            {var subQ3=sQuery(id+"F0.wireOp",EDGE,"E2.12.0.3");var subQ8=sQuery(id+"F0.wireOp",EDGE,"E2.12.0.1");var subQ11=makeQuery(id+"F0.imprint","INTERSECT",VERTEX,{"derivedFrom":[subQ8,subQ3]});Q230=makeQuery(id+"F0.imprint","IMPRINT",FACE,{"disambiguationData":[TD([[makeQuery(id+"F0.imprint","IMPRINT",EDGE,{"disambiguationData":[TD([[subQ11,1.0]])],"derivedFrom":subQ8}),1.0]])]});}
            var Q231;
            {var subQ3=sQuery(id+"F0.wireOp",EDGE,"E2.8.0.3");var subQ6=sQuery(id+"F0.wireOp",EDGE,"E2.8.0.1");var subQ10=makeQuery(id+"F0.imprint","INTERSECT",VERTEX,{"derivedFrom":[subQ6,subQ3]});Q231=makeQuery(id+"F0.imprint","IMPRINT",FACE,{"disambiguationData":[TD([[makeQuery(id+"F0.imprint","IMPRINT",EDGE,{"disambiguationData":[TD([[subQ10,1.0]])],"derivedFrom":subQ6}),1.0]])]});}
            var Q232;
            {var subQ6=sQuery(id+"F0.wireOp",EDGE,"E3.0.1.128");var subQ9=sQuery(id+"F0.wireOp",EDGE,"E3.0.1.83");var subQ10=makeQuery(id+"F0.imprint","INTERSECT",VERTEX,{"derivedFrom":[subQ9,subQ6]});Q232=makeQuery(id+"F0.imprint","IMPRINT",FACE,{"disambiguationData":[TD([[makeQuery(id+"F0.imprint","IMPRINT",EDGE,{"disambiguationData":[TD([[subQ10,1.0]])],"derivedFrom":subQ9}),1.0]])]});}
            var Q233;
            {var subQ3=sQuery(id+"F0.wireOp",EDGE,"E2.24.0.3");var subQ6=sQuery(id+"F0.wireOp",EDGE,"E2.24.0.1");var subQ11=makeQuery(id+"F0.imprint","INTERSECT",VERTEX,{"derivedFrom":[subQ6,subQ3]});Q233=makeQuery(id+"F0.imprint","IMPRINT",FACE,{"disambiguationData":[TD([[makeQuery(id+"F0.imprint","IMPRINT",EDGE,{"disambiguationData":[TD([[subQ11,1.0]])],"derivedFrom":subQ6}),1.0]])]});}
            var Q234;
            {var subQ0=sQuery(id+"F0.wireOp",EDGE,"E3.0.1.207");var subQ1=sQuery(id+"F0.wireOp",EDGE,"E3.0.1.165");var subQ2=makeQuery(id+"F0.imprint","INTERSECT",VERTEX,{"derivedFrom":[subQ1,subQ0]});Q234=makeQuery(id+"F0.imprint","IMPRINT",FACE,{"disambiguationData":[TD([[makeQuery(id+"F0.imprint","IMPRINT",EDGE,{"disambiguationData":[TD([[subQ2,1.0]])],"derivedFrom":subQ1}),-1.0]])]});}
            var Q235;
            {var subQ1=sQuery(id+"F0.wireOp",EDGE,"E3.0.2.102");var subQ7=sQuery(id+"F0.wireOp",EDGE,"E3.0.2.81");var subQ8=makeQuery(id+"F0.imprint","INTERSECT",VERTEX,{"derivedFrom":[subQ7,subQ1]});Q235=makeQuery(id+"F0.imprint","IMPRINT",FACE,{"disambiguationData":[TD([[makeQuery(id+"F0.imprint","IMPRINT",EDGE,{"disambiguationData":[TD([[subQ8,-1.0]])],"derivedFrom":subQ7}),-1.0]])]});}
            var Q236;
            {var subQ0=sQuery(id+"F0.wireOp",EDGE,"E3.0.2.224");var subQ1=sQuery(id+"F0.wireOp",EDGE,"E3.0.2.157");var subQ2=makeQuery(id+"F0.imprint","INTERSECT",VERTEX,{"derivedFrom":[subQ1,subQ0]});Q236=makeQuery(id+"F0.imprint","IMPRINT",FACE,{"disambiguationData":[TD([[makeQuery(id+"F0.imprint","IMPRINT",EDGE,{"disambiguationData":[TD([[subQ2,-1.0]])],"derivedFrom":subQ1}),1.0]])]});}
            var Q237;
            {var subQ3=sQuery(id+"F0.wireOp",EDGE,"E3.0.3.160");var subQ6=sQuery(id+"F0.wireOp",EDGE,"E3.0.3.150");var subQ11=makeQuery(id+"F0.imprint","INTERSECT",VERTEX,{"derivedFrom":[subQ6,subQ3]});Q237=makeQuery(id+"F0.imprint","IMPRINT",FACE,{"disambiguationData":[TD([[makeQuery(id+"F0.imprint","IMPRINT",EDGE,{"disambiguationData":[TD([[subQ11,1.0]])],"derivedFrom":subQ6}),1.0]])]});}
            var Q238;
            {var subQ0=sQuery(id+"F0.wireOp",EDGE,"E3.0.4.61");var subQ1=sQuery(id+"F0.wireOp",EDGE,"E3.0.4.7");var subQ2=makeQuery(id+"F0.imprint","INTERSECT",VERTEX,{"derivedFrom":[subQ1,subQ0]});Q238=makeQuery(id+"F0.imprint","IMPRINT",FACE,{"disambiguationData":[TD([[makeQuery(id+"F0.imprint","IMPRINT",EDGE,{"disambiguationData":[TD([[subQ2,1.0]])],"derivedFrom":subQ1}),1.0]])]});}
            var Q239;
            {var subQ0=sQuery(id+"F0.wireOp",EDGE,"E2.4.0.7");var subQ1=sQuery(id+"F0.wireOp",EDGE,"E2.4.0.5");var subQ2=makeQuery(id+"F0.imprint","INTERSECT",VERTEX,{"derivedFrom":[subQ1,subQ0]});Q239=makeQuery(id+"F0.imprint","IMPRINT",FACE,{"disambiguationData":[TD([[makeQuery(id+"F0.imprint","IMPRINT",EDGE,{"disambiguationData":[TD([[subQ2,1.0]])],"derivedFrom":subQ1}),-1.0]])]});}
            var Q240;
            {var subQ5=sQuery(id+"F0.wireOp",EDGE,"E3.0.4.245");Q240=makeQuery(id+"F0.imprint","IMPRINT",FACE,{"disambiguationData":[TD([[makeQuery(id+"F0.imprint","IMPRINT",EDGE,{"derivedFrom":subQ5}),1.0]])]});}
            var Q241;
            {var subQ0=sQuery(id+"F0.wireOp",EDGE,"E2.20.0.7");var subQ1=sQuery(id+"F0.wireOp",EDGE,"E2.20.0.5");var subQ2=makeQuery(id+"F0.imprint","INTERSECT",VERTEX,{"derivedFrom":[subQ1,subQ0]});Q241=makeQuery(id+"F0.imprint","IMPRINT",FACE,{"disambiguationData":[TD([[makeQuery(id+"F0.imprint","IMPRINT",EDGE,{"disambiguationData":[TD([[subQ2,1.0]])],"derivedFrom":subQ1}),1.0]])]});}
            var Q242;
            {var subQ0=sQuery(id+"F0.wireOp",EDGE,"E2.16.0.7");var subQ1=sQuery(id+"F0.wireOp",EDGE,"E2.16.0.5");var subQ2=makeQuery(id+"F0.imprint","INTERSECT",VERTEX,{"derivedFrom":[subQ1,subQ0]});Q242=makeQuery(id+"F0.imprint","IMPRINT",FACE,{"disambiguationData":[TD([[makeQuery(id+"F0.imprint","IMPRINT",EDGE,{"disambiguationData":[TD([[subQ2,1.0]])],"derivedFrom":subQ1}),-1.0]])]});}
            var Q243;
            {var subQ0=sQuery(id+"F0.wireOp",EDGE,"E2.8.0.7");var subQ1=sQuery(id+"F0.wireOp",EDGE,"E2.8.0.5");var subQ2=makeQuery(id+"F0.imprint","INTERSECT",VERTEX,{"derivedFrom":[subQ1,subQ0]});Q243=makeQuery(id+"F0.imprint","IMPRINT",FACE,{"disambiguationData":[TD([[makeQuery(id+"F0.imprint","IMPRINT",EDGE,{"disambiguationData":[TD([[subQ2,1.0]])],"derivedFrom":subQ1}),-1.0]])]});}
            var Q244;
            {var subQ0=sQuery(id+"F0.wireOp",EDGE,"E3.0.3.226");var subQ1=sQuery(id+"F0.wireOp",EDGE,"E3.0.3.133");var subQ2=makeQuery(id+"F0.imprint","INTERSECT",VERTEX,{"derivedFrom":[subQ1,subQ0]});Q244=makeQuery(id+"F0.imprint","IMPRINT",FACE,{"disambiguationData":[TD([[makeQuery(id+"F0.imprint","IMPRINT",EDGE,{"disambiguationData":[TD([[subQ2,1.0]])],"derivedFrom":subQ1}),1.0]])]});}
            var Q245;
            {var subQ1=sQuery(id+"F0.wireOp",EDGE,"E3.0.3.95");var subQ9=sQuery(id+"F0.wireOp",EDGE,"E3.0.3.84");var subQ11=makeQuery(id+"F0.imprint","INTERSECT",VERTEX,{"derivedFrom":[subQ9,subQ1]});Q245=makeQuery(id+"F0.imprint","IMPRINT",FACE,{"disambiguationData":[TD([[makeQuery(id+"F0.imprint","IMPRINT",EDGE,{"disambiguationData":[TD([[subQ11,-1.0]])],"derivedFrom":subQ9}),-1.0]])]});}
            var Q246;
            {var subQ0=sQuery(id+"F0.wireOp",EDGE,"E3.0.4.155");var subQ1=sQuery(id+"F0.wireOp",EDGE,"E3.0.4.135");var subQ2=makeQuery(id+"F0.imprint","INTERSECT",VERTEX,{"derivedFrom":[subQ1,subQ0]});Q246=makeQuery(id+"F0.imprint","IMPRINT",FACE,{"disambiguationData":[TD([[makeQuery(id+"F0.imprint","IMPRINT",EDGE,{"disambiguationData":[TD([[subQ2,1.0]])],"derivedFrom":subQ1}),1.0]])]});}
            var Q247;
            {var subQ0=sQuery(id+"F0.wireOp",EDGE,"E3.0.4.33");var subQ1=sQuery(id+"F0.wireOp",EDGE,"E3.0.4.23");var subQ2=makeQuery(id+"F0.imprint","INTERSECT",VERTEX,{"derivedFrom":[subQ1,subQ0]});Q247=makeQuery(id+"F0.imprint","IMPRINT",FACE,{"disambiguationData":[TD([[makeQuery(id+"F0.imprint","IMPRINT",EDGE,{"disambiguationData":[TD([[subQ2,1.0]])],"derivedFrom":subQ1}),-1.0]])]});}
            var Q248;
            {var subQ5=sQuery(id+"F0.wireOp",EDGE,"E3.0.3.212");var subQ6=sQuery(id+"F0.wireOp",EDGE,"E3.0.3.166");var subQ7=makeQuery(id+"F0.imprint","INTERSECT",VERTEX,{"derivedFrom":[subQ6,subQ5]});Q248=makeQuery(id+"F0.imprint","IMPRINT",FACE,{"disambiguationData":[TD([[makeQuery(id+"F0.imprint","IMPRINT",EDGE,{"disambiguationData":[TD([[subQ7,1.0]])],"derivedFrom":subQ6}),1.0]])]});}
            var Q249;
            {var subQ0=sQuery(id+"F0.wireOp",EDGE,"E2.1.0.3");var subQ1=sQuery(id+"F0.wireOp",EDGE,"E2.1.0.0");var subQ2=makeQuery(id+"F0.imprint","INTERSECT",VERTEX,{"derivedFrom":[subQ1,subQ0]});Q249=makeQuery(id+"F0.imprint","IMPRINT",FACE,{"disambiguationData":[TD([[makeQuery(id+"F0.imprint","IMPRINT",EDGE,{"disambiguationData":[TD([[subQ2,1.0]])],"derivedFrom":subQ1}),1.0]])]});}
            var Q250;
            {var subQ5=sQuery(id+"F0.wireOp",EDGE,"E3.0.4.207");Q250=makeQuery(id+"F0.imprint","IMPRINT",FACE,{"disambiguationData":[TD([[makeQuery(id+"F0.imprint","IMPRINT",EDGE,{"derivedFrom":subQ5}),1.0]])]});}
            var Q251;
            {var subQ3=sQuery(id+"F0.wireOp",EDGE,"E3.0.3.167");var subQ9=sQuery(id+"F0.wireOp",EDGE,"E3.0.3.205");var subQ10=makeQuery(id+"F0.imprint","INTERSECT",VERTEX,{"derivedFrom":[subQ3,subQ9]});Q251=makeQuery(id+"F0.imprint","IMPRINT",FACE,{"disambiguationData":[TD([[makeQuery(id+"F0.imprint","IMPRINT",EDGE,{"disambiguationData":[TD([[subQ10,1.0]])],"derivedFrom":subQ3}),1.0]])]});}
            var Q252;
            {var subQ7=sQuery(id+"F0.wireOp",EDGE,"E3.0.1.127");var subQ9=sQuery(id+"F0.wireOp",EDGE,"E3.0.1.84");var subQ10=makeQuery(id+"F0.imprint","INTERSECT",VERTEX,{"derivedFrom":[subQ9,subQ7]});Q252=makeQuery(id+"F0.imprint","IMPRINT",FACE,{"disambiguationData":[TD([[makeQuery(id+"F0.imprint","IMPRINT",EDGE,{"disambiguationData":[TD([[subQ10,1.0]])],"derivedFrom":subQ9}),1.0]])]});}
            var Q253;
            {var subQ0=sQuery(id+"F0.wireOp",EDGE,"E3.0.1.125");var subQ1=sQuery(id+"F0.wireOp",EDGE,"E3.0.1.26");var subQ2=makeQuery(id+"F0.imprint","INTERSECT",VERTEX,{"derivedFrom":[subQ1,subQ0]});Q253=makeQuery(id+"F0.imprint","IMPRINT",FACE,{"disambiguationData":[TD([[makeQuery(id+"F0.imprint","IMPRINT",EDGE,{"disambiguationData":[TD([[subQ2,1.0]])],"derivedFrom":subQ1}),-1.0]])]});}
            var Q254;
            {var subQ3=sQuery(id+"F0.wireOp",EDGE,"E2.5.0.3");var subQ6=sQuery(id+"F0.wireOp",EDGE,"E2.5.0.1");var subQ10=makeQuery(id+"F0.imprint","INTERSECT",VERTEX,{"derivedFrom":[subQ6,subQ3]});Q254=makeQuery(id+"F0.imprint","IMPRINT",FACE,{"disambiguationData":[TD([[makeQuery(id+"F0.imprint","IMPRINT",EDGE,{"disambiguationData":[TD([[subQ10,1.0]])],"derivedFrom":subQ6}),1.0]])]});}
            var Q255;
            {var subQ5=sQuery(id+"F0.wireOp",EDGE,"E3.0.4.244");Q255=makeQuery(id+"F0.imprint","IMPRINT",FACE,{"disambiguationData":[TD([[makeQuery(id+"F0.imprint","IMPRINT",EDGE,{"derivedFrom":subQ5}),1.0]])]});}
            var Q256;
            {var subQ3=sQuery(id+"F0.wireOp",EDGE,"E2.21.0.3");var subQ9=sQuery(id+"F0.wireOp",EDGE,"E2.21.0.1");var subQ11=makeQuery(id+"F0.imprint","INTERSECT",VERTEX,{"derivedFrom":[subQ9,subQ3]});Q256=makeQuery(id+"F0.imprint","IMPRINT",FACE,{"disambiguationData":[TD([[makeQuery(id+"F0.imprint","IMPRINT",EDGE,{"disambiguationData":[TD([[subQ11,1.0]])],"derivedFrom":subQ9}),1.0]])]});}
            var Q257;
            {var subQ3=sQuery(id+"F0.wireOp",EDGE,"E2.17.0.3");var subQ6=sQuery(id+"F0.wireOp",EDGE,"E2.17.0.1");var subQ10=makeQuery(id+"F0.imprint","INTERSECT",VERTEX,{"derivedFrom":[subQ6,subQ3]});Q257=makeQuery(id+"F0.imprint","IMPRINT",FACE,{"disambiguationData":[TD([[makeQuery(id+"F0.imprint","IMPRINT",EDGE,{"disambiguationData":[TD([[subQ10,1.0]])],"derivedFrom":subQ6}),1.0]])]});}
            var Q258;
            {var subQ3=sQuery(id+"F0.wireOp",EDGE,"E2.13.0.3");var subQ6=sQuery(id+"F0.wireOp",EDGE,"E2.13.0.1");var subQ10=makeQuery(id+"F0.imprint","INTERSECT",VERTEX,{"derivedFrom":[subQ6,subQ3]});Q258=makeQuery(id+"F0.imprint","IMPRINT",FACE,{"disambiguationData":[TD([[makeQuery(id+"F0.imprint","IMPRINT",EDGE,{"disambiguationData":[TD([[subQ10,1.0]])],"derivedFrom":subQ6}),1.0]])]});}
            var Q259;
            {var subQ6=sQuery(id+"F0.wireOp",EDGE,"E3.0.1.125");var subQ9=sQuery(id+"F0.wireOp",EDGE,"E3.0.1.26");var subQ10=makeQuery(id+"F0.imprint","INTERSECT",VERTEX,{"derivedFrom":[subQ9,subQ6]});Q259=makeQuery(id+"F0.imprint","IMPRINT",FACE,{"disambiguationData":[TD([[makeQuery(id+"F0.imprint","IMPRINT",EDGE,{"disambiguationData":[TD([[subQ10,1.0]])],"derivedFrom":subQ9}),1.0]])]});}
            var Q260;
            {var subQ3=sQuery(id+"F0.wireOp",EDGE,"E2.25.0.3");var subQ8=sQuery(id+"F0.wireOp",EDGE,"E2.25.0.1");var subQ11=makeQuery(id+"F0.imprint","INTERSECT",VERTEX,{"derivedFrom":[subQ8,subQ3]});Q260=makeQuery(id+"F0.imprint","IMPRINT",FACE,{"disambiguationData":[TD([[makeQuery(id+"F0.imprint","IMPRINT",EDGE,{"disambiguationData":[TD([[subQ11,1.0]])],"derivedFrom":subQ8}),1.0]])]});}
            var Q261;
            {var subQ1=sQuery(id+"F0.wireOp",EDGE,"E3.0.1.215");var subQ5=sQuery(id+"F0.wireOp",EDGE,"E3.0.1.186");var subQ6=makeQuery(id+"F0.imprint","INTERSECT",VERTEX,{"derivedFrom":[subQ5,subQ1]});Q261=makeQuery(id+"F0.imprint","IMPRINT",FACE,{"disambiguationData":[TD([[makeQuery(id+"F0.imprint","IMPRINT",EDGE,{"disambiguationData":[TD([[subQ6,1.0]])],"derivedFrom":subQ5}),1.0]])]});}
            var Q262;
            {var subQ1=sQuery(id+"F0.wireOp",EDGE,"E3.0.3.125");var subQ9=sQuery(id+"F0.wireOp",EDGE,"E3.0.3.26");var subQ10=makeQuery(id+"F0.imprint","INTERSECT",VERTEX,{"derivedFrom":[subQ9,subQ1]});Q262=makeQuery(id+"F0.imprint","IMPRINT",FACE,{"disambiguationData":[TD([[makeQuery(id+"F0.imprint","IMPRINT",EDGE,{"disambiguationData":[TD([[subQ10,1.0]])],"derivedFrom":subQ9}),1.0]])]});}
            var Q263;
            {var subQ0=sQuery(id+"F0.wireOp",EDGE,"E3.0.3.222");var subQ1=sQuery(id+"F0.wireOp",EDGE,"E3.0.3.152");var subQ2=makeQuery(id+"F0.imprint","INTERSECT",VERTEX,{"derivedFrom":[subQ1,subQ0]});Q263=makeQuery(id+"F0.imprint","IMPRINT",FACE,{"disambiguationData":[TD([[makeQuery(id+"F0.imprint","IMPRINT",EDGE,{"disambiguationData":[TD([[subQ2,-1.0]])],"derivedFrom":subQ1}),1.0]])]});}
            var Q264;
            {var subQ1=sQuery(id+"F0.wireOp",EDGE,"E3.0.3.144");var subQ8=sQuery(id+"F0.wireOp",EDGE,"E3.0.3.153");var subQ10=makeQuery(id+"F0.imprint","INTERSECT",VERTEX,{"derivedFrom":[subQ1,subQ8]});Q264=makeQuery(id+"F0.imprint","IMPRINT",FACE,{"disambiguationData":[TD([[makeQuery(id+"F0.imprint","IMPRINT",EDGE,{"disambiguationData":[TD([[subQ10,1.0]])],"derivedFrom":subQ1}),1.0]])]});}
            var Q265;
            {var subQ0=sQuery(id+"F0.wireOp",EDGE,"E3.0.3.197");var subQ1=sQuery(id+"F0.wireOp",EDGE,"E3.0.3.85");var subQ2=makeQuery(id+"F0.imprint","INTERSECT",VERTEX,{"derivedFrom":[subQ1,subQ0]});Q265=makeQuery(id+"F0.imprint","IMPRINT",FACE,{"disambiguationData":[TD([[makeQuery(id+"F0.imprint","IMPRINT",EDGE,{"disambiguationData":[TD([[subQ2,-1.0]])],"derivedFrom":subQ1}),-1.0]])]});}
            var Q266;
            {var subQ0=sQuery(id+"F0.wireOp",EDGE,"E3.0.4.158");var subQ1=sQuery(id+"F0.wireOp",EDGE,"E3.0.4.138");var subQ2=makeQuery(id+"F0.imprint","INTERSECT",VERTEX,{"derivedFrom":[subQ1,subQ0]});Q266=makeQuery(id+"F0.imprint","IMPRINT",FACE,{"disambiguationData":[TD([[makeQuery(id+"F0.imprint","IMPRINT",EDGE,{"disambiguationData":[TD([[subQ2,1.0]])],"derivedFrom":subQ1}),1.0]])]});}
            var Q267;
            {var subQ0=sQuery(id+"F0.wireOp",EDGE,"E3.0.4.104");var subQ1=sQuery(id+"F0.wireOp",EDGE,"E3.0.4.83");var subQ2=makeQuery(id+"F0.imprint","INTERSECT",VERTEX,{"derivedFrom":[subQ1,subQ0]});Q267=makeQuery(id+"F0.imprint","IMPRINT",FACE,{"disambiguationData":[TD([[makeQuery(id+"F0.imprint","IMPRINT",EDGE,{"disambiguationData":[TD([[subQ2,1.0]])],"derivedFrom":subQ1}),-1.0]])]});}
            var Q268;
            {var subQ6=sQuery(id+"F0.wireOp",EDGE,"E3.0.3.215");var subQ9=sQuery(id+"F0.wireOp",EDGE,"E3.0.3.186");var subQ10=makeQuery(id+"F0.imprint","INTERSECT",VERTEX,{"derivedFrom":[subQ9,subQ6]});Q268=makeQuery(id+"F0.imprint","IMPRINT",FACE,{"disambiguationData":[TD([[makeQuery(id+"F0.imprint","IMPRINT",EDGE,{"disambiguationData":[TD([[subQ10,1.0]])],"derivedFrom":subQ9}),1.0]])]});}
            var Q269;
            {var subQ5=sQuery(id+"F0.wireOp",EDGE,"E2.5.0.7");var subQ6=sQuery(id+"F0.wireOp",EDGE,"E2.5.0.5");var subQ7=makeQuery(id+"F0.imprint","INTERSECT",VERTEX,{"derivedFrom":[subQ6,subQ5]});Q269=makeQuery(id+"F0.imprint","IMPRINT",FACE,{"disambiguationData":[TD([[makeQuery(id+"F0.imprint","IMPRINT",EDGE,{"disambiguationData":[TD([[subQ7,1.0]])],"derivedFrom":subQ6}),1.0]])]});}
            var Q270;
            {var subQ5=sQuery(id+"F0.wireOp",EDGE,"E3.0.4.212");Q270=makeQuery(id+"F0.imprint","IMPRINT",FACE,{"disambiguationData":[TD([[makeQuery(id+"F0.imprint","IMPRINT",EDGE,{"derivedFrom":subQ5}),1.0]])]});}
            var Q271;
            {var subQ0=sQuery(id+"F0.wireOp",EDGE,"E3.0.1.213");var subQ1=sQuery(id+"F0.wireOp",EDGE,"E3.0.1.187");var subQ2=makeQuery(id+"F0.imprint","INTERSECT",VERTEX,{"derivedFrom":[subQ1,subQ0]});Q271=makeQuery(id+"F0.imprint","IMPRINT",FACE,{"disambiguationData":[TD([[makeQuery(id+"F0.imprint","IMPRINT",EDGE,{"disambiguationData":[TD([[subQ2,1.0]])],"derivedFrom":subQ1}),-1.0]])]});}
            var Q272;
            {var subQ0=sQuery(id+"F0.wireOp",EDGE,"E3.0.2.196");var subQ1=sQuery(id+"F0.wireOp",EDGE,"E3.0.2.101");var subQ2=makeQuery(id+"F0.imprint","INTERSECT",VERTEX,{"derivedFrom":[subQ1,subQ0]});Q272=makeQuery(id+"F0.imprint","IMPRINT",FACE,{"disambiguationData":[TD([[makeQuery(id+"F0.imprint","IMPRINT",EDGE,{"disambiguationData":[TD([[subQ2,1.0]])],"derivedFrom":subQ1}),-1.0]])]});}
            var Q273;
            {var subQ1=sQuery(id+"F0.wireOp",EDGE,"E3.0.3.126");var subQ9=sQuery(id+"F0.wireOp",EDGE,"E3.0.3.85");var subQ10=makeQuery(id+"F0.imprint","INTERSECT",VERTEX,{"derivedFrom":[subQ9,subQ1]});Q273=makeQuery(id+"F0.imprint","IMPRINT",FACE,{"disambiguationData":[TD([[makeQuery(id+"F0.imprint","IMPRINT",EDGE,{"disambiguationData":[TD([[subQ10,1.0]])],"derivedFrom":subQ9}),1.0]])]});}
            var Q274;
            {var subQ0=sQuery(id+"F0.wireOp",EDGE,"E3.0.4.159");var subQ1=sQuery(id+"F0.wireOp",EDGE,"E3.0.4.139");var subQ2=makeQuery(id+"F0.imprint","INTERSECT",VERTEX,{"derivedFrom":[subQ1,subQ0]});Q274=makeQuery(id+"F0.imprint","IMPRINT",FACE,{"disambiguationData":[TD([[makeQuery(id+"F0.imprint","IMPRINT",EDGE,{"disambiguationData":[TD([[subQ2,1.0]])],"derivedFrom":subQ1}),1.0]])]});}
            var Q275;
            {var subQ0=sQuery(id+"F0.wireOp",EDGE,"E3.0.4.197");var subQ1=sQuery(id+"F0.wireOp",EDGE,"E3.0.4.85");var subQ2=makeQuery(id+"F0.imprint","INTERSECT",VERTEX,{"derivedFrom":[subQ1,subQ0]});Q275=makeQuery(id+"F0.imprint","IMPRINT",FACE,{"disambiguationData":[TD([[makeQuery(id+"F0.imprint","IMPRINT",EDGE,{"disambiguationData":[TD([[subQ2,1.0]])],"derivedFrom":subQ1}),-1.0]])]});}
            var Q276;
            {var subQ0=sQuery(id+"F0.wireOp",EDGE,"E2.1.0.7");var subQ1=sQuery(id+"F0.wireOp",EDGE,"E2.1.0.5");var subQ2=makeQuery(id+"F0.imprint","INTERSECT",VERTEX,{"derivedFrom":[subQ1,subQ0]});Q276=makeQuery(id+"F0.imprint","IMPRINT",FACE,{"disambiguationData":[TD([[makeQuery(id+"F0.imprint","IMPRINT",EDGE,{"disambiguationData":[TD([[subQ2,1.0]])],"derivedFrom":subQ1}),-1.0]])]});}
            var Q277;
            {var subQ5=sQuery(id+"F0.wireOp",EDGE,"E3.0.4.204");Q277=makeQuery(id+"F0.imprint","IMPRINT",FACE,{"disambiguationData":[TD([[makeQuery(id+"F0.imprint","IMPRINT",EDGE,{"derivedFrom":subQ5}),1.0]])]});}
            var Q278;
            {var subQ3=sQuery(id+"F0.wireOp",EDGE,"E3.0.4.129");Q278=makeQuery(id+"F0.imprint","IMPRINT",FACE,{"disambiguationData":[TD([[makeQuery(id+"F0.imprint","IMPRINT",EDGE,{"derivedFrom":subQ3}),1.0]])]});}
            var Q279;
            {var subQ0=sQuery(id+"F0.wireOp",EDGE,"E2.9.0.7");var subQ1=sQuery(id+"F0.wireOp",EDGE,"E2.9.0.5");var subQ2=makeQuery(id+"F0.imprint","INTERSECT",VERTEX,{"derivedFrom":[subQ1,subQ0]});Q279=makeQuery(id+"F0.imprint","IMPRINT",FACE,{"disambiguationData":[TD([[makeQuery(id+"F0.imprint","IMPRINT",EDGE,{"disambiguationData":[TD([[subQ2,1.0]])],"derivedFrom":subQ1}),-1.0]])]});}
            var Q280;
            {var subQ0=sQuery(id+"F0.wireOp",EDGE,"E2.29.0.7");var subQ1=sQuery(id+"F0.wireOp",EDGE,"E2.29.0.5");var subQ2=makeQuery(id+"F0.imprint","INTERSECT",VERTEX,{"derivedFrom":[subQ1,subQ0]});Q280=makeQuery(id+"F0.imprint","IMPRINT",FACE,{"disambiguationData":[TD([[makeQuery(id+"F0.imprint","IMPRINT",EDGE,{"disambiguationData":[TD([[subQ2,1.0]])],"derivedFrom":subQ1}),-1.0]])]});}
            var Q281;
            {var subQ0=sQuery(id+"F0.wireOp",EDGE,"E3.0.2.208");var subQ1=sQuery(id+"F0.wireOp",EDGE,"E3.0.2.164");var subQ2=makeQuery(id+"F0.imprint","INTERSECT",VERTEX,{"derivedFrom":[subQ1,subQ0]});Q281=makeQuery(id+"F0.imprint","IMPRINT",FACE,{"disambiguationData":[TD([[makeQuery(id+"F0.imprint","IMPRINT",EDGE,{"disambiguationData":[TD([[subQ2,1.0]])],"derivedFrom":subQ1}),-1.0]])]});}
            var Q282;
            {var subQ1=sQuery(id+"F0.wireOp",EDGE,"E3.0.2.149");var subQ7=sQuery(id+"F0.wireOp",EDGE,"E3.0.2.159");var subQ8=makeQuery(id+"F0.imprint","INTERSECT",VERTEX,{"derivedFrom":[subQ1,subQ7]});Q282=makeQuery(id+"F0.imprint","IMPRINT",FACE,{"disambiguationData":[TD([[makeQuery(id+"F0.imprint","IMPRINT",EDGE,{"disambiguationData":[TD([[subQ8,1.0]])],"derivedFrom":subQ1}),1.0]])]});}
            var Q283;
            {var subQ3=sQuery(id+"F0.wireOp",EDGE,"E3.0.3.154");var subQ5=sQuery(id+"F0.wireOp",EDGE,"E3.0.3.223");var subQ6=makeQuery(id+"F0.imprint","INTERSECT",VERTEX,{"derivedFrom":[subQ3,subQ5]});Q283=makeQuery(id+"F0.imprint","IMPRINT",FACE,{"disambiguationData":[TD([[makeQuery(id+"F0.imprint","IMPRINT",EDGE,{"disambiguationData":[TD([[subQ6,-1.0]])],"derivedFrom":subQ3}),1.0]])]});}
            var Q284;
            {var subQ1=sQuery(id+"F0.wireOp",EDGE,"E3.0.3.145");var subQ9=sQuery(id+"F0.wireOp",EDGE,"E3.0.3.155");var subQ11=makeQuery(id+"F0.imprint","INTERSECT",VERTEX,{"derivedFrom":[subQ1,subQ9]});Q284=makeQuery(id+"F0.imprint","IMPRINT",FACE,{"disambiguationData":[TD([[makeQuery(id+"F0.imprint","IMPRINT",EDGE,{"disambiguationData":[TD([[subQ11,1.0]])],"derivedFrom":subQ1}),1.0]])]});}
            var Q285;
            {var subQ0=sQuery(id+"F0.wireOp",EDGE,"E3.0.4.160");var subQ1=sQuery(id+"F0.wireOp",EDGE,"E3.0.4.141");var subQ2=makeQuery(id+"F0.imprint","INTERSECT",VERTEX,{"derivedFrom":[subQ1,subQ0]});Q285=makeQuery(id+"F0.imprint","IMPRINT",FACE,{"disambiguationData":[TD([[makeQuery(id+"F0.imprint","IMPRINT",EDGE,{"disambiguationData":[TD([[subQ2,1.0]])],"derivedFrom":subQ1}),1.0]])]});}
            var Q286;
            {var subQ3=sQuery(id+"F0.wireOp",EDGE,"E3.0.4.217");Q286=makeQuery(id+"F0.imprint","IMPRINT",FACE,{"disambiguationData":[TD([[makeQuery(id+"F0.imprint","IMPRINT",EDGE,{"derivedFrom":subQ3}),1.0]])]});}
            var Q287;
            {var subQ0=sQuery(id+"F0.wireOp",EDGE,"E3.0.1.10");var subQ1=sQuery(id+"F0.wireOp",EDGE,"E3.0.1.9");var subQ2=makeQuery(id+"F0.imprint","INTERSECT",VERTEX,{"derivedFrom":[subQ1,subQ0]});Q287=makeQuery(id+"F0.imprint","IMPRINT",FACE,{"disambiguationData":[TD([[makeQuery(id+"F0.imprint","IMPRINT",EDGE,{"disambiguationData":[TD([[subQ2,1.0]])],"derivedFrom":subQ1}),-1.0]])]});}
            var Q288;
            {var subQ7=sQuery(id+"F0.wireOp",EDGE,"E3.0.2.185");var subQ9=sQuery(id+"F0.wireOp",EDGE,"E3.0.2.199");var subQ10=makeQuery(id+"F0.imprint","INTERSECT",VERTEX,{"derivedFrom":[subQ7,subQ9]});Q288=makeQuery(id+"F0.imprint","IMPRINT",FACE,{"disambiguationData":[TD([[makeQuery(id+"F0.imprint","IMPRINT",EDGE,{"disambiguationData":[TD([[subQ10,-1.0]])],"derivedFrom":subQ7}),-1.0]])]});}
            var Q289;
            {var subQ0=sQuery(id+"F0.wireOp",EDGE,"E3.0.3.10");var subQ1=sQuery(id+"F0.wireOp",EDGE,"E3.0.3.9");var subQ2=makeQuery(id+"F0.imprint","INTERSECT",VERTEX,{"derivedFrom":[subQ1,subQ0]});Q289=makeQuery(id+"F0.imprint","IMPRINT",FACE,{"disambiguationData":[TD([[makeQuery(id+"F0.imprint","IMPRINT",EDGE,{"disambiguationData":[TD([[subQ2,1.0]])],"derivedFrom":subQ1}),-1.0]])]});}
            var Q290;
            {var subQ0=sQuery(id+"F0.wireOp",EDGE,"E3.0.4.161");var subQ1=sQuery(id+"F0.wireOp",EDGE,"E3.0.4.140");var subQ2=makeQuery(id+"F0.imprint","INTERSECT",VERTEX,{"derivedFrom":[subQ1,subQ0]});Q290=makeQuery(id+"F0.imprint","IMPRINT",FACE,{"disambiguationData":[TD([[makeQuery(id+"F0.imprint","IMPRINT",EDGE,{"disambiguationData":[TD([[subQ2,1.0]])],"derivedFrom":subQ1}),1.0]])]});}
            var Q291;
            {var subQ5=sQuery(id+"F0.wireOp",EDGE,"E3.0.3.209");var subQ9=sQuery(id+"F0.wireOp",EDGE,"E3.0.3.169");var subQ11=makeQuery(id+"F0.imprint","INTERSECT",VERTEX,{"derivedFrom":[subQ9,subQ5]});Q291=makeQuery(id+"F0.imprint","IMPRINT",FACE,{"disambiguationData":[TD([[makeQuery(id+"F0.imprint","IMPRINT",EDGE,{"disambiguationData":[TD([[subQ11,1.0]])],"derivedFrom":subQ9}),1.0]])]});}
            var Q292;
            {var subQ3=sQuery(id+"F0.wireOp",EDGE,"E2.6.0.3");var subQ6=sQuery(id+"F0.wireOp",EDGE,"E2.6.0.1");var subQ10=makeQuery(id+"F0.imprint","INTERSECT",VERTEX,{"derivedFrom":[subQ6,subQ3]});Q292=makeQuery(id+"F0.imprint","IMPRINT",FACE,{"disambiguationData":[TD([[makeQuery(id+"F0.imprint","IMPRINT",EDGE,{"disambiguationData":[TD([[subQ10,1.0]])],"derivedFrom":subQ6}),1.0]])]});}
            var Q293;
            {var subQ3=sQuery(id+"F0.wireOp",EDGE,"E2.2.0.3");var subQ8=sQuery(id+"F0.wireOp",EDGE,"E2.2.0.1");var subQ11=makeQuery(id+"F0.imprint","INTERSECT",VERTEX,{"derivedFrom":[subQ8,subQ3]});Q293=makeQuery(id+"F0.imprint","IMPRINT",FACE,{"disambiguationData":[TD([[makeQuery(id+"F0.imprint","IMPRINT",EDGE,{"disambiguationData":[TD([[subQ11,1.0]])],"derivedFrom":subQ8}),1.0]])]});}
            var Q294;
            {var subQ5=sQuery(id+"F0.wireOp",EDGE,"E3.0.4.206");Q294=makeQuery(id+"F0.imprint","IMPRINT",FACE,{"disambiguationData":[TD([[makeQuery(id+"F0.imprint","IMPRINT",EDGE,{"derivedFrom":subQ5}),1.0]])]});}
            var Q295;
            {var subQ3=sQuery(id+"F0.wireOp",EDGE,"E2.22.0.3");var subQ6=sQuery(id+"F0.wireOp",EDGE,"E2.22.0.1");var subQ10=makeQuery(id+"F0.imprint","INTERSECT",VERTEX,{"derivedFrom":[subQ6,subQ3]});Q295=makeQuery(id+"F0.imprint","IMPRINT",FACE,{"disambiguationData":[TD([[makeQuery(id+"F0.imprint","IMPRINT",EDGE,{"disambiguationData":[TD([[subQ10,1.0]])],"derivedFrom":subQ6}),1.0]])]});}
            var Q296;
            {var subQ3=sQuery(id+"F0.wireOp",EDGE,"E2.18.0.3");var subQ6=sQuery(id+"F0.wireOp",EDGE,"E2.18.0.1");var subQ10=makeQuery(id+"F0.imprint","INTERSECT",VERTEX,{"derivedFrom":[subQ6,subQ3]});Q296=makeQuery(id+"F0.imprint","IMPRINT",FACE,{"disambiguationData":[TD([[makeQuery(id+"F0.imprint","IMPRINT",EDGE,{"disambiguationData":[TD([[subQ10,1.0]])],"derivedFrom":subQ6}),1.0]])]});}
            var Q297;
            {var subQ3=sQuery(id+"F0.wireOp",EDGE,"E2.14.0.3");var subQ6=sQuery(id+"F0.wireOp",EDGE,"E2.14.0.1");var subQ10=makeQuery(id+"F0.imprint","INTERSECT",VERTEX,{"derivedFrom":[subQ6,subQ3]});Q297=makeQuery(id+"F0.imprint","IMPRINT",FACE,{"disambiguationData":[TD([[makeQuery(id+"F0.imprint","IMPRINT",EDGE,{"disambiguationData":[TD([[subQ10,1.0]])],"derivedFrom":subQ6}),1.0]])]});}
            var Q298;
            {var subQ3=sQuery(id+"F0.wireOp",EDGE,"E2.10.0.3");var subQ6=sQuery(id+"F0.wireOp",EDGE,"E2.10.0.1");var subQ10=makeQuery(id+"F0.imprint","INTERSECT",VERTEX,{"derivedFrom":[subQ6,subQ3]});Q298=makeQuery(id+"F0.imprint","IMPRINT",FACE,{"disambiguationData":[TD([[makeQuery(id+"F0.imprint","IMPRINT",EDGE,{"disambiguationData":[TD([[subQ10,1.0]])],"derivedFrom":subQ6}),1.0]])]});}
            var Q299;
            {var subQ5=sQuery(id+"F0.wireOp",EDGE,"E3.0.2.100");var subQ6=sQuery(id+"F0.wireOp",EDGE,"E3.0.2.89");var subQ7=makeQuery(id+"F0.imprint","INTERSECT",VERTEX,{"derivedFrom":[subQ6,subQ5]});Q299=makeQuery(id+"F0.imprint","IMPRINT",FACE,{"disambiguationData":[TD([[makeQuery(id+"F0.imprint","IMPRINT",EDGE,{"disambiguationData":[TD([[subQ7,-1.0]])],"derivedFrom":subQ6}),-1.0]])]});}
            var Q300;
            {var subQ1=sQuery(id+"F0.wireOp",EDGE,"E3.0.3.102");var subQ7=sQuery(id+"F0.wireOp",EDGE,"E3.0.3.81");var subQ8=makeQuery(id+"F0.imprint","INTERSECT",VERTEX,{"derivedFrom":[subQ7,subQ1]});Q300=makeQuery(id+"F0.imprint","IMPRINT",FACE,{"disambiguationData":[TD([[makeQuery(id+"F0.imprint","IMPRINT",EDGE,{"disambiguationData":[TD([[subQ8,-1.0]])],"derivedFrom":subQ7}),-1.0]])]});}
            var Q301;
            {var subQ3=sQuery(id+"F0.wireOp",EDGE,"E3.0.3.227");var subQ6=sQuery(id+"F0.wireOp",EDGE,"E3.0.3.146");var subQ10=makeQuery(id+"F0.imprint","INTERSECT",VERTEX,{"derivedFrom":[subQ6,subQ3]});Q301=makeQuery(id+"F0.imprint","IMPRINT",FACE,{"disambiguationData":[TD([[makeQuery(id+"F0.imprint","IMPRINT",EDGE,{"disambiguationData":[TD([[subQ10,1.0]])],"derivedFrom":subQ6}),1.0]])]});}
            var Q302;
            {var subQ0=sQuery(id+"F0.wireOp",EDGE,"E3.0.4.222");var subQ1=sQuery(id+"F0.wireOp",EDGE,"E3.0.4.152");var subQ2=makeQuery(id+"F0.imprint","INTERSECT",VERTEX,{"derivedFrom":[subQ1,subQ0]});Q302=makeQuery(id+"F0.imprint","IMPRINT",FACE,{"disambiguationData":[TD([[makeQuery(id+"F0.imprint","IMPRINT",EDGE,{"disambiguationData":[TD([[subQ2,1.0]])],"derivedFrom":subQ1}),1.0]])]});}
            var Q303;
            {var subQ0=sQuery(id+"F0.wireOp",EDGE,"E3.0.4.97");var subQ1=sQuery(id+"F0.wireOp",EDGE,"E3.0.4.86");var subQ2=makeQuery(id+"F0.imprint","INTERSECT",VERTEX,{"derivedFrom":[subQ1,subQ0]});Q303=makeQuery(id+"F0.imprint","IMPRINT",FACE,{"disambiguationData":[TD([[makeQuery(id+"F0.imprint","IMPRINT",EDGE,{"disambiguationData":[TD([[subQ2,1.0]])],"derivedFrom":subQ1}),-1.0]])]});}
            var Q304;
            {var subQ0=sQuery(id+"F0.wireOp",EDGE,"E2.10.0.7");var subQ1=sQuery(id+"F0.wireOp",EDGE,"E2.10.0.5");var subQ2=makeQuery(id+"F0.imprint","INTERSECT",VERTEX,{"derivedFrom":[subQ1,subQ0]});Q304=makeQuery(id+"F0.imprint","IMPRINT",FACE,{"disambiguationData":[TD([[makeQuery(id+"F0.imprint","IMPRINT",EDGE,{"disambiguationData":[TD([[subQ2,1.0]])],"derivedFrom":subQ1}),-1.0]])]});}
            var Q305;
            {var subQ0=sQuery(id+"F0.wireOp",EDGE,"E2.6.0.7");var subQ1=sQuery(id+"F0.wireOp",EDGE,"E2.6.0.5");var subQ2=makeQuery(id+"F0.imprint","INTERSECT",VERTEX,{"derivedFrom":[subQ1,subQ0]});Q305=makeQuery(id+"F0.imprint","IMPRINT",FACE,{"disambiguationData":[TD([[makeQuery(id+"F0.imprint","IMPRINT",EDGE,{"disambiguationData":[TD([[subQ2,1.0]])],"derivedFrom":subQ1}),-1.0]])]});}
            var Q306;
            {var subQ0=sQuery(id+"F0.wireOp",EDGE,"E2.2.0.7");var subQ1=sQuery(id+"F0.wireOp",EDGE,"E2.2.0.5");var subQ2=makeQuery(id+"F0.imprint","INTERSECT",VERTEX,{"derivedFrom":[subQ1,subQ0]});Q306=makeQuery(id+"F0.imprint","IMPRINT",FACE,{"disambiguationData":[TD([[makeQuery(id+"F0.imprint","IMPRINT",EDGE,{"disambiguationData":[TD([[subQ2,1.0]])],"derivedFrom":subQ1}),-1.0]])]});}
            var Q307;
            {var subQ0=sQuery(id+"F0.wireOp",EDGE,"E2.26.0.7");var subQ1=sQuery(id+"F0.wireOp",EDGE,"E2.26.0.5");var subQ2=makeQuery(id+"F0.imprint","INTERSECT",VERTEX,{"derivedFrom":[subQ1,subQ0]});Q307=makeQuery(id+"F0.imprint","IMPRINT",FACE,{"disambiguationData":[TD([[makeQuery(id+"F0.imprint","IMPRINT",EDGE,{"disambiguationData":[TD([[subQ2,1.0]])],"derivedFrom":subQ1}),-1.0]])]});}
            var Q308;
            {var subQ0=sQuery(id+"F0.wireOp",EDGE,"E2.22.0.7");var subQ1=sQuery(id+"F0.wireOp",EDGE,"E2.22.0.5");var subQ2=makeQuery(id+"F0.imprint","INTERSECT",VERTEX,{"derivedFrom":[subQ1,subQ0]});Q308=makeQuery(id+"F0.imprint","IMPRINT",FACE,{"disambiguationData":[TD([[makeQuery(id+"F0.imprint","IMPRINT",EDGE,{"disambiguationData":[TD([[subQ2,1.0]])],"derivedFrom":subQ1}),-1.0]])]});}
            var Q309;
            {var subQ0=sQuery(id+"F0.wireOp",EDGE,"E2.18.0.7");var subQ1=sQuery(id+"F0.wireOp",EDGE,"E2.18.0.5");var subQ2=makeQuery(id+"F0.imprint","INTERSECT",VERTEX,{"derivedFrom":[subQ1,subQ0]});Q309=makeQuery(id+"F0.imprint","IMPRINT",FACE,{"disambiguationData":[TD([[makeQuery(id+"F0.imprint","IMPRINT",EDGE,{"disambiguationData":[TD([[subQ2,1.0]])],"derivedFrom":subQ1}),-1.0]])]});}
            var Q310;
            {var subQ3=sQuery(id+"F0.wireOp",EDGE,"E3.0.1.81");var subQ9=sQuery(id+"F0.wireOp",EDGE,"E3.0.1.129");var subQ10=makeQuery(id+"F0.imprint","INTERSECT",VERTEX,{"derivedFrom":[subQ3,subQ9]});Q310=makeQuery(id+"F0.imprint","IMPRINT",FACE,{"disambiguationData":[TD([[makeQuery(id+"F0.imprint","IMPRINT",EDGE,{"disambiguationData":[TD([[subQ10,1.0]])],"derivedFrom":subQ3}),1.0]])]});}
            var Q311;
            {var subQ1=sQuery(id+"F0.wireOp",EDGE,"E3.0.2.95");var subQ7=sQuery(id+"F0.wireOp",EDGE,"E3.0.2.84");var subQ8=makeQuery(id+"F0.imprint","INTERSECT",VERTEX,{"derivedFrom":[subQ7,subQ1]});Q311=makeQuery(id+"F0.imprint","IMPRINT",FACE,{"disambiguationData":[TD([[makeQuery(id+"F0.imprint","IMPRINT",EDGE,{"disambiguationData":[TD([[subQ8,-1.0]])],"derivedFrom":subQ7}),-1.0]])]});}
            var Q312;
            {var subQ7=sQuery(id+"F0.wireOp",EDGE,"E3.0.3.228");var subQ9=sQuery(id+"F0.wireOp",EDGE,"E3.0.3.246");var subQ10=makeQuery(id+"F0.imprint","INTERSECT",VERTEX,{"derivedFrom":[subQ7,subQ9]});Q312=makeQuery(id+"F0.imprint","IMPRINT",FACE,{"disambiguationData":[TD([[makeQuery(id+"F0.imprint","IMPRINT",EDGE,{"disambiguationData":[TD([[subQ10,1.0]])],"derivedFrom":subQ7}),1.0]])]});}
            var Q313;
            {var subQ0=sQuery(id+"F0.wireOp",EDGE,"E3.0.4.98");var subQ1=sQuery(id+"F0.wireOp",EDGE,"E3.0.4.87");var subQ2=makeQuery(id+"F0.imprint","INTERSECT",VERTEX,{"derivedFrom":[subQ1,subQ0]});Q313=makeQuery(id+"F0.imprint","IMPRINT",FACE,{"disambiguationData":[TD([[makeQuery(id+"F0.imprint","IMPRINT",EDGE,{"disambiguationData":[TD([[subQ2,1.0]])],"derivedFrom":subQ1}),-1.0]])]});}
            var Q314;
            {var subQ0=sQuery(id+"F0.wireOp",EDGE,"E3.0.2.226");var subQ1=sQuery(id+"F0.wireOp",EDGE,"E3.0.2.143");var subQ2=makeQuery(id+"F0.imprint","INTERSECT",VERTEX,{"derivedFrom":[subQ1,subQ0]});Q314=makeQuery(id+"F0.imprint","IMPRINT",FACE,{"disambiguationData":[TD([[makeQuery(id+"F0.imprint","IMPRINT",EDGE,{"disambiguationData":[TD([[subQ2,1.0]])],"derivedFrom":subQ1}),1.0]])]});}
            var Q315;
            {var subQ0=sQuery(id+"F0.wireOp",EDGE,"E2.14.0.7");var subQ1=sQuery(id+"F0.wireOp",EDGE,"E2.14.0.5");var subQ2=makeQuery(id+"F0.imprint","INTERSECT",VERTEX,{"derivedFrom":[subQ1,subQ0]});Q315=makeQuery(id+"F0.imprint","IMPRINT",FACE,{"disambiguationData":[TD([[makeQuery(id+"F0.imprint","IMPRINT",EDGE,{"disambiguationData":[TD([[subQ2,1.0]])],"derivedFrom":subQ1}),-1.0]])]});}
            var Q316;
            {var subQ5=sQuery(id+"F0.wireOp",EDGE,"E2.6.0.7");var subQ6=sQuery(id+"F0.wireOp",EDGE,"E2.6.0.5");var subQ7=makeQuery(id+"F0.imprint","INTERSECT",VERTEX,{"derivedFrom":[subQ6,subQ5]});Q316=makeQuery(id+"F0.imprint","IMPRINT",FACE,{"disambiguationData":[TD([[makeQuery(id+"F0.imprint","IMPRINT",EDGE,{"disambiguationData":[TD([[subQ7,1.0]])],"derivedFrom":subQ6}),1.0]])]});}
            var Q317;
            {var subQ0=sQuery(id+"F0.wireOp",EDGE,"E3.0.4.224");var subQ1=sQuery(id+"F0.wireOp",EDGE,"E3.0.4.157");var subQ2=makeQuery(id+"F0.imprint","INTERSECT",VERTEX,{"derivedFrom":[subQ1,subQ0]});Q317=makeQuery(id+"F0.imprint","IMPRINT",FACE,{"disambiguationData":[TD([[makeQuery(id+"F0.imprint","IMPRINT",EDGE,{"disambiguationData":[TD([[subQ2,1.0]])],"derivedFrom":subQ1}),1.0]])]});}
            var Q318;
            {var subQ0=sQuery(id+"F0.wireOp",EDGE,"E3.0.1.216");var subQ1=sQuery(id+"F0.wireOp",EDGE,"E3.0.1.87");var subQ2=makeQuery(id+"F0.imprint","INTERSECT",VERTEX,{"derivedFrom":[subQ1,subQ0]});Q318=makeQuery(id+"F0.imprint","IMPRINT",FACE,{"disambiguationData":[TD([[makeQuery(id+"F0.imprint","IMPRINT",EDGE,{"disambiguationData":[TD([[subQ2,1.0]])],"derivedFrom":subQ1}),-1.0]])]});}
            var Q319;
            {var subQ0=sQuery(id+"F0.wireOp",EDGE,"E3.0.2.222");var subQ1=sQuery(id+"F0.wireOp",EDGE,"E3.0.2.152");var subQ2=makeQuery(id+"F0.imprint","INTERSECT",VERTEX,{"derivedFrom":[subQ1,subQ0]});Q319=makeQuery(id+"F0.imprint","IMPRINT",FACE,{"disambiguationData":[TD([[makeQuery(id+"F0.imprint","IMPRINT",EDGE,{"disambiguationData":[TD([[subQ2,1.0]])],"derivedFrom":subQ1}),1.0]])]});}
            var Q320;
            {var subQ0=sQuery(id+"F0.wireOp",EDGE,"E3.0.3.103");var subQ1=sQuery(id+"F0.wireOp",EDGE,"E3.0.3.82");var subQ2=makeQuery(id+"F0.imprint","INTERSECT",VERTEX,{"derivedFrom":[subQ1,subQ0]});Q320=makeQuery(id+"F0.imprint","IMPRINT",FACE,{"disambiguationData":[TD([[makeQuery(id+"F0.imprint","IMPRINT",EDGE,{"disambiguationData":[TD([[subQ2,-1.0]])],"derivedFrom":subQ1}),-1.0]])]});}
            var Q321;
            {var subQ3=sQuery(id+"F0.wireOp",EDGE,"E3.0.3.229");var subQ5=sQuery(id+"F0.wireOp",EDGE,"E3.0.3.245");var subQ6=makeQuery(id+"F0.imprint","INTERSECT",VERTEX,{"derivedFrom":[subQ3,subQ5]});Q321=makeQuery(id+"F0.imprint","IMPRINT",FACE,{"disambiguationData":[TD([[makeQuery(id+"F0.imprint","IMPRINT",EDGE,{"disambiguationData":[TD([[subQ6,1.0]])],"derivedFrom":subQ3}),1.0]])]});}
            var Q322;
            {var subQ7=sQuery(id+"F0.wireOp",EDGE,"E3.0.3.163");var subQ9=sQuery(id+"F0.wireOp",EDGE,"E3.0.3.210");var subQ10=makeQuery(id+"F0.imprint","INTERSECT",VERTEX,{"derivedFrom":[subQ7,subQ9]});Q322=makeQuery(id+"F0.imprint","IMPRINT",FACE,{"disambiguationData":[TD([[makeQuery(id+"F0.imprint","IMPRINT",EDGE,{"disambiguationData":[TD([[subQ10,1.0]])],"derivedFrom":subQ7}),1.0]])]});}
            var Q323;
            {var subQ0=sQuery(id+"F0.wireOp",EDGE,"E3.0.4.199");var subQ1=sQuery(id+"F0.wireOp",EDGE,"E3.0.4.185");var subQ2=makeQuery(id+"F0.imprint","INTERSECT",VERTEX,{"derivedFrom":[subQ1,subQ0]});Q323=makeQuery(id+"F0.imprint","IMPRINT",FACE,{"disambiguationData":[TD([[makeQuery(id+"F0.imprint","IMPRINT",EDGE,{"disambiguationData":[TD([[subQ2,1.0]])],"derivedFrom":subQ1}),-1.0]])]});}
            var Q324;
            {var subQ0=sQuery(id+"F0.wireOp",EDGE,"E3.0.4.100");var subQ1=sQuery(id+"F0.wireOp",EDGE,"E3.0.4.89");var subQ2=makeQuery(id+"F0.imprint","INTERSECT",VERTEX,{"derivedFrom":[subQ1,subQ0]});Q324=makeQuery(id+"F0.imprint","IMPRINT",FACE,{"disambiguationData":[TD([[makeQuery(id+"F0.imprint","IMPRINT",EDGE,{"disambiguationData":[TD([[subQ2,1.0]])],"derivedFrom":subQ1}),-1.0]])]});}
            var Q325;
            {var subQ3=sQuery(id+"F0.wireOp",EDGE,"E3.0.4.124");Q325=makeQuery(id+"F0.imprint","IMPRINT",FACE,{"disambiguationData":[TD([[makeQuery(id+"F0.imprint","IMPRINT",EDGE,{"derivedFrom":subQ3}),1.0]])]});}
            var Q326;
            {var subQ0=sQuery(id+"F0.wireOp",EDGE,"E3.0.1.245");var subQ1=sQuery(id+"F0.wireOp",EDGE,"E3.0.1.229");var subQ2=makeQuery(id+"F0.imprint","INTERSECT",VERTEX,{"derivedFrom":[subQ1,subQ0]});Q326=makeQuery(id+"F0.imprint","IMPRINT",FACE,{"disambiguationData":[TD([[makeQuery(id+"F0.imprint","IMPRINT",EDGE,{"disambiguationData":[TD([[subQ2,1.0]])],"derivedFrom":subQ1}),-1.0]])]});}
            var Q327;
            {var subQ0=sQuery(id+"F0.wireOp",EDGE,"E3.0.2.222");var subQ1=sQuery(id+"F0.wireOp",EDGE,"E3.0.2.152");var subQ2=makeQuery(id+"F0.imprint","INTERSECT",VERTEX,{"derivedFrom":[subQ1,subQ0]});Q327=makeQuery(id+"F0.imprint","IMPRINT",FACE,{"disambiguationData":[TD([[makeQuery(id+"F0.imprint","IMPRINT",EDGE,{"disambiguationData":[TD([[subQ2,-1.0]])],"derivedFrom":subQ1}),1.0]])]});}
            var Q328;
            {var subQ0=sQuery(id+"F0.wireOp",EDGE,"E3.0.4.198");var subQ1=sQuery(id+"F0.wireOp",EDGE,"E3.0.4.186");var subQ2=makeQuery(id+"F0.imprint","INTERSECT",VERTEX,{"derivedFrom":[subQ1,subQ0]});Q328=makeQuery(id+"F0.imprint","IMPRINT",FACE,{"disambiguationData":[TD([[makeQuery(id+"F0.imprint","IMPRINT",EDGE,{"disambiguationData":[TD([[subQ2,1.0]])],"derivedFrom":subQ1}),-1.0]])]});}
            var Q329;
            {var subQ0=sQuery(id+"F0.wireOp",EDGE,"E3.0.4.196");var subQ1=sQuery(id+"F0.wireOp",EDGE,"E3.0.4.101");var subQ2=makeQuery(id+"F0.imprint","INTERSECT",VERTEX,{"derivedFrom":[subQ1,subQ0]});Q329=makeQuery(id+"F0.imprint","IMPRINT",FACE,{"disambiguationData":[TD([[makeQuery(id+"F0.imprint","IMPRINT",EDGE,{"disambiguationData":[TD([[subQ2,1.0]])],"derivedFrom":subQ1}),-1.0]])]});}
            var Q330;
            {var subQ3=sQuery(id+"F0.wireOp",EDGE,"E3.0.4.216");Q330=makeQuery(id+"F0.imprint","IMPRINT",FACE,{"disambiguationData":[TD([[makeQuery(id+"F0.imprint","IMPRINT",EDGE,{"derivedFrom":subQ3}),1.0]])]});}
            var Q331;
            {var subQ3=sQuery(id+"F0.wireOp",EDGE,"E2.15.0.3");var subQ6=sQuery(id+"F0.wireOp",EDGE,"E2.15.0.1");var subQ10=makeQuery(id+"F0.imprint","INTERSECT",VERTEX,{"derivedFrom":[subQ6,subQ3]});Q331=makeQuery(id+"F0.imprint","IMPRINT",FACE,{"disambiguationData":[TD([[makeQuery(id+"F0.imprint","IMPRINT",EDGE,{"disambiguationData":[TD([[subQ10,1.0]])],"derivedFrom":subQ6}),1.0]])]});}
            var Q332;
            {var subQ3=sQuery(id+"F0.wireOp",EDGE,"E2.11.0.3");var subQ6=sQuery(id+"F0.wireOp",EDGE,"E2.11.0.1");var subQ10=makeQuery(id+"F0.imprint","INTERSECT",VERTEX,{"derivedFrom":[subQ6,subQ3]});Q332=makeQuery(id+"F0.imprint","IMPRINT",FACE,{"disambiguationData":[TD([[makeQuery(id+"F0.imprint","IMPRINT",EDGE,{"disambiguationData":[TD([[subQ10,1.0]])],"derivedFrom":subQ6}),1.0]])]});}
            var Q333;
            {var subQ3=sQuery(id+"F0.wireOp",EDGE,"E2.7.0.3");var subQ6=sQuery(id+"F0.wireOp",EDGE,"E2.7.0.1");var subQ10=makeQuery(id+"F0.imprint","INTERSECT",VERTEX,{"derivedFrom":[subQ6,subQ3]});Q333=makeQuery(id+"F0.imprint","IMPRINT",FACE,{"disambiguationData":[TD([[makeQuery(id+"F0.imprint","IMPRINT",EDGE,{"disambiguationData":[TD([[subQ10,1.0]])],"derivedFrom":subQ6}),1.0]])]});}
            var Q334;
            {var subQ3=sQuery(id+"F0.wireOp",EDGE,"E2.3.0.3");var subQ6=sQuery(id+"F0.wireOp",EDGE,"E2.3.0.1");var subQ10=makeQuery(id+"F0.imprint","INTERSECT",VERTEX,{"derivedFrom":[subQ6,subQ3]});Q334=makeQuery(id+"F0.imprint","IMPRINT",FACE,{"disambiguationData":[TD([[makeQuery(id+"F0.imprint","IMPRINT",EDGE,{"disambiguationData":[TD([[subQ10,1.0]])],"derivedFrom":subQ6}),1.0]])]});}
            var Q335;
            {var subQ3=sQuery(id+"F0.wireOp",EDGE,"E2.23.0.3");var subQ6=sQuery(id+"F0.wireOp",EDGE,"E2.23.0.1");var subQ11=makeQuery(id+"F0.imprint","INTERSECT",VERTEX,{"derivedFrom":[subQ6,subQ3]});Q335=makeQuery(id+"F0.imprint","IMPRINT",FACE,{"disambiguationData":[TD([[makeQuery(id+"F0.imprint","IMPRINT",EDGE,{"disambiguationData":[TD([[subQ11,1.0]])],"derivedFrom":subQ6}),1.0]])]});}
            var Q336;
            {var subQ3=sQuery(id+"F0.wireOp",EDGE,"E2.19.0.3");var subQ8=sQuery(id+"F0.wireOp",EDGE,"E2.19.0.1");var subQ11=makeQuery(id+"F0.imprint","INTERSECT",VERTEX,{"derivedFrom":[subQ8,subQ3]});Q336=makeQuery(id+"F0.imprint","IMPRINT",FACE,{"disambiguationData":[TD([[makeQuery(id+"F0.imprint","IMPRINT",EDGE,{"disambiguationData":[TD([[subQ11,1.0]])],"derivedFrom":subQ8}),1.0]])]});}
            var Q337;
            {var subQ7=sQuery(id+"F0.wireOp",EDGE,"E3.0.3.88");var subQ9=sQuery(id+"F0.wireOp",EDGE,"E3.0.3.99");var subQ11=makeQuery(id+"F0.imprint","INTERSECT",VERTEX,{"derivedFrom":[subQ7,subQ9]});Q337=makeQuery(id+"F0.imprint","IMPRINT",FACE,{"disambiguationData":[TD([[makeQuery(id+"F0.imprint","IMPRINT",EDGE,{"disambiguationData":[TD([[subQ11,-1.0]])],"derivedFrom":subQ7}),-1.0]])]});}
            var Q338;
            {var subQ5=sQuery(id+"F0.wireOp",EDGE,"E3.0.3.217");var subQ6=sQuery(id+"F0.wireOp",EDGE,"E3.0.3.82");var subQ7=makeQuery(id+"F0.imprint","INTERSECT",VERTEX,{"derivedFrom":[subQ6,subQ5]});Q338=makeQuery(id+"F0.imprint","IMPRINT",FACE,{"disambiguationData":[TD([[makeQuery(id+"F0.imprint","IMPRINT",EDGE,{"disambiguationData":[TD([[subQ7,1.0]])],"derivedFrom":subQ6}),1.0]])]});}
            var Q339;
            {var subQ3=sQuery(id+"F0.wireOp",EDGE,"E3.0.3.164");var subQ5=sQuery(id+"F0.wireOp",EDGE,"E3.0.3.208");var subQ6=makeQuery(id+"F0.imprint","INTERSECT",VERTEX,{"derivedFrom":[subQ3,subQ5]});Q339=makeQuery(id+"F0.imprint","IMPRINT",FACE,{"disambiguationData":[TD([[makeQuery(id+"F0.imprint","IMPRINT",EDGE,{"disambiguationData":[TD([[subQ6,1.0]])],"derivedFrom":subQ3}),1.0]])]});}
            var Q340;
            {var subQ0=sQuery(id+"F0.wireOp",EDGE,"E3.0.4.102");var subQ1=sQuery(id+"F0.wireOp",EDGE,"E3.0.4.81");var subQ2=makeQuery(id+"F0.imprint","INTERSECT",VERTEX,{"derivedFrom":[subQ1,subQ0]});Q340=makeQuery(id+"F0.imprint","IMPRINT",FACE,{"disambiguationData":[TD([[makeQuery(id+"F0.imprint","IMPRINT",EDGE,{"disambiguationData":[TD([[subQ2,1.0]])],"derivedFrom":subQ1}),-1.0]])]});}
            var Q341;
            {var subQ3=sQuery(id+"F0.wireOp",EDGE,"E2.15.0.5");var subQ5=sQuery(id+"F0.wireOp",EDGE,"E2.15.0.7");var subQ6=makeQuery(id+"F0.imprint","INTERSECT",VERTEX,{"derivedFrom":[subQ3,subQ5]});Q341=makeQuery(id+"F0.imprint","IMPRINT",FACE,{"disambiguationData":[TD([[makeQuery(id+"F0.imprint","IMPRINT",EDGE,{"disambiguationData":[TD([[subQ6,1.0]])],"derivedFrom":subQ3}),1.0]])]});}
            var Q342;
            {var subQ3=sQuery(id+"F0.wireOp",EDGE,"E2.3.0.5");var subQ9=sQuery(id+"F0.wireOp",EDGE,"E2.3.0.7");var subQ10=makeQuery(id+"F0.imprint","INTERSECT",VERTEX,{"derivedFrom":[subQ3,subQ9]});Q342=makeQuery(id+"F0.imprint","IMPRINT",FACE,{"disambiguationData":[TD([[makeQuery(id+"F0.imprint","IMPRINT",EDGE,{"disambiguationData":[TD([[subQ10,1.0]])],"derivedFrom":subQ3}),1.0]])]});}
            var Q343;
            {var subQ3=sQuery(id+"F0.wireOp",EDGE,"E3.0.1.230");var subQ5=sQuery(id+"F0.wireOp",EDGE,"E3.0.1.244");var subQ6=makeQuery(id+"F0.imprint","INTERSECT",VERTEX,{"derivedFrom":[subQ3,subQ5]});Q343=makeQuery(id+"F0.imprint","IMPRINT",FACE,{"disambiguationData":[TD([[makeQuery(id+"F0.imprint","IMPRINT",EDGE,{"disambiguationData":[TD([[subQ6,1.0]])],"derivedFrom":subQ3}),1.0]])]});}
            var Q344;
            {var subQ1=sQuery(id+"F0.wireOp",EDGE,"E3.0.3.149");var subQ7=sQuery(id+"F0.wireOp",EDGE,"E3.0.3.159");var subQ8=makeQuery(id+"F0.imprint","INTERSECT",VERTEX,{"derivedFrom":[subQ1,subQ7]});Q344=makeQuery(id+"F0.imprint","IMPRINT",FACE,{"disambiguationData":[TD([[makeQuery(id+"F0.imprint","IMPRINT",EDGE,{"disambiguationData":[TD([[subQ8,1.0]])],"derivedFrom":subQ1}),1.0]])]});}
            var Q345;
            {var subQ0=sQuery(id+"F0.wireOp",EDGE,"E3.0.4.225");var subQ1=sQuery(id+"F0.wireOp",EDGE,"E3.0.4.132");var subQ2=makeQuery(id+"F0.imprint","INTERSECT",VERTEX,{"derivedFrom":[subQ1,subQ0]});Q345=makeQuery(id+"F0.imprint","IMPRINT",FACE,{"disambiguationData":[TD([[makeQuery(id+"F0.imprint","IMPRINT",EDGE,{"disambiguationData":[TD([[subQ2,1.0]])],"derivedFrom":subQ1}),1.0]])]});}
            var Q346;
            {var subQ3=sQuery(id+"F0.wireOp",EDGE,"E3.0.4.215");Q346=makeQuery(id+"F0.imprint","IMPRINT",FACE,{"disambiguationData":[TD([[makeQuery(id+"F0.imprint","IMPRINT",EDGE,{"derivedFrom":subQ3}),1.0]])]});}
            var Q347;
            {var subQ3=sQuery(id+"F0.wireOp",EDGE,"E3.0.4.123");Q347=makeQuery(id+"F0.imprint","IMPRINT",FACE,{"disambiguationData":[TD([[makeQuery(id+"F0.imprint","IMPRINT",EDGE,{"derivedFrom":subQ3}),1.0]])]});}
            var Q348;
            {var subQ0=sQuery(id+"F0.wireOp",EDGE,"E2.27.0.7");var subQ1=sQuery(id+"F0.wireOp",EDGE,"E2.27.0.5");var subQ2=makeQuery(id+"F0.imprint","INTERSECT",VERTEX,{"derivedFrom":[subQ1,subQ0]});Q348=makeQuery(id+"F0.imprint","IMPRINT",FACE,{"disambiguationData":[TD([[makeQuery(id+"F0.imprint","IMPRINT",EDGE,{"disambiguationData":[TD([[subQ2,1.0]])],"derivedFrom":subQ1}),-1.0]])]});}
            var Q349;
            {var subQ0=sQuery(id+"F0.wireOp",EDGE,"E3.0.1.214");var subQ1=sQuery(id+"F0.wireOp",EDGE,"E3.0.1.88");var subQ2=makeQuery(id+"F0.imprint","INTERSECT",VERTEX,{"derivedFrom":[subQ1,subQ0]});Q349=makeQuery(id+"F0.imprint","IMPRINT",FACE,{"disambiguationData":[TD([[makeQuery(id+"F0.imprint","IMPRINT",EDGE,{"disambiguationData":[TD([[subQ2,1.0]])],"derivedFrom":subQ1}),-1.0]])]});}
            var Q350;
            {var subQ0=sQuery(id+"F0.wireOp",EDGE,"E3.0.2.180");var subQ1=sQuery(id+"F0.wireOp",EDGE,"E3.0.2.69");var subQ2=makeQuery(id+"F0.imprint","INTERSECT",VERTEX,{"derivedFrom":[subQ1,subQ0]});Q350=makeQuery(id+"F0.imprint","IMPRINT",FACE,{"disambiguationData":[TD([[makeQuery(id+"F0.imprint","IMPRINT",EDGE,{"disambiguationData":[TD([[subQ2,1.0]])],"derivedFrom":subQ1}),1.0]])]});}
            var Q351;
            {var subQ0=sQuery(id+"F0.wireOp",EDGE,"E3.0.1.237");var subQ1=sQuery(id+"F0.wireOp",EDGE,"E3.0.1.181");var subQ2=makeQuery(id+"F0.imprint","INTERSECT",VERTEX,{"derivedFrom":[subQ1,subQ0]});Q351=makeQuery(id+"F0.imprint","IMPRINT",FACE,{"disambiguationData":[TD([[makeQuery(id+"F0.imprint","IMPRINT",EDGE,{"disambiguationData":[TD([[subQ2,1.0]])],"derivedFrom":subQ1}),-1.0]])]});}
            var Q352;
            {var subQ1=sQuery(id+"F0.wireOp",EDGE,"E3.0.2.145");var subQ9=sQuery(id+"F0.wireOp",EDGE,"E3.0.2.155");var subQ11=makeQuery(id+"F0.imprint","INTERSECT",VERTEX,{"derivedFrom":[subQ1,subQ9]});Q352=makeQuery(id+"F0.imprint","IMPRINT",FACE,{"disambiguationData":[TD([[makeQuery(id+"F0.imprint","IMPRINT",EDGE,{"disambiguationData":[TD([[subQ11,1.0]])],"derivedFrom":subQ1}),1.0]])]});}
            var Q353;
            {var subQ0=sQuery(id+"F0.wireOp",EDGE,"E3.0.2.126");var subQ1=sQuery(id+"F0.wireOp",EDGE,"E3.0.2.85");var subQ2=makeQuery(id+"F0.imprint","INTERSECT",VERTEX,{"derivedFrom":[subQ1,subQ0]});Q353=makeQuery(id+"F0.imprint","IMPRINT",FACE,{"disambiguationData":[TD([[makeQuery(id+"F0.imprint","IMPRINT",EDGE,{"disambiguationData":[TD([[subQ2,1.0]])],"derivedFrom":subQ1}),-1.0]])]});}
            var Q354;
            {var subQ1=sQuery(id+"F0.wireOp",EDGE,"E3.0.3.214");var subQ7=sQuery(id+"F0.wireOp",EDGE,"E3.0.3.88");var subQ8=makeQuery(id+"F0.imprint","INTERSECT",VERTEX,{"derivedFrom":[subQ7,subQ1]});Q354=makeQuery(id+"F0.imprint","IMPRINT",FACE,{"disambiguationData":[TD([[makeQuery(id+"F0.imprint","IMPRINT",EDGE,{"disambiguationData":[TD([[subQ8,1.0]])],"derivedFrom":subQ7}),1.0]])]});}
            var Q355;
            {var subQ0=sQuery(id+"F0.wireOp",EDGE,"E3.0.4.226");var subQ1=sQuery(id+"F0.wireOp",EDGE,"E3.0.4.133");var subQ2=makeQuery(id+"F0.imprint","INTERSECT",VERTEX,{"derivedFrom":[subQ1,subQ0]});Q355=makeQuery(id+"F0.imprint","IMPRINT",FACE,{"disambiguationData":[TD([[makeQuery(id+"F0.imprint","IMPRINT",EDGE,{"disambiguationData":[TD([[subQ2,1.0]])],"derivedFrom":subQ1}),1.0]])]});}
            var Q356;
            {var subQ0=sQuery(id+"F0.wireOp",EDGE,"E3.0.2.10");var subQ1=sQuery(id+"F0.wireOp",EDGE,"E3.0.2.9");var subQ2=makeQuery(id+"F0.imprint","INTERSECT",VERTEX,{"derivedFrom":[subQ1,subQ0]});Q356=makeQuery(id+"F0.imprint","IMPRINT",FACE,{"disambiguationData":[TD([[makeQuery(id+"F0.imprint","IMPRINT",EDGE,{"disambiguationData":[TD([[subQ2,1.0]])],"derivedFrom":subQ1}),-1.0]])]});}
            var Q357;
            {var subQ3=sQuery(id+"F0.wireOp",EDGE,"E3.0.1.165");var subQ5=sQuery(id+"F0.wireOp",EDGE,"E3.0.1.207");var subQ6=makeQuery(id+"F0.imprint","INTERSECT",VERTEX,{"derivedFrom":[subQ3,subQ5]});Q357=makeQuery(id+"F0.imprint","IMPRINT",FACE,{"disambiguationData":[TD([[makeQuery(id+"F0.imprint","IMPRINT",EDGE,{"disambiguationData":[TD([[subQ6,1.0]])],"derivedFrom":subQ3}),1.0]])]});}
            var Q358;
            {var subQ0=sQuery(id+"F0.wireOp",EDGE,"E3.0.1.212");var subQ1=sQuery(id+"F0.wireOp",EDGE,"E3.0.1.166");var subQ2=makeQuery(id+"F0.imprint","INTERSECT",VERTEX,{"derivedFrom":[subQ1,subQ0]});Q358=makeQuery(id+"F0.imprint","IMPRINT",FACE,{"disambiguationData":[TD([[makeQuery(id+"F0.imprint","IMPRINT",EDGE,{"disambiguationData":[TD([[subQ2,1.0]])],"derivedFrom":subQ1}),-1.0]])]});}
            var Q359;
            {var subQ0=sQuery(id+"F0.wireOp",EDGE,"E3.0.2.129");var subQ1=sQuery(id+"F0.wireOp",EDGE,"E3.0.2.81");var subQ2=makeQuery(id+"F0.imprint","INTERSECT",VERTEX,{"derivedFrom":[subQ1,subQ0]});Q359=makeQuery(id+"F0.imprint","IMPRINT",FACE,{"disambiguationData":[TD([[makeQuery(id+"F0.imprint","IMPRINT",EDGE,{"disambiguationData":[TD([[subQ2,1.0]])],"derivedFrom":subQ1}),-1.0]])]});}
            var Q360;
            {var subQ0=sQuery(id+"F0.wireOp",EDGE,"E3.0.2.61");var subQ1=sQuery(id+"F0.wireOp",EDGE,"E3.0.2.7");var subQ2=makeQuery(id+"F0.imprint","INTERSECT",VERTEX,{"derivedFrom":[subQ1,subQ0]});Q360=makeQuery(id+"F0.imprint","IMPRINT",FACE,{"disambiguationData":[TD([[makeQuery(id+"F0.imprint","IMPRINT",EDGE,{"disambiguationData":[TD([[subQ2,1.0]])],"derivedFrom":subQ1}),1.0]])]});}
            var Q361;
            {var subQ0=sQuery(id+"F0.wireOp",EDGE,"E3.0.2.246");var subQ1=sQuery(id+"F0.wireOp",EDGE,"E3.0.2.228");var subQ2=makeQuery(id+"F0.imprint","INTERSECT",VERTEX,{"derivedFrom":[subQ1,subQ0]});Q361=makeQuery(id+"F0.imprint","IMPRINT",FACE,{"disambiguationData":[TD([[makeQuery(id+"F0.imprint","IMPRINT",EDGE,{"disambiguationData":[TD([[subQ2,1.0]])],"derivedFrom":subQ1}),-1.0]])]});}
            var Q362;
            {var subQ0=sQuery(id+"F0.wireOp",EDGE,"E3.0.2.211");var subQ1=sQuery(id+"F0.wireOp",EDGE,"E3.0.2.162");var subQ2=makeQuery(id+"F0.imprint","INTERSECT",VERTEX,{"derivedFrom":[subQ1,subQ0]});Q362=makeQuery(id+"F0.imprint","IMPRINT",FACE,{"disambiguationData":[TD([[makeQuery(id+"F0.imprint","IMPRINT",EDGE,{"disambiguationData":[TD([[subQ2,1.0]])],"derivedFrom":subQ1}),-1.0]])]});}
            var Q363;
            {var subQ0=sQuery(id+"F0.wireOp",EDGE,"E3.0.3.127");var subQ1=sQuery(id+"F0.wireOp",EDGE,"E3.0.3.84");var subQ2=makeQuery(id+"F0.imprint","INTERSECT",VERTEX,{"derivedFrom":[subQ1,subQ0]});Q363=makeQuery(id+"F0.imprint","IMPRINT",FACE,{"disambiguationData":[TD([[makeQuery(id+"F0.imprint","IMPRINT",EDGE,{"disambiguationData":[TD([[subQ2,1.0]])],"derivedFrom":subQ1}),-1.0]])]});}
            var Q364;
            {var subQ0=sQuery(id+"F0.wireOp",EDGE,"E3.0.3.212");var subQ1=sQuery(id+"F0.wireOp",EDGE,"E3.0.3.166");var subQ2=makeQuery(id+"F0.imprint","INTERSECT",VERTEX,{"derivedFrom":[subQ1,subQ0]});Q364=makeQuery(id+"F0.imprint","IMPRINT",FACE,{"disambiguationData":[TD([[makeQuery(id+"F0.imprint","IMPRINT",EDGE,{"disambiguationData":[TD([[subQ2,1.0]])],"derivedFrom":subQ1}),-1.0]])]});}
            var Q365;
            {var subQ0=sQuery(id+"F0.wireOp",EDGE,"E3.0.2.124");var subQ1=sQuery(id+"F0.wireOp",EDGE,"E3.0.2.86");var subQ2=makeQuery(id+"F0.imprint","INTERSECT",VERTEX,{"derivedFrom":[subQ1,subQ0]});Q365=makeQuery(id+"F0.imprint","IMPRINT",FACE,{"disambiguationData":[TD([[makeQuery(id+"F0.imprint","IMPRINT",EDGE,{"disambiguationData":[TD([[subQ2,1.0]])],"derivedFrom":subQ1}),-1.0]])]});}
            var Q366;
            {var subQ0=sQuery(id+"F0.wireOp",EDGE,"E3.0.1.218");var subQ1=sQuery(id+"F0.wireOp",EDGE,"E3.0.1.185");var subQ2=makeQuery(id+"F0.imprint","INTERSECT",VERTEX,{"derivedFrom":[subQ1,subQ0]});Q366=makeQuery(id+"F0.imprint","IMPRINT",FACE,{"disambiguationData":[TD([[makeQuery(id+"F0.imprint","IMPRINT",EDGE,{"disambiguationData":[TD([[subQ2,1.0]])],"derivedFrom":subQ1}),-1.0]])]});}
            var Q367;
            {var subQ0=sQuery(id+"F0.wireOp",EDGE,"E3.0.2.209");var subQ1=sQuery(id+"F0.wireOp",EDGE,"E3.0.2.169");var subQ2=makeQuery(id+"F0.imprint","INTERSECT",VERTEX,{"derivedFrom":[subQ1,subQ0]});Q367=makeQuery(id+"F0.imprint","IMPRINT",FACE,{"disambiguationData":[TD([[makeQuery(id+"F0.imprint","IMPRINT",EDGE,{"disambiguationData":[TD([[subQ2,1.0]])],"derivedFrom":subQ1}),-1.0]])]});}
            var Q368;
            {var subQ0=sQuery(id+"F0.wireOp",EDGE,"E3.0.2.97");var subQ1=sQuery(id+"F0.wireOp",EDGE,"E3.0.2.86");var subQ2=makeQuery(id+"F0.imprint","INTERSECT",VERTEX,{"derivedFrom":[subQ1,subQ0]});Q368=makeQuery(id+"F0.imprint","IMPRINT",FACE,{"disambiguationData":[TD([[makeQuery(id+"F0.imprint","IMPRINT",EDGE,{"disambiguationData":[TD([[subQ2,1.0]])],"derivedFrom":subQ1}),-1.0]])]});}
            var Q369;
            {var subQ0=sQuery(id+"F0.wireOp",EDGE,"E3.0.2.198");var subQ1=sQuery(id+"F0.wireOp",EDGE,"E3.0.2.186");var subQ2=makeQuery(id+"F0.imprint","INTERSECT",VERTEX,{"derivedFrom":[subQ1,subQ0]});Q369=makeQuery(id+"F0.imprint","IMPRINT",FACE,{"disambiguationData":[TD([[makeQuery(id+"F0.imprint","IMPRINT",EDGE,{"disambiguationData":[TD([[subQ2,1.0]])],"derivedFrom":subQ1}),-1.0]])]});}
            var Q370;
            {var subQ0=sQuery(id+"F0.wireOp",EDGE,"E3.0.4.153");var subQ1=sQuery(id+"F0.wireOp",EDGE,"E3.0.4.134");var subQ2=makeQuery(id+"F0.imprint","INTERSECT",VERTEX,{"derivedFrom":[subQ1,subQ0]});Q370=makeQuery(id+"F0.imprint","IMPRINT",FACE,{"disambiguationData":[TD([[makeQuery(id+"F0.imprint","IMPRINT",EDGE,{"disambiguationData":[TD([[subQ2,1.0]])],"derivedFrom":subQ1}),1.0]])]});}
            var Q371;
            {var subQ0=sQuery(id+"F0.wireOp",EDGE,"E3.0.3.218");var subQ1=sQuery(id+"F0.wireOp",EDGE,"E3.0.3.185");var subQ2=makeQuery(id+"F0.imprint","INTERSECT",VERTEX,{"derivedFrom":[subQ1,subQ0]});Q371=makeQuery(id+"F0.imprint","IMPRINT",FACE,{"disambiguationData":[TD([[makeQuery(id+"F0.imprint","IMPRINT",EDGE,{"disambiguationData":[TD([[subQ2,1.0]])],"derivedFrom":subQ1}),-1.0]])]});}
            var Q372;
            {var subQ0=sQuery(id+"F0.wireOp",EDGE,"E3.0.3.207");var subQ1=sQuery(id+"F0.wireOp",EDGE,"E3.0.3.165");var subQ2=makeQuery(id+"F0.imprint","INTERSECT",VERTEX,{"derivedFrom":[subQ1,subQ0]});Q372=makeQuery(id+"F0.imprint","IMPRINT",FACE,{"disambiguationData":[TD([[makeQuery(id+"F0.imprint","IMPRINT",EDGE,{"disambiguationData":[TD([[subQ2,1.0]])],"derivedFrom":subQ1}),-1.0]])]});}
            var Q373;
            {var subQ0=sQuery(id+"F0.wireOp",EDGE,"E2.12.0.7");var subQ1=sQuery(id+"F0.wireOp",EDGE,"E2.12.0.5");var subQ2=makeQuery(id+"F0.imprint","INTERSECT",VERTEX,{"derivedFrom":[subQ1,subQ0]});Q373=makeQuery(id+"F0.imprint","IMPRINT",FACE,{"disambiguationData":[TD([[makeQuery(id+"F0.imprint","IMPRINT",EDGE,{"disambiguationData":[TD([[subQ2,1.0]])],"derivedFrom":subQ1}),-1.0]])]});}
            var Q374;
            {var subQ0=sQuery(id+"F0.wireOp",EDGE,"E2.24.0.7");var subQ1=sQuery(id+"F0.wireOp",EDGE,"E2.24.0.5");var subQ2=makeQuery(id+"F0.imprint","INTERSECT",VERTEX,{"derivedFrom":[subQ1,subQ0]});Q374=makeQuery(id+"F0.imprint","IMPRINT",FACE,{"disambiguationData":[TD([[makeQuery(id+"F0.imprint","IMPRINT",EDGE,{"disambiguationData":[TD([[subQ2,1.0]])],"derivedFrom":subQ1}),-1.0]])]});}
            var Q375;
            {var subQ0=sQuery(id+"F0.wireOp",EDGE,"E3.0.1.226");var subQ1=sQuery(id+"F0.wireOp",EDGE,"E3.0.1.133");var subQ2=makeQuery(id+"F0.imprint","INTERSECT",VERTEX,{"derivedFrom":[subQ1,subQ0]});Q375=makeQuery(id+"F0.imprint","IMPRINT",FACE,{"disambiguationData":[TD([[makeQuery(id+"F0.imprint","IMPRINT",EDGE,{"disambiguationData":[TD([[subQ2,1.0]])],"derivedFrom":subQ1}),1.0]])]});}
            var Q376;
            {var subQ0=sQuery(id+"F0.wireOp",EDGE,"E3.0.1.123");var subQ1=sQuery(id+"F0.wireOp",EDGE,"E3.0.1.89");var subQ2=makeQuery(id+"F0.imprint","INTERSECT",VERTEX,{"derivedFrom":[subQ1,subQ0]});Q376=makeQuery(id+"F0.imprint","IMPRINT",FACE,{"disambiguationData":[TD([[makeQuery(id+"F0.imprint","IMPRINT",EDGE,{"disambiguationData":[TD([[subQ2,1.0]])],"derivedFrom":subQ1}),-1.0]])]});}
            var Q377;
            {var subQ0=sQuery(id+"F0.wireOp",EDGE,"E3.0.2.156");var subQ1=sQuery(id+"F0.wireOp",EDGE,"E3.0.2.136");var subQ2=makeQuery(id+"F0.imprint","INTERSECT",VERTEX,{"derivedFrom":[subQ1,subQ0]});Q377=makeQuery(id+"F0.imprint","IMPRINT",FACE,{"disambiguationData":[TD([[makeQuery(id+"F0.imprint","IMPRINT",EDGE,{"disambiguationData":[TD([[subQ2,1.0]])],"derivedFrom":subQ1}),1.0]])]});}
            var Q378;
            {var subQ0=sQuery(id+"F0.wireOp",EDGE,"E3.0.2.98");var subQ1=sQuery(id+"F0.wireOp",EDGE,"E3.0.2.87");var subQ2=makeQuery(id+"F0.imprint","INTERSECT",VERTEX,{"derivedFrom":[subQ1,subQ0]});Q378=makeQuery(id+"F0.imprint","IMPRINT",FACE,{"disambiguationData":[TD([[makeQuery(id+"F0.imprint","IMPRINT",EDGE,{"disambiguationData":[TD([[subQ2,1.0]])],"derivedFrom":subQ1}),-1.0]])]});}
            var Q379;
            {var subQ0=sQuery(id+"F0.wireOp",EDGE,"E3.0.3.123");var subQ1=sQuery(id+"F0.wireOp",EDGE,"E3.0.3.89");var subQ2=makeQuery(id+"F0.imprint","INTERSECT",VERTEX,{"derivedFrom":[subQ1,subQ0]});Q379=makeQuery(id+"F0.imprint","IMPRINT",FACE,{"disambiguationData":[TD([[makeQuery(id+"F0.imprint","IMPRINT",EDGE,{"disambiguationData":[TD([[subQ2,1.0]])],"derivedFrom":subQ1}),-1.0]])]});}
            var Q380;
            {var subQ0=sQuery(id+"F0.wireOp",EDGE,"E3.0.4.156");var subQ1=sQuery(id+"F0.wireOp",EDGE,"E3.0.4.136");var subQ2=makeQuery(id+"F0.imprint","INTERSECT",VERTEX,{"derivedFrom":[subQ1,subQ0]});Q380=makeQuery(id+"F0.imprint","IMPRINT",FACE,{"disambiguationData":[TD([[makeQuery(id+"F0.imprint","IMPRINT",EDGE,{"disambiguationData":[TD([[subQ2,1.0]])],"derivedFrom":subQ1}),1.0]])]});}
            var Q381;
            {var subQ0=sQuery(id+"F0.wireOp",EDGE,"E3.0.4.103");var subQ1=sQuery(id+"F0.wireOp",EDGE,"E3.0.4.82");var subQ2=makeQuery(id+"F0.imprint","INTERSECT",VERTEX,{"derivedFrom":[subQ1,subQ0]});Q381=makeQuery(id+"F0.imprint","IMPRINT",FACE,{"disambiguationData":[TD([[makeQuery(id+"F0.imprint","IMPRINT",EDGE,{"disambiguationData":[TD([[subQ2,1.0]])],"derivedFrom":subQ1}),-1.0]])]});}
            var Q382;
            {var subQ0=sQuery(id+"F0.wireOp",EDGE,"E3.0.3.215");var subQ1=sQuery(id+"F0.wireOp",EDGE,"E3.0.3.186");var subQ2=makeQuery(id+"F0.imprint","INTERSECT",VERTEX,{"derivedFrom":[subQ1,subQ0]});Q382=makeQuery(id+"F0.imprint","IMPRINT",FACE,{"disambiguationData":[TD([[makeQuery(id+"F0.imprint","IMPRINT",EDGE,{"disambiguationData":[TD([[subQ2,1.0]])],"derivedFrom":subQ1}),-1.0]])]});}
            var Q383;
            {var subQ0=sQuery(id+"F0.wireOp",EDGE,"E3.0.1.222");var subQ1=sQuery(id+"F0.wireOp",EDGE,"E3.0.1.152");var subQ2=makeQuery(id+"F0.imprint","INTERSECT",VERTEX,{"derivedFrom":[subQ1,subQ0]});Q383=makeQuery(id+"F0.imprint","IMPRINT",FACE,{"disambiguationData":[TD([[makeQuery(id+"F0.imprint","IMPRINT",EDGE,{"disambiguationData":[TD([[subQ2,1.0]])],"derivedFrom":subQ1}),1.0]])]});}
            var Q384;
            {var subQ0=sQuery(id+"F0.wireOp",EDGE,"E3.0.2.216");var subQ1=sQuery(id+"F0.wireOp",EDGE,"E3.0.2.87");var subQ2=makeQuery(id+"F0.imprint","INTERSECT",VERTEX,{"derivedFrom":[subQ1,subQ0]});Q384=makeQuery(id+"F0.imprint","IMPRINT",FACE,{"disambiguationData":[TD([[makeQuery(id+"F0.imprint","IMPRINT",EDGE,{"disambiguationData":[TD([[subQ2,1.0]])],"derivedFrom":subQ1}),-1.0]])]});}
            var Q385;
            {var subQ0=sQuery(id+"F0.wireOp",EDGE,"E3.0.1.215");var subQ1=sQuery(id+"F0.wireOp",EDGE,"E3.0.1.186");var subQ2=makeQuery(id+"F0.imprint","INTERSECT",VERTEX,{"derivedFrom":[subQ1,subQ0]});Q385=makeQuery(id+"F0.imprint","IMPRINT",FACE,{"disambiguationData":[TD([[makeQuery(id+"F0.imprint","IMPRINT",EDGE,{"disambiguationData":[TD([[subQ2,1.0]])],"derivedFrom":subQ1}),-1.0]])]});}
            var Q386;
            {var subQ0=sQuery(id+"F0.wireOp",EDGE,"E3.0.2.158");var subQ1=sQuery(id+"F0.wireOp",EDGE,"E3.0.2.138");var subQ2=makeQuery(id+"F0.imprint","INTERSECT",VERTEX,{"derivedFrom":[subQ1,subQ0]});Q386=makeQuery(id+"F0.imprint","IMPRINT",FACE,{"disambiguationData":[TD([[makeQuery(id+"F0.imprint","IMPRINT",EDGE,{"disambiguationData":[TD([[subQ2,1.0]])],"derivedFrom":subQ1}),1.0]])]});}
            var Q387;
            {var subQ0=sQuery(id+"F0.wireOp",EDGE,"E3.0.2.100");var subQ1=sQuery(id+"F0.wireOp",EDGE,"E3.0.2.89");var subQ2=makeQuery(id+"F0.imprint","INTERSECT",VERTEX,{"derivedFrom":[subQ1,subQ0]});Q387=makeQuery(id+"F0.imprint","IMPRINT",FACE,{"disambiguationData":[TD([[makeQuery(id+"F0.imprint","IMPRINT",EDGE,{"disambiguationData":[TD([[subQ2,1.0]])],"derivedFrom":subQ1}),-1.0]])]});}
            var Q388;
            {var subQ0=sQuery(id+"F0.wireOp",EDGE,"E3.0.3.125");var subQ1=sQuery(id+"F0.wireOp",EDGE,"E3.0.3.26");var subQ2=makeQuery(id+"F0.imprint","INTERSECT",VERTEX,{"derivedFrom":[subQ1,subQ0]});Q388=makeQuery(id+"F0.imprint","IMPRINT",FACE,{"disambiguationData":[TD([[makeQuery(id+"F0.imprint","IMPRINT",EDGE,{"disambiguationData":[TD([[subQ2,1.0]])],"derivedFrom":subQ1}),-1.0]])]});}
            var Q389;
            {var subQ0=sQuery(id+"F0.wireOp",EDGE,"E3.0.3.222");var subQ1=sQuery(id+"F0.wireOp",EDGE,"E3.0.3.152");var subQ2=makeQuery(id+"F0.imprint","INTERSECT",VERTEX,{"derivedFrom":[subQ1,subQ0]});Q389=makeQuery(id+"F0.imprint","IMPRINT",FACE,{"disambiguationData":[TD([[makeQuery(id+"F0.imprint","IMPRINT",EDGE,{"disambiguationData":[TD([[subQ2,1.0]])],"derivedFrom":subQ1}),1.0]])]});}
            var Q390;
            {var subQ0=sQuery(id+"F0.wireOp",EDGE,"E3.0.1.205");var subQ1=sQuery(id+"F0.wireOp",EDGE,"E3.0.1.167");var subQ2=makeQuery(id+"F0.imprint","INTERSECT",VERTEX,{"derivedFrom":[subQ1,subQ0]});Q390=makeQuery(id+"F0.imprint","IMPRINT",FACE,{"disambiguationData":[TD([[makeQuery(id+"F0.imprint","IMPRINT",EDGE,{"disambiguationData":[TD([[subQ2,1.0]])],"derivedFrom":subQ1}),-1.0]])]});}
            var Q391;
            {var subQ0=sQuery(id+"F0.wireOp",EDGE,"E3.0.2.210");var subQ1=sQuery(id+"F0.wireOp",EDGE,"E3.0.2.163");var subQ2=makeQuery(id+"F0.imprint","INTERSECT",VERTEX,{"derivedFrom":[subQ1,subQ0]});Q391=makeQuery(id+"F0.imprint","IMPRINT",FACE,{"disambiguationData":[TD([[makeQuery(id+"F0.imprint","IMPRINT",EDGE,{"disambiguationData":[TD([[subQ2,1.0]])],"derivedFrom":subQ1}),-1.0]])]});}
            var Q392;
            {var subQ0=sQuery(id+"F0.wireOp",EDGE,"E3.0.2.245");var subQ1=sQuery(id+"F0.wireOp",EDGE,"E3.0.2.229");var subQ2=makeQuery(id+"F0.imprint","INTERSECT",VERTEX,{"derivedFrom":[subQ1,subQ0]});Q392=makeQuery(id+"F0.imprint","IMPRINT",FACE,{"disambiguationData":[TD([[makeQuery(id+"F0.imprint","IMPRINT",EDGE,{"disambiguationData":[TD([[subQ2,1.0]])],"derivedFrom":subQ1}),-1.0]])]});}
            var Q393;
            {var subQ0=sQuery(id+"F0.wireOp",EDGE,"E3.0.3.205");var subQ1=sQuery(id+"F0.wireOp",EDGE,"E3.0.3.167");var subQ2=makeQuery(id+"F0.imprint","INTERSECT",VERTEX,{"derivedFrom":[subQ1,subQ0]});Q393=makeQuery(id+"F0.imprint","IMPRINT",FACE,{"disambiguationData":[TD([[makeQuery(id+"F0.imprint","IMPRINT",EDGE,{"disambiguationData":[TD([[subQ2,1.0]])],"derivedFrom":subQ1}),-1.0]])]});}
            var Q394;
            {var subQ0=sQuery(id+"F0.wireOp",EDGE,"E3.0.2.159");var subQ1=sQuery(id+"F0.wireOp",EDGE,"E3.0.2.139");var subQ2=makeQuery(id+"F0.imprint","INTERSECT",VERTEX,{"derivedFrom":[subQ1,subQ0]});Q394=makeQuery(id+"F0.imprint","IMPRINT",FACE,{"disambiguationData":[TD([[makeQuery(id+"F0.imprint","IMPRINT",EDGE,{"disambiguationData":[TD([[subQ2,1.0]])],"derivedFrom":subQ1}),1.0]])]});}
            var Q395;
            {var subQ0=sQuery(id+"F0.wireOp",EDGE,"E3.0.3.213");var subQ1=sQuery(id+"F0.wireOp",EDGE,"E3.0.3.187");var subQ2=makeQuery(id+"F0.imprint","INTERSECT",VERTEX,{"derivedFrom":[subQ1,subQ0]});Q395=makeQuery(id+"F0.imprint","IMPRINT",FACE,{"disambiguationData":[TD([[makeQuery(id+"F0.imprint","IMPRINT",EDGE,{"disambiguationData":[TD([[subQ2,1.0]])],"derivedFrom":subQ1}),-1.0]])]});}
            var Q396;
            {var subQ0=sQuery(id+"F0.wireOp",EDGE,"E2.5.0.7");var subQ1=sQuery(id+"F0.wireOp",EDGE,"E2.5.0.5");var subQ2=makeQuery(id+"F0.imprint","INTERSECT",VERTEX,{"derivedFrom":[subQ1,subQ0]});Q396=makeQuery(id+"F0.imprint","IMPRINT",FACE,{"disambiguationData":[TD([[makeQuery(id+"F0.imprint","IMPRINT",EDGE,{"disambiguationData":[TD([[subQ2,1.0]])],"derivedFrom":subQ1}),-1.0]])]});}
            var Q397;
            {var subQ0=sQuery(id+"F0.wireOp",EDGE,"E2.21.0.7");var subQ1=sQuery(id+"F0.wireOp",EDGE,"E2.21.0.5");var subQ2=makeQuery(id+"F0.imprint","INTERSECT",VERTEX,{"derivedFrom":[subQ1,subQ0]});Q397=makeQuery(id+"F0.imprint","IMPRINT",FACE,{"disambiguationData":[TD([[makeQuery(id+"F0.imprint","IMPRINT",EDGE,{"disambiguationData":[TD([[subQ2,1.0]])],"derivedFrom":subQ1}),-1.0]])]});}
            var Q398;
            {var subQ0=sQuery(id+"F0.wireOp",EDGE,"E2.17.0.7");var subQ1=sQuery(id+"F0.wireOp",EDGE,"E2.17.0.5");var subQ2=makeQuery(id+"F0.imprint","INTERSECT",VERTEX,{"derivedFrom":[subQ1,subQ0]});Q398=makeQuery(id+"F0.imprint","IMPRINT",FACE,{"disambiguationData":[TD([[makeQuery(id+"F0.imprint","IMPRINT",EDGE,{"disambiguationData":[TD([[subQ2,1.0]])],"derivedFrom":subQ1}),-1.0]])]});}
            var Q399;
            {var subQ0=sQuery(id+"F0.wireOp",EDGE,"E2.13.0.7");var subQ1=sQuery(id+"F0.wireOp",EDGE,"E2.13.0.5");var subQ2=makeQuery(id+"F0.imprint","INTERSECT",VERTEX,{"derivedFrom":[subQ1,subQ0]});Q399=makeQuery(id+"F0.imprint","IMPRINT",FACE,{"disambiguationData":[TD([[makeQuery(id+"F0.imprint","IMPRINT",EDGE,{"disambiguationData":[TD([[subQ2,1.0]])],"derivedFrom":subQ1}),-1.0]])]});}
            var Q400;
            {var subQ0=sQuery(id+"F0.wireOp",EDGE,"E3.0.1.126");var subQ1=sQuery(id+"F0.wireOp",EDGE,"E3.0.1.85");var subQ2=makeQuery(id+"F0.imprint","INTERSECT",VERTEX,{"derivedFrom":[subQ1,subQ0]});Q400=makeQuery(id+"F0.imprint","IMPRINT",FACE,{"disambiguationData":[TD([[makeQuery(id+"F0.imprint","IMPRINT",EDGE,{"disambiguationData":[TD([[subQ2,1.0]])],"derivedFrom":subQ1}),-1.0]])]});}
            var Q401;
            {var subQ0=sQuery(id+"F0.wireOp",EDGE,"E3.0.1.180");var subQ1=sQuery(id+"F0.wireOp",EDGE,"E3.0.1.69");var subQ2=makeQuery(id+"F0.imprint","INTERSECT",VERTEX,{"derivedFrom":[subQ1,subQ0]});Q401=makeQuery(id+"F0.imprint","IMPRINT",FACE,{"disambiguationData":[TD([[makeQuery(id+"F0.imprint","IMPRINT",EDGE,{"disambiguationData":[TD([[subQ2,1.0]])],"derivedFrom":subQ1}),1.0]])]});}
            var Q402;
            {var subQ0=sQuery(id+"F0.wireOp",EDGE,"E2.25.0.7");var subQ1=sQuery(id+"F0.wireOp",EDGE,"E2.25.0.5");var subQ2=makeQuery(id+"F0.imprint","INTERSECT",VERTEX,{"derivedFrom":[subQ1,subQ0]});Q402=makeQuery(id+"F0.imprint","IMPRINT",FACE,{"disambiguationData":[TD([[makeQuery(id+"F0.imprint","IMPRINT",EDGE,{"disambiguationData":[TD([[subQ2,1.0]])],"derivedFrom":subQ1}),-1.0]])]});}
            var Q403;
            {var subQ0=sQuery(id+"F0.wireOp",EDGE,"E3.0.1.204");var subQ1=sQuery(id+"F0.wireOp",EDGE,"E3.0.1.168");var subQ2=makeQuery(id+"F0.imprint","INTERSECT",VERTEX,{"derivedFrom":[subQ1,subQ0]});Q403=makeQuery(id+"F0.imprint","IMPRINT",FACE,{"disambiguationData":[TD([[makeQuery(id+"F0.imprint","IMPRINT",EDGE,{"disambiguationData":[TD([[subQ2,1.0]])],"derivedFrom":subQ1}),-1.0]])]});}
            var Q404;
            {var subQ0=sQuery(id+"F0.wireOp",EDGE,"E3.0.2.214");var subQ1=sQuery(id+"F0.wireOp",EDGE,"E3.0.2.88");var subQ2=makeQuery(id+"F0.imprint","INTERSECT",VERTEX,{"derivedFrom":[subQ1,subQ0]});Q404=makeQuery(id+"F0.imprint","IMPRINT",FACE,{"disambiguationData":[TD([[makeQuery(id+"F0.imprint","IMPRINT",EDGE,{"disambiguationData":[TD([[subQ2,1.0]])],"derivedFrom":subQ1}),-1.0]])]});}
            var Q405;
            {var subQ0=sQuery(id+"F0.wireOp",EDGE,"E3.0.2.239");var subQ1=sQuery(id+"F0.wireOp",EDGE,"E3.0.2.19");var subQ2=makeQuery(id+"F0.imprint","INTERSECT",VERTEX,{"derivedFrom":[subQ1,subQ0]});Q405=makeQuery(id+"F0.imprint","IMPRINT",FACE,{"disambiguationData":[TD([[makeQuery(id+"F0.imprint","IMPRINT",EDGE,{"disambiguationData":[TD([[subQ2,1.0]])],"derivedFrom":subQ1}),-1.0]])]});}
            var Q406;
            {var subQ0=sQuery(id+"F0.wireOp",EDGE,"E3.0.2.237");var subQ1=sQuery(id+"F0.wireOp",EDGE,"E3.0.2.181");var subQ2=makeQuery(id+"F0.imprint","INTERSECT",VERTEX,{"derivedFrom":[subQ1,subQ0]});Q406=makeQuery(id+"F0.imprint","IMPRINT",FACE,{"disambiguationData":[TD([[makeQuery(id+"F0.imprint","IMPRINT",EDGE,{"disambiguationData":[TD([[subQ2,1.0]])],"derivedFrom":subQ1}),-1.0]])]});}
            var Q407;
            {var subQ0=sQuery(id+"F0.wireOp",EDGE,"E3.0.2.102");var subQ1=sQuery(id+"F0.wireOp",EDGE,"E3.0.2.81");var subQ2=makeQuery(id+"F0.imprint","INTERSECT",VERTEX,{"derivedFrom":[subQ1,subQ0]});Q407=makeQuery(id+"F0.imprint","IMPRINT",FACE,{"disambiguationData":[TD([[makeQuery(id+"F0.imprint","IMPRINT",EDGE,{"disambiguationData":[TD([[subQ2,1.0]])],"derivedFrom":subQ1}),-1.0]])]});}
            var Q408;
            {var subQ0=sQuery(id+"F0.wireOp",EDGE,"E3.0.3.180");var subQ1=sQuery(id+"F0.wireOp",EDGE,"E3.0.3.69");var subQ2=makeQuery(id+"F0.imprint","INTERSECT",VERTEX,{"derivedFrom":[subQ1,subQ0]});Q408=makeQuery(id+"F0.imprint","IMPRINT",FACE,{"disambiguationData":[TD([[makeQuery(id+"F0.imprint","IMPRINT",EDGE,{"disambiguationData":[TD([[subQ2,1.0]])],"derivedFrom":subQ1}),1.0]])]});}
            var Q409;
            {var subQ0=sQuery(id+"F0.wireOp",EDGE,"E3.0.2.244");var subQ1=sQuery(id+"F0.wireOp",EDGE,"E3.0.2.230");var subQ2=makeQuery(id+"F0.imprint","INTERSECT",VERTEX,{"derivedFrom":[subQ1,subQ0]});Q409=makeQuery(id+"F0.imprint","IMPRINT",FACE,{"disambiguationData":[TD([[makeQuery(id+"F0.imprint","IMPRINT",EDGE,{"disambiguationData":[TD([[subQ2,1.0]])],"derivedFrom":subQ1}),-1.0]])]});}
            var Q410;
            {var subQ0=sQuery(id+"F0.wireOp",EDGE,"E3.0.3.126");var subQ1=sQuery(id+"F0.wireOp",EDGE,"E3.0.3.85");var subQ2=makeQuery(id+"F0.imprint","INTERSECT",VERTEX,{"derivedFrom":[subQ1,subQ0]});Q410=makeQuery(id+"F0.imprint","IMPRINT",FACE,{"disambiguationData":[TD([[makeQuery(id+"F0.imprint","IMPRINT",EDGE,{"disambiguationData":[TD([[subQ2,1.0]])],"derivedFrom":subQ1}),-1.0]])]});}
            var Q411;
            {var subQ0=sQuery(id+"F0.wireOp",EDGE,"E3.0.4.96");var subQ1=sQuery(id+"F0.wireOp",EDGE,"E3.0.4.26");var subQ2=makeQuery(id+"F0.imprint","INTERSECT",VERTEX,{"derivedFrom":[subQ1,subQ0]});Q411=makeQuery(id+"F0.imprint","IMPRINT",FACE,{"disambiguationData":[TD([[makeQuery(id+"F0.imprint","IMPRINT",EDGE,{"disambiguationData":[TD([[subQ2,1.0]])],"derivedFrom":subQ1}),-1.0]])]});}
            var Q412;
            {var subQ0=sQuery(id+"F0.wireOp",EDGE,"E3.0.3.204");var subQ1=sQuery(id+"F0.wireOp",EDGE,"E3.0.3.168");var subQ2=makeQuery(id+"F0.imprint","INTERSECT",VERTEX,{"derivedFrom":[subQ1,subQ0]});Q412=makeQuery(id+"F0.imprint","IMPRINT",FACE,{"disambiguationData":[TD([[makeQuery(id+"F0.imprint","IMPRINT",EDGE,{"disambiguationData":[TD([[subQ2,1.0]])],"derivedFrom":subQ1}),-1.0]])]});}
            var Q413;
            {var subQ0=sQuery(id+"F0.wireOp",EDGE,"E2.2.0.3");var subQ1=sQuery(id+"F0.wireOp",EDGE,"E2.2.0.0");var subQ2=makeQuery(id+"F0.imprint","INTERSECT",VERTEX,{"derivedFrom":[subQ1,subQ0]});Q413=makeQuery(id+"F0.imprint","IMPRINT",FACE,{"disambiguationData":[TD([[makeQuery(id+"F0.imprint","IMPRINT",EDGE,{"disambiguationData":[TD([[subQ2,1.0]])],"derivedFrom":subQ1}),1.0]])]});}
            var Q414;
            {var subQ0=sQuery(id+"F0.wireOp",EDGE,"E3.0.2.160");var subQ1=sQuery(id+"F0.wireOp",EDGE,"E3.0.2.141");var subQ2=makeQuery(id+"F0.imprint","INTERSECT",VERTEX,{"derivedFrom":[subQ1,subQ0]});Q414=makeQuery(id+"F0.imprint","IMPRINT",FACE,{"disambiguationData":[TD([[makeQuery(id+"F0.imprint","IMPRINT",EDGE,{"disambiguationData":[TD([[subQ2,1.0]])],"derivedFrom":subQ1}),1.0]])]});}
            var Q415;
            {var subQ0=sQuery(id+"F0.wireOp",EDGE,"E3.0.2.225");var subQ1=sQuery(id+"F0.wireOp",EDGE,"E3.0.2.132");var subQ2=makeQuery(id+"F0.imprint","INTERSECT",VERTEX,{"derivedFrom":[subQ1,subQ0]});Q415=makeQuery(id+"F0.imprint","IMPRINT",FACE,{"disambiguationData":[TD([[makeQuery(id+"F0.imprint","IMPRINT",EDGE,{"disambiguationData":[TD([[subQ2,1.0]])],"derivedFrom":subQ1}),1.0]])]});}
            var Q416;
            {var subQ0=sQuery(id+"F0.wireOp",EDGE,"E3.0.4.95");var subQ1=sQuery(id+"F0.wireOp",EDGE,"E3.0.4.84");var subQ2=makeQuery(id+"F0.imprint","INTERSECT",VERTEX,{"derivedFrom":[subQ1,subQ0]});Q416=makeQuery(id+"F0.imprint","IMPRINT",FACE,{"disambiguationData":[TD([[makeQuery(id+"F0.imprint","IMPRINT",EDGE,{"disambiguationData":[TD([[subQ2,1.0]])],"derivedFrom":subQ1}),-1.0]])]});}
            var Q417;
            {var subQ0=sQuery(id+"F0.wireOp",EDGE,"E3.0.1.124");var subQ1=sQuery(id+"F0.wireOp",EDGE,"E3.0.1.86");var subQ2=makeQuery(id+"F0.imprint","INTERSECT",VERTEX,{"derivedFrom":[subQ1,subQ0]});Q417=makeQuery(id+"F0.imprint","IMPRINT",FACE,{"disambiguationData":[TD([[makeQuery(id+"F0.imprint","IMPRINT",EDGE,{"disambiguationData":[TD([[subQ2,1.0]])],"derivedFrom":subQ1}),-1.0]])]});}
            var Q418;
            {var subQ0=sQuery(id+"F0.wireOp",EDGE,"E3.0.1.209");var subQ1=sQuery(id+"F0.wireOp",EDGE,"E3.0.1.169");var subQ2=makeQuery(id+"F0.imprint","INTERSECT",VERTEX,{"derivedFrom":[subQ1,subQ0]});Q418=makeQuery(id+"F0.imprint","IMPRINT",FACE,{"disambiguationData":[TD([[makeQuery(id+"F0.imprint","IMPRINT",EDGE,{"disambiguationData":[TD([[subQ2,1.0]])],"derivedFrom":subQ1}),-1.0]])]});}
            var Q419;
            {var subQ0=sQuery(id+"F0.wireOp",EDGE,"E3.0.2.218");var subQ1=sQuery(id+"F0.wireOp",EDGE,"E3.0.2.185");var subQ2=makeQuery(id+"F0.imprint","INTERSECT",VERTEX,{"derivedFrom":[subQ1,subQ0]});Q419=makeQuery(id+"F0.imprint","IMPRINT",FACE,{"disambiguationData":[TD([[makeQuery(id+"F0.imprint","IMPRINT",EDGE,{"disambiguationData":[TD([[subQ2,1.0]])],"derivedFrom":subQ1}),-1.0]])]});}
            var Q420;
            {var subQ0=sQuery(id+"F0.wireOp",EDGE,"E3.0.2.207");var subQ1=sQuery(id+"F0.wireOp",EDGE,"E3.0.2.165");var subQ2=makeQuery(id+"F0.imprint","INTERSECT",VERTEX,{"derivedFrom":[subQ1,subQ0]});Q420=makeQuery(id+"F0.imprint","IMPRINT",FACE,{"disambiguationData":[TD([[makeQuery(id+"F0.imprint","IMPRINT",EDGE,{"disambiguationData":[TD([[subQ2,1.0]])],"derivedFrom":subQ1}),-1.0]])]});}
            var Q421;
            {var subQ0=sQuery(id+"F0.wireOp",EDGE,"E3.0.3.124");var subQ1=sQuery(id+"F0.wireOp",EDGE,"E3.0.3.86");var subQ2=makeQuery(id+"F0.imprint","INTERSECT",VERTEX,{"derivedFrom":[subQ1,subQ0]});Q421=makeQuery(id+"F0.imprint","IMPRINT",FACE,{"disambiguationData":[TD([[makeQuery(id+"F0.imprint","IMPRINT",EDGE,{"disambiguationData":[TD([[subQ2,1.0]])],"derivedFrom":subQ1}),-1.0]])]});}
            var Q422;
            {var subQ0=sQuery(id+"F0.wireOp",EDGE,"E3.0.3.209");var subQ1=sQuery(id+"F0.wireOp",EDGE,"E3.0.3.169");var subQ2=makeQuery(id+"F0.imprint","INTERSECT",VERTEX,{"derivedFrom":[subQ1,subQ0]});Q422=makeQuery(id+"F0.imprint","IMPRINT",FACE,{"disambiguationData":[TD([[makeQuery(id+"F0.imprint","IMPRINT",EDGE,{"disambiguationData":[TD([[subQ2,1.0]])],"derivedFrom":subQ1}),-1.0]])]});}
            var Q423;
            {var subQ0=sQuery(id+"F0.wireOp",EDGE,"E3.0.1.98");var subQ1=sQuery(id+"F0.wireOp",EDGE,"E3.0.1.87");var subQ2=makeQuery(id+"F0.imprint","INTERSECT",VERTEX,{"derivedFrom":[subQ1,subQ0]});Q423=makeQuery(id+"F0.imprint","IMPRINT",FACE,{"disambiguationData":[TD([[makeQuery(id+"F0.imprint","IMPRINT",EDGE,{"disambiguationData":[TD([[subQ2,1.0]])],"derivedFrom":subQ1}),-1.0]])]});}
            var Q424;
            {var subQ0=sQuery(id+"F0.wireOp",EDGE,"E3.0.2.161");var subQ1=sQuery(id+"F0.wireOp",EDGE,"E3.0.2.140");var subQ2=makeQuery(id+"F0.imprint","INTERSECT",VERTEX,{"derivedFrom":[subQ1,subQ0]});Q424=makeQuery(id+"F0.imprint","IMPRINT",FACE,{"disambiguationData":[TD([[makeQuery(id+"F0.imprint","IMPRINT",EDGE,{"disambiguationData":[TD([[subQ2,1.0]])],"derivedFrom":subQ1}),1.0]])]});}
            var Q425;
            {var subQ0=sQuery(id+"F0.wireOp",EDGE,"E3.0.2.226");var subQ1=sQuery(id+"F0.wireOp",EDGE,"E3.0.2.133");var subQ2=makeQuery(id+"F0.imprint","INTERSECT",VERTEX,{"derivedFrom":[subQ1,subQ0]});Q425=makeQuery(id+"F0.imprint","IMPRINT",FACE,{"disambiguationData":[TD([[makeQuery(id+"F0.imprint","IMPRINT",EDGE,{"disambiguationData":[TD([[subQ2,1.0]])],"derivedFrom":subQ1}),1.0]])]});}
            var Q426;
            {var subQ0=sQuery(id+"F0.wireOp",EDGE,"E3.0.2.123");var subQ1=sQuery(id+"F0.wireOp",EDGE,"E3.0.2.89");var subQ2=makeQuery(id+"F0.imprint","INTERSECT",VERTEX,{"derivedFrom":[subQ1,subQ0]});Q426=makeQuery(id+"F0.imprint","IMPRINT",FACE,{"disambiguationData":[TD([[makeQuery(id+"F0.imprint","IMPRINT",EDGE,{"disambiguationData":[TD([[subQ2,1.0]])],"derivedFrom":subQ1}),-1.0]])]});}
            var Q427;
            {var subQ0=sQuery(id+"F0.wireOp",EDGE,"E3.0.3.98");var subQ1=sQuery(id+"F0.wireOp",EDGE,"E3.0.3.87");var subQ2=makeQuery(id+"F0.imprint","INTERSECT",VERTEX,{"derivedFrom":[subQ1,subQ0]});Q427=makeQuery(id+"F0.imprint","IMPRINT",FACE,{"disambiguationData":[TD([[makeQuery(id+"F0.imprint","IMPRINT",EDGE,{"disambiguationData":[TD([[subQ2,1.0]])],"derivedFrom":subQ1}),-1.0]])]});}
            var Q428;
            {var subQ0=sQuery(id+"F0.wireOp",EDGE,"E3.0.4.223");var subQ1=sQuery(id+"F0.wireOp",EDGE,"E3.0.4.154");var subQ2=makeQuery(id+"F0.imprint","INTERSECT",VERTEX,{"derivedFrom":[subQ1,subQ0]});Q428=makeQuery(id+"F0.imprint","IMPRINT",FACE,{"disambiguationData":[TD([[makeQuery(id+"F0.imprint","IMPRINT",EDGE,{"disambiguationData":[TD([[subQ2,1.0]])],"derivedFrom":subQ1}),1.0]])]});}
            var Q429;
            {var subQ0=sQuery(id+"F0.wireOp",EDGE,"E3.0.1.129");var subQ1=sQuery(id+"F0.wireOp",EDGE,"E3.0.1.81");var subQ2=makeQuery(id+"F0.imprint","INTERSECT",VERTEX,{"derivedFrom":[subQ1,subQ0]});Q429=makeQuery(id+"F0.imprint","IMPRINT",FACE,{"disambiguationData":[TD([[makeQuery(id+"F0.imprint","IMPRINT",EDGE,{"disambiguationData":[TD([[subQ2,1.0]])],"derivedFrom":subQ1}),-1.0]])]});}
            var Q430;
            {var subQ0=sQuery(id+"F0.wireOp",EDGE,"E3.0.1.246");var subQ1=sQuery(id+"F0.wireOp",EDGE,"E3.0.1.228");var subQ2=makeQuery(id+"F0.imprint","INTERSECT",VERTEX,{"derivedFrom":[subQ1,subQ0]});Q430=makeQuery(id+"F0.imprint","IMPRINT",FACE,{"disambiguationData":[TD([[makeQuery(id+"F0.imprint","IMPRINT",EDGE,{"disambiguationData":[TD([[subQ2,1.0]])],"derivedFrom":subQ1}),-1.0]])]});}
            var Q431;
            {var subQ0=sQuery(id+"F0.wireOp",EDGE,"E3.0.1.211");var subQ1=sQuery(id+"F0.wireOp",EDGE,"E3.0.1.162");var subQ2=makeQuery(id+"F0.imprint","INTERSECT",VERTEX,{"derivedFrom":[subQ1,subQ0]});Q431=makeQuery(id+"F0.imprint","IMPRINT",FACE,{"disambiguationData":[TD([[makeQuery(id+"F0.imprint","IMPRINT",EDGE,{"disambiguationData":[TD([[subQ2,1.0]])],"derivedFrom":subQ1}),-1.0]])]});}
            var Q432;
            {var subQ0=sQuery(id+"F0.wireOp",EDGE,"E3.0.2.127");var subQ1=sQuery(id+"F0.wireOp",EDGE,"E3.0.2.84");var subQ2=makeQuery(id+"F0.imprint","INTERSECT",VERTEX,{"derivedFrom":[subQ1,subQ0]});Q432=makeQuery(id+"F0.imprint","IMPRINT",FACE,{"disambiguationData":[TD([[makeQuery(id+"F0.imprint","IMPRINT",EDGE,{"disambiguationData":[TD([[subQ2,1.0]])],"derivedFrom":subQ1}),-1.0]])]});}
            var Q433;
            {var subQ0=sQuery(id+"F0.wireOp",EDGE,"E3.0.2.212");var subQ1=sQuery(id+"F0.wireOp",EDGE,"E3.0.2.166");var subQ2=makeQuery(id+"F0.imprint","INTERSECT",VERTEX,{"derivedFrom":[subQ1,subQ0]});Q433=makeQuery(id+"F0.imprint","IMPRINT",FACE,{"disambiguationData":[TD([[makeQuery(id+"F0.imprint","IMPRINT",EDGE,{"disambiguationData":[TD([[subQ2,1.0]])],"derivedFrom":subQ1}),-1.0]])]});}
            var Q434;
            {var subQ0=sQuery(id+"F0.wireOp",EDGE,"E3.0.3.99");var subQ1=sQuery(id+"F0.wireOp",EDGE,"E3.0.3.88");var subQ2=makeQuery(id+"F0.imprint","INTERSECT",VERTEX,{"derivedFrom":[subQ1,subQ0]});Q434=makeQuery(id+"F0.imprint","IMPRINT",FACE,{"disambiguationData":[TD([[makeQuery(id+"F0.imprint","IMPRINT",EDGE,{"disambiguationData":[TD([[subQ2,1.0]])],"derivedFrom":subQ1}),-1.0]])]});}
            var Q435;
            {var subQ0=sQuery(id+"F0.wireOp",EDGE,"E3.0.3.129");var subQ1=sQuery(id+"F0.wireOp",EDGE,"E3.0.3.81");var subQ2=makeQuery(id+"F0.imprint","INTERSECT",VERTEX,{"derivedFrom":[subQ1,subQ0]});Q435=makeQuery(id+"F0.imprint","IMPRINT",FACE,{"disambiguationData":[TD([[makeQuery(id+"F0.imprint","IMPRINT",EDGE,{"disambiguationData":[TD([[subQ2,1.0]])],"derivedFrom":subQ1}),-1.0]])]});}
            var Q436;
            {var subQ0=sQuery(id+"F0.wireOp",EDGE,"E3.0.3.246");var subQ1=sQuery(id+"F0.wireOp",EDGE,"E3.0.3.228");var subQ2=makeQuery(id+"F0.imprint","INTERSECT",VERTEX,{"derivedFrom":[subQ1,subQ0]});Q436=makeQuery(id+"F0.imprint","IMPRINT",FACE,{"disambiguationData":[TD([[makeQuery(id+"F0.imprint","IMPRINT",EDGE,{"disambiguationData":[TD([[subQ2,1.0]])],"derivedFrom":subQ1}),-1.0]])]});}
            var Q437;
            {var subQ0=sQuery(id+"F0.wireOp",EDGE,"E3.0.3.211");var subQ1=sQuery(id+"F0.wireOp",EDGE,"E3.0.3.162");var subQ2=makeQuery(id+"F0.imprint","INTERSECT",VERTEX,{"derivedFrom":[subQ1,subQ0]});Q437=makeQuery(id+"F0.imprint","IMPRINT",FACE,{"disambiguationData":[TD([[makeQuery(id+"F0.imprint","IMPRINT",EDGE,{"disambiguationData":[TD([[subQ2,1.0]])],"derivedFrom":subQ1}),-1.0]])]});}
            var Q438;
            {var subQ0=sQuery(id+"F0.wireOp",EDGE,"E3.0.4.99");var subQ1=sQuery(id+"F0.wireOp",EDGE,"E3.0.4.88");var subQ2=makeQuery(id+"F0.imprint","INTERSECT",VERTEX,{"derivedFrom":[subQ1,subQ0]});Q438=makeQuery(id+"F0.imprint","IMPRINT",FACE,{"disambiguationData":[TD([[makeQuery(id+"F0.imprint","IMPRINT",EDGE,{"disambiguationData":[TD([[subQ2,1.0]])],"derivedFrom":subQ1}),-1.0]])]});}
            var Q439;
            {var subQ0=sQuery(id+"F0.wireOp",EDGE,"E3.0.2.125");var subQ1=sQuery(id+"F0.wireOp",EDGE,"E3.0.2.26");var subQ2=makeQuery(id+"F0.imprint","INTERSECT",VERTEX,{"derivedFrom":[subQ1,subQ0]});Q439=makeQuery(id+"F0.imprint","IMPRINT",FACE,{"disambiguationData":[TD([[makeQuery(id+"F0.imprint","IMPRINT",EDGE,{"disambiguationData":[TD([[subQ2,1.0]])],"derivedFrom":subQ1}),-1.0]])]});}
            var Q440;
            {var subQ0=sQuery(id+"F0.wireOp",EDGE,"E3.0.2.153");var subQ1=sQuery(id+"F0.wireOp",EDGE,"E3.0.2.134");var subQ2=makeQuery(id+"F0.imprint","INTERSECT",VERTEX,{"derivedFrom":[subQ1,subQ0]});Q440=makeQuery(id+"F0.imprint","IMPRINT",FACE,{"disambiguationData":[TD([[makeQuery(id+"F0.imprint","IMPRINT",EDGE,{"disambiguationData":[TD([[subQ2,1.0]])],"derivedFrom":subQ1}),1.0]])]});}
            var Q441;
            {var subQ0=sQuery(id+"F0.wireOp",EDGE,"E3.0.2.103");var subQ1=sQuery(id+"F0.wireOp",EDGE,"E3.0.2.82");var subQ2=makeQuery(id+"F0.imprint","INTERSECT",VERTEX,{"derivedFrom":[subQ1,subQ0]});Q441=makeQuery(id+"F0.imprint","IMPRINT",FACE,{"disambiguationData":[TD([[makeQuery(id+"F0.imprint","IMPRINT",EDGE,{"disambiguationData":[TD([[subQ2,1.0]])],"derivedFrom":subQ1}),-1.0]])]});}
            var Q442;
            {var subQ0=sQuery(id+"F0.wireOp",EDGE,"E3.0.2.215");var subQ1=sQuery(id+"F0.wireOp",EDGE,"E3.0.2.186");var subQ2=makeQuery(id+"F0.imprint","INTERSECT",VERTEX,{"derivedFrom":[subQ1,subQ0]});Q442=makeQuery(id+"F0.imprint","IMPRINT",FACE,{"disambiguationData":[TD([[makeQuery(id+"F0.imprint","IMPRINT",EDGE,{"disambiguationData":[TD([[subQ2,1.0]])],"derivedFrom":subQ1}),-1.0]])]});}
            var Q443;
            {var subQ0=sQuery(id+"F0.wireOp",EDGE,"E3.0.3.216");var subQ1=sQuery(id+"F0.wireOp",EDGE,"E3.0.3.87");var subQ2=makeQuery(id+"F0.imprint","INTERSECT",VERTEX,{"derivedFrom":[subQ1,subQ0]});Q443=makeQuery(id+"F0.imprint","IMPRINT",FACE,{"disambiguationData":[TD([[makeQuery(id+"F0.imprint","IMPRINT",EDGE,{"disambiguationData":[TD([[subQ2,1.0]])],"derivedFrom":subQ1}),-1.0]])]});}
            var Q444;
            {var subQ0=sQuery(id+"F0.wireOp",EDGE,"E3.0.1.210");var subQ1=sQuery(id+"F0.wireOp",EDGE,"E3.0.1.163");var subQ2=makeQuery(id+"F0.imprint","INTERSECT",VERTEX,{"derivedFrom":[subQ1,subQ0]});Q444=makeQuery(id+"F0.imprint","IMPRINT",FACE,{"disambiguationData":[TD([[makeQuery(id+"F0.imprint","IMPRINT",EDGE,{"disambiguationData":[TD([[subQ2,1.0]])],"derivedFrom":subQ1}),-1.0]])]});}
            var Q445;
            {var subQ0=sQuery(id+"F0.wireOp",EDGE,"E3.0.2.104");var subQ1=sQuery(id+"F0.wireOp",EDGE,"E3.0.2.83");var subQ2=makeQuery(id+"F0.imprint","INTERSECT",VERTEX,{"derivedFrom":[subQ1,subQ0]});Q445=makeQuery(id+"F0.imprint","IMPRINT",FACE,{"disambiguationData":[TD([[makeQuery(id+"F0.imprint","IMPRINT",EDGE,{"disambiguationData":[TD([[subQ2,1.0]])],"derivedFrom":subQ1}),-1.0]])]});}
            var Q446;
            {var subQ0=sQuery(id+"F0.wireOp",EDGE,"E3.0.2.205");var subQ1=sQuery(id+"F0.wireOp",EDGE,"E3.0.2.167");var subQ2=makeQuery(id+"F0.imprint","INTERSECT",VERTEX,{"derivedFrom":[subQ1,subQ0]});Q446=makeQuery(id+"F0.imprint","IMPRINT",FACE,{"disambiguationData":[TD([[makeQuery(id+"F0.imprint","IMPRINT",EDGE,{"disambiguationData":[TD([[subQ2,1.0]])],"derivedFrom":subQ1}),-1.0]])]});}
            var Q447;
            {var subQ0=sQuery(id+"F0.wireOp",EDGE,"E3.0.3.245");var subQ1=sQuery(id+"F0.wireOp",EDGE,"E3.0.3.229");var subQ2=makeQuery(id+"F0.imprint","INTERSECT",VERTEX,{"derivedFrom":[subQ1,subQ0]});Q447=makeQuery(id+"F0.imprint","IMPRINT",FACE,{"disambiguationData":[TD([[makeQuery(id+"F0.imprint","IMPRINT",EDGE,{"disambiguationData":[TD([[subQ2,1.0]])],"derivedFrom":subQ1}),-1.0]])]});}
            var Q448;
            {var subQ0=sQuery(id+"F0.wireOp",EDGE,"E3.0.3.210");var subQ1=sQuery(id+"F0.wireOp",EDGE,"E3.0.3.163");var subQ2=makeQuery(id+"F0.imprint","INTERSECT",VERTEX,{"derivedFrom":[subQ1,subQ0]});Q448=makeQuery(id+"F0.imprint","IMPRINT",FACE,{"disambiguationData":[TD([[makeQuery(id+"F0.imprint","IMPRINT",EDGE,{"disambiguationData":[TD([[subQ2,1.0]])],"derivedFrom":subQ1}),-1.0]])]});}
            var Q449;
            {var subQ0=sQuery(id+"F0.wireOp",EDGE,"E3.0.2.223");var subQ1=sQuery(id+"F0.wireOp",EDGE,"E3.0.2.154");var subQ2=makeQuery(id+"F0.imprint","INTERSECT",VERTEX,{"derivedFrom":[subQ1,subQ0]});Q449=makeQuery(id+"F0.imprint","IMPRINT",FACE,{"disambiguationData":[TD([[makeQuery(id+"F0.imprint","IMPRINT",EDGE,{"disambiguationData":[TD([[subQ2,1.0]])],"derivedFrom":subQ1}),1.0]])]});}
            var Q450;
            {var subQ0=sQuery(id+"F0.wireOp",EDGE,"E3.0.2.155");var subQ1=sQuery(id+"F0.wireOp",EDGE,"E3.0.2.135");var subQ2=makeQuery(id+"F0.imprint","INTERSECT",VERTEX,{"derivedFrom":[subQ1,subQ0]});Q450=makeQuery(id+"F0.imprint","IMPRINT",FACE,{"disambiguationData":[TD([[makeQuery(id+"F0.imprint","IMPRINT",EDGE,{"disambiguationData":[TD([[subQ2,1.0]])],"derivedFrom":subQ1}),1.0]])]});}
            var Q451;
            {var subQ0=sQuery(id+"F0.wireOp",EDGE,"E3.0.2.197");var subQ1=sQuery(id+"F0.wireOp",EDGE,"E3.0.2.85");var subQ2=makeQuery(id+"F0.imprint","INTERSECT",VERTEX,{"derivedFrom":[subQ1,subQ0]});Q451=makeQuery(id+"F0.imprint","IMPRINT",FACE,{"disambiguationData":[TD([[makeQuery(id+"F0.imprint","IMPRINT",EDGE,{"disambiguationData":[TD([[subQ2,1.0]])],"derivedFrom":subQ1}),-1.0]])]});}
            var Q452;
            {var subQ0=sQuery(id+"F0.wireOp",EDGE,"E3.0.2.213");var subQ1=sQuery(id+"F0.wireOp",EDGE,"E3.0.2.187");var subQ2=makeQuery(id+"F0.imprint","INTERSECT",VERTEX,{"derivedFrom":[subQ1,subQ0]});Q452=makeQuery(id+"F0.imprint","IMPRINT",FACE,{"disambiguationData":[TD([[makeQuery(id+"F0.imprint","IMPRINT",EDGE,{"disambiguationData":[TD([[subQ2,1.0]])],"derivedFrom":subQ1}),-1.0]])]});}
            var Q453;
            {var subQ0=sQuery(id+"F0.wireOp",EDGE,"E3.0.3.196");var subQ1=sQuery(id+"F0.wireOp",EDGE,"E3.0.3.101");var subQ2=makeQuery(id+"F0.imprint","INTERSECT",VERTEX,{"derivedFrom":[subQ1,subQ0]});Q453=makeQuery(id+"F0.imprint","IMPRINT",FACE,{"disambiguationData":[TD([[makeQuery(id+"F0.imprint","IMPRINT",EDGE,{"disambiguationData":[TD([[subQ2,1.0]])],"derivedFrom":subQ1}),-1.0]])]});}
            var Q454;
            {var subQ0=sQuery(id+"F0.wireOp",EDGE,"E3.0.2.33");var subQ1=sQuery(id+"F0.wireOp",EDGE,"E3.0.2.23");var subQ2=makeQuery(id+"F0.imprint","INTERSECT",VERTEX,{"derivedFrom":[subQ1,subQ0]});Q454=makeQuery(id+"F0.imprint","IMPRINT",FACE,{"disambiguationData":[TD([[makeQuery(id+"F0.imprint","IMPRINT",EDGE,{"disambiguationData":[TD([[subQ2,1.0]])],"derivedFrom":subQ1}),-1.0]])]});}
            var Q455;
            {var subQ0=sQuery(id+"F0.wireOp",EDGE,"E3.0.2.204");var subQ1=sQuery(id+"F0.wireOp",EDGE,"E3.0.2.168");var subQ2=makeQuery(id+"F0.imprint","INTERSECT",VERTEX,{"derivedFrom":[subQ1,subQ0]});Q455=makeQuery(id+"F0.imprint","IMPRINT",FACE,{"disambiguationData":[TD([[makeQuery(id+"F0.imprint","IMPRINT",EDGE,{"disambiguationData":[TD([[subQ2,1.0]])],"derivedFrom":subQ1}),-1.0]])]});}
            var Q456;
            {var subQ0=sQuery(id+"F0.wireOp",EDGE,"E3.0.3.214");var subQ1=sQuery(id+"F0.wireOp",EDGE,"E3.0.3.88");var subQ2=makeQuery(id+"F0.imprint","INTERSECT",VERTEX,{"derivedFrom":[subQ1,subQ0]});Q456=makeQuery(id+"F0.imprint","IMPRINT",FACE,{"disambiguationData":[TD([[makeQuery(id+"F0.imprint","IMPRINT",EDGE,{"disambiguationData":[TD([[subQ2,1.0]])],"derivedFrom":subQ1}),-1.0]])]});}
            var Q457;
            {var subQ0=sQuery(id+"F0.wireOp",EDGE,"E3.0.3.239");var subQ1=sQuery(id+"F0.wireOp",EDGE,"E3.0.3.19");var subQ2=makeQuery(id+"F0.imprint","INTERSECT",VERTEX,{"derivedFrom":[subQ1,subQ0]});Q457=makeQuery(id+"F0.imprint","IMPRINT",FACE,{"disambiguationData":[TD([[makeQuery(id+"F0.imprint","IMPRINT",EDGE,{"disambiguationData":[TD([[subQ2,1.0]])],"derivedFrom":subQ1}),-1.0]])]});}
            var Q458;
            {var subQ0=sQuery(id+"F0.wireOp",EDGE,"E3.0.3.244");var subQ1=sQuery(id+"F0.wireOp",EDGE,"E3.0.3.230");var subQ2=makeQuery(id+"F0.imprint","INTERSECT",VERTEX,{"derivedFrom":[subQ1,subQ0]});Q458=makeQuery(id+"F0.imprint","IMPRINT",FACE,{"disambiguationData":[TD([[makeQuery(id+"F0.imprint","IMPRINT",EDGE,{"disambiguationData":[TD([[subQ2,1.0]])],"derivedFrom":subQ1}),-1.0]])]});}
            var Q459;
            {var subQ0=sQuery(id+"F0.wireOp",EDGE,"E3.0.3.237");var subQ1=sQuery(id+"F0.wireOp",EDGE,"E3.0.3.181");var subQ2=makeQuery(id+"F0.imprint","INTERSECT",VERTEX,{"derivedFrom":[subQ1,subQ0]});Q459=makeQuery(id+"F0.imprint","IMPRINT",FACE,{"disambiguationData":[TD([[makeQuery(id+"F0.imprint","IMPRINT",EDGE,{"disambiguationData":[TD([[subQ2,1.0]])],"derivedFrom":subQ1}),-1.0]])]});}
            var Q460;
            {var subQ0=sQuery(id+"F0.wireOp",EDGE,"E3.0.3.208");var subQ1=sQuery(id+"F0.wireOp",EDGE,"E3.0.3.164");var subQ2=makeQuery(id+"F0.imprint","INTERSECT",VERTEX,{"derivedFrom":[subQ1,subQ0]});Q460=makeQuery(id+"F0.imprint","IMPRINT",FACE,{"disambiguationData":[TD([[makeQuery(id+"F0.imprint","IMPRINT",EDGE,{"disambiguationData":[TD([[subQ2,1.0]])],"derivedFrom":subQ1}),-1.0]])]});}
            var Q461;
            {var subQ0=sQuery(id+"F0.wireOp",EDGE,"E2.15.0.7");var subQ1=sQuery(id+"F0.wireOp",EDGE,"E2.15.0.5");var subQ2=makeQuery(id+"F0.imprint","INTERSECT",VERTEX,{"derivedFrom":[subQ1,subQ0]});Q461=makeQuery(id+"F0.imprint","IMPRINT",FACE,{"disambiguationData":[TD([[makeQuery(id+"F0.imprint","IMPRINT",EDGE,{"disambiguationData":[TD([[subQ2,1.0]])],"derivedFrom":subQ1}),-1.0]])]});}
            var Q462;
            {var subQ0=sQuery(id+"F0.wireOp",EDGE,"E2.11.0.7");var subQ1=sQuery(id+"F0.wireOp",EDGE,"E2.11.0.5");var subQ2=makeQuery(id+"F0.imprint","INTERSECT",VERTEX,{"derivedFrom":[subQ1,subQ0]});Q462=makeQuery(id+"F0.imprint","IMPRINT",FACE,{"disambiguationData":[TD([[makeQuery(id+"F0.imprint","IMPRINT",EDGE,{"disambiguationData":[TD([[subQ2,1.0]])],"derivedFrom":subQ1}),-1.0]])]});}
            var Q463;
            {var subQ0=sQuery(id+"F0.wireOp",EDGE,"E2.7.0.7");var subQ1=sQuery(id+"F0.wireOp",EDGE,"E2.7.0.5");var subQ2=makeQuery(id+"F0.imprint","INTERSECT",VERTEX,{"derivedFrom":[subQ1,subQ0]});Q463=makeQuery(id+"F0.imprint","IMPRINT",FACE,{"disambiguationData":[TD([[makeQuery(id+"F0.imprint","IMPRINT",EDGE,{"disambiguationData":[TD([[subQ2,1.0]])],"derivedFrom":subQ1}),-1.0]])]});}
            var Q464;
            {var subQ0=sQuery(id+"F0.wireOp",EDGE,"E2.3.0.7");var subQ1=sQuery(id+"F0.wireOp",EDGE,"E2.3.0.5");var subQ2=makeQuery(id+"F0.imprint","INTERSECT",VERTEX,{"derivedFrom":[subQ1,subQ0]});Q464=makeQuery(id+"F0.imprint","IMPRINT",FACE,{"disambiguationData":[TD([[makeQuery(id+"F0.imprint","IMPRINT",EDGE,{"disambiguationData":[TD([[subQ2,1.0]])],"derivedFrom":subQ1}),-1.0]])]});}
            var Q465;
            {var subQ0=sQuery(id+"F0.wireOp",EDGE,"E2.23.0.7");var subQ1=sQuery(id+"F0.wireOp",EDGE,"E2.23.0.5");var subQ2=makeQuery(id+"F0.imprint","INTERSECT",VERTEX,{"derivedFrom":[subQ1,subQ0]});Q465=makeQuery(id+"F0.imprint","IMPRINT",FACE,{"disambiguationData":[TD([[makeQuery(id+"F0.imprint","IMPRINT",EDGE,{"disambiguationData":[TD([[subQ2,1.0]])],"derivedFrom":subQ1}),-1.0]])]});}
            var Q466;
            {var subQ0=sQuery(id+"F0.wireOp",EDGE,"E2.19.0.7");var subQ1=sQuery(id+"F0.wireOp",EDGE,"E2.19.0.5");var subQ2=makeQuery(id+"F0.imprint","INTERSECT",VERTEX,{"derivedFrom":[subQ1,subQ0]});Q466=makeQuery(id+"F0.imprint","IMPRINT",FACE,{"disambiguationData":[TD([[makeQuery(id+"F0.imprint","IMPRINT",EDGE,{"disambiguationData":[TD([[subQ2,1.0]])],"derivedFrom":subQ1}),-1.0]])]});}
            var Q467;
            {var subQ0=sQuery(id+"F0.wireOp",EDGE,"E3.0.1.244");var subQ1=sQuery(id+"F0.wireOp",EDGE,"E3.0.1.230");var subQ2=makeQuery(id+"F0.imprint","INTERSECT",VERTEX,{"derivedFrom":[subQ1,subQ0]});Q467=makeQuery(id+"F0.imprint","IMPRINT",FACE,{"disambiguationData":[TD([[makeQuery(id+"F0.imprint","IMPRINT",EDGE,{"disambiguationData":[TD([[subQ2,1.0]])],"derivedFrom":subQ1}),-1.0]])]});}
            var Q468;
            {var subQ0=sQuery(id+"F0.wireOp",EDGE,"E3.0.1.208");var subQ1=sQuery(id+"F0.wireOp",EDGE,"E3.0.1.164");var subQ2=makeQuery(id+"F0.imprint","INTERSECT",VERTEX,{"derivedFrom":[subQ1,subQ0]});Q468=makeQuery(id+"F0.imprint","IMPRINT",FACE,{"disambiguationData":[TD([[makeQuery(id+"F0.imprint","IMPRINT",EDGE,{"disambiguationData":[TD([[subQ2,1.0]])],"derivedFrom":subQ1}),-1.0]])]});}
            var Q469;
            {var subQ0=sQuery(id+"F0.wireOp",EDGE,"E3.0.2.96");var subQ1=sQuery(id+"F0.wireOp",EDGE,"E3.0.2.26");var subQ2=makeQuery(id+"F0.imprint","INTERSECT",VERTEX,{"derivedFrom":[subQ1,subQ0]});Q469=makeQuery(id+"F0.imprint","IMPRINT",FACE,{"disambiguationData":[TD([[makeQuery(id+"F0.imprint","IMPRINT",EDGE,{"disambiguationData":[TD([[subQ2,1.0]])],"derivedFrom":subQ1}),-1.0]])]});}
            var Q470;
            {var subQ0=sQuery(id+"F0.wireOp",EDGE,"E3.0.4.10");var subQ1=sQuery(id+"F0.wireOp",EDGE,"E3.0.4.9");var subQ2=makeQuery(id+"F0.imprint","INTERSECT",VERTEX,{"derivedFrom":[subQ1,subQ0]});Q470=makeQuery(id+"F0.imprint","IMPRINT",FACE,{"disambiguationData":[TD([[makeQuery(id+"F0.imprint","IMPRINT",EDGE,{"disambiguationData":[TD([[subQ2,1.0]])],"derivedFrom":subQ1}),-1.0]])]});}
            var Q471;
            {var subQ0=sQuery(id+"F0.wireOp",EDGE,"E0.bottom");Q471=makeQuery(id+"F0.imprint","IMPRINT",FACE,{"disambiguationData":[TD([[makeQuery(id+"F0.imprint","IMPRINT",EDGE,{"derivedFrom":subQ0}),-1.0]])]});}
            var Q472;
            {var subQ0=sQuery(id+"F0.wireOp",EDGE,"E3.0.1.225");var subQ1=sQuery(id+"F0.wireOp",EDGE,"E3.0.1.132");var subQ2=makeQuery(id+"F0.imprint","INTERSECT",VERTEX,{"derivedFrom":[subQ1,subQ0]});Q472=makeQuery(id+"F0.imprint","IMPRINT",FACE,{"disambiguationData":[TD([[makeQuery(id+"F0.imprint","IMPRINT",EDGE,{"disambiguationData":[TD([[subQ2,1.0]])],"derivedFrom":subQ1}),1.0]])]});}
            var Q473;
            {var subQ0=sQuery(id+"F0.wireOp",EDGE,"E3.0.2.224");var subQ1=sQuery(id+"F0.wireOp",EDGE,"E3.0.2.157");var subQ2=makeQuery(id+"F0.imprint","INTERSECT",VERTEX,{"derivedFrom":[subQ1,subQ0]});Q473=makeQuery(id+"F0.imprint","IMPRINT",FACE,{"disambiguationData":[TD([[makeQuery(id+"F0.imprint","IMPRINT",EDGE,{"disambiguationData":[TD([[subQ2,1.0]])],"derivedFrom":subQ1}),1.0]])]});}
            var Q474;
            {var subQ0=sQuery(id+"F0.wireOp",EDGE,"E3.0.2.227");var subQ1=sQuery(id+"F0.wireOp",EDGE,"E3.0.2.137");var subQ2=makeQuery(id+"F0.imprint","INTERSECT",VERTEX,{"derivedFrom":[subQ1,subQ0]});Q474=makeQuery(id+"F0.imprint","IMPRINT",FACE,{"disambiguationData":[TD([[makeQuery(id+"F0.imprint","IMPRINT",EDGE,{"disambiguationData":[TD([[subQ2,1.0]])],"derivedFrom":subQ1}),1.0]])]});}
            var Q475;
            {var subQ0=sQuery(id+"F0.wireOp",EDGE,"E3.0.2.95");var subQ1=sQuery(id+"F0.wireOp",EDGE,"E3.0.2.84");var subQ2=makeQuery(id+"F0.imprint","INTERSECT",VERTEX,{"derivedFrom":[subQ1,subQ0]});Q475=makeQuery(id+"F0.imprint","IMPRINT",FACE,{"disambiguationData":[TD([[makeQuery(id+"F0.imprint","IMPRINT",EDGE,{"disambiguationData":[TD([[subQ2,1.0]])],"derivedFrom":subQ1}),-1.0]])]});}
            var Q476;
            {var subQ0=sQuery(id+"F0.wireOp",EDGE,"E3.0.2.199");var subQ1=sQuery(id+"F0.wireOp",EDGE,"E3.0.2.185");var subQ2=makeQuery(id+"F0.imprint","INTERSECT",VERTEX,{"derivedFrom":[subQ1,subQ0]});Q476=makeQuery(id+"F0.imprint","IMPRINT",FACE,{"disambiguationData":[TD([[makeQuery(id+"F0.imprint","IMPRINT",EDGE,{"disambiguationData":[TD([[subQ2,1.0]])],"derivedFrom":subQ1}),-1.0]])]});}
            var Q477;
            {var subQ0=sQuery(id+"F0.wireOp",EDGE,"E3.0.2.203");var subQ1=sQuery(id+"F0.wireOp",EDGE,"E3.0.2.170");var subQ2=makeQuery(id+"F0.imprint","INTERSECT",VERTEX,{"derivedFrom":[subQ1,subQ0]});Q477=makeQuery(id+"F0.imprint","IMPRINT",FACE,{"disambiguationData":[TD([[makeQuery(id+"F0.imprint","IMPRINT",EDGE,{"disambiguationData":[TD([[subQ2,1.0]])],"derivedFrom":subQ1}),-1.0]])]});}
            var Q478;
            {var subQ0=sQuery(id+"F0.wireOp",EDGE,"E3.0.1.130");var subQ1=sQuery(id+"F0.wireOp",EDGE,"E3.0.1.23");var subQ2=makeQuery(id+"F0.imprint","INTERSECT",VERTEX,{"derivedFrom":[subQ1,subQ0]});Q478=makeQuery(id+"F0.imprint","IMPRINT",FACE,{"disambiguationData":[TD([[makeQuery(id+"F0.imprint","IMPRINT",EDGE,{"disambiguationData":[TD([[subQ2,1.0]])],"derivedFrom":subQ1}),-1.0]])]});}
            var Q479;
            {var subQ0=sQuery(id+"F0.wireOp",EDGE,"E3.0.1.161");var subQ1=sQuery(id+"F0.wireOp",EDGE,"E3.0.1.140");var subQ2=makeQuery(id+"F0.imprint","INTERSECT",VERTEX,{"derivedFrom":[subQ1,subQ0]});Q479=makeQuery(id+"F0.imprint","IMPRINT",FACE,{"disambiguationData":[TD([[makeQuery(id+"F0.imprint","IMPRINT",EDGE,{"disambiguationData":[TD([[subQ2,1.0]])],"derivedFrom":subQ1}),1.0]])]});}
            var Q480;
            {var subQ0=sQuery(id+"F0.wireOp",EDGE,"E3.0.3.130");var subQ1=sQuery(id+"F0.wireOp",EDGE,"E3.0.3.23");var subQ2=makeQuery(id+"F0.imprint","INTERSECT",VERTEX,{"derivedFrom":[subQ1,subQ0]});Q480=makeQuery(id+"F0.imprint","IMPRINT",FACE,{"disambiguationData":[TD([[makeQuery(id+"F0.imprint","IMPRINT",EDGE,{"disambiguationData":[TD([[subQ2,1.0]])],"derivedFrom":subQ1}),-1.0]])]});}
            var Q481;
            {var subQ0=sQuery(id+"F0.wireOp",EDGE,"E3.0.3.161");var subQ1=sQuery(id+"F0.wireOp",EDGE,"E3.0.3.140");var subQ2=makeQuery(id+"F0.imprint","INTERSECT",VERTEX,{"derivedFrom":[subQ1,subQ0]});Q481=makeQuery(id+"F0.imprint","IMPRINT",FACE,{"disambiguationData":[TD([[makeQuery(id+"F0.imprint","IMPRINT",EDGE,{"disambiguationData":[TD([[subQ2,1.0]])],"derivedFrom":subQ1}),1.0]])]});}
            var Q482;
            {var subQ0=sQuery(id+"F0.wireOp",EDGE,"E2.5.0.3");var subQ1=sQuery(id+"F0.wireOp",EDGE,"E2.5.0.0");var subQ2=makeQuery(id+"F0.imprint","INTERSECT",VERTEX,{"derivedFrom":[subQ1,subQ0]});Q482=makeQuery(id+"F0.imprint","IMPRINT",FACE,{"disambiguationData":[TD([[makeQuery(id+"F0.imprint","IMPRINT",EDGE,{"disambiguationData":[TD([[subQ2,1.0]])],"derivedFrom":subQ1}),1.0]])]});}
            var Q483;
            {var subQ0=sQuery(id+"F0.wireOp",EDGE,"E2.21.0.3");var subQ1=sQuery(id+"F0.wireOp",EDGE,"E2.21.0.0");var subQ2=makeQuery(id+"F0.imprint","INTERSECT",VERTEX,{"derivedFrom":[subQ1,subQ0]});Q483=makeQuery(id+"F0.imprint","IMPRINT",FACE,{"disambiguationData":[TD([[makeQuery(id+"F0.imprint","IMPRINT",EDGE,{"disambiguationData":[TD([[subQ2,1.0]])],"derivedFrom":subQ1}),1.0]])]});}
            var Q484;
            {var subQ0=sQuery(id+"F0.wireOp",EDGE,"E2.17.0.3");var subQ1=sQuery(id+"F0.wireOp",EDGE,"E2.17.0.0");var subQ2=makeQuery(id+"F0.imprint","INTERSECT",VERTEX,{"derivedFrom":[subQ1,subQ0]});Q484=makeQuery(id+"F0.imprint","IMPRINT",FACE,{"disambiguationData":[TD([[makeQuery(id+"F0.imprint","IMPRINT",EDGE,{"disambiguationData":[TD([[subQ2,1.0]])],"derivedFrom":subQ1}),1.0]])]});}
            var Q485;
            {var subQ0=sQuery(id+"F0.wireOp",EDGE,"E2.13.0.3");var subQ1=sQuery(id+"F0.wireOp",EDGE,"E2.13.0.0");var subQ2=makeQuery(id+"F0.imprint","INTERSECT",VERTEX,{"derivedFrom":[subQ1,subQ0]});Q485=makeQuery(id+"F0.imprint","IMPRINT",FACE,{"disambiguationData":[TD([[makeQuery(id+"F0.imprint","IMPRINT",EDGE,{"disambiguationData":[TD([[subQ2,1.0]])],"derivedFrom":subQ1}),1.0]])]});}
            var Q486;
            {var subQ0=sQuery(id+"F0.wireOp",EDGE,"E2.9.0.3");var subQ1=sQuery(id+"F0.wireOp",EDGE,"E2.9.0.0");var subQ2=makeQuery(id+"F0.imprint","INTERSECT",VERTEX,{"derivedFrom":[subQ1,subQ0]});Q486=makeQuery(id+"F0.imprint","IMPRINT",FACE,{"disambiguationData":[TD([[makeQuery(id+"F0.imprint","IMPRINT",EDGE,{"disambiguationData":[TD([[subQ2,1.0]])],"derivedFrom":subQ1}),1.0]])]});}
            var Q487;
            {var subQ0=sQuery(id+"F0.wireOp",EDGE,"E2.29.0.3");var subQ1=sQuery(id+"F0.wireOp",EDGE,"E2.29.0.0");var subQ2=makeQuery(id+"F0.imprint","INTERSECT",VERTEX,{"derivedFrom":[subQ1,subQ0]});Q487=makeQuery(id+"F0.imprint","IMPRINT",FACE,{"disambiguationData":[TD([[makeQuery(id+"F0.imprint","IMPRINT",EDGE,{"disambiguationData":[TD([[subQ2,1.0]])],"derivedFrom":subQ1}),1.0]])]});}
            var Q488;
            {var subQ0=sQuery(id+"F0.wireOp",EDGE,"E2.25.0.3");var subQ1=sQuery(id+"F0.wireOp",EDGE,"E2.25.0.0");var subQ2=makeQuery(id+"F0.imprint","INTERSECT",VERTEX,{"derivedFrom":[subQ1,subQ0]});Q488=makeQuery(id+"F0.imprint","IMPRINT",FACE,{"disambiguationData":[TD([[makeQuery(id+"F0.imprint","IMPRINT",EDGE,{"disambiguationData":[TD([[subQ2,1.0]])],"derivedFrom":subQ1}),1.0]])]});}
            var Q489;
            {var subQ0=sQuery(id+"F0.wireOp",EDGE,"E3.0.1.153");var subQ1=sQuery(id+"F0.wireOp",EDGE,"E3.0.1.134");var subQ2=makeQuery(id+"F0.imprint","INTERSECT",VERTEX,{"derivedFrom":[subQ1,subQ0]});Q489=makeQuery(id+"F0.imprint","IMPRINT",FACE,{"disambiguationData":[TD([[makeQuery(id+"F0.imprint","IMPRINT",EDGE,{"disambiguationData":[TD([[subQ2,1.0]])],"derivedFrom":subQ1}),1.0]])]});}
            var Q490;
            {var subQ0=sQuery(id+"F0.wireOp",EDGE,"E3.0.1.103");var subQ1=sQuery(id+"F0.wireOp",EDGE,"E3.0.1.82");var subQ2=makeQuery(id+"F0.imprint","INTERSECT",VERTEX,{"derivedFrom":[subQ1,subQ0]});Q490=makeQuery(id+"F0.imprint","IMPRINT",FACE,{"disambiguationData":[TD([[makeQuery(id+"F0.imprint","IMPRINT",EDGE,{"disambiguationData":[TD([[subQ2,1.0]])],"derivedFrom":subQ1}),-1.0]])]});}
            var Q491;
            {var subQ0=sQuery(id+"F0.wireOp",EDGE,"E3.0.3.153");var subQ1=sQuery(id+"F0.wireOp",EDGE,"E3.0.3.134");var subQ2=makeQuery(id+"F0.imprint","INTERSECT",VERTEX,{"derivedFrom":[subQ1,subQ0]});Q491=makeQuery(id+"F0.imprint","IMPRINT",FACE,{"disambiguationData":[TD([[makeQuery(id+"F0.imprint","IMPRINT",EDGE,{"disambiguationData":[TD([[subQ2,1.0]])],"derivedFrom":subQ1}),1.0]])]});}
            var Q492;
            {var subQ0=sQuery(id+"F0.wireOp",EDGE,"E3.0.3.103");var subQ1=sQuery(id+"F0.wireOp",EDGE,"E3.0.3.82");var subQ2=makeQuery(id+"F0.imprint","INTERSECT",VERTEX,{"derivedFrom":[subQ1,subQ0]});Q492=makeQuery(id+"F0.imprint","IMPRINT",FACE,{"disambiguationData":[TD([[makeQuery(id+"F0.imprint","IMPRINT",EDGE,{"disambiguationData":[TD([[subQ2,1.0]])],"derivedFrom":subQ1}),-1.0]])]});}
            var Q493;
            {var subQ0=sQuery(id+"F0.wireOp",EDGE,"E3.0.1.104");var subQ1=sQuery(id+"F0.wireOp",EDGE,"E3.0.1.83");var subQ2=makeQuery(id+"F0.imprint","INTERSECT",VERTEX,{"derivedFrom":[subQ1,subQ0]});Q493=makeQuery(id+"F0.imprint","IMPRINT",FACE,{"disambiguationData":[TD([[makeQuery(id+"F0.imprint","IMPRINT",EDGE,{"disambiguationData":[TD([[subQ2,1.0]])],"derivedFrom":subQ1}),-1.0]])]});}
            var Q494;
            {var subQ0=sQuery(id+"F0.wireOp",EDGE,"E3.0.2.217");var subQ1=sQuery(id+"F0.wireOp",EDGE,"E3.0.2.82");var subQ2=makeQuery(id+"F0.imprint","INTERSECT",VERTEX,{"derivedFrom":[subQ1,subQ0]});Q494=makeQuery(id+"F0.imprint","IMPRINT",FACE,{"disambiguationData":[TD([[makeQuery(id+"F0.imprint","IMPRINT",EDGE,{"disambiguationData":[TD([[subQ2,1.0]])],"derivedFrom":subQ1}),-1.0]])]});}
            var Q495;
            {var subQ0=sQuery(id+"F0.wireOp",EDGE,"E3.0.2.41");var subQ1=sQuery(id+"F0.wireOp",EDGE,"E3.0.2.16");var subQ2=makeQuery(id+"F0.imprint","INTERSECT",VERTEX,{"derivedFrom":[subQ1,subQ0]});Q495=makeQuery(id+"F0.imprint","IMPRINT",FACE,{"disambiguationData":[TD([[makeQuery(id+"F0.imprint","IMPRINT",EDGE,{"disambiguationData":[TD([[subQ2,1.0]])],"derivedFrom":subQ1}),-1.0]])]});}
            var Q496;
            {var subQ0=sQuery(id+"F0.wireOp",EDGE,"E3.0.2.206");var subQ1=sQuery(id+"F0.wireOp",EDGE,"E3.0.2.171");var subQ2=makeQuery(id+"F0.imprint","INTERSECT",VERTEX,{"derivedFrom":[subQ1,subQ0]});Q496=makeQuery(id+"F0.imprint","IMPRINT",FACE,{"disambiguationData":[TD([[makeQuery(id+"F0.imprint","IMPRINT",EDGE,{"disambiguationData":[TD([[subQ2,1.0]])],"derivedFrom":subQ1}),-1.0]])]});}
            var Q497;
            {var subQ0=sQuery(id+"F0.wireOp",EDGE,"E3.0.3.104");var subQ1=sQuery(id+"F0.wireOp",EDGE,"E3.0.3.83");var subQ2=makeQuery(id+"F0.imprint","INTERSECT",VERTEX,{"derivedFrom":[subQ1,subQ0]});Q497=makeQuery(id+"F0.imprint","IMPRINT",FACE,{"disambiguationData":[TD([[makeQuery(id+"F0.imprint","IMPRINT",EDGE,{"disambiguationData":[TD([[subQ2,1.0]])],"derivedFrom":subQ1}),-1.0]])]});}
            var Q498;
            {var subQ0=sQuery(id+"F0.wireOp",EDGE,"E3.0.1.33");var subQ1=sQuery(id+"F0.wireOp",EDGE,"E3.0.1.23");var subQ2=makeQuery(id+"F0.imprint","INTERSECT",VERTEX,{"derivedFrom":[subQ1,subQ0]});Q498=makeQuery(id+"F0.imprint","IMPRINT",FACE,{"disambiguationData":[TD([[makeQuery(id+"F0.imprint","IMPRINT",EDGE,{"disambiguationData":[TD([[subQ2,1.0]])],"derivedFrom":subQ1}),-1.0]])]});}
            var Q499;
            {var subQ0=sQuery(id+"F0.wireOp",EDGE,"E3.0.1.223");var subQ1=sQuery(id+"F0.wireOp",EDGE,"E3.0.1.154");var subQ2=makeQuery(id+"F0.imprint","INTERSECT",VERTEX,{"derivedFrom":[subQ1,subQ0]});Q499=makeQuery(id+"F0.imprint","IMPRINT",FACE,{"disambiguationData":[TD([[makeQuery(id+"F0.imprint","IMPRINT",EDGE,{"disambiguationData":[TD([[subQ2,1.0]])],"derivedFrom":subQ1}),1.0]])]});}
            var Q500;
            {var subQ0=sQuery(id+"F0.wireOp",EDGE,"E3.0.1.155");var subQ1=sQuery(id+"F0.wireOp",EDGE,"E3.0.1.135");var subQ2=makeQuery(id+"F0.imprint","INTERSECT",VERTEX,{"derivedFrom":[subQ1,subQ0]});Q500=makeQuery(id+"F0.imprint","IMPRINT",FACE,{"disambiguationData":[TD([[makeQuery(id+"F0.imprint","IMPRINT",EDGE,{"disambiguationData":[TD([[subQ2,1.0]])],"derivedFrom":subQ1}),1.0]])]});}
            var Q501;
            {var subQ0=sQuery(id+"F0.wireOp",EDGE,"E3.0.1.197");var subQ1=sQuery(id+"F0.wireOp",EDGE,"E3.0.1.85");var subQ2=makeQuery(id+"F0.imprint","INTERSECT",VERTEX,{"derivedFrom":[subQ1,subQ0]});Q501=makeQuery(id+"F0.imprint","IMPRINT",FACE,{"disambiguationData":[TD([[makeQuery(id+"F0.imprint","IMPRINT",EDGE,{"disambiguationData":[TD([[subQ2,1.0]])],"derivedFrom":subQ1}),-1.0]])]});}
            var Q502;
            {var subQ0=sQuery(id+"F0.wireOp",EDGE,"E3.0.3.33");var subQ1=sQuery(id+"F0.wireOp",EDGE,"E3.0.3.23");var subQ2=makeQuery(id+"F0.imprint","INTERSECT",VERTEX,{"derivedFrom":[subQ1,subQ0]});Q502=makeQuery(id+"F0.imprint","IMPRINT",FACE,{"disambiguationData":[TD([[makeQuery(id+"F0.imprint","IMPRINT",EDGE,{"disambiguationData":[TD([[subQ2,1.0]])],"derivedFrom":subQ1}),-1.0]])]});}
            var Q503;
            {var subQ0=sQuery(id+"F0.wireOp",EDGE,"E3.0.3.223");var subQ1=sQuery(id+"F0.wireOp",EDGE,"E3.0.3.154");var subQ2=makeQuery(id+"F0.imprint","INTERSECT",VERTEX,{"derivedFrom":[subQ1,subQ0]});Q503=makeQuery(id+"F0.imprint","IMPRINT",FACE,{"disambiguationData":[TD([[makeQuery(id+"F0.imprint","IMPRINT",EDGE,{"disambiguationData":[TD([[subQ2,1.0]])],"derivedFrom":subQ1}),1.0]])]});}
            var Q504;
            {var subQ0=sQuery(id+"F0.wireOp",EDGE,"E3.0.3.155");var subQ1=sQuery(id+"F0.wireOp",EDGE,"E3.0.3.135");var subQ2=makeQuery(id+"F0.imprint","INTERSECT",VERTEX,{"derivedFrom":[subQ1,subQ0]});Q504=makeQuery(id+"F0.imprint","IMPRINT",FACE,{"disambiguationData":[TD([[makeQuery(id+"F0.imprint","IMPRINT",EDGE,{"disambiguationData":[TD([[subQ2,1.0]])],"derivedFrom":subQ1}),1.0]])]});}
            var Q505;
            {var subQ0=sQuery(id+"F0.wireOp",EDGE,"E3.0.3.197");var subQ1=sQuery(id+"F0.wireOp",EDGE,"E3.0.3.85");var subQ2=makeQuery(id+"F0.imprint","INTERSECT",VERTEX,{"derivedFrom":[subQ1,subQ0]});Q505=makeQuery(id+"F0.imprint","IMPRINT",FACE,{"disambiguationData":[TD([[makeQuery(id+"F0.imprint","IMPRINT",EDGE,{"disambiguationData":[TD([[subQ2,1.0]])],"derivedFrom":subQ1}),-1.0]])]});}
            var Q506;
            {var subQ0=sQuery(id+"F0.wireOp",EDGE,"E3.0.1.96");var subQ1=sQuery(id+"F0.wireOp",EDGE,"E3.0.1.26");var subQ2=makeQuery(id+"F0.imprint","INTERSECT",VERTEX,{"derivedFrom":[subQ1,subQ0]});Q506=makeQuery(id+"F0.imprint","IMPRINT",FACE,{"disambiguationData":[TD([[makeQuery(id+"F0.imprint","IMPRINT",EDGE,{"disambiguationData":[TD([[subQ2,1.0]])],"derivedFrom":subQ1}),-1.0]])]});}
            var Q507;
            {var subQ0=sQuery(id+"F0.wireOp",EDGE,"E3.0.3.96");var subQ1=sQuery(id+"F0.wireOp",EDGE,"E3.0.3.26");var subQ2=makeQuery(id+"F0.imprint","INTERSECT",VERTEX,{"derivedFrom":[subQ1,subQ0]});Q507=makeQuery(id+"F0.imprint","IMPRINT",FACE,{"disambiguationData":[TD([[makeQuery(id+"F0.imprint","IMPRINT",EDGE,{"disambiguationData":[TD([[subQ2,1.0]])],"derivedFrom":subQ1}),-1.0]])]});}
            var Q508;
            {var subQ0=sQuery(id+"F0.wireOp",EDGE,"E2.6.0.3");var subQ1=sQuery(id+"F0.wireOp",EDGE,"E2.6.0.0");var subQ2=makeQuery(id+"F0.imprint","INTERSECT",VERTEX,{"derivedFrom":[subQ1,subQ0]});Q508=makeQuery(id+"F0.imprint","IMPRINT",FACE,{"disambiguationData":[TD([[makeQuery(id+"F0.imprint","IMPRINT",EDGE,{"disambiguationData":[TD([[subQ2,1.0]])],"derivedFrom":subQ1}),1.0]])]});}
            var Q509;
            {var subQ0=sQuery(id+"F0.wireOp",EDGE,"E2.22.0.3");var subQ1=sQuery(id+"F0.wireOp",EDGE,"E2.22.0.0");var subQ2=makeQuery(id+"F0.imprint","INTERSECT",VERTEX,{"derivedFrom":[subQ1,subQ0]});Q509=makeQuery(id+"F0.imprint","IMPRINT",FACE,{"disambiguationData":[TD([[makeQuery(id+"F0.imprint","IMPRINT",EDGE,{"disambiguationData":[TD([[subQ2,1.0]])],"derivedFrom":subQ1}),1.0]])]});}
            var Q510;
            {var subQ0=sQuery(id+"F0.wireOp",EDGE,"E2.18.0.3");var subQ1=sQuery(id+"F0.wireOp",EDGE,"E2.18.0.0");var subQ2=makeQuery(id+"F0.imprint","INTERSECT",VERTEX,{"derivedFrom":[subQ1,subQ0]});Q510=makeQuery(id+"F0.imprint","IMPRINT",FACE,{"disambiguationData":[TD([[makeQuery(id+"F0.imprint","IMPRINT",EDGE,{"disambiguationData":[TD([[subQ2,1.0]])],"derivedFrom":subQ1}),1.0]])]});}
            var Q511;
            {var subQ0=sQuery(id+"F0.wireOp",EDGE,"E2.14.0.3");var subQ1=sQuery(id+"F0.wireOp",EDGE,"E2.14.0.0");var subQ2=makeQuery(id+"F0.imprint","INTERSECT",VERTEX,{"derivedFrom":[subQ1,subQ0]});Q511=makeQuery(id+"F0.imprint","IMPRINT",FACE,{"disambiguationData":[TD([[makeQuery(id+"F0.imprint","IMPRINT",EDGE,{"disambiguationData":[TD([[subQ2,1.0]])],"derivedFrom":subQ1}),1.0]])]});}
            var Q512;
            {var subQ0=sQuery(id+"F0.wireOp",EDGE,"E2.10.0.3");var subQ1=sQuery(id+"F0.wireOp",EDGE,"E2.10.0.0");var subQ2=makeQuery(id+"F0.imprint","INTERSECT",VERTEX,{"derivedFrom":[subQ1,subQ0]});Q512=makeQuery(id+"F0.imprint","IMPRINT",FACE,{"disambiguationData":[TD([[makeQuery(id+"F0.imprint","IMPRINT",EDGE,{"disambiguationData":[TD([[subQ2,1.0]])],"derivedFrom":subQ1}),1.0]])]});}
            var Q513;
            {var subQ0=sQuery(id+"F0.wireOp",EDGE,"E2.26.0.3");var subQ1=sQuery(id+"F0.wireOp",EDGE,"E2.26.0.0");var subQ2=makeQuery(id+"F0.imprint","INTERSECT",VERTEX,{"derivedFrom":[subQ1,subQ0]});Q513=makeQuery(id+"F0.imprint","IMPRINT",FACE,{"disambiguationData":[TD([[makeQuery(id+"F0.imprint","IMPRINT",EDGE,{"disambiguationData":[TD([[subQ2,1.0]])],"derivedFrom":subQ1}),1.0]])]});}
            var Q514;
            {var subQ0=sQuery(id+"F0.wireOp",EDGE,"E3.0.1.224");var subQ1=sQuery(id+"F0.wireOp",EDGE,"E3.0.1.157");var subQ2=makeQuery(id+"F0.imprint","INTERSECT",VERTEX,{"derivedFrom":[subQ1,subQ0]});Q514=makeQuery(id+"F0.imprint","IMPRINT",FACE,{"disambiguationData":[TD([[makeQuery(id+"F0.imprint","IMPRINT",EDGE,{"disambiguationData":[TD([[subQ2,1.0]])],"derivedFrom":subQ1}),1.0]])]});}
            var Q515;
            {var subQ0=sQuery(id+"F0.wireOp",EDGE,"E3.0.1.227");var subQ1=sQuery(id+"F0.wireOp",EDGE,"E3.0.1.137");var subQ2=makeQuery(id+"F0.imprint","INTERSECT",VERTEX,{"derivedFrom":[subQ1,subQ0]});Q515=makeQuery(id+"F0.imprint","IMPRINT",FACE,{"disambiguationData":[TD([[makeQuery(id+"F0.imprint","IMPRINT",EDGE,{"disambiguationData":[TD([[subQ2,1.0]])],"derivedFrom":subQ1}),1.0]])]});}
            var Q516;
            {var subQ0=sQuery(id+"F0.wireOp",EDGE,"E3.0.1.95");var subQ1=sQuery(id+"F0.wireOp",EDGE,"E3.0.1.84");var subQ2=makeQuery(id+"F0.imprint","INTERSECT",VERTEX,{"derivedFrom":[subQ1,subQ0]});Q516=makeQuery(id+"F0.imprint","IMPRINT",FACE,{"disambiguationData":[TD([[makeQuery(id+"F0.imprint","IMPRINT",EDGE,{"disambiguationData":[TD([[subQ2,1.0]])],"derivedFrom":subQ1}),-1.0]])]});}
            var Q517;
            {var subQ0=sQuery(id+"F0.wireOp",EDGE,"E3.0.2.128");var subQ1=sQuery(id+"F0.wireOp",EDGE,"E3.0.2.83");var subQ2=makeQuery(id+"F0.imprint","INTERSECT",VERTEX,{"derivedFrom":[subQ1,subQ0]});Q517=makeQuery(id+"F0.imprint","IMPRINT",FACE,{"disambiguationData":[TD([[makeQuery(id+"F0.imprint","IMPRINT",EDGE,{"disambiguationData":[TD([[subQ2,1.0]])],"derivedFrom":subQ1}),-1.0]])]});}
            var Q518;
            {var subQ0=sQuery(id+"F0.wireOp",EDGE,"E3.0.1.199");var subQ1=sQuery(id+"F0.wireOp",EDGE,"E3.0.1.185");var subQ2=makeQuery(id+"F0.imprint","INTERSECT",VERTEX,{"derivedFrom":[subQ1,subQ0]});Q518=makeQuery(id+"F0.imprint","IMPRINT",FACE,{"disambiguationData":[TD([[makeQuery(id+"F0.imprint","IMPRINT",EDGE,{"disambiguationData":[TD([[subQ2,1.0]])],"derivedFrom":subQ1}),-1.0]])]});}
            var Q519;
            {var subQ0=sQuery(id+"F0.wireOp",EDGE,"E3.0.3.224");var subQ1=sQuery(id+"F0.wireOp",EDGE,"E3.0.3.157");var subQ2=makeQuery(id+"F0.imprint","INTERSECT",VERTEX,{"derivedFrom":[subQ1,subQ0]});Q519=makeQuery(id+"F0.imprint","IMPRINT",FACE,{"disambiguationData":[TD([[makeQuery(id+"F0.imprint","IMPRINT",EDGE,{"disambiguationData":[TD([[subQ2,1.0]])],"derivedFrom":subQ1}),1.0]])]});}
            var Q520;
            {var subQ0=sQuery(id+"F0.wireOp",EDGE,"E3.0.3.227");var subQ1=sQuery(id+"F0.wireOp",EDGE,"E3.0.3.137");var subQ2=makeQuery(id+"F0.imprint","INTERSECT",VERTEX,{"derivedFrom":[subQ1,subQ0]});Q520=makeQuery(id+"F0.imprint","IMPRINT",FACE,{"disambiguationData":[TD([[makeQuery(id+"F0.imprint","IMPRINT",EDGE,{"disambiguationData":[TD([[subQ2,1.0]])],"derivedFrom":subQ1}),1.0]])]});}
            var Q521;
            {var subQ0=sQuery(id+"F0.wireOp",EDGE,"E3.0.3.95");var subQ1=sQuery(id+"F0.wireOp",EDGE,"E3.0.3.84");var subQ2=makeQuery(id+"F0.imprint","INTERSECT",VERTEX,{"derivedFrom":[subQ1,subQ0]});Q521=makeQuery(id+"F0.imprint","IMPRINT",FACE,{"disambiguationData":[TD([[makeQuery(id+"F0.imprint","IMPRINT",EDGE,{"disambiguationData":[TD([[subQ2,1.0]])],"derivedFrom":subQ1}),-1.0]])]});}
            var Q522;
            {var subQ0=sQuery(id+"F0.wireOp",EDGE,"E3.0.3.199");var subQ1=sQuery(id+"F0.wireOp",EDGE,"E3.0.3.185");var subQ2=makeQuery(id+"F0.imprint","INTERSECT",VERTEX,{"derivedFrom":[subQ1,subQ0]});Q522=makeQuery(id+"F0.imprint","IMPRINT",FACE,{"disambiguationData":[TD([[makeQuery(id+"F0.imprint","IMPRINT",EDGE,{"disambiguationData":[TD([[subQ2,1.0]])],"derivedFrom":subQ1}),-1.0]])]});}
            var Q523;
            {var subQ0=sQuery(id+"F0.wireOp",EDGE,"E3.0.1.97");var subQ1=sQuery(id+"F0.wireOp",EDGE,"E3.0.1.86");var subQ2=makeQuery(id+"F0.imprint","INTERSECT",VERTEX,{"derivedFrom":[subQ1,subQ0]});Q523=makeQuery(id+"F0.imprint","IMPRINT",FACE,{"disambiguationData":[TD([[makeQuery(id+"F0.imprint","IMPRINT",EDGE,{"disambiguationData":[TD([[subQ2,1.0]])],"derivedFrom":subQ1}),-1.0]])]});}
            var Q524;
            {var subQ0=sQuery(id+"F0.wireOp",EDGE,"E3.0.1.198");var subQ1=sQuery(id+"F0.wireOp",EDGE,"E3.0.1.186");var subQ2=makeQuery(id+"F0.imprint","INTERSECT",VERTEX,{"derivedFrom":[subQ1,subQ0]});Q524=makeQuery(id+"F0.imprint","IMPRINT",FACE,{"disambiguationData":[TD([[makeQuery(id+"F0.imprint","IMPRINT",EDGE,{"disambiguationData":[TD([[subQ2,1.0]])],"derivedFrom":subQ1}),-1.0]])]});}
            var Q525;
            {var subQ0=sQuery(id+"F0.wireOp",EDGE,"E3.0.3.97");var subQ1=sQuery(id+"F0.wireOp",EDGE,"E3.0.3.86");var subQ2=makeQuery(id+"F0.imprint","INTERSECT",VERTEX,{"derivedFrom":[subQ1,subQ0]});Q525=makeQuery(id+"F0.imprint","IMPRINT",FACE,{"disambiguationData":[TD([[makeQuery(id+"F0.imprint","IMPRINT",EDGE,{"disambiguationData":[TD([[subQ2,1.0]])],"derivedFrom":subQ1}),-1.0]])]});}
            var Q526;
            {var subQ0=sQuery(id+"F0.wireOp",EDGE,"E3.0.3.198");var subQ1=sQuery(id+"F0.wireOp",EDGE,"E3.0.3.186");var subQ2=makeQuery(id+"F0.imprint","INTERSECT",VERTEX,{"derivedFrom":[subQ1,subQ0]});Q526=makeQuery(id+"F0.imprint","IMPRINT",FACE,{"disambiguationData":[TD([[makeQuery(id+"F0.imprint","IMPRINT",EDGE,{"disambiguationData":[TD([[subQ2,1.0]])],"derivedFrom":subQ1}),-1.0]])]});}
            var Q527;
            {var subQ0=sQuery(id+"F0.wireOp",EDGE,"E3.0.1.156");var subQ1=sQuery(id+"F0.wireOp",EDGE,"E3.0.1.136");var subQ2=makeQuery(id+"F0.imprint","INTERSECT",VERTEX,{"derivedFrom":[subQ1,subQ0]});Q527=makeQuery(id+"F0.imprint","IMPRINT",FACE,{"disambiguationData":[TD([[makeQuery(id+"F0.imprint","IMPRINT",EDGE,{"disambiguationData":[TD([[subQ2,1.0]])],"derivedFrom":subQ1}),1.0]])]});}
            var Q528;
            {var subQ0=sQuery(id+"F0.wireOp",EDGE,"E3.0.2.130");var subQ1=sQuery(id+"F0.wireOp",EDGE,"E3.0.2.23");var subQ2=makeQuery(id+"F0.imprint","INTERSECT",VERTEX,{"derivedFrom":[subQ1,subQ0]});Q528=makeQuery(id+"F0.imprint","IMPRINT",FACE,{"disambiguationData":[TD([[makeQuery(id+"F0.imprint","IMPRINT",EDGE,{"disambiguationData":[TD([[subQ2,1.0]])],"derivedFrom":subQ1}),-1.0]])]});}
            var Q529;
            {var subQ0=sQuery(id+"F0.wireOp",EDGE,"E3.0.3.156");var subQ1=sQuery(id+"F0.wireOp",EDGE,"E3.0.3.136");var subQ2=makeQuery(id+"F0.imprint","INTERSECT",VERTEX,{"derivedFrom":[subQ1,subQ0]});Q529=makeQuery(id+"F0.imprint","IMPRINT",FACE,{"disambiguationData":[TD([[makeQuery(id+"F0.imprint","IMPRINT",EDGE,{"disambiguationData":[TD([[subQ2,1.0]])],"derivedFrom":subQ1}),1.0]])]});}
            var Q530;
            {var subQ0=sQuery(id+"F0.wireOp",EDGE,"E3.0.1.61");var subQ1=sQuery(id+"F0.wireOp",EDGE,"E3.0.1.7");var subQ2=makeQuery(id+"F0.imprint","INTERSECT",VERTEX,{"derivedFrom":[subQ1,subQ0]});Q530=makeQuery(id+"F0.imprint","IMPRINT",FACE,{"disambiguationData":[TD([[makeQuery(id+"F0.imprint","IMPRINT",EDGE,{"disambiguationData":[TD([[subQ2,1.0]])],"derivedFrom":subQ1}),1.0]])]});}
            var Q531;
            {var subQ0=sQuery(id+"F0.wireOp",EDGE,"E3.0.1.99");var subQ1=sQuery(id+"F0.wireOp",EDGE,"E3.0.1.88");var subQ2=makeQuery(id+"F0.imprint","INTERSECT",VERTEX,{"derivedFrom":[subQ1,subQ0]});Q531=makeQuery(id+"F0.imprint","IMPRINT",FACE,{"disambiguationData":[TD([[makeQuery(id+"F0.imprint","IMPRINT",EDGE,{"disambiguationData":[TD([[subQ2,1.0]])],"derivedFrom":subQ1}),-1.0]])]});}
            var Q532;
            {var subQ0=sQuery(id+"F0.wireOp",EDGE,"E3.0.1.203");var subQ1=sQuery(id+"F0.wireOp",EDGE,"E3.0.1.170");var subQ2=makeQuery(id+"F0.imprint","INTERSECT",VERTEX,{"derivedFrom":[subQ1,subQ0]});Q532=makeQuery(id+"F0.imprint","IMPRINT",FACE,{"disambiguationData":[TD([[makeQuery(id+"F0.imprint","IMPRINT",EDGE,{"disambiguationData":[TD([[subQ2,1.0]])],"derivedFrom":subQ1}),-1.0]])]});}
            var Q533;
            {var subQ0=sQuery(id+"F0.wireOp",EDGE,"E3.0.3.61");var subQ1=sQuery(id+"F0.wireOp",EDGE,"E3.0.3.7");var subQ2=makeQuery(id+"F0.imprint","INTERSECT",VERTEX,{"derivedFrom":[subQ1,subQ0]});Q533=makeQuery(id+"F0.imprint","IMPRINT",FACE,{"disambiguationData":[TD([[makeQuery(id+"F0.imprint","IMPRINT",EDGE,{"disambiguationData":[TD([[subQ2,1.0]])],"derivedFrom":subQ1}),1.0]])]});}
            var Q534;
            {var subQ0=sQuery(id+"F0.wireOp",EDGE,"E3.0.3.203");var subQ1=sQuery(id+"F0.wireOp",EDGE,"E3.0.3.170");var subQ2=makeQuery(id+"F0.imprint","INTERSECT",VERTEX,{"derivedFrom":[subQ1,subQ0]});Q534=makeQuery(id+"F0.imprint","IMPRINT",FACE,{"disambiguationData":[TD([[makeQuery(id+"F0.imprint","IMPRINT",EDGE,{"disambiguationData":[TD([[subQ2,1.0]])],"derivedFrom":subQ1}),-1.0]])]});}
            var Q535;
            {var subQ0=sQuery(id+"F0.wireOp",EDGE,"E3.0.1.158");var subQ1=sQuery(id+"F0.wireOp",EDGE,"E3.0.1.138");var subQ2=makeQuery(id+"F0.imprint","INTERSECT",VERTEX,{"derivedFrom":[subQ1,subQ0]});Q535=makeQuery(id+"F0.imprint","IMPRINT",FACE,{"disambiguationData":[TD([[makeQuery(id+"F0.imprint","IMPRINT",EDGE,{"disambiguationData":[TD([[subQ2,1.0]])],"derivedFrom":subQ1}),1.0]])]});}
            var Q536;
            {var subQ0=sQuery(id+"F0.wireOp",EDGE,"E3.0.1.100");var subQ1=sQuery(id+"F0.wireOp",EDGE,"E3.0.1.89");var subQ2=makeQuery(id+"F0.imprint","INTERSECT",VERTEX,{"derivedFrom":[subQ1,subQ0]});Q536=makeQuery(id+"F0.imprint","IMPRINT",FACE,{"disambiguationData":[TD([[makeQuery(id+"F0.imprint","IMPRINT",EDGE,{"disambiguationData":[TD([[subQ2,1.0]])],"derivedFrom":subQ1}),-1.0]])]});}
            var Q537;
            {var subQ0=sQuery(id+"F0.wireOp",EDGE,"E3.0.3.100");var subQ1=sQuery(id+"F0.wireOp",EDGE,"E3.0.3.89");var subQ2=makeQuery(id+"F0.imprint","INTERSECT",VERTEX,{"derivedFrom":[subQ1,subQ0]});Q537=makeQuery(id+"F0.imprint","IMPRINT",FACE,{"disambiguationData":[TD([[makeQuery(id+"F0.imprint","IMPRINT",EDGE,{"disambiguationData":[TD([[subQ2,1.0]])],"derivedFrom":subQ1}),-1.0]])]});}
            var Q538;
            {var subQ0=sQuery(id+"F0.wireOp",EDGE,"E3.0.3.158");var subQ1=sQuery(id+"F0.wireOp",EDGE,"E3.0.3.138");var subQ2=makeQuery(id+"F0.imprint","INTERSECT",VERTEX,{"derivedFrom":[subQ1,subQ0]});Q538=makeQuery(id+"F0.imprint","IMPRINT",FACE,{"disambiguationData":[TD([[makeQuery(id+"F0.imprint","IMPRINT",EDGE,{"disambiguationData":[TD([[subQ2,1.0]])],"derivedFrom":subQ1}),1.0]])]});}
            var Q539;
            {var subQ0=sQuery(id+"F0.wireOp",EDGE,"E2.15.0.3");var subQ1=sQuery(id+"F0.wireOp",EDGE,"E2.15.0.0");var subQ2=makeQuery(id+"F0.imprint","INTERSECT",VERTEX,{"derivedFrom":[subQ1,subQ0]});Q539=makeQuery(id+"F0.imprint","IMPRINT",FACE,{"disambiguationData":[TD([[makeQuery(id+"F0.imprint","IMPRINT",EDGE,{"disambiguationData":[TD([[subQ2,1.0]])],"derivedFrom":subQ1}),1.0]])]});}
            var Q540;
            {var subQ0=sQuery(id+"F0.wireOp",EDGE,"E2.11.0.3");var subQ1=sQuery(id+"F0.wireOp",EDGE,"E2.11.0.0");var subQ2=makeQuery(id+"F0.imprint","INTERSECT",VERTEX,{"derivedFrom":[subQ1,subQ0]});Q540=makeQuery(id+"F0.imprint","IMPRINT",FACE,{"disambiguationData":[TD([[makeQuery(id+"F0.imprint","IMPRINT",EDGE,{"disambiguationData":[TD([[subQ2,1.0]])],"derivedFrom":subQ1}),1.0]])]});}
            var Q541;
            {var subQ0=sQuery(id+"F0.wireOp",EDGE,"E2.7.0.3");var subQ1=sQuery(id+"F0.wireOp",EDGE,"E2.7.0.0");var subQ2=makeQuery(id+"F0.imprint","INTERSECT",VERTEX,{"derivedFrom":[subQ1,subQ0]});Q541=makeQuery(id+"F0.imprint","IMPRINT",FACE,{"disambiguationData":[TD([[makeQuery(id+"F0.imprint","IMPRINT",EDGE,{"disambiguationData":[TD([[subQ2,1.0]])],"derivedFrom":subQ1}),1.0]])]});}
            var Q542;
            {var subQ0=sQuery(id+"F0.wireOp",EDGE,"E2.3.0.3");var subQ1=sQuery(id+"F0.wireOp",EDGE,"E2.3.0.0");var subQ2=makeQuery(id+"F0.imprint","INTERSECT",VERTEX,{"derivedFrom":[subQ1,subQ0]});Q542=makeQuery(id+"F0.imprint","IMPRINT",FACE,{"disambiguationData":[TD([[makeQuery(id+"F0.imprint","IMPRINT",EDGE,{"disambiguationData":[TD([[subQ2,1.0]])],"derivedFrom":subQ1}),1.0]])]});}
            var Q543;
            {var subQ0=sQuery(id+"F0.wireOp",EDGE,"E2.27.0.3");var subQ1=sQuery(id+"F0.wireOp",EDGE,"E2.27.0.0");var subQ2=makeQuery(id+"F0.imprint","INTERSECT",VERTEX,{"derivedFrom":[subQ1,subQ0]});Q543=makeQuery(id+"F0.imprint","IMPRINT",FACE,{"disambiguationData":[TD([[makeQuery(id+"F0.imprint","IMPRINT",EDGE,{"disambiguationData":[TD([[subQ2,1.0]])],"derivedFrom":subQ1}),1.0]])]});}
            var Q544;
            {var subQ0=sQuery(id+"F0.wireOp",EDGE,"E2.23.0.3");var subQ1=sQuery(id+"F0.wireOp",EDGE,"E2.23.0.0");var subQ2=makeQuery(id+"F0.imprint","INTERSECT",VERTEX,{"derivedFrom":[subQ1,subQ0]});Q544=makeQuery(id+"F0.imprint","IMPRINT",FACE,{"disambiguationData":[TD([[makeQuery(id+"F0.imprint","IMPRINT",EDGE,{"disambiguationData":[TD([[subQ2,1.0]])],"derivedFrom":subQ1}),1.0]])]});}
            var Q545;
            {var subQ0=sQuery(id+"F0.wireOp",EDGE,"E2.19.0.3");var subQ1=sQuery(id+"F0.wireOp",EDGE,"E2.19.0.0");var subQ2=makeQuery(id+"F0.imprint","INTERSECT",VERTEX,{"derivedFrom":[subQ1,subQ0]});Q545=makeQuery(id+"F0.imprint","IMPRINT",FACE,{"disambiguationData":[TD([[makeQuery(id+"F0.imprint","IMPRINT",EDGE,{"disambiguationData":[TD([[subQ2,1.0]])],"derivedFrom":subQ1}),1.0]])]});}
            var Q546;
            {var subQ0=sQuery(id+"F0.wireOp",EDGE,"E3.0.1.206");var subQ1=sQuery(id+"F0.wireOp",EDGE,"E3.0.1.171");var subQ2=makeQuery(id+"F0.imprint","INTERSECT",VERTEX,{"derivedFrom":[subQ1,subQ0]});Q546=makeQuery(id+"F0.imprint","IMPRINT",FACE,{"disambiguationData":[TD([[makeQuery(id+"F0.imprint","IMPRINT",EDGE,{"disambiguationData":[TD([[subQ2,1.0]])],"derivedFrom":subQ1}),-1.0]])]});}
            var Q547;
            {var subQ0=sQuery(id+"F0.wireOp",EDGE,"E3.0.3.217");var subQ1=sQuery(id+"F0.wireOp",EDGE,"E3.0.3.82");var subQ2=makeQuery(id+"F0.imprint","INTERSECT",VERTEX,{"derivedFrom":[subQ1,subQ0]});Q547=makeQuery(id+"F0.imprint","IMPRINT",FACE,{"disambiguationData":[TD([[makeQuery(id+"F0.imprint","IMPRINT",EDGE,{"disambiguationData":[TD([[subQ2,1.0]])],"derivedFrom":subQ1}),-1.0]])]});}
            var Q548;
            {var subQ0=sQuery(id+"F0.wireOp",EDGE,"E3.0.3.41");var subQ1=sQuery(id+"F0.wireOp",EDGE,"E3.0.3.16");var subQ2=makeQuery(id+"F0.imprint","INTERSECT",VERTEX,{"derivedFrom":[subQ1,subQ0]});Q548=makeQuery(id+"F0.imprint","IMPRINT",FACE,{"disambiguationData":[TD([[makeQuery(id+"F0.imprint","IMPRINT",EDGE,{"disambiguationData":[TD([[subQ2,1.0]])],"derivedFrom":subQ1}),-1.0]])]});}
            var Q549;
            {var subQ0=sQuery(id+"F0.wireOp",EDGE,"E3.0.3.206");var subQ1=sQuery(id+"F0.wireOp",EDGE,"E3.0.3.171");var subQ2=makeQuery(id+"F0.imprint","INTERSECT",VERTEX,{"derivedFrom":[subQ1,subQ0]});Q549=makeQuery(id+"F0.imprint","IMPRINT",FACE,{"disambiguationData":[TD([[makeQuery(id+"F0.imprint","IMPRINT",EDGE,{"disambiguationData":[TD([[subQ2,1.0]])],"derivedFrom":subQ1}),-1.0]])]});}
            var Q550;
            {var subQ0=sQuery(id+"F0.wireOp",EDGE,"E3.0.1.41");var subQ1=sQuery(id+"F0.wireOp",EDGE,"E3.0.1.16");var subQ2=makeQuery(id+"F0.imprint","INTERSECT",VERTEX,{"derivedFrom":[subQ1,subQ0]});Q550=makeQuery(id+"F0.imprint","IMPRINT",FACE,{"disambiguationData":[TD([[makeQuery(id+"F0.imprint","IMPRINT",EDGE,{"disambiguationData":[TD([[subQ2,1.0]])],"derivedFrom":subQ1}),-1.0]])]});}
            var Q551;
            {var subQ0=sQuery(id+"F0.wireOp",EDGE,"E3.0.1.217");var subQ1=sQuery(id+"F0.wireOp",EDGE,"E3.0.1.82");var subQ2=makeQuery(id+"F0.imprint","INTERSECT",VERTEX,{"derivedFrom":[subQ1,subQ0]});Q551=makeQuery(id+"F0.imprint","IMPRINT",FACE,{"disambiguationData":[TD([[makeQuery(id+"F0.imprint","IMPRINT",EDGE,{"disambiguationData":[TD([[subQ2,1.0]])],"derivedFrom":subQ1}),-1.0]])]});}
            var Q552;
            {var subQ0=sQuery(id+"F0.wireOp",EDGE,"E3.0.3.159");var subQ1=sQuery(id+"F0.wireOp",EDGE,"E3.0.3.139");var subQ2=makeQuery(id+"F0.imprint","INTERSECT",VERTEX,{"derivedFrom":[subQ1,subQ0]});Q552=makeQuery(id+"F0.imprint","IMPRINT",FACE,{"disambiguationData":[TD([[makeQuery(id+"F0.imprint","IMPRINT",EDGE,{"disambiguationData":[TD([[subQ2,1.0]])],"derivedFrom":subQ1}),1.0]])]});}
            var Q553;
            {var subQ0=sQuery(id+"F0.wireOp",EDGE,"E3.0.1.159");var subQ1=sQuery(id+"F0.wireOp",EDGE,"E3.0.1.139");var subQ2=makeQuery(id+"F0.imprint","INTERSECT",VERTEX,{"derivedFrom":[subQ1,subQ0]});Q553=makeQuery(id+"F0.imprint","IMPRINT",FACE,{"disambiguationData":[TD([[makeQuery(id+"F0.imprint","IMPRINT",EDGE,{"disambiguationData":[TD([[subQ2,1.0]])],"derivedFrom":subQ1}),1.0]])]});}
            var Q554;
            {var subQ0=sQuery(id+"F0.wireOp",EDGE,"E3.0.1.196");var subQ1=sQuery(id+"F0.wireOp",EDGE,"E3.0.1.101");var subQ2=makeQuery(id+"F0.imprint","INTERSECT",VERTEX,{"derivedFrom":[subQ1,subQ0]});Q554=makeQuery(id+"F0.imprint","IMPRINT",FACE,{"disambiguationData":[TD([[makeQuery(id+"F0.imprint","IMPRINT",EDGE,{"disambiguationData":[TD([[subQ2,1.0]])],"derivedFrom":subQ1}),-1.0]])]});}
            var Q555;
            {var subQ0=sQuery(id+"F0.wireOp",EDGE,"E3.0.3.102");var subQ1=sQuery(id+"F0.wireOp",EDGE,"E3.0.3.81");var subQ2=makeQuery(id+"F0.imprint","INTERSECT",VERTEX,{"derivedFrom":[subQ1,subQ0]});Q555=makeQuery(id+"F0.imprint","IMPRINT",FACE,{"disambiguationData":[TD([[makeQuery(id+"F0.imprint","IMPRINT",EDGE,{"disambiguationData":[TD([[subQ2,1.0]])],"derivedFrom":subQ1}),-1.0]])]});}
            var Q556;
            {var subQ0=sQuery(id+"F0.wireOp",EDGE,"E3.0.1.239");var subQ1=sQuery(id+"F0.wireOp",EDGE,"E3.0.1.19");var subQ2=makeQuery(id+"F0.imprint","INTERSECT",VERTEX,{"derivedFrom":[subQ1,subQ0]});Q556=makeQuery(id+"F0.imprint","IMPRINT",FACE,{"disambiguationData":[TD([[makeQuery(id+"F0.imprint","IMPRINT",EDGE,{"disambiguationData":[TD([[subQ2,1.0]])],"derivedFrom":subQ1}),-1.0]])]});}
            var Q557;
            {var subQ0=sQuery(id+"F0.wireOp",EDGE,"E3.0.1.102");var subQ1=sQuery(id+"F0.wireOp",EDGE,"E3.0.1.81");var subQ2=makeQuery(id+"F0.imprint","INTERSECT",VERTEX,{"derivedFrom":[subQ1,subQ0]});Q557=makeQuery(id+"F0.imprint","IMPRINT",FACE,{"disambiguationData":[TD([[makeQuery(id+"F0.imprint","IMPRINT",EDGE,{"disambiguationData":[TD([[subQ2,1.0]])],"derivedFrom":subQ1}),-1.0]])]});}
            var Q558;
            {var subQ0=sQuery(id+"F0.wireOp",EDGE,"E3.0.3.225");var subQ1=sQuery(id+"F0.wireOp",EDGE,"E3.0.3.132");var subQ2=makeQuery(id+"F0.imprint","INTERSECT",VERTEX,{"derivedFrom":[subQ1,subQ0]});Q558=makeQuery(id+"F0.imprint","IMPRINT",FACE,{"disambiguationData":[TD([[makeQuery(id+"F0.imprint","IMPRINT",EDGE,{"disambiguationData":[TD([[subQ2,1.0]])],"derivedFrom":subQ1}),1.0]])]});}
            var Q559;
            {var subQ0=sQuery(id+"F0.wireOp",EDGE,"E3.0.3.128");var subQ1=sQuery(id+"F0.wireOp",EDGE,"E3.0.3.83");var subQ2=makeQuery(id+"F0.imprint","INTERSECT",VERTEX,{"derivedFrom":[subQ1,subQ0]});Q559=makeQuery(id+"F0.imprint","IMPRINT",FACE,{"disambiguationData":[TD([[makeQuery(id+"F0.imprint","IMPRINT",EDGE,{"disambiguationData":[TD([[subQ2,1.0]])],"derivedFrom":subQ1}),-1.0]])]});}
            var Q560;
            {var subQ0=sQuery(id+"F0.wireOp",EDGE,"E3.0.3.160");var subQ1=sQuery(id+"F0.wireOp",EDGE,"E3.0.3.141");var subQ2=makeQuery(id+"F0.imprint","INTERSECT",VERTEX,{"derivedFrom":[subQ1,subQ0]});Q560=makeQuery(id+"F0.imprint","IMPRINT",FACE,{"disambiguationData":[TD([[makeQuery(id+"F0.imprint","IMPRINT",EDGE,{"disambiguationData":[TD([[subQ2,1.0]])],"derivedFrom":subQ1}),1.0]])]});}
            var Q561;
            {var subQ0=sQuery(id+"F0.wireOp",EDGE,"E2.16.0.3");var subQ1=sQuery(id+"F0.wireOp",EDGE,"E2.16.0.0");var subQ2=makeQuery(id+"F0.imprint","INTERSECT",VERTEX,{"derivedFrom":[subQ1,subQ0]});Q561=makeQuery(id+"F0.imprint","IMPRINT",FACE,{"disambiguationData":[TD([[makeQuery(id+"F0.imprint","IMPRINT",EDGE,{"disambiguationData":[TD([[subQ2,1.0]])],"derivedFrom":subQ1}),1.0]])]});}
            var Q562;
            {var subQ0=sQuery(id+"F0.wireOp",EDGE,"E2.12.0.3");var subQ1=sQuery(id+"F0.wireOp",EDGE,"E2.12.0.0");var subQ2=makeQuery(id+"F0.imprint","INTERSECT",VERTEX,{"derivedFrom":[subQ1,subQ0]});Q562=makeQuery(id+"F0.imprint","IMPRINT",FACE,{"disambiguationData":[TD([[makeQuery(id+"F0.imprint","IMPRINT",EDGE,{"disambiguationData":[TD([[subQ2,1.0]])],"derivedFrom":subQ1}),1.0]])]});}
            var Q563;
            {var subQ0=sQuery(id+"F0.wireOp",EDGE,"E2.8.0.3");var subQ1=sQuery(id+"F0.wireOp",EDGE,"E2.8.0.0");var subQ2=makeQuery(id+"F0.imprint","INTERSECT",VERTEX,{"derivedFrom":[subQ1,subQ0]});Q563=makeQuery(id+"F0.imprint","IMPRINT",FACE,{"disambiguationData":[TD([[makeQuery(id+"F0.imprint","IMPRINT",EDGE,{"disambiguationData":[TD([[subQ2,1.0]])],"derivedFrom":subQ1}),1.0]])]});}
            var Q564;
            {var subQ0=sQuery(id+"F0.wireOp",EDGE,"E2.4.0.3");var subQ1=sQuery(id+"F0.wireOp",EDGE,"E2.4.0.0");var subQ2=makeQuery(id+"F0.imprint","INTERSECT",VERTEX,{"derivedFrom":[subQ1,subQ0]});Q564=makeQuery(id+"F0.imprint","IMPRINT",FACE,{"disambiguationData":[TD([[makeQuery(id+"F0.imprint","IMPRINT",EDGE,{"disambiguationData":[TD([[subQ2,1.0]])],"derivedFrom":subQ1}),1.0]])]});}
            var Q565;
            {var subQ0=sQuery(id+"F0.wireOp",EDGE,"E2.28.0.3");var subQ1=sQuery(id+"F0.wireOp",EDGE,"E2.28.0.0");var subQ2=makeQuery(id+"F0.imprint","INTERSECT",VERTEX,{"derivedFrom":[subQ1,subQ0]});Q565=makeQuery(id+"F0.imprint","IMPRINT",FACE,{"disambiguationData":[TD([[makeQuery(id+"F0.imprint","IMPRINT",EDGE,{"disambiguationData":[TD([[subQ2,1.0]])],"derivedFrom":subQ1}),1.0]])]});}
            var Q566;
            {var subQ0=sQuery(id+"F0.wireOp",EDGE,"E2.24.0.3");var subQ1=sQuery(id+"F0.wireOp",EDGE,"E2.24.0.0");var subQ2=makeQuery(id+"F0.imprint","INTERSECT",VERTEX,{"derivedFrom":[subQ1,subQ0]});Q566=makeQuery(id+"F0.imprint","IMPRINT",FACE,{"disambiguationData":[TD([[makeQuery(id+"F0.imprint","IMPRINT",EDGE,{"disambiguationData":[TD([[subQ2,1.0]])],"derivedFrom":subQ1}),1.0]])]});}
            var Q567;
            {var subQ0=sQuery(id+"F0.wireOp",EDGE,"E2.20.0.3");var subQ1=sQuery(id+"F0.wireOp",EDGE,"E2.20.0.0");var subQ2=makeQuery(id+"F0.imprint","INTERSECT",VERTEX,{"derivedFrom":[subQ1,subQ0]});Q567=makeQuery(id+"F0.imprint","IMPRINT",FACE,{"disambiguationData":[TD([[makeQuery(id+"F0.imprint","IMPRINT",EDGE,{"disambiguationData":[TD([[subQ2,1.0]])],"derivedFrom":subQ1}),1.0]])]});}
            var Q568;
            {var subQ0=sQuery(id+"F0.wireOp",EDGE,"E3.0.1.160");var subQ1=sQuery(id+"F0.wireOp",EDGE,"E3.0.1.141");var subQ2=makeQuery(id+"F0.imprint","INTERSECT",VERTEX,{"derivedFrom":[subQ1,subQ0]});Q568=makeQuery(id+"F0.imprint","IMPRINT",FACE,{"disambiguationData":[TD([[makeQuery(id+"F0.imprint","IMPRINT",EDGE,{"disambiguationData":[TD([[subQ2,1.0]])],"derivedFrom":subQ1}),1.0]])]});}
            var Q569;
            {var subQ0=sQuery(id+"F0.wireOp",EDGE,"E3.0.1.128");var subQ1=sQuery(id+"F0.wireOp",EDGE,"E3.0.1.83");var subQ2=makeQuery(id+"F0.imprint","INTERSECT",VERTEX,{"derivedFrom":[subQ1,subQ0]});Q569=makeQuery(id+"F0.imprint","IMPRINT",FACE,{"disambiguationData":[TD([[makeQuery(id+"F0.imprint","IMPRINT",EDGE,{"disambiguationData":[TD([[subQ2,1.0]])],"derivedFrom":subQ1}),-1.0]])]});}
            extrude(context, id + "F1", {"entities" : qUnion([Q0, Q1, Q2, Q3, Q4, Q5, Q6, Q7, Q8, Q9, Q10, Q11, Q12, Q13, Q14, Q15, Q16, Q17, Q18, Q19, Q20, Q21, Q22, Q23, Q24, Q25, Q26, Q27, Q28, Q29, Q30, Q31, Q32, Q33, Q34, Q35, Q36, Q37, Q38, Q39, Q40, Q41, Q42, Q43, Q44, Q45, Q46, Q47, Q48, Q49, Q50, Q51, Q52, Q53, Q54, Q55, Q56, Q57, Q58, Q59, Q60, Q61, Q62, Q63, Q64, Q65, Q66, Q67, Q68, Q69, Q70, Q71, Q72, Q73, Q74, Q75, Q76, Q77, Q78, Q79, Q80, Q81, Q82, Q83, Q84, Q85, Q86, Q87, Q88, Q89, Q90, Q91, Q92, Q93, Q94, Q95, Q96, Q97, Q98, Q99, Q100, Q101, Q102, Q103, Q104, Q105, Q106, Q107, Q108, Q109, Q110, Q111, Q112, Q113, Q114, Q115, Q116, Q117, Q118, Q119, Q120, Q121, Q122, Q123, Q124, Q125, Q126, Q127, Q128, Q129, Q130, Q131, Q132, Q133, Q134, Q135, Q136, Q137, Q138, Q139, Q140, Q141, Q142, Q143, Q144, Q145, Q146, Q147, Q148, Q149, Q150, Q151, Q152, Q153, Q154, Q155, Q156, Q157, Q158, Q159, Q160, Q161, Q162, Q163, Q164, Q165, Q166, Q167, Q168, Q169, Q170, Q171, Q172, Q173, Q174, Q175, Q176, Q177, Q178, Q179, Q180, Q181, Q182, Q183, Q184, Q185, Q186, Q187, Q188, Q189, Q190, Q191, Q192, Q193, Q194, Q195, Q196, Q197, Q198, Q199, Q200, Q201, Q202, Q203, Q204, Q205, Q206, Q207, Q208, Q209, Q210, Q211, Q212, Q213, Q214, Q215, Q216, Q217, Q218, Q219, Q220, Q221, Q222, Q223, Q224, Q225, Q226, Q227, Q228, Q229, Q230, Q231, Q232, Q233, Q234, Q235, Q236, Q237, Q238, Q239, Q240, Q241, Q242, Q243, Q244, Q245, Q246, Q247, Q248, Q249, Q250, Q251, Q252, Q253, Q254, Q255, Q256, Q257, Q258, Q259, Q260, Q261, Q262, Q263, Q264, Q265, Q266, Q267, Q268, Q269, Q270, Q271, Q272, Q273, Q274, Q275, Q276, Q277, Q278, Q279, Q280, Q281, Q282, Q283, Q284, Q285, Q286, Q287, Q288, Q289, Q290, Q291, Q292, Q293, Q294, Q295, Q296, Q297, Q298, Q299, Q300, Q301, Q302, Q303, Q304, Q305, Q306, Q307, Q308, Q309, Q310, Q311, Q312, Q313, Q314, Q315, Q316, Q317, Q318, Q319, Q320, Q321, Q322, Q323, Q324, Q325, Q326, Q327, Q328, Q329, Q330, Q331, Q332, Q333, Q334, Q335, Q336, Q337, Q338, Q339, Q340, Q341, Q342, Q343, Q344, Q345, Q346, Q347, Q348, Q349, Q350, Q351, Q352, Q353, Q354, Q355, Q356, Q357, Q358, Q359, Q360, Q361, Q362, Q363, Q364, Q365, Q366, Q367, Q368, Q369, Q370, Q371, Q372, Q373, Q374, Q375, Q376, Q377, Q378, Q379, Q380, Q381, Q382, Q383, Q384, Q385, Q386, Q387, Q388, Q389, Q390, Q391, Q392, Q393, Q394, Q395, Q396, Q397, Q398, Q399, Q400, Q401, Q402, Q403, Q404, Q405, Q406, Q407, Q408, Q409, Q410, Q411, Q412, Q413, Q414, Q415, Q416, Q417, Q418, Q419, Q420, Q421, Q422, Q423, Q424, Q425, Q426, Q427, Q428, Q429, Q430, Q431, Q432, Q433, Q434, Q435, Q436, Q437, Q438, Q439, Q440, Q441, Q442, Q443, Q444, Q445, Q446, Q447, Q448, Q449, Q450, Q451, Q452, Q453, Q454, Q455, Q456, Q457, Q458, Q459, Q460, Q461, Q462, Q463, Q464, Q465, Q466, Q467, Q468, Q469, Q470, Q471, Q472, Q473, Q474, Q475, Q476, Q477, Q478, Q479, Q480, Q481, Q482, Q483, Q484, Q485, Q486, Q487, Q488, Q489, Q490, Q491, Q492, Q493, Q494, Q495, Q496, Q497, Q498, Q499, Q500, Q501, Q502, Q503, Q504, Q505, Q506, Q507, Q508, Q509, Q510, Q511, Q512, Q513, Q514, Q515, Q516, Q517, Q518, Q519, Q520, Q521, Q522, Q523, Q524, Q525, Q526, Q527, Q528, Q529, Q530, Q531, Q532, Q533, Q534, Q535, Q536, Q537, Q538, Q539, Q540, Q541, Q542, Q543, Q544, Q545, Q546, Q547, Q548, Q549, Q550, Q551, Q552, Q553, Q554, Q555, Q556, Q557, Q558, Q559, Q560, Q561, Q562, Q563, Q564, Q565, Q566, Q567, Q568, Q569]), "depth" : 0.5 * mm, "offsetDistance" : 25 * mm});
        }
    });
